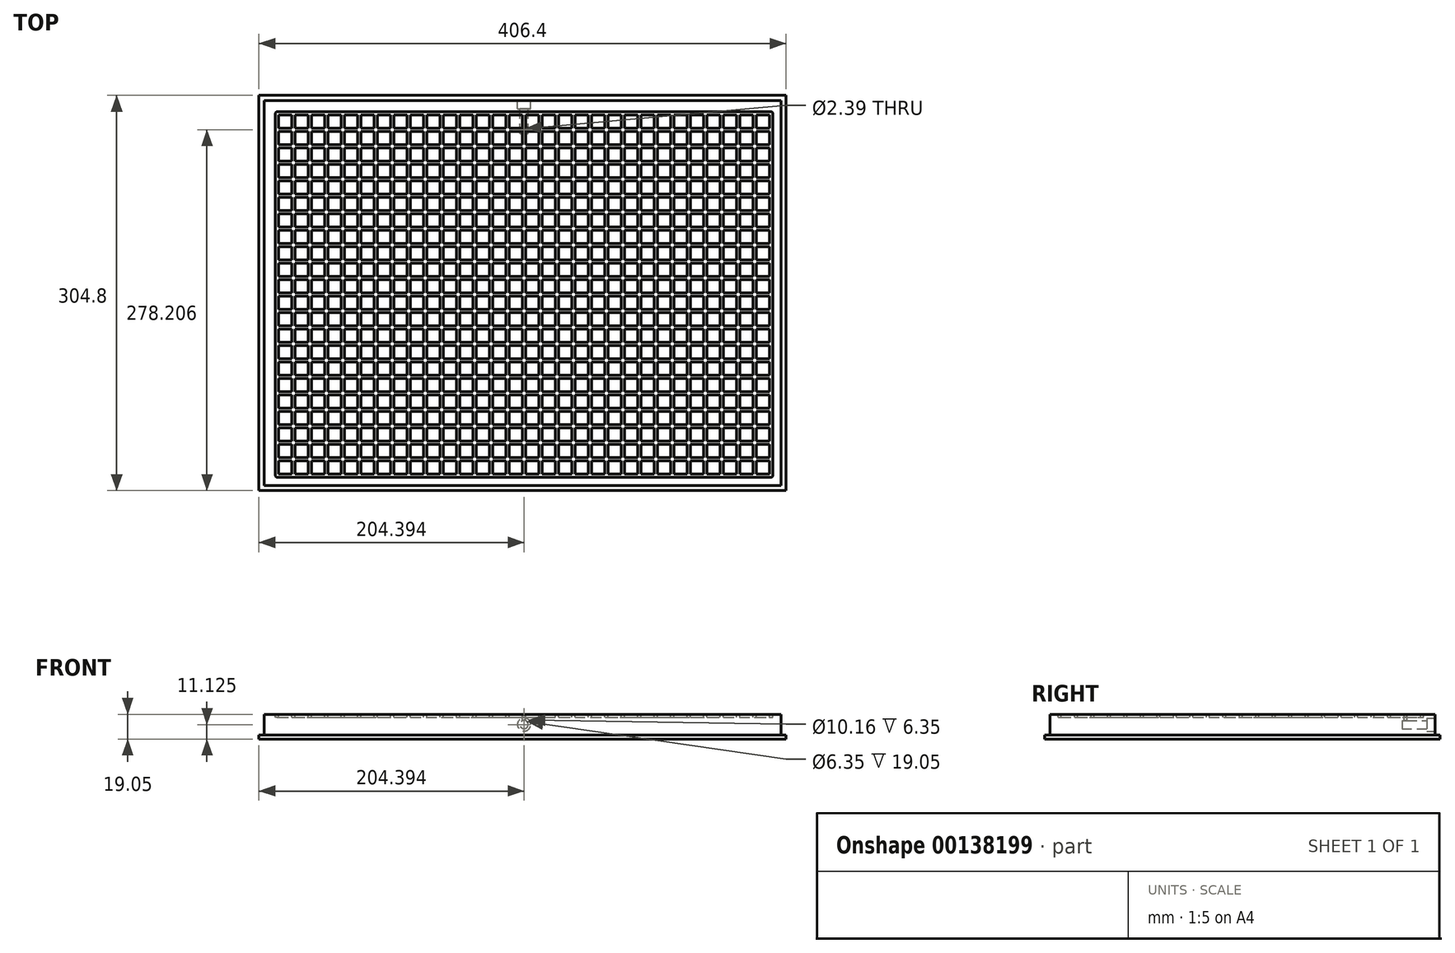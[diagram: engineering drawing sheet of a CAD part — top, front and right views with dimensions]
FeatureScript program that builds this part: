
annotation { "Feature Type Name" : "Feature", "Feature Type Description" : "" }
export const myFeature = defineFeature(function(context is Context, id is Id, definition is map)
    precondition{}
    {
        {
            var Q0;
            Q0=qCreatedBy(makeId("Top.planeOp"),FACE);
            var sketch = newSketch(context, id + "F0", { "sketchPlane" : qUnion([Q0])});
            skLineSegment(sketch, "E0.bottom", {"start": v(0, 0) * mm, "end": v(406.4, 0) * mm});
            skLineSegment(sketch, "E0.top", {"start": v(0, 304.8) * mm, "end": v(406.4, 304.8) * mm});
            skLineSegment(sketch, "E0.left", {"start": v(0, 0) * mm, "end": v(0, 304.8) * mm});
            skLineSegment(sketch, "E0.right", {"start": v(406.4, 0) * mm, "end": v(406.4, 304.8) * mm});
            skSolve(sketch);
        }
        {
            var Q0;
            Q0 = qSketchRegion(id + "F0", true);
            extrude(context, id + "F1", {"entities" : qUnion([Q0]), "depth" : 19.05 * mm});
        }
        {
            var Q0;
            Q0=makeQuery(id+"F1.opExtrude","CAP_FACE",FACE,{"disambiguationData":[OSD([sQuery(id+"F0.wireOp",EDGE,"E0.bottom"),sQuery(id+"F0.wireOp",EDGE,"E0.top"),sQuery(id+"F0.wireOp",EDGE,"E0.left"),sQuery(id+"F0.wireOp",EDGE,"E0.right")])],"isStart":false});
            var sketch = newSketch(context, id + "F2", { "sketchPlane" : qUnion([Q0])});
            skLineSegment(sketch, "E1.bottom", {"start": v(13.9, 10.31) * mm, "end": v(394.9, 10.31) * mm});
            skLineSegment(sketch, "E1.top", {"start": v(13.9, 292.1) * mm, "end": v(394.9, 292.1) * mm});
            skLineSegment(sketch, "E1.left", {"start": v(12.7, 11.5) * mm, "end": v(12.7, 290.9) * mm});
            skLineSegment(sketch, "E1.right", {"start": v(396.09, 11.5) * mm, "end": v(396.09, 290.9) * mm});
            skLineSegment(sketch, "E2.bottom", {"start": v(15.09, 12.7) * mm, "end": v(25.4, 12.7) * mm});
            skLineSegment(sketch, "E2.top", {"start": v(15.09, 23.01) * mm, "end": v(25.4, 23.01) * mm});
            skLineSegment(sketch, "E2.left", {"start": v(15.09, 12.7) * mm, "end": v(15.09, 23.01) * mm});
            skLineSegment(sketch, "E2.right", {"start": v(25.4, 12.7) * mm, "end": v(25.4, 23.01) * mm});
            skLineSegment(sketch, "E3.0.1.0", {"start": v(15.09, 25.4) * mm, "end": v(15.09, 35.71) * mm});
            skLineSegment(sketch, "E3.0.1.1", {"start": v(15.09, 35.71) * mm, "end": v(25.4, 35.71) * mm});
            skLineSegment(sketch, "E3.0.1.2", {"start": v(15.09, 25.4) * mm, "end": v(25.4, 25.4) * mm});
            skLineSegment(sketch, "E3.0.1.3", {"start": v(25.4, 25.4) * mm, "end": v(25.4, 35.71) * mm});
            skLineSegment(sketch, "E3.0.2.0", {"start": v(15.09, 38.1) * mm, "end": v(15.09, 48.41) * mm});
            skLineSegment(sketch, "E3.0.2.1", {"start": v(15.09, 48.41) * mm, "end": v(25.4, 48.41) * mm});
            skLineSegment(sketch, "E3.0.2.2", {"start": v(15.09, 38.1) * mm, "end": v(25.4, 38.1) * mm});
            skLineSegment(sketch, "E3.0.2.3", {"start": v(25.4, 38.1) * mm, "end": v(25.4, 48.41) * mm});
            skLineSegment(sketch, "E3.0.3.0", {"start": v(15.09, 50.8) * mm, "end": v(15.09, 61.11) * mm});
            skLineSegment(sketch, "E3.0.3.1", {"start": v(15.09, 61.11) * mm, "end": v(25.4, 61.11) * mm});
            skLineSegment(sketch, "E3.0.3.2", {"start": v(15.09, 50.8) * mm, "end": v(25.4, 50.8) * mm});
            skLineSegment(sketch, "E3.0.3.3", {"start": v(25.4, 50.8) * mm, "end": v(25.4, 61.11) * mm});
            skLineSegment(sketch, "E3.0.4.0", {"start": v(15.09, 63.5) * mm, "end": v(15.09, 73.81) * mm});
            skLineSegment(sketch, "E3.0.4.1", {"start": v(15.09, 73.81) * mm, "end": v(25.4, 73.81) * mm});
            skLineSegment(sketch, "E3.0.4.2", {"start": v(15.09, 63.5) * mm, "end": v(25.4, 63.5) * mm});
            skLineSegment(sketch, "E3.0.4.3", {"start": v(25.4, 63.5) * mm, "end": v(25.4, 73.81) * mm});
            skLineSegment(sketch, "E3.0.5.0", {"start": v(15.09, 76.2) * mm, "end": v(15.09, 86.51) * mm});
            skLineSegment(sketch, "E3.0.5.1", {"start": v(15.09, 86.51) * mm, "end": v(25.4, 86.51) * mm});
            skLineSegment(sketch, "E3.0.5.2", {"start": v(15.09, 76.2) * mm, "end": v(25.4, 76.2) * mm});
            skLineSegment(sketch, "E3.0.5.3", {"start": v(25.4, 76.2) * mm, "end": v(25.4, 86.51) * mm});
            skLineSegment(sketch, "E3.0.6.0", {"start": v(15.09, 88.9) * mm, "end": v(15.09, 99.21) * mm});
            skLineSegment(sketch, "E3.0.6.1", {"start": v(15.09, 99.21) * mm, "end": v(25.4, 99.21) * mm});
            skLineSegment(sketch, "E3.0.6.2", {"start": v(15.09, 88.9) * mm, "end": v(25.4, 88.9) * mm});
            skLineSegment(sketch, "E3.0.6.3", {"start": v(25.4, 88.9) * mm, "end": v(25.4, 99.21) * mm});
            skLineSegment(sketch, "E3.0.7.0", {"start": v(15.09, 101.6) * mm, "end": v(15.09, 111.91) * mm});
            skLineSegment(sketch, "E3.0.7.1", {"start": v(15.09, 111.91) * mm, "end": v(25.4, 111.91) * mm});
            skLineSegment(sketch, "E3.0.7.2", {"start": v(15.09, 101.6) * mm, "end": v(25.4, 101.6) * mm});
            skLineSegment(sketch, "E3.0.7.3", {"start": v(25.4, 101.6) * mm, "end": v(25.4, 111.91) * mm});
            skLineSegment(sketch, "E3.0.8.0", {"start": v(15.09, 114.3) * mm, "end": v(15.09, 124.61) * mm});
            skLineSegment(sketch, "E3.0.8.1", {"start": v(15.09, 124.61) * mm, "end": v(25.4, 124.61) * mm});
            skLineSegment(sketch, "E3.0.8.2", {"start": v(15.09, 114.3) * mm, "end": v(25.4, 114.3) * mm});
            skLineSegment(sketch, "E3.0.8.3", {"start": v(25.4, 114.3) * mm, "end": v(25.4, 124.61) * mm});
            skLineSegment(sketch, "E3.0.9.0", {"start": v(15.09, 127) * mm, "end": v(15.09, 137.31) * mm});
            skLineSegment(sketch, "E3.0.9.1", {"start": v(15.09, 137.31) * mm, "end": v(25.4, 137.31) * mm});
            skLineSegment(sketch, "E3.0.9.2", {"start": v(15.09, 127) * mm, "end": v(25.4, 127) * mm});
            skLineSegment(sketch, "E3.0.9.3", {"start": v(25.4, 127) * mm, "end": v(25.4, 137.31) * mm});
            skLineSegment(sketch, "E3.0.10.0", {"start": v(15.09, 139.7) * mm, "end": v(15.09, 150.01) * mm});
            skLineSegment(sketch, "E3.0.10.1", {"start": v(15.09, 150.01) * mm, "end": v(25.4, 150.01) * mm});
            skLineSegment(sketch, "E3.0.10.2", {"start": v(15.09, 139.7) * mm, "end": v(25.4, 139.7) * mm});
            skLineSegment(sketch, "E3.0.10.3", {"start": v(25.4, 139.7) * mm, "end": v(25.4, 150.01) * mm});
            skLineSegment(sketch, "E3.0.11.0", {"start": v(15.09, 152.4) * mm, "end": v(15.09, 162.71) * mm});
            skLineSegment(sketch, "E3.0.11.1", {"start": v(15.09, 162.71) * mm, "end": v(25.4, 162.71) * mm});
            skLineSegment(sketch, "E3.0.11.2", {"start": v(15.09, 152.4) * mm, "end": v(25.4, 152.4) * mm});
            skLineSegment(sketch, "E3.0.11.3", {"start": v(25.4, 152.4) * mm, "end": v(25.4, 162.71) * mm});
            skLineSegment(sketch, "E3.0.12.0", {"start": v(15.09, 165.1) * mm, "end": v(15.09, 175.41) * mm});
            skLineSegment(sketch, "E3.0.12.1", {"start": v(15.09, 175.41) * mm, "end": v(25.4, 175.41) * mm});
            skLineSegment(sketch, "E3.0.12.2", {"start": v(15.09, 165.1) * mm, "end": v(25.4, 165.1) * mm});
            skLineSegment(sketch, "E3.0.12.3", {"start": v(25.4, 165.1) * mm, "end": v(25.4, 175.41) * mm});
            skLineSegment(sketch, "E3.0.13.0", {"start": v(15.09, 177.8) * mm, "end": v(15.09, 188.11) * mm});
            skLineSegment(sketch, "E3.0.13.1", {"start": v(15.09, 188.11) * mm, "end": v(25.4, 188.11) * mm});
            skLineSegment(sketch, "E3.0.13.2", {"start": v(15.09, 177.8) * mm, "end": v(25.4, 177.8) * mm});
            skLineSegment(sketch, "E3.0.13.3", {"start": v(25.4, 177.8) * mm, "end": v(25.4, 188.11) * mm});
            skLineSegment(sketch, "E3.0.14.0", {"start": v(15.09, 190.5) * mm, "end": v(15.09, 200.81) * mm});
            skLineSegment(sketch, "E3.0.14.1", {"start": v(15.09, 200.81) * mm, "end": v(25.4, 200.81) * mm});
            skLineSegment(sketch, "E3.0.14.2", {"start": v(15.09, 190.5) * mm, "end": v(25.4, 190.5) * mm});
            skLineSegment(sketch, "E3.0.14.3", {"start": v(25.4, 190.5) * mm, "end": v(25.4, 200.81) * mm});
            skLineSegment(sketch, "E3.0.15.0", {"start": v(15.09, 203.2) * mm, "end": v(15.09, 213.51) * mm});
            skLineSegment(sketch, "E3.0.15.1", {"start": v(15.09, 213.51) * mm, "end": v(25.4, 213.51) * mm});
            skLineSegment(sketch, "E3.0.15.2", {"start": v(15.09, 203.2) * mm, "end": v(25.4, 203.2) * mm});
            skLineSegment(sketch, "E3.0.15.3", {"start": v(25.4, 203.2) * mm, "end": v(25.4, 213.51) * mm});
            skLineSegment(sketch, "E3.0.16.0", {"start": v(15.09, 215.9) * mm, "end": v(15.09, 226.21) * mm});
            skLineSegment(sketch, "E3.0.16.1", {"start": v(15.09, 226.21) * mm, "end": v(25.4, 226.21) * mm});
            skLineSegment(sketch, "E3.0.16.2", {"start": v(15.09, 215.9) * mm, "end": v(25.4, 215.9) * mm});
            skLineSegment(sketch, "E3.0.16.3", {"start": v(25.4, 215.9) * mm, "end": v(25.4, 226.21) * mm});
            skLineSegment(sketch, "E3.0.17.0", {"start": v(15.09, 228.6) * mm, "end": v(15.09, 238.91) * mm});
            skLineSegment(sketch, "E3.0.17.1", {"start": v(15.09, 238.91) * mm, "end": v(25.4, 238.91) * mm});
            skLineSegment(sketch, "E3.0.17.2", {"start": v(15.09, 228.6) * mm, "end": v(25.4, 228.6) * mm});
            skLineSegment(sketch, "E3.0.17.3", {"start": v(25.4, 228.6) * mm, "end": v(25.4, 238.91) * mm});
            skLineSegment(sketch, "E3.0.18.0", {"start": v(15.09, 241.3) * mm, "end": v(15.09, 251.61) * mm});
            skLineSegment(sketch, "E3.0.18.1", {"start": v(15.09, 251.61) * mm, "end": v(25.4, 251.61) * mm});
            skLineSegment(sketch, "E3.0.18.2", {"start": v(15.09, 241.3) * mm, "end": v(25.4, 241.3) * mm});
            skLineSegment(sketch, "E3.0.18.3", {"start": v(25.4, 241.3) * mm, "end": v(25.4, 251.61) * mm});
            skLineSegment(sketch, "E3.0.19.0", {"start": v(15.09, 254) * mm, "end": v(15.09, 264.31) * mm});
            skLineSegment(sketch, "E3.0.19.1", {"start": v(15.09, 264.31) * mm, "end": v(25.4, 264.31) * mm});
            skLineSegment(sketch, "E3.0.19.2", {"start": v(15.09, 254) * mm, "end": v(25.4, 254) * mm});
            skLineSegment(sketch, "E3.0.19.3", {"start": v(25.4, 254) * mm, "end": v(25.4, 264.31) * mm});
            skLineSegment(sketch, "E3.0.20.0", {"start": v(15.09, 266.7) * mm, "end": v(15.09, 277.01) * mm});
            skLineSegment(sketch, "E3.0.20.1", {"start": v(15.09, 277.01) * mm, "end": v(25.4, 277.01) * mm});
            skLineSegment(sketch, "E3.0.20.2", {"start": v(15.09, 266.7) * mm, "end": v(25.4, 266.7) * mm});
            skLineSegment(sketch, "E3.0.20.3", {"start": v(25.4, 266.7) * mm, "end": v(25.4, 277.01) * mm});
            skLineSegment(sketch, "E3.0.21.0", {"start": v(15.09, 279.4) * mm, "end": v(15.09, 289.71) * mm});
            skLineSegment(sketch, "E3.0.21.1", {"start": v(15.09, 289.71) * mm, "end": v(25.4, 289.71) * mm});
            skLineSegment(sketch, "E3.0.21.2", {"start": v(15.09, 279.4) * mm, "end": v(25.4, 279.4) * mm});
            skLineSegment(sketch, "E3.0.21.3", {"start": v(25.4, 279.4) * mm, "end": v(25.4, 289.71) * mm});
            skLineSegment(sketch, "E3.1.0.0", {"start": v(27.79, 12.7) * mm, "end": v(27.79, 23.01) * mm});
            skLineSegment(sketch, "E3.1.0.1", {"start": v(27.79, 23.01) * mm, "end": v(38.1, 23.01) * mm});
            skLineSegment(sketch, "E3.1.0.2", {"start": v(27.79, 12.7) * mm, "end": v(38.1, 12.7) * mm});
            skLineSegment(sketch, "E3.1.0.3", {"start": v(38.1, 12.7) * mm, "end": v(38.1, 23.01) * mm});
            skLineSegment(sketch, "E3.1.1.0", {"start": v(27.79, 25.4) * mm, "end": v(27.79, 35.71) * mm});
            skLineSegment(sketch, "E3.1.1.1", {"start": v(27.79, 35.71) * mm, "end": v(38.1, 35.71) * mm});
            skLineSegment(sketch, "E3.1.1.2", {"start": v(27.79, 25.4) * mm, "end": v(38.1, 25.4) * mm});
            skLineSegment(sketch, "E3.1.1.3", {"start": v(38.1, 25.4) * mm, "end": v(38.1, 35.71) * mm});
            skLineSegment(sketch, "E3.1.2.0", {"start": v(27.79, 38.1) * mm, "end": v(27.79, 48.41) * mm});
            skLineSegment(sketch, "E3.1.2.1", {"start": v(27.79, 48.41) * mm, "end": v(38.1, 48.41) * mm});
            skLineSegment(sketch, "E3.1.2.2", {"start": v(27.79, 38.1) * mm, "end": v(38.1, 38.1) * mm});
            skLineSegment(sketch, "E3.1.2.3", {"start": v(38.1, 38.1) * mm, "end": v(38.1, 48.41) * mm});
            skLineSegment(sketch, "E3.1.3.0", {"start": v(27.79, 50.8) * mm, "end": v(27.79, 61.11) * mm});
            skLineSegment(sketch, "E3.1.3.1", {"start": v(27.79, 61.11) * mm, "end": v(38.1, 61.11) * mm});
            skLineSegment(sketch, "E3.1.3.2", {"start": v(27.79, 50.8) * mm, "end": v(38.1, 50.8) * mm});
            skLineSegment(sketch, "E3.1.3.3", {"start": v(38.1, 50.8) * mm, "end": v(38.1, 61.11) * mm});
            skLineSegment(sketch, "E3.1.4.0", {"start": v(27.79, 63.5) * mm, "end": v(27.79, 73.81) * mm});
            skLineSegment(sketch, "E3.1.4.1", {"start": v(27.79, 73.81) * mm, "end": v(38.1, 73.81) * mm});
            skLineSegment(sketch, "E3.1.4.2", {"start": v(27.79, 63.5) * mm, "end": v(38.1, 63.5) * mm});
            skLineSegment(sketch, "E3.1.4.3", {"start": v(38.1, 63.5) * mm, "end": v(38.1, 73.81) * mm});
            skLineSegment(sketch, "E3.1.5.0", {"start": v(27.79, 76.2) * mm, "end": v(27.79, 86.51) * mm});
            skLineSegment(sketch, "E3.1.5.1", {"start": v(27.79, 86.51) * mm, "end": v(38.1, 86.51) * mm});
            skLineSegment(sketch, "E3.1.5.2", {"start": v(27.79, 76.2) * mm, "end": v(38.1, 76.2) * mm});
            skLineSegment(sketch, "E3.1.5.3", {"start": v(38.1, 76.2) * mm, "end": v(38.1, 86.51) * mm});
            skLineSegment(sketch, "E3.1.6.0", {"start": v(27.79, 88.9) * mm, "end": v(27.79, 99.21) * mm});
            skLineSegment(sketch, "E3.1.6.1", {"start": v(27.79, 99.21) * mm, "end": v(38.1, 99.21) * mm});
            skLineSegment(sketch, "E3.1.6.2", {"start": v(27.79, 88.9) * mm, "end": v(38.1, 88.9) * mm});
            skLineSegment(sketch, "E3.1.6.3", {"start": v(38.1, 88.9) * mm, "end": v(38.1, 99.21) * mm});
            skLineSegment(sketch, "E3.1.7.0", {"start": v(27.79, 101.6) * mm, "end": v(27.79, 111.91) * mm});
            skLineSegment(sketch, "E3.1.7.1", {"start": v(27.79, 111.91) * mm, "end": v(38.1, 111.91) * mm});
            skLineSegment(sketch, "E3.1.7.2", {"start": v(27.79, 101.6) * mm, "end": v(38.1, 101.6) * mm});
            skLineSegment(sketch, "E3.1.7.3", {"start": v(38.1, 101.6) * mm, "end": v(38.1, 111.91) * mm});
            skLineSegment(sketch, "E3.1.8.0", {"start": v(27.79, 114.3) * mm, "end": v(27.79, 124.61) * mm});
            skLineSegment(sketch, "E3.1.8.1", {"start": v(27.79, 124.61) * mm, "end": v(38.1, 124.61) * mm});
            skLineSegment(sketch, "E3.1.8.2", {"start": v(27.79, 114.3) * mm, "end": v(38.1, 114.3) * mm});
            skLineSegment(sketch, "E3.1.8.3", {"start": v(38.1, 114.3) * mm, "end": v(38.1, 124.61) * mm});
            skLineSegment(sketch, "E3.1.9.0", {"start": v(27.79, 127) * mm, "end": v(27.79, 137.31) * mm});
            skLineSegment(sketch, "E3.1.9.1", {"start": v(27.79, 137.31) * mm, "end": v(38.1, 137.31) * mm});
            skLineSegment(sketch, "E3.1.9.2", {"start": v(27.79, 127) * mm, "end": v(38.1, 127) * mm});
            skLineSegment(sketch, "E3.1.9.3", {"start": v(38.1, 127) * mm, "end": v(38.1, 137.31) * mm});
            skLineSegment(sketch, "E3.1.10.0", {"start": v(27.79, 139.7) * mm, "end": v(27.79, 150.01) * mm});
            skLineSegment(sketch, "E3.1.10.1", {"start": v(27.79, 150.01) * mm, "end": v(38.1, 150.01) * mm});
            skLineSegment(sketch, "E3.1.10.2", {"start": v(27.79, 139.7) * mm, "end": v(38.1, 139.7) * mm});
            skLineSegment(sketch, "E3.1.10.3", {"start": v(38.1, 139.7) * mm, "end": v(38.1, 150.01) * mm});
            skLineSegment(sketch, "E3.1.11.0", {"start": v(27.79, 152.4) * mm, "end": v(27.79, 162.71) * mm});
            skLineSegment(sketch, "E3.1.11.1", {"start": v(27.79, 162.71) * mm, "end": v(38.1, 162.71) * mm});
            skLineSegment(sketch, "E3.1.11.2", {"start": v(27.79, 152.4) * mm, "end": v(38.1, 152.4) * mm});
            skLineSegment(sketch, "E3.1.11.3", {"start": v(38.1, 152.4) * mm, "end": v(38.1, 162.71) * mm});
            skLineSegment(sketch, "E3.1.12.0", {"start": v(27.79, 165.1) * mm, "end": v(27.79, 175.41) * mm});
            skLineSegment(sketch, "E3.1.12.1", {"start": v(27.79, 175.41) * mm, "end": v(38.1, 175.41) * mm});
            skLineSegment(sketch, "E3.1.12.2", {"start": v(27.79, 165.1) * mm, "end": v(38.1, 165.1) * mm});
            skLineSegment(sketch, "E3.1.12.3", {"start": v(38.1, 165.1) * mm, "end": v(38.1, 175.41) * mm});
            skLineSegment(sketch, "E3.1.13.0", {"start": v(27.79, 177.8) * mm, "end": v(27.79, 188.11) * mm});
            skLineSegment(sketch, "E3.1.13.1", {"start": v(27.79, 188.11) * mm, "end": v(38.1, 188.11) * mm});
            skLineSegment(sketch, "E3.1.13.2", {"start": v(27.79, 177.8) * mm, "end": v(38.1, 177.8) * mm});
            skLineSegment(sketch, "E3.1.13.3", {"start": v(38.1, 177.8) * mm, "end": v(38.1, 188.11) * mm});
            skLineSegment(sketch, "E3.1.14.0", {"start": v(27.79, 190.5) * mm, "end": v(27.79, 200.81) * mm});
            skLineSegment(sketch, "E3.1.14.1", {"start": v(27.79, 200.81) * mm, "end": v(38.1, 200.81) * mm});
            skLineSegment(sketch, "E3.1.14.2", {"start": v(27.79, 190.5) * mm, "end": v(38.1, 190.5) * mm});
            skLineSegment(sketch, "E3.1.14.3", {"start": v(38.1, 190.5) * mm, "end": v(38.1, 200.81) * mm});
            skLineSegment(sketch, "E3.1.15.0", {"start": v(27.79, 203.2) * mm, "end": v(27.79, 213.51) * mm});
            skLineSegment(sketch, "E3.1.15.1", {"start": v(27.79, 213.51) * mm, "end": v(38.1, 213.51) * mm});
            skLineSegment(sketch, "E3.1.15.2", {"start": v(27.79, 203.2) * mm, "end": v(38.1, 203.2) * mm});
            skLineSegment(sketch, "E3.1.15.3", {"start": v(38.1, 203.2) * mm, "end": v(38.1, 213.51) * mm});
            skLineSegment(sketch, "E3.1.16.0", {"start": v(27.79, 215.9) * mm, "end": v(27.79, 226.21) * mm});
            skLineSegment(sketch, "E3.1.16.1", {"start": v(27.79, 226.21) * mm, "end": v(38.1, 226.21) * mm});
            skLineSegment(sketch, "E3.1.16.2", {"start": v(27.79, 215.9) * mm, "end": v(38.1, 215.9) * mm});
            skLineSegment(sketch, "E3.1.16.3", {"start": v(38.1, 215.9) * mm, "end": v(38.1, 226.21) * mm});
            skLineSegment(sketch, "E3.1.17.0", {"start": v(27.79, 228.6) * mm, "end": v(27.79, 238.91) * mm});
            skLineSegment(sketch, "E3.1.17.1", {"start": v(27.79, 238.91) * mm, "end": v(38.1, 238.91) * mm});
            skLineSegment(sketch, "E3.1.17.2", {"start": v(27.79, 228.6) * mm, "end": v(38.1, 228.6) * mm});
            skLineSegment(sketch, "E3.1.17.3", {"start": v(38.1, 228.6) * mm, "end": v(38.1, 238.91) * mm});
            skLineSegment(sketch, "E3.1.18.0", {"start": v(27.79, 241.3) * mm, "end": v(27.79, 251.61) * mm});
            skLineSegment(sketch, "E3.1.18.1", {"start": v(27.79, 251.61) * mm, "end": v(38.1, 251.61) * mm});
            skLineSegment(sketch, "E3.1.18.2", {"start": v(27.79, 241.3) * mm, "end": v(38.1, 241.3) * mm});
            skLineSegment(sketch, "E3.1.18.3", {"start": v(38.1, 241.3) * mm, "end": v(38.1, 251.61) * mm});
            skLineSegment(sketch, "E3.1.19.0", {"start": v(27.79, 254) * mm, "end": v(27.79, 264.31) * mm});
            skLineSegment(sketch, "E3.1.19.1", {"start": v(27.79, 264.31) * mm, "end": v(38.1, 264.31) * mm});
            skLineSegment(sketch, "E3.1.19.2", {"start": v(27.79, 254) * mm, "end": v(38.1, 254) * mm});
            skLineSegment(sketch, "E3.1.19.3", {"start": v(38.1, 254) * mm, "end": v(38.1, 264.31) * mm});
            skLineSegment(sketch, "E3.1.20.0", {"start": v(27.79, 266.7) * mm, "end": v(27.79, 277.01) * mm});
            skLineSegment(sketch, "E3.1.20.1", {"start": v(27.79, 277.01) * mm, "end": v(38.1, 277.01) * mm});
            skLineSegment(sketch, "E3.1.20.2", {"start": v(27.79, 266.7) * mm, "end": v(38.1, 266.7) * mm});
            skLineSegment(sketch, "E3.1.20.3", {"start": v(38.1, 266.7) * mm, "end": v(38.1, 277.01) * mm});
            skLineSegment(sketch, "E3.1.21.0", {"start": v(27.79, 279.4) * mm, "end": v(27.79, 289.71) * mm});
            skLineSegment(sketch, "E3.1.21.1", {"start": v(27.79, 289.71) * mm, "end": v(38.1, 289.71) * mm});
            skLineSegment(sketch, "E3.1.21.2", {"start": v(27.79, 279.4) * mm, "end": v(38.1, 279.4) * mm});
            skLineSegment(sketch, "E3.1.21.3", {"start": v(38.1, 279.4) * mm, "end": v(38.1, 289.71) * mm});
            skLineSegment(sketch, "E3.2.0.0", {"start": v(40.49, 12.7) * mm, "end": v(40.49, 23.01) * mm});
            skLineSegment(sketch, "E3.2.0.1", {"start": v(40.49, 23.01) * mm, "end": v(50.8, 23.01) * mm});
            skLineSegment(sketch, "E3.2.0.2", {"start": v(40.49, 12.7) * mm, "end": v(50.8, 12.7) * mm});
            skLineSegment(sketch, "E3.2.0.3", {"start": v(50.8, 12.7) * mm, "end": v(50.8, 23.01) * mm});
            skLineSegment(sketch, "E3.2.1.0", {"start": v(40.49, 25.4) * mm, "end": v(40.49, 35.71) * mm});
            skLineSegment(sketch, "E3.2.1.1", {"start": v(40.49, 35.71) * mm, "end": v(50.8, 35.71) * mm});
            skLineSegment(sketch, "E3.2.1.2", {"start": v(40.49, 25.4) * mm, "end": v(50.8, 25.4) * mm});
            skLineSegment(sketch, "E3.2.1.3", {"start": v(50.8, 25.4) * mm, "end": v(50.8, 35.71) * mm});
            skLineSegment(sketch, "E3.2.2.0", {"start": v(40.49, 38.1) * mm, "end": v(40.49, 48.41) * mm});
            skLineSegment(sketch, "E3.2.2.1", {"start": v(40.49, 48.41) * mm, "end": v(50.8, 48.41) * mm});
            skLineSegment(sketch, "E3.2.2.2", {"start": v(40.49, 38.1) * mm, "end": v(50.8, 38.1) * mm});
            skLineSegment(sketch, "E3.2.2.3", {"start": v(50.8, 38.1) * mm, "end": v(50.8, 48.41) * mm});
            skLineSegment(sketch, "E3.2.3.0", {"start": v(40.49, 50.8) * mm, "end": v(40.49, 61.11) * mm});
            skLineSegment(sketch, "E3.2.3.1", {"start": v(40.49, 61.11) * mm, "end": v(50.8, 61.11) * mm});
            skLineSegment(sketch, "E3.2.3.2", {"start": v(40.49, 50.8) * mm, "end": v(50.8, 50.8) * mm});
            skLineSegment(sketch, "E3.2.3.3", {"start": v(50.8, 50.8) * mm, "end": v(50.8, 61.11) * mm});
            skLineSegment(sketch, "E3.2.4.0", {"start": v(40.49, 63.5) * mm, "end": v(40.49, 73.81) * mm});
            skLineSegment(sketch, "E3.2.4.1", {"start": v(40.49, 73.81) * mm, "end": v(50.8, 73.81) * mm});
            skLineSegment(sketch, "E3.2.4.2", {"start": v(40.49, 63.5) * mm, "end": v(50.8, 63.5) * mm});
            skLineSegment(sketch, "E3.2.4.3", {"start": v(50.8, 63.5) * mm, "end": v(50.8, 73.81) * mm});
            skLineSegment(sketch, "E3.2.5.0", {"start": v(40.49, 76.2) * mm, "end": v(40.49, 86.51) * mm});
            skLineSegment(sketch, "E3.2.5.1", {"start": v(40.49, 86.51) * mm, "end": v(50.8, 86.51) * mm});
            skLineSegment(sketch, "E3.2.5.2", {"start": v(40.49, 76.2) * mm, "end": v(50.8, 76.2) * mm});
            skLineSegment(sketch, "E3.2.5.3", {"start": v(50.8, 76.2) * mm, "end": v(50.8, 86.51) * mm});
            skLineSegment(sketch, "E3.2.6.0", {"start": v(40.49, 88.9) * mm, "end": v(40.49, 99.21) * mm});
            skLineSegment(sketch, "E3.2.6.1", {"start": v(40.49, 99.21) * mm, "end": v(50.8, 99.21) * mm});
            skLineSegment(sketch, "E3.2.6.2", {"start": v(40.49, 88.9) * mm, "end": v(50.8, 88.9) * mm});
            skLineSegment(sketch, "E3.2.6.3", {"start": v(50.8, 88.9) * mm, "end": v(50.8, 99.21) * mm});
            skLineSegment(sketch, "E3.2.7.0", {"start": v(40.49, 101.6) * mm, "end": v(40.49, 111.91) * mm});
            skLineSegment(sketch, "E3.2.7.1", {"start": v(40.49, 111.91) * mm, "end": v(50.8, 111.91) * mm});
            skLineSegment(sketch, "E3.2.7.2", {"start": v(40.49, 101.6) * mm, "end": v(50.8, 101.6) * mm});
            skLineSegment(sketch, "E3.2.7.3", {"start": v(50.8, 101.6) * mm, "end": v(50.8, 111.91) * mm});
            skLineSegment(sketch, "E3.2.8.0", {"start": v(40.49, 114.3) * mm, "end": v(40.49, 124.61) * mm});
            skLineSegment(sketch, "E3.2.8.1", {"start": v(40.49, 124.61) * mm, "end": v(50.8, 124.61) * mm});
            skLineSegment(sketch, "E3.2.8.2", {"start": v(40.49, 114.3) * mm, "end": v(50.8, 114.3) * mm});
            skLineSegment(sketch, "E3.2.8.3", {"start": v(50.8, 114.3) * mm, "end": v(50.8, 124.61) * mm});
            skLineSegment(sketch, "E3.2.9.0", {"start": v(40.49, 127) * mm, "end": v(40.49, 137.31) * mm});
            skLineSegment(sketch, "E3.2.9.1", {"start": v(40.49, 137.31) * mm, "end": v(50.8, 137.31) * mm});
            skLineSegment(sketch, "E3.2.9.2", {"start": v(40.49, 127) * mm, "end": v(50.8, 127) * mm});
            skLineSegment(sketch, "E3.2.9.3", {"start": v(50.8, 127) * mm, "end": v(50.8, 137.31) * mm});
            skLineSegment(sketch, "E3.2.10.0", {"start": v(40.49, 139.7) * mm, "end": v(40.49, 150.01) * mm});
            skLineSegment(sketch, "E3.2.10.1", {"start": v(40.49, 150.01) * mm, "end": v(50.8, 150.01) * mm});
            skLineSegment(sketch, "E3.2.10.2", {"start": v(40.49, 139.7) * mm, "end": v(50.8, 139.7) * mm});
            skLineSegment(sketch, "E3.2.10.3", {"start": v(50.8, 139.7) * mm, "end": v(50.8, 150.01) * mm});
            skLineSegment(sketch, "E3.2.11.0", {"start": v(40.49, 152.4) * mm, "end": v(40.49, 162.71) * mm});
            skLineSegment(sketch, "E3.2.11.1", {"start": v(40.49, 162.71) * mm, "end": v(50.8, 162.71) * mm});
            skLineSegment(sketch, "E3.2.11.2", {"start": v(40.49, 152.4) * mm, "end": v(50.8, 152.4) * mm});
            skLineSegment(sketch, "E3.2.11.3", {"start": v(50.8, 152.4) * mm, "end": v(50.8, 162.71) * mm});
            skLineSegment(sketch, "E3.2.12.0", {"start": v(40.49, 165.1) * mm, "end": v(40.49, 175.41) * mm});
            skLineSegment(sketch, "E3.2.12.1", {"start": v(40.49, 175.41) * mm, "end": v(50.8, 175.41) * mm});
            skLineSegment(sketch, "E3.2.12.2", {"start": v(40.49, 165.1) * mm, "end": v(50.8, 165.1) * mm});
            skLineSegment(sketch, "E3.2.12.3", {"start": v(50.8, 165.1) * mm, "end": v(50.8, 175.41) * mm});
            skLineSegment(sketch, "E3.2.13.0", {"start": v(40.49, 177.8) * mm, "end": v(40.49, 188.11) * mm});
            skLineSegment(sketch, "E3.2.13.1", {"start": v(40.49, 188.11) * mm, "end": v(50.8, 188.11) * mm});
            skLineSegment(sketch, "E3.2.13.2", {"start": v(40.49, 177.8) * mm, "end": v(50.8, 177.8) * mm});
            skLineSegment(sketch, "E3.2.13.3", {"start": v(50.8, 177.8) * mm, "end": v(50.8, 188.11) * mm});
            skLineSegment(sketch, "E3.2.14.0", {"start": v(40.49, 190.5) * mm, "end": v(40.49, 200.81) * mm});
            skLineSegment(sketch, "E3.2.14.1", {"start": v(40.49, 200.81) * mm, "end": v(50.8, 200.81) * mm});
            skLineSegment(sketch, "E3.2.14.2", {"start": v(40.49, 190.5) * mm, "end": v(50.8, 190.5) * mm});
            skLineSegment(sketch, "E3.2.14.3", {"start": v(50.8, 190.5) * mm, "end": v(50.8, 200.81) * mm});
            skLineSegment(sketch, "E3.2.15.0", {"start": v(40.49, 203.2) * mm, "end": v(40.49, 213.51) * mm});
            skLineSegment(sketch, "E3.2.15.1", {"start": v(40.49, 213.51) * mm, "end": v(50.8, 213.51) * mm});
            skLineSegment(sketch, "E3.2.15.2", {"start": v(40.49, 203.2) * mm, "end": v(50.8, 203.2) * mm});
            skLineSegment(sketch, "E3.2.15.3", {"start": v(50.8, 203.2) * mm, "end": v(50.8, 213.51) * mm});
            skLineSegment(sketch, "E3.2.16.0", {"start": v(40.49, 215.9) * mm, "end": v(40.49, 226.21) * mm});
            skLineSegment(sketch, "E3.2.16.1", {"start": v(40.49, 226.21) * mm, "end": v(50.8, 226.21) * mm});
            skLineSegment(sketch, "E3.2.16.2", {"start": v(40.49, 215.9) * mm, "end": v(50.8, 215.9) * mm});
            skLineSegment(sketch, "E3.2.16.3", {"start": v(50.8, 215.9) * mm, "end": v(50.8, 226.21) * mm});
            skLineSegment(sketch, "E3.2.17.0", {"start": v(40.49, 228.6) * mm, "end": v(40.49, 238.91) * mm});
            skLineSegment(sketch, "E3.2.17.1", {"start": v(40.49, 238.91) * mm, "end": v(50.8, 238.91) * mm});
            skLineSegment(sketch, "E3.2.17.2", {"start": v(40.49, 228.6) * mm, "end": v(50.8, 228.6) * mm});
            skLineSegment(sketch, "E3.2.17.3", {"start": v(50.8, 228.6) * mm, "end": v(50.8, 238.91) * mm});
            skLineSegment(sketch, "E3.2.18.0", {"start": v(40.49, 241.3) * mm, "end": v(40.49, 251.61) * mm});
            skLineSegment(sketch, "E3.2.18.1", {"start": v(40.49, 251.61) * mm, "end": v(50.8, 251.61) * mm});
            skLineSegment(sketch, "E3.2.18.2", {"start": v(40.49, 241.3) * mm, "end": v(50.8, 241.3) * mm});
            skLineSegment(sketch, "E3.2.18.3", {"start": v(50.8, 241.3) * mm, "end": v(50.8, 251.61) * mm});
            skLineSegment(sketch, "E3.2.19.0", {"start": v(40.49, 254) * mm, "end": v(40.49, 264.31) * mm});
            skLineSegment(sketch, "E3.2.19.1", {"start": v(40.49, 264.31) * mm, "end": v(50.8, 264.31) * mm});
            skLineSegment(sketch, "E3.2.19.2", {"start": v(40.49, 254) * mm, "end": v(50.8, 254) * mm});
            skLineSegment(sketch, "E3.2.19.3", {"start": v(50.8, 254) * mm, "end": v(50.8, 264.31) * mm});
            skLineSegment(sketch, "E3.2.20.0", {"start": v(40.49, 266.7) * mm, "end": v(40.49, 277.01) * mm});
            skLineSegment(sketch, "E3.2.20.1", {"start": v(40.49, 277.01) * mm, "end": v(50.8, 277.01) * mm});
            skLineSegment(sketch, "E3.2.20.2", {"start": v(40.49, 266.7) * mm, "end": v(50.8, 266.7) * mm});
            skLineSegment(sketch, "E3.2.20.3", {"start": v(50.8, 266.7) * mm, "end": v(50.8, 277.01) * mm});
            skLineSegment(sketch, "E3.2.21.0", {"start": v(40.49, 279.4) * mm, "end": v(40.49, 289.71) * mm});
            skLineSegment(sketch, "E3.2.21.1", {"start": v(40.49, 289.71) * mm, "end": v(50.8, 289.71) * mm});
            skLineSegment(sketch, "E3.2.21.2", {"start": v(40.49, 279.4) * mm, "end": v(50.8, 279.4) * mm});
            skLineSegment(sketch, "E3.2.21.3", {"start": v(50.8, 279.4) * mm, "end": v(50.8, 289.71) * mm});
            skLineSegment(sketch, "E3.3.0.0", {"start": v(53.19, 12.7) * mm, "end": v(53.19, 23.01) * mm});
            skLineSegment(sketch, "E3.3.0.1", {"start": v(53.19, 23.01) * mm, "end": v(63.5, 23.01) * mm});
            skLineSegment(sketch, "E3.3.0.2", {"start": v(53.19, 12.7) * mm, "end": v(63.5, 12.7) * mm});
            skLineSegment(sketch, "E3.3.0.3", {"start": v(63.5, 12.7) * mm, "end": v(63.5, 23.01) * mm});
            skLineSegment(sketch, "E3.3.1.0", {"start": v(53.19, 25.4) * mm, "end": v(53.19, 35.71) * mm});
            skLineSegment(sketch, "E3.3.1.1", {"start": v(53.19, 35.71) * mm, "end": v(63.5, 35.71) * mm});
            skLineSegment(sketch, "E3.3.1.2", {"start": v(53.19, 25.4) * mm, "end": v(63.5, 25.4) * mm});
            skLineSegment(sketch, "E3.3.1.3", {"start": v(63.5, 25.4) * mm, "end": v(63.5, 35.71) * mm});
            skLineSegment(sketch, "E3.3.2.0", {"start": v(53.19, 38.1) * mm, "end": v(53.19, 48.41) * mm});
            skLineSegment(sketch, "E3.3.2.1", {"start": v(53.19, 48.41) * mm, "end": v(63.5, 48.41) * mm});
            skLineSegment(sketch, "E3.3.2.2", {"start": v(53.19, 38.1) * mm, "end": v(63.5, 38.1) * mm});
            skLineSegment(sketch, "E3.3.2.3", {"start": v(63.5, 38.1) * mm, "end": v(63.5, 48.41) * mm});
            skLineSegment(sketch, "E3.3.3.0", {"start": v(53.19, 50.8) * mm, "end": v(53.19, 61.11) * mm});
            skLineSegment(sketch, "E3.3.3.1", {"start": v(53.19, 61.11) * mm, "end": v(63.5, 61.11) * mm});
            skLineSegment(sketch, "E3.3.3.2", {"start": v(53.19, 50.8) * mm, "end": v(63.5, 50.8) * mm});
            skLineSegment(sketch, "E3.3.3.3", {"start": v(63.5, 50.8) * mm, "end": v(63.5, 61.11) * mm});
            skLineSegment(sketch, "E3.3.4.0", {"start": v(53.19, 63.5) * mm, "end": v(53.19, 73.81) * mm});
            skLineSegment(sketch, "E3.3.4.1", {"start": v(53.19, 73.81) * mm, "end": v(63.5, 73.81) * mm});
            skLineSegment(sketch, "E3.3.4.2", {"start": v(53.19, 63.5) * mm, "end": v(63.5, 63.5) * mm});
            skLineSegment(sketch, "E3.3.4.3", {"start": v(63.5, 63.5) * mm, "end": v(63.5, 73.81) * mm});
            skLineSegment(sketch, "E3.3.5.0", {"start": v(53.19, 76.2) * mm, "end": v(53.19, 86.51) * mm});
            skLineSegment(sketch, "E3.3.5.1", {"start": v(53.19, 86.51) * mm, "end": v(63.5, 86.51) * mm});
            skLineSegment(sketch, "E3.3.5.2", {"start": v(53.19, 76.2) * mm, "end": v(63.5, 76.2) * mm});
            skLineSegment(sketch, "E3.3.5.3", {"start": v(63.5, 76.2) * mm, "end": v(63.5, 86.51) * mm});
            skLineSegment(sketch, "E3.3.6.0", {"start": v(53.19, 88.9) * mm, "end": v(53.19, 99.21) * mm});
            skLineSegment(sketch, "E3.3.6.1", {"start": v(53.19, 99.21) * mm, "end": v(63.5, 99.21) * mm});
            skLineSegment(sketch, "E3.3.6.2", {"start": v(53.19, 88.9) * mm, "end": v(63.5, 88.9) * mm});
            skLineSegment(sketch, "E3.3.6.3", {"start": v(63.5, 88.9) * mm, "end": v(63.5, 99.21) * mm});
            skLineSegment(sketch, "E3.3.7.0", {"start": v(53.19, 101.6) * mm, "end": v(53.19, 111.91) * mm});
            skLineSegment(sketch, "E3.3.7.1", {"start": v(53.19, 111.91) * mm, "end": v(63.5, 111.91) * mm});
            skLineSegment(sketch, "E3.3.7.2", {"start": v(53.19, 101.6) * mm, "end": v(63.5, 101.6) * mm});
            skLineSegment(sketch, "E3.3.7.3", {"start": v(63.5, 101.6) * mm, "end": v(63.5, 111.91) * mm});
            skLineSegment(sketch, "E3.3.8.0", {"start": v(53.19, 114.3) * mm, "end": v(53.19, 124.61) * mm});
            skLineSegment(sketch, "E3.3.8.1", {"start": v(53.19, 124.61) * mm, "end": v(63.5, 124.61) * mm});
            skLineSegment(sketch, "E3.3.8.2", {"start": v(53.19, 114.3) * mm, "end": v(63.5, 114.3) * mm});
            skLineSegment(sketch, "E3.3.8.3", {"start": v(63.5, 114.3) * mm, "end": v(63.5, 124.61) * mm});
            skLineSegment(sketch, "E3.3.9.0", {"start": v(53.19, 127) * mm, "end": v(53.19, 137.31) * mm});
            skLineSegment(sketch, "E3.3.9.1", {"start": v(53.19, 137.31) * mm, "end": v(63.5, 137.31) * mm});
            skLineSegment(sketch, "E3.3.9.2", {"start": v(53.19, 127) * mm, "end": v(63.5, 127) * mm});
            skLineSegment(sketch, "E3.3.9.3", {"start": v(63.5, 127) * mm, "end": v(63.5, 137.31) * mm});
            skLineSegment(sketch, "E3.3.10.0", {"start": v(53.19, 139.7) * mm, "end": v(53.19, 150.01) * mm});
            skLineSegment(sketch, "E3.3.10.1", {"start": v(53.19, 150.01) * mm, "end": v(63.5, 150.01) * mm});
            skLineSegment(sketch, "E3.3.10.2", {"start": v(53.19, 139.7) * mm, "end": v(63.5, 139.7) * mm});
            skLineSegment(sketch, "E3.3.10.3", {"start": v(63.5, 139.7) * mm, "end": v(63.5, 150.01) * mm});
            skLineSegment(sketch, "E3.3.11.0", {"start": v(53.19, 152.4) * mm, "end": v(53.19, 162.71) * mm});
            skLineSegment(sketch, "E3.3.11.1", {"start": v(53.19, 162.71) * mm, "end": v(63.5, 162.71) * mm});
            skLineSegment(sketch, "E3.3.11.2", {"start": v(53.19, 152.4) * mm, "end": v(63.5, 152.4) * mm});
            skLineSegment(sketch, "E3.3.11.3", {"start": v(63.5, 152.4) * mm, "end": v(63.5, 162.71) * mm});
            skLineSegment(sketch, "E3.3.12.0", {"start": v(53.19, 165.1) * mm, "end": v(53.19, 175.41) * mm});
            skLineSegment(sketch, "E3.3.12.1", {"start": v(53.19, 175.41) * mm, "end": v(63.5, 175.41) * mm});
            skLineSegment(sketch, "E3.3.12.2", {"start": v(53.19, 165.1) * mm, "end": v(63.5, 165.1) * mm});
            skLineSegment(sketch, "E3.3.12.3", {"start": v(63.5, 165.1) * mm, "end": v(63.5, 175.41) * mm});
            skLineSegment(sketch, "E3.3.13.0", {"start": v(53.19, 177.8) * mm, "end": v(53.19, 188.11) * mm});
            skLineSegment(sketch, "E3.3.13.1", {"start": v(53.19, 188.11) * mm, "end": v(63.5, 188.11) * mm});
            skLineSegment(sketch, "E3.3.13.2", {"start": v(53.19, 177.8) * mm, "end": v(63.5, 177.8) * mm});
            skLineSegment(sketch, "E3.3.13.3", {"start": v(63.5, 177.8) * mm, "end": v(63.5, 188.11) * mm});
            skLineSegment(sketch, "E3.3.14.0", {"start": v(53.19, 190.5) * mm, "end": v(53.19, 200.81) * mm});
            skLineSegment(sketch, "E3.3.14.1", {"start": v(53.19, 200.81) * mm, "end": v(63.5, 200.81) * mm});
            skLineSegment(sketch, "E3.3.14.2", {"start": v(53.19, 190.5) * mm, "end": v(63.5, 190.5) * mm});
            skLineSegment(sketch, "E3.3.14.3", {"start": v(63.5, 190.5) * mm, "end": v(63.5, 200.81) * mm});
            skLineSegment(sketch, "E3.3.15.0", {"start": v(53.19, 203.2) * mm, "end": v(53.19, 213.51) * mm});
            skLineSegment(sketch, "E3.3.15.1", {"start": v(53.19, 213.51) * mm, "end": v(63.5, 213.51) * mm});
            skLineSegment(sketch, "E3.3.15.2", {"start": v(53.19, 203.2) * mm, "end": v(63.5, 203.2) * mm});
            skLineSegment(sketch, "E3.3.15.3", {"start": v(63.5, 203.2) * mm, "end": v(63.5, 213.51) * mm});
            skLineSegment(sketch, "E3.3.16.0", {"start": v(53.19, 215.9) * mm, "end": v(53.19, 226.21) * mm});
            skLineSegment(sketch, "E3.3.16.1", {"start": v(53.19, 226.21) * mm, "end": v(63.5, 226.21) * mm});
            skLineSegment(sketch, "E3.3.16.2", {"start": v(53.19, 215.9) * mm, "end": v(63.5, 215.9) * mm});
            skLineSegment(sketch, "E3.3.16.3", {"start": v(63.5, 215.9) * mm, "end": v(63.5, 226.21) * mm});
            skLineSegment(sketch, "E3.3.17.0", {"start": v(53.19, 228.6) * mm, "end": v(53.19, 238.91) * mm});
            skLineSegment(sketch, "E3.3.17.1", {"start": v(53.19, 238.91) * mm, "end": v(63.5, 238.91) * mm});
            skLineSegment(sketch, "E3.3.17.2", {"start": v(53.19, 228.6) * mm, "end": v(63.5, 228.6) * mm});
            skLineSegment(sketch, "E3.3.17.3", {"start": v(63.5, 228.6) * mm, "end": v(63.5, 238.91) * mm});
            skLineSegment(sketch, "E3.3.18.0", {"start": v(53.19, 241.3) * mm, "end": v(53.19, 251.61) * mm});
            skLineSegment(sketch, "E3.3.18.1", {"start": v(53.19, 251.61) * mm, "end": v(63.5, 251.61) * mm});
            skLineSegment(sketch, "E3.3.18.2", {"start": v(53.19, 241.3) * mm, "end": v(63.5, 241.3) * mm});
            skLineSegment(sketch, "E3.3.18.3", {"start": v(63.5, 241.3) * mm, "end": v(63.5, 251.61) * mm});
            skLineSegment(sketch, "E3.3.19.0", {"start": v(53.19, 254) * mm, "end": v(53.19, 264.31) * mm});
            skLineSegment(sketch, "E3.3.19.1", {"start": v(53.19, 264.31) * mm, "end": v(63.5, 264.31) * mm});
            skLineSegment(sketch, "E3.3.19.2", {"start": v(53.19, 254) * mm, "end": v(63.5, 254) * mm});
            skLineSegment(sketch, "E3.3.19.3", {"start": v(63.5, 254) * mm, "end": v(63.5, 264.31) * mm});
            skLineSegment(sketch, "E3.3.20.0", {"start": v(53.19, 266.7) * mm, "end": v(53.19, 277.01) * mm});
            skLineSegment(sketch, "E3.3.20.1", {"start": v(53.19, 277.01) * mm, "end": v(63.5, 277.01) * mm});
            skLineSegment(sketch, "E3.3.20.2", {"start": v(53.19, 266.7) * mm, "end": v(63.5, 266.7) * mm});
            skLineSegment(sketch, "E3.3.20.3", {"start": v(63.5, 266.7) * mm, "end": v(63.5, 277.01) * mm});
            skLineSegment(sketch, "E3.3.21.0", {"start": v(53.19, 279.4) * mm, "end": v(53.19, 289.71) * mm});
            skLineSegment(sketch, "E3.3.21.1", {"start": v(53.19, 289.71) * mm, "end": v(63.5, 289.71) * mm});
            skLineSegment(sketch, "E3.3.21.2", {"start": v(53.19, 279.4) * mm, "end": v(63.5, 279.4) * mm});
            skLineSegment(sketch, "E3.3.21.3", {"start": v(63.5, 279.4) * mm, "end": v(63.5, 289.71) * mm});
            skLineSegment(sketch, "E3.4.0.0", {"start": v(65.89, 12.7) * mm, "end": v(65.89, 23.01) * mm});
            skLineSegment(sketch, "E3.4.0.1", {"start": v(65.89, 23.01) * mm, "end": v(76.2, 23.01) * mm});
            skLineSegment(sketch, "E3.4.0.2", {"start": v(65.89, 12.7) * mm, "end": v(76.2, 12.7) * mm});
            skLineSegment(sketch, "E3.4.0.3", {"start": v(76.2, 12.7) * mm, "end": v(76.2, 23.01) * mm});
            skLineSegment(sketch, "E3.4.1.0", {"start": v(65.89, 25.4) * mm, "end": v(65.89, 35.71) * mm});
            skLineSegment(sketch, "E3.4.1.1", {"start": v(65.89, 35.71) * mm, "end": v(76.2, 35.71) * mm});
            skLineSegment(sketch, "E3.4.1.2", {"start": v(65.89, 25.4) * mm, "end": v(76.2, 25.4) * mm});
            skLineSegment(sketch, "E3.4.1.3", {"start": v(76.2, 25.4) * mm, "end": v(76.2, 35.71) * mm});
            skLineSegment(sketch, "E3.4.2.0", {"start": v(65.89, 38.1) * mm, "end": v(65.89, 48.41) * mm});
            skLineSegment(sketch, "E3.4.2.1", {"start": v(65.89, 48.41) * mm, "end": v(76.2, 48.41) * mm});
            skLineSegment(sketch, "E3.4.2.2", {"start": v(65.89, 38.1) * mm, "end": v(76.2, 38.1) * mm});
            skLineSegment(sketch, "E3.4.2.3", {"start": v(76.2, 38.1) * mm, "end": v(76.2, 48.41) * mm});
            skLineSegment(sketch, "E3.4.3.0", {"start": v(65.89, 50.8) * mm, "end": v(65.89, 61.11) * mm});
            skLineSegment(sketch, "E3.4.3.1", {"start": v(65.89, 61.11) * mm, "end": v(76.2, 61.11) * mm});
            skLineSegment(sketch, "E3.4.3.2", {"start": v(65.89, 50.8) * mm, "end": v(76.2, 50.8) * mm});
            skLineSegment(sketch, "E3.4.3.3", {"start": v(76.2, 50.8) * mm, "end": v(76.2, 61.11) * mm});
            skLineSegment(sketch, "E3.4.4.0", {"start": v(65.89, 63.5) * mm, "end": v(65.89, 73.81) * mm});
            skLineSegment(sketch, "E3.4.4.1", {"start": v(65.89, 73.81) * mm, "end": v(76.2, 73.81) * mm});
            skLineSegment(sketch, "E3.4.4.2", {"start": v(65.89, 63.5) * mm, "end": v(76.2, 63.5) * mm});
            skLineSegment(sketch, "E3.4.4.3", {"start": v(76.2, 63.5) * mm, "end": v(76.2, 73.81) * mm});
            skLineSegment(sketch, "E3.4.5.0", {"start": v(65.89, 76.2) * mm, "end": v(65.89, 86.51) * mm});
            skLineSegment(sketch, "E3.4.5.1", {"start": v(65.89, 86.51) * mm, "end": v(76.2, 86.51) * mm});
            skLineSegment(sketch, "E3.4.5.2", {"start": v(65.89, 76.2) * mm, "end": v(76.2, 76.2) * mm});
            skLineSegment(sketch, "E3.4.5.3", {"start": v(76.2, 76.2) * mm, "end": v(76.2, 86.51) * mm});
            skLineSegment(sketch, "E3.4.6.0", {"start": v(65.89, 88.9) * mm, "end": v(65.89, 99.21) * mm});
            skLineSegment(sketch, "E3.4.6.1", {"start": v(65.89, 99.21) * mm, "end": v(76.2, 99.21) * mm});
            skLineSegment(sketch, "E3.4.6.2", {"start": v(65.89, 88.9) * mm, "end": v(76.2, 88.9) * mm});
            skLineSegment(sketch, "E3.4.6.3", {"start": v(76.2, 88.9) * mm, "end": v(76.2, 99.21) * mm});
            skLineSegment(sketch, "E3.4.7.0", {"start": v(65.89, 101.6) * mm, "end": v(65.89, 111.91) * mm});
            skLineSegment(sketch, "E3.4.7.1", {"start": v(65.89, 111.91) * mm, "end": v(76.2, 111.91) * mm});
            skLineSegment(sketch, "E3.4.7.2", {"start": v(65.89, 101.6) * mm, "end": v(76.2, 101.6) * mm});
            skLineSegment(sketch, "E3.4.7.3", {"start": v(76.2, 101.6) * mm, "end": v(76.2, 111.91) * mm});
            skLineSegment(sketch, "E3.4.8.0", {"start": v(65.89, 114.3) * mm, "end": v(65.89, 124.61) * mm});
            skLineSegment(sketch, "E3.4.8.1", {"start": v(65.89, 124.61) * mm, "end": v(76.2, 124.61) * mm});
            skLineSegment(sketch, "E3.4.8.2", {"start": v(65.89, 114.3) * mm, "end": v(76.2, 114.3) * mm});
            skLineSegment(sketch, "E3.4.8.3", {"start": v(76.2, 114.3) * mm, "end": v(76.2, 124.61) * mm});
            skLineSegment(sketch, "E3.4.9.0", {"start": v(65.89, 127) * mm, "end": v(65.89, 137.31) * mm});
            skLineSegment(sketch, "E3.4.9.1", {"start": v(65.89, 137.31) * mm, "end": v(76.2, 137.31) * mm});
            skLineSegment(sketch, "E3.4.9.2", {"start": v(65.89, 127) * mm, "end": v(76.2, 127) * mm});
            skLineSegment(sketch, "E3.4.9.3", {"start": v(76.2, 127) * mm, "end": v(76.2, 137.31) * mm});
            skLineSegment(sketch, "E3.4.10.0", {"start": v(65.89, 139.7) * mm, "end": v(65.89, 150.01) * mm});
            skLineSegment(sketch, "E3.4.10.1", {"start": v(65.89, 150.01) * mm, "end": v(76.2, 150.01) * mm});
            skLineSegment(sketch, "E3.4.10.2", {"start": v(65.89, 139.7) * mm, "end": v(76.2, 139.7) * mm});
            skLineSegment(sketch, "E3.4.10.3", {"start": v(76.2, 139.7) * mm, "end": v(76.2, 150.01) * mm});
            skLineSegment(sketch, "E3.4.11.0", {"start": v(65.89, 152.4) * mm, "end": v(65.89, 162.71) * mm});
            skLineSegment(sketch, "E3.4.11.1", {"start": v(65.89, 162.71) * mm, "end": v(76.2, 162.71) * mm});
            skLineSegment(sketch, "E3.4.11.2", {"start": v(65.89, 152.4) * mm, "end": v(76.2, 152.4) * mm});
            skLineSegment(sketch, "E3.4.11.3", {"start": v(76.2, 152.4) * mm, "end": v(76.2, 162.71) * mm});
            skLineSegment(sketch, "E3.4.12.0", {"start": v(65.89, 165.1) * mm, "end": v(65.89, 175.41) * mm});
            skLineSegment(sketch, "E3.4.12.1", {"start": v(65.89, 175.41) * mm, "end": v(76.2, 175.41) * mm});
            skLineSegment(sketch, "E3.4.12.2", {"start": v(65.89, 165.1) * mm, "end": v(76.2, 165.1) * mm});
            skLineSegment(sketch, "E3.4.12.3", {"start": v(76.2, 165.1) * mm, "end": v(76.2, 175.41) * mm});
            skLineSegment(sketch, "E3.4.13.0", {"start": v(65.89, 177.8) * mm, "end": v(65.89, 188.11) * mm});
            skLineSegment(sketch, "E3.4.13.1", {"start": v(65.89, 188.11) * mm, "end": v(76.2, 188.11) * mm});
            skLineSegment(sketch, "E3.4.13.2", {"start": v(65.89, 177.8) * mm, "end": v(76.2, 177.8) * mm});
            skLineSegment(sketch, "E3.4.13.3", {"start": v(76.2, 177.8) * mm, "end": v(76.2, 188.11) * mm});
            skLineSegment(sketch, "E3.4.14.0", {"start": v(65.89, 190.5) * mm, "end": v(65.89, 200.81) * mm});
            skLineSegment(sketch, "E3.4.14.1", {"start": v(65.89, 200.81) * mm, "end": v(76.2, 200.81) * mm});
            skLineSegment(sketch, "E3.4.14.2", {"start": v(65.89, 190.5) * mm, "end": v(76.2, 190.5) * mm});
            skLineSegment(sketch, "E3.4.14.3", {"start": v(76.2, 190.5) * mm, "end": v(76.2, 200.81) * mm});
            skLineSegment(sketch, "E3.4.15.0", {"start": v(65.89, 203.2) * mm, "end": v(65.89, 213.51) * mm});
            skLineSegment(sketch, "E3.4.15.1", {"start": v(65.89, 213.51) * mm, "end": v(76.2, 213.51) * mm});
            skLineSegment(sketch, "E3.4.15.2", {"start": v(65.89, 203.2) * mm, "end": v(76.2, 203.2) * mm});
            skLineSegment(sketch, "E3.4.15.3", {"start": v(76.2, 203.2) * mm, "end": v(76.2, 213.51) * mm});
            skLineSegment(sketch, "E3.4.16.0", {"start": v(65.89, 215.9) * mm, "end": v(65.89, 226.21) * mm});
            skLineSegment(sketch, "E3.4.16.1", {"start": v(65.89, 226.21) * mm, "end": v(76.2, 226.21) * mm});
            skLineSegment(sketch, "E3.4.16.2", {"start": v(65.89, 215.9) * mm, "end": v(76.2, 215.9) * mm});
            skLineSegment(sketch, "E3.4.16.3", {"start": v(76.2, 215.9) * mm, "end": v(76.2, 226.21) * mm});
            skLineSegment(sketch, "E3.4.17.0", {"start": v(65.89, 228.6) * mm, "end": v(65.89, 238.91) * mm});
            skLineSegment(sketch, "E3.4.17.1", {"start": v(65.89, 238.91) * mm, "end": v(76.2, 238.91) * mm});
            skLineSegment(sketch, "E3.4.17.2", {"start": v(65.89, 228.6) * mm, "end": v(76.2, 228.6) * mm});
            skLineSegment(sketch, "E3.4.17.3", {"start": v(76.2, 228.6) * mm, "end": v(76.2, 238.91) * mm});
            skLineSegment(sketch, "E3.4.18.0", {"start": v(65.89, 241.3) * mm, "end": v(65.89, 251.61) * mm});
            skLineSegment(sketch, "E3.4.18.1", {"start": v(65.89, 251.61) * mm, "end": v(76.2, 251.61) * mm});
            skLineSegment(sketch, "E3.4.18.2", {"start": v(65.89, 241.3) * mm, "end": v(76.2, 241.3) * mm});
            skLineSegment(sketch, "E3.4.18.3", {"start": v(76.2, 241.3) * mm, "end": v(76.2, 251.61) * mm});
            skLineSegment(sketch, "E3.4.19.0", {"start": v(65.89, 254) * mm, "end": v(65.89, 264.31) * mm});
            skLineSegment(sketch, "E3.4.19.1", {"start": v(65.89, 264.31) * mm, "end": v(76.2, 264.31) * mm});
            skLineSegment(sketch, "E3.4.19.2", {"start": v(65.89, 254) * mm, "end": v(76.2, 254) * mm});
            skLineSegment(sketch, "E3.4.19.3", {"start": v(76.2, 254) * mm, "end": v(76.2, 264.31) * mm});
            skLineSegment(sketch, "E3.4.20.0", {"start": v(65.89, 266.7) * mm, "end": v(65.89, 277.01) * mm});
            skLineSegment(sketch, "E3.4.20.1", {"start": v(65.89, 277.01) * mm, "end": v(76.2, 277.01) * mm});
            skLineSegment(sketch, "E3.4.20.2", {"start": v(65.89, 266.7) * mm, "end": v(76.2, 266.7) * mm});
            skLineSegment(sketch, "E3.4.20.3", {"start": v(76.2, 266.7) * mm, "end": v(76.2, 277.01) * mm});
            skLineSegment(sketch, "E3.4.21.0", {"start": v(65.89, 279.4) * mm, "end": v(65.89, 289.71) * mm});
            skLineSegment(sketch, "E3.4.21.1", {"start": v(65.89, 289.71) * mm, "end": v(76.2, 289.71) * mm});
            skLineSegment(sketch, "E3.4.21.2", {"start": v(65.89, 279.4) * mm, "end": v(76.2, 279.4) * mm});
            skLineSegment(sketch, "E3.4.21.3", {"start": v(76.2, 279.4) * mm, "end": v(76.2, 289.71) * mm});
            skLineSegment(sketch, "E3.5.0.0", {"start": v(78.59, 12.7) * mm, "end": v(78.59, 23.01) * mm});
            skLineSegment(sketch, "E3.5.0.1", {"start": v(78.59, 23.01) * mm, "end": v(88.9, 23.01) * mm});
            skLineSegment(sketch, "E3.5.0.2", {"start": v(78.59, 12.7) * mm, "end": v(88.9, 12.7) * mm});
            skLineSegment(sketch, "E3.5.0.3", {"start": v(88.9, 12.7) * mm, "end": v(88.9, 23.01) * mm});
            skLineSegment(sketch, "E3.5.1.0", {"start": v(78.59, 25.4) * mm, "end": v(78.59, 35.71) * mm});
            skLineSegment(sketch, "E3.5.1.1", {"start": v(78.59, 35.71) * mm, "end": v(88.9, 35.71) * mm});
            skLineSegment(sketch, "E3.5.1.2", {"start": v(78.59, 25.4) * mm, "end": v(88.9, 25.4) * mm});
            skLineSegment(sketch, "E3.5.1.3", {"start": v(88.9, 25.4) * mm, "end": v(88.9, 35.71) * mm});
            skLineSegment(sketch, "E3.5.2.0", {"start": v(78.59, 38.1) * mm, "end": v(78.59, 48.41) * mm});
            skLineSegment(sketch, "E3.5.2.1", {"start": v(78.59, 48.41) * mm, "end": v(88.9, 48.41) * mm});
            skLineSegment(sketch, "E3.5.2.2", {"start": v(78.59, 38.1) * mm, "end": v(88.9, 38.1) * mm});
            skLineSegment(sketch, "E3.5.2.3", {"start": v(88.9, 38.1) * mm, "end": v(88.9, 48.41) * mm});
            skLineSegment(sketch, "E3.5.3.0", {"start": v(78.59, 50.8) * mm, "end": v(78.59, 61.11) * mm});
            skLineSegment(sketch, "E3.5.3.1", {"start": v(78.59, 61.11) * mm, "end": v(88.9, 61.11) * mm});
            skLineSegment(sketch, "E3.5.3.2", {"start": v(78.59, 50.8) * mm, "end": v(88.9, 50.8) * mm});
            skLineSegment(sketch, "E3.5.3.3", {"start": v(88.9, 50.8) * mm, "end": v(88.9, 61.11) * mm});
            skLineSegment(sketch, "E3.5.4.0", {"start": v(78.59, 63.5) * mm, "end": v(78.59, 73.81) * mm});
            skLineSegment(sketch, "E3.5.4.1", {"start": v(78.59, 73.81) * mm, "end": v(88.9, 73.81) * mm});
            skLineSegment(sketch, "E3.5.4.2", {"start": v(78.59, 63.5) * mm, "end": v(88.9, 63.5) * mm});
            skLineSegment(sketch, "E3.5.4.3", {"start": v(88.9, 63.5) * mm, "end": v(88.9, 73.81) * mm});
            skLineSegment(sketch, "E3.5.5.0", {"start": v(78.59, 76.2) * mm, "end": v(78.59, 86.51) * mm});
            skLineSegment(sketch, "E3.5.5.1", {"start": v(78.59, 86.51) * mm, "end": v(88.9, 86.51) * mm});
            skLineSegment(sketch, "E3.5.5.2", {"start": v(78.59, 76.2) * mm, "end": v(88.9, 76.2) * mm});
            skLineSegment(sketch, "E3.5.5.3", {"start": v(88.9, 76.2) * mm, "end": v(88.9, 86.51) * mm});
            skLineSegment(sketch, "E3.5.6.0", {"start": v(78.59, 88.9) * mm, "end": v(78.59, 99.21) * mm});
            skLineSegment(sketch, "E3.5.6.1", {"start": v(78.59, 99.21) * mm, "end": v(88.9, 99.21) * mm});
            skLineSegment(sketch, "E3.5.6.2", {"start": v(78.59, 88.9) * mm, "end": v(88.9, 88.9) * mm});
            skLineSegment(sketch, "E3.5.6.3", {"start": v(88.9, 88.9) * mm, "end": v(88.9, 99.21) * mm});
            skLineSegment(sketch, "E3.5.7.0", {"start": v(78.59, 101.6) * mm, "end": v(78.59, 111.91) * mm});
            skLineSegment(sketch, "E3.5.7.1", {"start": v(78.59, 111.91) * mm, "end": v(88.9, 111.91) * mm});
            skLineSegment(sketch, "E3.5.7.2", {"start": v(78.59, 101.6) * mm, "end": v(88.9, 101.6) * mm});
            skLineSegment(sketch, "E3.5.7.3", {"start": v(88.9, 101.6) * mm, "end": v(88.9, 111.91) * mm});
            skLineSegment(sketch, "E3.5.8.0", {"start": v(78.59, 114.3) * mm, "end": v(78.59, 124.61) * mm});
            skLineSegment(sketch, "E3.5.8.1", {"start": v(78.59, 124.61) * mm, "end": v(88.9, 124.61) * mm});
            skLineSegment(sketch, "E3.5.8.2", {"start": v(78.59, 114.3) * mm, "end": v(88.9, 114.3) * mm});
            skLineSegment(sketch, "E3.5.8.3", {"start": v(88.9, 114.3) * mm, "end": v(88.9, 124.61) * mm});
            skLineSegment(sketch, "E3.5.9.0", {"start": v(78.59, 127) * mm, "end": v(78.59, 137.31) * mm});
            skLineSegment(sketch, "E3.5.9.1", {"start": v(78.59, 137.31) * mm, "end": v(88.9, 137.31) * mm});
            skLineSegment(sketch, "E3.5.9.2", {"start": v(78.59, 127) * mm, "end": v(88.9, 127) * mm});
            skLineSegment(sketch, "E3.5.9.3", {"start": v(88.9, 127) * mm, "end": v(88.9, 137.31) * mm});
            skLineSegment(sketch, "E3.5.10.0", {"start": v(78.59, 139.7) * mm, "end": v(78.59, 150.01) * mm});
            skLineSegment(sketch, "E3.5.10.1", {"start": v(78.59, 150.01) * mm, "end": v(88.9, 150.01) * mm});
            skLineSegment(sketch, "E3.5.10.2", {"start": v(78.59, 139.7) * mm, "end": v(88.9, 139.7) * mm});
            skLineSegment(sketch, "E3.5.10.3", {"start": v(88.9, 139.7) * mm, "end": v(88.9, 150.01) * mm});
            skLineSegment(sketch, "E3.5.11.0", {"start": v(78.59, 152.4) * mm, "end": v(78.59, 162.71) * mm});
            skLineSegment(sketch, "E3.5.11.1", {"start": v(78.59, 162.71) * mm, "end": v(88.9, 162.71) * mm});
            skLineSegment(sketch, "E3.5.11.2", {"start": v(78.59, 152.4) * mm, "end": v(88.9, 152.4) * mm});
            skLineSegment(sketch, "E3.5.11.3", {"start": v(88.9, 152.4) * mm, "end": v(88.9, 162.71) * mm});
            skLineSegment(sketch, "E3.5.12.0", {"start": v(78.59, 165.1) * mm, "end": v(78.59, 175.41) * mm});
            skLineSegment(sketch, "E3.5.12.1", {"start": v(78.59, 175.41) * mm, "end": v(88.9, 175.41) * mm});
            skLineSegment(sketch, "E3.5.12.2", {"start": v(78.59, 165.1) * mm, "end": v(88.9, 165.1) * mm});
            skLineSegment(sketch, "E3.5.12.3", {"start": v(88.9, 165.1) * mm, "end": v(88.9, 175.41) * mm});
            skLineSegment(sketch, "E3.5.13.0", {"start": v(78.59, 177.8) * mm, "end": v(78.59, 188.11) * mm});
            skLineSegment(sketch, "E3.5.13.1", {"start": v(78.59, 188.11) * mm, "end": v(88.9, 188.11) * mm});
            skLineSegment(sketch, "E3.5.13.2", {"start": v(78.59, 177.8) * mm, "end": v(88.9, 177.8) * mm});
            skLineSegment(sketch, "E3.5.13.3", {"start": v(88.9, 177.8) * mm, "end": v(88.9, 188.11) * mm});
            skLineSegment(sketch, "E3.5.14.0", {"start": v(78.59, 190.5) * mm, "end": v(78.59, 200.81) * mm});
            skLineSegment(sketch, "E3.5.14.1", {"start": v(78.59, 200.81) * mm, "end": v(88.9, 200.81) * mm});
            skLineSegment(sketch, "E3.5.14.2", {"start": v(78.59, 190.5) * mm, "end": v(88.9, 190.5) * mm});
            skLineSegment(sketch, "E3.5.14.3", {"start": v(88.9, 190.5) * mm, "end": v(88.9, 200.81) * mm});
            skLineSegment(sketch, "E3.5.15.0", {"start": v(78.59, 203.2) * mm, "end": v(78.59, 213.51) * mm});
            skLineSegment(sketch, "E3.5.15.1", {"start": v(78.59, 213.51) * mm, "end": v(88.9, 213.51) * mm});
            skLineSegment(sketch, "E3.5.15.2", {"start": v(78.59, 203.2) * mm, "end": v(88.9, 203.2) * mm});
            skLineSegment(sketch, "E3.5.15.3", {"start": v(88.9, 203.2) * mm, "end": v(88.9, 213.51) * mm});
            skLineSegment(sketch, "E3.5.16.0", {"start": v(78.59, 215.9) * mm, "end": v(78.59, 226.21) * mm});
            skLineSegment(sketch, "E3.5.16.1", {"start": v(78.59, 226.21) * mm, "end": v(88.9, 226.21) * mm});
            skLineSegment(sketch, "E3.5.16.2", {"start": v(78.59, 215.9) * mm, "end": v(88.9, 215.9) * mm});
            skLineSegment(sketch, "E3.5.16.3", {"start": v(88.9, 215.9) * mm, "end": v(88.9, 226.21) * mm});
            skLineSegment(sketch, "E3.5.17.0", {"start": v(78.59, 228.6) * mm, "end": v(78.59, 238.91) * mm});
            skLineSegment(sketch, "E3.5.17.1", {"start": v(78.59, 238.91) * mm, "end": v(88.9, 238.91) * mm});
            skLineSegment(sketch, "E3.5.17.2", {"start": v(78.59, 228.6) * mm, "end": v(88.9, 228.6) * mm});
            skLineSegment(sketch, "E3.5.17.3", {"start": v(88.9, 228.6) * mm, "end": v(88.9, 238.91) * mm});
            skLineSegment(sketch, "E3.5.18.0", {"start": v(78.59, 241.3) * mm, "end": v(78.59, 251.61) * mm});
            skLineSegment(sketch, "E3.5.18.1", {"start": v(78.59, 251.61) * mm, "end": v(88.9, 251.61) * mm});
            skLineSegment(sketch, "E3.5.18.2", {"start": v(78.59, 241.3) * mm, "end": v(88.9, 241.3) * mm});
            skLineSegment(sketch, "E3.5.18.3", {"start": v(88.9, 241.3) * mm, "end": v(88.9, 251.61) * mm});
            skLineSegment(sketch, "E3.5.19.0", {"start": v(78.59, 254) * mm, "end": v(78.59, 264.31) * mm});
            skLineSegment(sketch, "E3.5.19.1", {"start": v(78.59, 264.31) * mm, "end": v(88.9, 264.31) * mm});
            skLineSegment(sketch, "E3.5.19.2", {"start": v(78.59, 254) * mm, "end": v(88.9, 254) * mm});
            skLineSegment(sketch, "E3.5.19.3", {"start": v(88.9, 254) * mm, "end": v(88.9, 264.31) * mm});
            skLineSegment(sketch, "E3.5.20.0", {"start": v(78.59, 266.7) * mm, "end": v(78.59, 277.01) * mm});
            skLineSegment(sketch, "E3.5.20.1", {"start": v(78.59, 277.01) * mm, "end": v(88.9, 277.01) * mm});
            skLineSegment(sketch, "E3.5.20.2", {"start": v(78.59, 266.7) * mm, "end": v(88.9, 266.7) * mm});
            skLineSegment(sketch, "E3.5.20.3", {"start": v(88.9, 266.7) * mm, "end": v(88.9, 277.01) * mm});
            skLineSegment(sketch, "E3.5.21.0", {"start": v(78.59, 279.4) * mm, "end": v(78.59, 289.71) * mm});
            skLineSegment(sketch, "E3.5.21.1", {"start": v(78.59, 289.71) * mm, "end": v(88.9, 289.71) * mm});
            skLineSegment(sketch, "E3.5.21.2", {"start": v(78.59, 279.4) * mm, "end": v(88.9, 279.4) * mm});
            skLineSegment(sketch, "E3.5.21.3", {"start": v(88.9, 279.4) * mm, "end": v(88.9, 289.71) * mm});
            skLineSegment(sketch, "E3.6.0.0", {"start": v(91.29, 12.7) * mm, "end": v(91.29, 23.01) * mm});
            skLineSegment(sketch, "E3.6.0.1", {"start": v(91.29, 23.01) * mm, "end": v(101.6, 23.01) * mm});
            skLineSegment(sketch, "E3.6.0.2", {"start": v(91.29, 12.7) * mm, "end": v(101.6, 12.7) * mm});
            skLineSegment(sketch, "E3.6.0.3", {"start": v(101.6, 12.7) * mm, "end": v(101.6, 23.01) * mm});
            skLineSegment(sketch, "E3.6.1.0", {"start": v(91.29, 25.4) * mm, "end": v(91.29, 35.71) * mm});
            skLineSegment(sketch, "E3.6.1.1", {"start": v(91.29, 35.71) * mm, "end": v(101.6, 35.71) * mm});
            skLineSegment(sketch, "E3.6.1.2", {"start": v(91.29, 25.4) * mm, "end": v(101.6, 25.4) * mm});
            skLineSegment(sketch, "E3.6.1.3", {"start": v(101.6, 25.4) * mm, "end": v(101.6, 35.71) * mm});
            skLineSegment(sketch, "E3.6.2.0", {"start": v(91.29, 38.1) * mm, "end": v(91.29, 48.41) * mm});
            skLineSegment(sketch, "E3.6.2.1", {"start": v(91.29, 48.41) * mm, "end": v(101.6, 48.41) * mm});
            skLineSegment(sketch, "E3.6.2.2", {"start": v(91.29, 38.1) * mm, "end": v(101.6, 38.1) * mm});
            skLineSegment(sketch, "E3.6.2.3", {"start": v(101.6, 38.1) * mm, "end": v(101.6, 48.41) * mm});
            skLineSegment(sketch, "E3.6.3.0", {"start": v(91.29, 50.8) * mm, "end": v(91.29, 61.11) * mm});
            skLineSegment(sketch, "E3.6.3.1", {"start": v(91.29, 61.11) * mm, "end": v(101.6, 61.11) * mm});
            skLineSegment(sketch, "E3.6.3.2", {"start": v(91.29, 50.8) * mm, "end": v(101.6, 50.8) * mm});
            skLineSegment(sketch, "E3.6.3.3", {"start": v(101.6, 50.8) * mm, "end": v(101.6, 61.11) * mm});
            skLineSegment(sketch, "E3.6.4.0", {"start": v(91.29, 63.5) * mm, "end": v(91.29, 73.81) * mm});
            skLineSegment(sketch, "E3.6.4.1", {"start": v(91.29, 73.81) * mm, "end": v(101.6, 73.81) * mm});
            skLineSegment(sketch, "E3.6.4.2", {"start": v(91.29, 63.5) * mm, "end": v(101.6, 63.5) * mm});
            skLineSegment(sketch, "E3.6.4.3", {"start": v(101.6, 63.5) * mm, "end": v(101.6, 73.81) * mm});
            skLineSegment(sketch, "E3.6.5.0", {"start": v(91.29, 76.2) * mm, "end": v(91.29, 86.51) * mm});
            skLineSegment(sketch, "E3.6.5.1", {"start": v(91.29, 86.51) * mm, "end": v(101.6, 86.51) * mm});
            skLineSegment(sketch, "E3.6.5.2", {"start": v(91.29, 76.2) * mm, "end": v(101.6, 76.2) * mm});
            skLineSegment(sketch, "E3.6.5.3", {"start": v(101.6, 76.2) * mm, "end": v(101.6, 86.51) * mm});
            skLineSegment(sketch, "E3.6.6.0", {"start": v(91.29, 88.9) * mm, "end": v(91.29, 99.21) * mm});
            skLineSegment(sketch, "E3.6.6.1", {"start": v(91.29, 99.21) * mm, "end": v(101.6, 99.21) * mm});
            skLineSegment(sketch, "E3.6.6.2", {"start": v(91.29, 88.9) * mm, "end": v(101.6, 88.9) * mm});
            skLineSegment(sketch, "E3.6.6.3", {"start": v(101.6, 88.9) * mm, "end": v(101.6, 99.21) * mm});
            skLineSegment(sketch, "E3.6.7.0", {"start": v(91.29, 101.6) * mm, "end": v(91.29, 111.91) * mm});
            skLineSegment(sketch, "E3.6.7.1", {"start": v(91.29, 111.91) * mm, "end": v(101.6, 111.91) * mm});
            skLineSegment(sketch, "E3.6.7.2", {"start": v(91.29, 101.6) * mm, "end": v(101.6, 101.6) * mm});
            skLineSegment(sketch, "E3.6.7.3", {"start": v(101.6, 101.6) * mm, "end": v(101.6, 111.91) * mm});
            skLineSegment(sketch, "E3.6.8.0", {"start": v(91.29, 114.3) * mm, "end": v(91.29, 124.61) * mm});
            skLineSegment(sketch, "E3.6.8.1", {"start": v(91.29, 124.61) * mm, "end": v(101.6, 124.61) * mm});
            skLineSegment(sketch, "E3.6.8.2", {"start": v(91.29, 114.3) * mm, "end": v(101.6, 114.3) * mm});
            skLineSegment(sketch, "E3.6.8.3", {"start": v(101.6, 114.3) * mm, "end": v(101.6, 124.61) * mm});
            skLineSegment(sketch, "E3.6.9.0", {"start": v(91.29, 127) * mm, "end": v(91.29, 137.31) * mm});
            skLineSegment(sketch, "E3.6.9.1", {"start": v(91.29, 137.31) * mm, "end": v(101.6, 137.31) * mm});
            skLineSegment(sketch, "E3.6.9.2", {"start": v(91.29, 127) * mm, "end": v(101.6, 127) * mm});
            skLineSegment(sketch, "E3.6.9.3", {"start": v(101.6, 127) * mm, "end": v(101.6, 137.31) * mm});
            skLineSegment(sketch, "E3.6.10.0", {"start": v(91.29, 139.7) * mm, "end": v(91.29, 150.01) * mm});
            skLineSegment(sketch, "E3.6.10.1", {"start": v(91.29, 150.01) * mm, "end": v(101.6, 150.01) * mm});
            skLineSegment(sketch, "E3.6.10.2", {"start": v(91.29, 139.7) * mm, "end": v(101.6, 139.7) * mm});
            skLineSegment(sketch, "E3.6.10.3", {"start": v(101.6, 139.7) * mm, "end": v(101.6, 150.01) * mm});
            skLineSegment(sketch, "E3.6.11.0", {"start": v(91.29, 152.4) * mm, "end": v(91.29, 162.71) * mm});
            skLineSegment(sketch, "E3.6.11.1", {"start": v(91.29, 162.71) * mm, "end": v(101.6, 162.71) * mm});
            skLineSegment(sketch, "E3.6.11.2", {"start": v(91.29, 152.4) * mm, "end": v(101.6, 152.4) * mm});
            skLineSegment(sketch, "E3.6.11.3", {"start": v(101.6, 152.4) * mm, "end": v(101.6, 162.71) * mm});
            skLineSegment(sketch, "E3.6.12.0", {"start": v(91.29, 165.1) * mm, "end": v(91.29, 175.41) * mm});
            skLineSegment(sketch, "E3.6.12.1", {"start": v(91.29, 175.41) * mm, "end": v(101.6, 175.41) * mm});
            skLineSegment(sketch, "E3.6.12.2", {"start": v(91.29, 165.1) * mm, "end": v(101.6, 165.1) * mm});
            skLineSegment(sketch, "E3.6.12.3", {"start": v(101.6, 165.1) * mm, "end": v(101.6, 175.41) * mm});
            skLineSegment(sketch, "E3.6.13.0", {"start": v(91.29, 177.8) * mm, "end": v(91.29, 188.11) * mm});
            skLineSegment(sketch, "E3.6.13.1", {"start": v(91.29, 188.11) * mm, "end": v(101.6, 188.11) * mm});
            skLineSegment(sketch, "E3.6.13.2", {"start": v(91.29, 177.8) * mm, "end": v(101.6, 177.8) * mm});
            skLineSegment(sketch, "E3.6.13.3", {"start": v(101.6, 177.8) * mm, "end": v(101.6, 188.11) * mm});
            skLineSegment(sketch, "E3.6.14.0", {"start": v(91.29, 190.5) * mm, "end": v(91.29, 200.81) * mm});
            skLineSegment(sketch, "E3.6.14.1", {"start": v(91.29, 200.81) * mm, "end": v(101.6, 200.81) * mm});
            skLineSegment(sketch, "E3.6.14.2", {"start": v(91.29, 190.5) * mm, "end": v(101.6, 190.5) * mm});
            skLineSegment(sketch, "E3.6.14.3", {"start": v(101.6, 190.5) * mm, "end": v(101.6, 200.81) * mm});
            skLineSegment(sketch, "E3.6.15.0", {"start": v(91.29, 203.2) * mm, "end": v(91.29, 213.51) * mm});
            skLineSegment(sketch, "E3.6.15.1", {"start": v(91.29, 213.51) * mm, "end": v(101.6, 213.51) * mm});
            skLineSegment(sketch, "E3.6.15.2", {"start": v(91.29, 203.2) * mm, "end": v(101.6, 203.2) * mm});
            skLineSegment(sketch, "E3.6.15.3", {"start": v(101.6, 203.2) * mm, "end": v(101.6, 213.51) * mm});
            skLineSegment(sketch, "E3.6.16.0", {"start": v(91.29, 215.9) * mm, "end": v(91.29, 226.21) * mm});
            skLineSegment(sketch, "E3.6.16.1", {"start": v(91.29, 226.21) * mm, "end": v(101.6, 226.21) * mm});
            skLineSegment(sketch, "E3.6.16.2", {"start": v(91.29, 215.9) * mm, "end": v(101.6, 215.9) * mm});
            skLineSegment(sketch, "E3.6.16.3", {"start": v(101.6, 215.9) * mm, "end": v(101.6, 226.21) * mm});
            skLineSegment(sketch, "E3.6.17.0", {"start": v(91.29, 228.6) * mm, "end": v(91.29, 238.91) * mm});
            skLineSegment(sketch, "E3.6.17.1", {"start": v(91.29, 238.91) * mm, "end": v(101.6, 238.91) * mm});
            skLineSegment(sketch, "E3.6.17.2", {"start": v(91.29, 228.6) * mm, "end": v(101.6, 228.6) * mm});
            skLineSegment(sketch, "E3.6.17.3", {"start": v(101.6, 228.6) * mm, "end": v(101.6, 238.91) * mm});
            skLineSegment(sketch, "E3.6.18.0", {"start": v(91.29, 241.3) * mm, "end": v(91.29, 251.61) * mm});
            skLineSegment(sketch, "E3.6.18.1", {"start": v(91.29, 251.61) * mm, "end": v(101.6, 251.61) * mm});
            skLineSegment(sketch, "E3.6.18.2", {"start": v(91.29, 241.3) * mm, "end": v(101.6, 241.3) * mm});
            skLineSegment(sketch, "E3.6.18.3", {"start": v(101.6, 241.3) * mm, "end": v(101.6, 251.61) * mm});
            skLineSegment(sketch, "E3.6.19.0", {"start": v(91.29, 254) * mm, "end": v(91.29, 264.31) * mm});
            skLineSegment(sketch, "E3.6.19.1", {"start": v(91.29, 264.31) * mm, "end": v(101.6, 264.31) * mm});
            skLineSegment(sketch, "E3.6.19.2", {"start": v(91.29, 254) * mm, "end": v(101.6, 254) * mm});
            skLineSegment(sketch, "E3.6.19.3", {"start": v(101.6, 254) * mm, "end": v(101.6, 264.31) * mm});
            skLineSegment(sketch, "E3.6.20.0", {"start": v(91.29, 266.7) * mm, "end": v(91.29, 277.01) * mm});
            skLineSegment(sketch, "E3.6.20.1", {"start": v(91.29, 277.01) * mm, "end": v(101.6, 277.01) * mm});
            skLineSegment(sketch, "E3.6.20.2", {"start": v(91.29, 266.7) * mm, "end": v(101.6, 266.7) * mm});
            skLineSegment(sketch, "E3.6.20.3", {"start": v(101.6, 266.7) * mm, "end": v(101.6, 277.01) * mm});
            skLineSegment(sketch, "E3.6.21.0", {"start": v(91.29, 279.4) * mm, "end": v(91.29, 289.71) * mm});
            skLineSegment(sketch, "E3.6.21.1", {"start": v(91.29, 289.71) * mm, "end": v(101.6, 289.71) * mm});
            skLineSegment(sketch, "E3.6.21.2", {"start": v(91.29, 279.4) * mm, "end": v(101.6, 279.4) * mm});
            skLineSegment(sketch, "E3.6.21.3", {"start": v(101.6, 279.4) * mm, "end": v(101.6, 289.71) * mm});
            skLineSegment(sketch, "E3.7.0.0", {"start": v(103.99, 12.7) * mm, "end": v(103.99, 23.01) * mm});
            skLineSegment(sketch, "E3.7.0.1", {"start": v(103.99, 23.01) * mm, "end": v(114.3, 23.01) * mm});
            skLineSegment(sketch, "E3.7.0.2", {"start": v(103.99, 12.7) * mm, "end": v(114.3, 12.7) * mm});
            skLineSegment(sketch, "E3.7.0.3", {"start": v(114.3, 12.7) * mm, "end": v(114.3, 23.01) * mm});
            skLineSegment(sketch, "E3.7.1.0", {"start": v(103.99, 25.4) * mm, "end": v(103.99, 35.71) * mm});
            skLineSegment(sketch, "E3.7.1.1", {"start": v(103.99, 35.71) * mm, "end": v(114.3, 35.71) * mm});
            skLineSegment(sketch, "E3.7.1.2", {"start": v(103.99, 25.4) * mm, "end": v(114.3, 25.4) * mm});
            skLineSegment(sketch, "E3.7.1.3", {"start": v(114.3, 25.4) * mm, "end": v(114.3, 35.71) * mm});
            skLineSegment(sketch, "E3.7.2.0", {"start": v(103.99, 38.1) * mm, "end": v(103.99, 48.41) * mm});
            skLineSegment(sketch, "E3.7.2.1", {"start": v(103.99, 48.41) * mm, "end": v(114.3, 48.41) * mm});
            skLineSegment(sketch, "E3.7.2.2", {"start": v(103.99, 38.1) * mm, "end": v(114.3, 38.1) * mm});
            skLineSegment(sketch, "E3.7.2.3", {"start": v(114.3, 38.1) * mm, "end": v(114.3, 48.41) * mm});
            skLineSegment(sketch, "E3.7.3.0", {"start": v(103.99, 50.8) * mm, "end": v(103.99, 61.11) * mm});
            skLineSegment(sketch, "E3.7.3.1", {"start": v(103.99, 61.11) * mm, "end": v(114.3, 61.11) * mm});
            skLineSegment(sketch, "E3.7.3.2", {"start": v(103.99, 50.8) * mm, "end": v(114.3, 50.8) * mm});
            skLineSegment(sketch, "E3.7.3.3", {"start": v(114.3, 50.8) * mm, "end": v(114.3, 61.11) * mm});
            skLineSegment(sketch, "E3.7.4.0", {"start": v(103.99, 63.5) * mm, "end": v(103.99, 73.81) * mm});
            skLineSegment(sketch, "E3.7.4.1", {"start": v(103.99, 73.81) * mm, "end": v(114.3, 73.81) * mm});
            skLineSegment(sketch, "E3.7.4.2", {"start": v(103.99, 63.5) * mm, "end": v(114.3, 63.5) * mm});
            skLineSegment(sketch, "E3.7.4.3", {"start": v(114.3, 63.5) * mm, "end": v(114.3, 73.81) * mm});
            skLineSegment(sketch, "E3.7.5.0", {"start": v(103.99, 76.2) * mm, "end": v(103.99, 86.51) * mm});
            skLineSegment(sketch, "E3.7.5.1", {"start": v(103.99, 86.51) * mm, "end": v(114.3, 86.51) * mm});
            skLineSegment(sketch, "E3.7.5.2", {"start": v(103.99, 76.2) * mm, "end": v(114.3, 76.2) * mm});
            skLineSegment(sketch, "E3.7.5.3", {"start": v(114.3, 76.2) * mm, "end": v(114.3, 86.51) * mm});
            skLineSegment(sketch, "E3.7.6.0", {"start": v(103.99, 88.9) * mm, "end": v(103.99, 99.21) * mm});
            skLineSegment(sketch, "E3.7.6.1", {"start": v(103.99, 99.21) * mm, "end": v(114.3, 99.21) * mm});
            skLineSegment(sketch, "E3.7.6.2", {"start": v(103.99, 88.9) * mm, "end": v(114.3, 88.9) * mm});
            skLineSegment(sketch, "E3.7.6.3", {"start": v(114.3, 88.9) * mm, "end": v(114.3, 99.21) * mm});
            skLineSegment(sketch, "E3.7.7.0", {"start": v(103.99, 101.6) * mm, "end": v(103.99, 111.91) * mm});
            skLineSegment(sketch, "E3.7.7.1", {"start": v(103.99, 111.91) * mm, "end": v(114.3, 111.91) * mm});
            skLineSegment(sketch, "E3.7.7.2", {"start": v(103.99, 101.6) * mm, "end": v(114.3, 101.6) * mm});
            skLineSegment(sketch, "E3.7.7.3", {"start": v(114.3, 101.6) * mm, "end": v(114.3, 111.91) * mm});
            skLineSegment(sketch, "E3.7.8.0", {"start": v(103.99, 114.3) * mm, "end": v(103.99, 124.61) * mm});
            skLineSegment(sketch, "E3.7.8.1", {"start": v(103.99, 124.61) * mm, "end": v(114.3, 124.61) * mm});
            skLineSegment(sketch, "E3.7.8.2", {"start": v(103.99, 114.3) * mm, "end": v(114.3, 114.3) * mm});
            skLineSegment(sketch, "E3.7.8.3", {"start": v(114.3, 114.3) * mm, "end": v(114.3, 124.61) * mm});
            skLineSegment(sketch, "E3.7.9.0", {"start": v(103.99, 127) * mm, "end": v(103.99, 137.31) * mm});
            skLineSegment(sketch, "E3.7.9.1", {"start": v(103.99, 137.31) * mm, "end": v(114.3, 137.31) * mm});
            skLineSegment(sketch, "E3.7.9.2", {"start": v(103.99, 127) * mm, "end": v(114.3, 127) * mm});
            skLineSegment(sketch, "E3.7.9.3", {"start": v(114.3, 127) * mm, "end": v(114.3, 137.31) * mm});
            skLineSegment(sketch, "E3.7.10.0", {"start": v(103.99, 139.7) * mm, "end": v(103.99, 150.01) * mm});
            skLineSegment(sketch, "E3.7.10.1", {"start": v(103.99, 150.01) * mm, "end": v(114.3, 150.01) * mm});
            skLineSegment(sketch, "E3.7.10.2", {"start": v(103.99, 139.7) * mm, "end": v(114.3, 139.7) * mm});
            skLineSegment(sketch, "E3.7.10.3", {"start": v(114.3, 139.7) * mm, "end": v(114.3, 150.01) * mm});
            skLineSegment(sketch, "E3.7.11.0", {"start": v(103.99, 152.4) * mm, "end": v(103.99, 162.71) * mm});
            skLineSegment(sketch, "E3.7.11.1", {"start": v(103.99, 162.71) * mm, "end": v(114.3, 162.71) * mm});
            skLineSegment(sketch, "E3.7.11.2", {"start": v(103.99, 152.4) * mm, "end": v(114.3, 152.4) * mm});
            skLineSegment(sketch, "E3.7.11.3", {"start": v(114.3, 152.4) * mm, "end": v(114.3, 162.71) * mm});
            skLineSegment(sketch, "E3.7.12.0", {"start": v(103.99, 165.1) * mm, "end": v(103.99, 175.41) * mm});
            skLineSegment(sketch, "E3.7.12.1", {"start": v(103.99, 175.41) * mm, "end": v(114.3, 175.41) * mm});
            skLineSegment(sketch, "E3.7.12.2", {"start": v(103.99, 165.1) * mm, "end": v(114.3, 165.1) * mm});
            skLineSegment(sketch, "E3.7.12.3", {"start": v(114.3, 165.1) * mm, "end": v(114.3, 175.41) * mm});
            skLineSegment(sketch, "E3.7.13.0", {"start": v(103.99, 177.8) * mm, "end": v(103.99, 188.11) * mm});
            skLineSegment(sketch, "E3.7.13.1", {"start": v(103.99, 188.11) * mm, "end": v(114.3, 188.11) * mm});
            skLineSegment(sketch, "E3.7.13.2", {"start": v(103.99, 177.8) * mm, "end": v(114.3, 177.8) * mm});
            skLineSegment(sketch, "E3.7.13.3", {"start": v(114.3, 177.8) * mm, "end": v(114.3, 188.11) * mm});
            skLineSegment(sketch, "E3.7.14.0", {"start": v(103.99, 190.5) * mm, "end": v(103.99, 200.81) * mm});
            skLineSegment(sketch, "E3.7.14.1", {"start": v(103.99, 200.81) * mm, "end": v(114.3, 200.81) * mm});
            skLineSegment(sketch, "E3.7.14.2", {"start": v(103.99, 190.5) * mm, "end": v(114.3, 190.5) * mm});
            skLineSegment(sketch, "E3.7.14.3", {"start": v(114.3, 190.5) * mm, "end": v(114.3, 200.81) * mm});
            skLineSegment(sketch, "E3.7.15.0", {"start": v(103.99, 203.2) * mm, "end": v(103.99, 213.51) * mm});
            skLineSegment(sketch, "E3.7.15.1", {"start": v(103.99, 213.51) * mm, "end": v(114.3, 213.51) * mm});
            skLineSegment(sketch, "E3.7.15.2", {"start": v(103.99, 203.2) * mm, "end": v(114.3, 203.2) * mm});
            skLineSegment(sketch, "E3.7.15.3", {"start": v(114.3, 203.2) * mm, "end": v(114.3, 213.51) * mm});
            skLineSegment(sketch, "E3.7.16.0", {"start": v(103.99, 215.9) * mm, "end": v(103.99, 226.21) * mm});
            skLineSegment(sketch, "E3.7.16.1", {"start": v(103.99, 226.21) * mm, "end": v(114.3, 226.21) * mm});
            skLineSegment(sketch, "E3.7.16.2", {"start": v(103.99, 215.9) * mm, "end": v(114.3, 215.9) * mm});
            skLineSegment(sketch, "E3.7.16.3", {"start": v(114.3, 215.9) * mm, "end": v(114.3, 226.21) * mm});
            skLineSegment(sketch, "E3.7.17.0", {"start": v(103.99, 228.6) * mm, "end": v(103.99, 238.91) * mm});
            skLineSegment(sketch, "E3.7.17.1", {"start": v(103.99, 238.91) * mm, "end": v(114.3, 238.91) * mm});
            skLineSegment(sketch, "E3.7.17.2", {"start": v(103.99, 228.6) * mm, "end": v(114.3, 228.6) * mm});
            skLineSegment(sketch, "E3.7.17.3", {"start": v(114.3, 228.6) * mm, "end": v(114.3, 238.91) * mm});
            skLineSegment(sketch, "E3.7.18.0", {"start": v(103.99, 241.3) * mm, "end": v(103.99, 251.61) * mm});
            skLineSegment(sketch, "E3.7.18.1", {"start": v(103.99, 251.61) * mm, "end": v(114.3, 251.61) * mm});
            skLineSegment(sketch, "E3.7.18.2", {"start": v(103.99, 241.3) * mm, "end": v(114.3, 241.3) * mm});
            skLineSegment(sketch, "E3.7.18.3", {"start": v(114.3, 241.3) * mm, "end": v(114.3, 251.61) * mm});
            skLineSegment(sketch, "E3.7.19.0", {"start": v(103.99, 254) * mm, "end": v(103.99, 264.31) * mm});
            skLineSegment(sketch, "E3.7.19.1", {"start": v(103.99, 264.31) * mm, "end": v(114.3, 264.31) * mm});
            skLineSegment(sketch, "E3.7.19.2", {"start": v(103.99, 254) * mm, "end": v(114.3, 254) * mm});
            skLineSegment(sketch, "E3.7.19.3", {"start": v(114.3, 254) * mm, "end": v(114.3, 264.31) * mm});
            skLineSegment(sketch, "E3.7.20.0", {"start": v(103.99, 266.7) * mm, "end": v(103.99, 277.01) * mm});
            skLineSegment(sketch, "E3.7.20.1", {"start": v(103.99, 277.01) * mm, "end": v(114.3, 277.01) * mm});
            skLineSegment(sketch, "E3.7.20.2", {"start": v(103.99, 266.7) * mm, "end": v(114.3, 266.7) * mm});
            skLineSegment(sketch, "E3.7.20.3", {"start": v(114.3, 266.7) * mm, "end": v(114.3, 277.01) * mm});
            skLineSegment(sketch, "E3.7.21.0", {"start": v(103.99, 279.4) * mm, "end": v(103.99, 289.71) * mm});
            skLineSegment(sketch, "E3.7.21.1", {"start": v(103.99, 289.71) * mm, "end": v(114.3, 289.71) * mm});
            skLineSegment(sketch, "E3.7.21.2", {"start": v(103.99, 279.4) * mm, "end": v(114.3, 279.4) * mm});
            skLineSegment(sketch, "E3.7.21.3", {"start": v(114.3, 279.4) * mm, "end": v(114.3, 289.71) * mm});
            skLineSegment(sketch, "E3.8.0.0", {"start": v(116.69, 12.7) * mm, "end": v(116.69, 23.01) * mm});
            skLineSegment(sketch, "E3.8.0.1", {"start": v(116.69, 23.01) * mm, "end": v(127, 23.01) * mm});
            skLineSegment(sketch, "E3.8.0.2", {"start": v(116.69, 12.7) * mm, "end": v(127, 12.7) * mm});
            skLineSegment(sketch, "E3.8.0.3", {"start": v(127, 12.7) * mm, "end": v(127, 23.01) * mm});
            skLineSegment(sketch, "E3.8.1.0", {"start": v(116.69, 25.4) * mm, "end": v(116.69, 35.71) * mm});
            skLineSegment(sketch, "E3.8.1.1", {"start": v(116.69, 35.71) * mm, "end": v(127, 35.71) * mm});
            skLineSegment(sketch, "E3.8.1.2", {"start": v(116.69, 25.4) * mm, "end": v(127, 25.4) * mm});
            skLineSegment(sketch, "E3.8.1.3", {"start": v(127, 25.4) * mm, "end": v(127, 35.71) * mm});
            skLineSegment(sketch, "E3.8.2.0", {"start": v(116.69, 38.1) * mm, "end": v(116.69, 48.41) * mm});
            skLineSegment(sketch, "E3.8.2.1", {"start": v(116.69, 48.41) * mm, "end": v(127, 48.41) * mm});
            skLineSegment(sketch, "E3.8.2.2", {"start": v(116.69, 38.1) * mm, "end": v(127, 38.1) * mm});
            skLineSegment(sketch, "E3.8.2.3", {"start": v(127, 38.1) * mm, "end": v(127, 48.41) * mm});
            skLineSegment(sketch, "E3.8.3.0", {"start": v(116.69, 50.8) * mm, "end": v(116.69, 61.11) * mm});
            skLineSegment(sketch, "E3.8.3.1", {"start": v(116.69, 61.11) * mm, "end": v(127, 61.11) * mm});
            skLineSegment(sketch, "E3.8.3.2", {"start": v(116.69, 50.8) * mm, "end": v(127, 50.8) * mm});
            skLineSegment(sketch, "E3.8.3.3", {"start": v(127, 50.8) * mm, "end": v(127, 61.11) * mm});
            skLineSegment(sketch, "E3.8.4.0", {"start": v(116.69, 63.5) * mm, "end": v(116.69, 73.81) * mm});
            skLineSegment(sketch, "E3.8.4.1", {"start": v(116.69, 73.81) * mm, "end": v(127, 73.81) * mm});
            skLineSegment(sketch, "E3.8.4.2", {"start": v(116.69, 63.5) * mm, "end": v(127, 63.5) * mm});
            skLineSegment(sketch, "E3.8.4.3", {"start": v(127, 63.5) * mm, "end": v(127, 73.81) * mm});
            skLineSegment(sketch, "E3.8.5.0", {"start": v(116.69, 76.2) * mm, "end": v(116.69, 86.51) * mm});
            skLineSegment(sketch, "E3.8.5.1", {"start": v(116.69, 86.51) * mm, "end": v(127, 86.51) * mm});
            skLineSegment(sketch, "E3.8.5.2", {"start": v(116.69, 76.2) * mm, "end": v(127, 76.2) * mm});
            skLineSegment(sketch, "E3.8.5.3", {"start": v(127, 76.2) * mm, "end": v(127, 86.51) * mm});
            skLineSegment(sketch, "E3.8.6.0", {"start": v(116.69, 88.9) * mm, "end": v(116.69, 99.21) * mm});
            skLineSegment(sketch, "E3.8.6.1", {"start": v(116.69, 99.21) * mm, "end": v(127, 99.21) * mm});
            skLineSegment(sketch, "E3.8.6.2", {"start": v(116.69, 88.9) * mm, "end": v(127, 88.9) * mm});
            skLineSegment(sketch, "E3.8.6.3", {"start": v(127, 88.9) * mm, "end": v(127, 99.21) * mm});
            skLineSegment(sketch, "E3.8.7.0", {"start": v(116.69, 101.6) * mm, "end": v(116.69, 111.91) * mm});
            skLineSegment(sketch, "E3.8.7.1", {"start": v(116.69, 111.91) * mm, "end": v(127, 111.91) * mm});
            skLineSegment(sketch, "E3.8.7.2", {"start": v(116.69, 101.6) * mm, "end": v(127, 101.6) * mm});
            skLineSegment(sketch, "E3.8.7.3", {"start": v(127, 101.6) * mm, "end": v(127, 111.91) * mm});
            skLineSegment(sketch, "E3.8.8.0", {"start": v(116.69, 114.3) * mm, "end": v(116.69, 124.61) * mm});
            skLineSegment(sketch, "E3.8.8.1", {"start": v(116.69, 124.61) * mm, "end": v(127, 124.61) * mm});
            skLineSegment(sketch, "E3.8.8.2", {"start": v(116.69, 114.3) * mm, "end": v(127, 114.3) * mm});
            skLineSegment(sketch, "E3.8.8.3", {"start": v(127, 114.3) * mm, "end": v(127, 124.61) * mm});
            skLineSegment(sketch, "E3.8.9.0", {"start": v(116.69, 127) * mm, "end": v(116.69, 137.31) * mm});
            skLineSegment(sketch, "E3.8.9.1", {"start": v(116.69, 137.31) * mm, "end": v(127, 137.31) * mm});
            skLineSegment(sketch, "E3.8.9.2", {"start": v(116.69, 127) * mm, "end": v(127, 127) * mm});
            skLineSegment(sketch, "E3.8.9.3", {"start": v(127, 127) * mm, "end": v(127, 137.31) * mm});
            skLineSegment(sketch, "E3.8.10.0", {"start": v(116.69, 139.7) * mm, "end": v(116.69, 150.01) * mm});
            skLineSegment(sketch, "E3.8.10.1", {"start": v(116.69, 150.01) * mm, "end": v(127, 150.01) * mm});
            skLineSegment(sketch, "E3.8.10.2", {"start": v(116.69, 139.7) * mm, "end": v(127, 139.7) * mm});
            skLineSegment(sketch, "E3.8.10.3", {"start": v(127, 139.7) * mm, "end": v(127, 150.01) * mm});
            skLineSegment(sketch, "E3.8.11.0", {"start": v(116.69, 152.4) * mm, "end": v(116.69, 162.71) * mm});
            skLineSegment(sketch, "E3.8.11.1", {"start": v(116.69, 162.71) * mm, "end": v(127, 162.71) * mm});
            skLineSegment(sketch, "E3.8.11.2", {"start": v(116.69, 152.4) * mm, "end": v(127, 152.4) * mm});
            skLineSegment(sketch, "E3.8.11.3", {"start": v(127, 152.4) * mm, "end": v(127, 162.71) * mm});
            skLineSegment(sketch, "E3.8.12.0", {"start": v(116.69, 165.1) * mm, "end": v(116.69, 175.41) * mm});
            skLineSegment(sketch, "E3.8.12.1", {"start": v(116.69, 175.41) * mm, "end": v(127, 175.41) * mm});
            skLineSegment(sketch, "E3.8.12.2", {"start": v(116.69, 165.1) * mm, "end": v(127, 165.1) * mm});
            skLineSegment(sketch, "E3.8.12.3", {"start": v(127, 165.1) * mm, "end": v(127, 175.41) * mm});
            skLineSegment(sketch, "E3.8.13.0", {"start": v(116.69, 177.8) * mm, "end": v(116.69, 188.11) * mm});
            skLineSegment(sketch, "E3.8.13.1", {"start": v(116.69, 188.11) * mm, "end": v(127, 188.11) * mm});
            skLineSegment(sketch, "E3.8.13.2", {"start": v(116.69, 177.8) * mm, "end": v(127, 177.8) * mm});
            skLineSegment(sketch, "E3.8.13.3", {"start": v(127, 177.8) * mm, "end": v(127, 188.11) * mm});
            skLineSegment(sketch, "E3.8.14.0", {"start": v(116.69, 190.5) * mm, "end": v(116.69, 200.81) * mm});
            skLineSegment(sketch, "E3.8.14.1", {"start": v(116.69, 200.81) * mm, "end": v(127, 200.81) * mm});
            skLineSegment(sketch, "E3.8.14.2", {"start": v(116.69, 190.5) * mm, "end": v(127, 190.5) * mm});
            skLineSegment(sketch, "E3.8.14.3", {"start": v(127, 190.5) * mm, "end": v(127, 200.81) * mm});
            skLineSegment(sketch, "E3.8.15.0", {"start": v(116.69, 203.2) * mm, "end": v(116.69, 213.51) * mm});
            skLineSegment(sketch, "E3.8.15.1", {"start": v(116.69, 213.51) * mm, "end": v(127, 213.51) * mm});
            skLineSegment(sketch, "E3.8.15.2", {"start": v(116.69, 203.2) * mm, "end": v(127, 203.2) * mm});
            skLineSegment(sketch, "E3.8.15.3", {"start": v(127, 203.2) * mm, "end": v(127, 213.51) * mm});
            skLineSegment(sketch, "E3.8.16.0", {"start": v(116.69, 215.9) * mm, "end": v(116.69, 226.21) * mm});
            skLineSegment(sketch, "E3.8.16.1", {"start": v(116.69, 226.21) * mm, "end": v(127, 226.21) * mm});
            skLineSegment(sketch, "E3.8.16.2", {"start": v(116.69, 215.9) * mm, "end": v(127, 215.9) * mm});
            skLineSegment(sketch, "E3.8.16.3", {"start": v(127, 215.9) * mm, "end": v(127, 226.21) * mm});
            skLineSegment(sketch, "E3.8.17.0", {"start": v(116.69, 228.6) * mm, "end": v(116.69, 238.91) * mm});
            skLineSegment(sketch, "E3.8.17.1", {"start": v(116.69, 238.91) * mm, "end": v(127, 238.91) * mm});
            skLineSegment(sketch, "E3.8.17.2", {"start": v(116.69, 228.6) * mm, "end": v(127, 228.6) * mm});
            skLineSegment(sketch, "E3.8.17.3", {"start": v(127, 228.6) * mm, "end": v(127, 238.91) * mm});
            skLineSegment(sketch, "E3.8.18.0", {"start": v(116.69, 241.3) * mm, "end": v(116.69, 251.61) * mm});
            skLineSegment(sketch, "E3.8.18.1", {"start": v(116.69, 251.61) * mm, "end": v(127, 251.61) * mm});
            skLineSegment(sketch, "E3.8.18.2", {"start": v(116.69, 241.3) * mm, "end": v(127, 241.3) * mm});
            skLineSegment(sketch, "E3.8.18.3", {"start": v(127, 241.3) * mm, "end": v(127, 251.61) * mm});
            skLineSegment(sketch, "E3.8.19.0", {"start": v(116.69, 254) * mm, "end": v(116.69, 264.31) * mm});
            skLineSegment(sketch, "E3.8.19.1", {"start": v(116.69, 264.31) * mm, "end": v(127, 264.31) * mm});
            skLineSegment(sketch, "E3.8.19.2", {"start": v(116.69, 254) * mm, "end": v(127, 254) * mm});
            skLineSegment(sketch, "E3.8.19.3", {"start": v(127, 254) * mm, "end": v(127, 264.31) * mm});
            skLineSegment(sketch, "E3.8.20.0", {"start": v(116.69, 266.7) * mm, "end": v(116.69, 277.01) * mm});
            skLineSegment(sketch, "E3.8.20.1", {"start": v(116.69, 277.01) * mm, "end": v(127, 277.01) * mm});
            skLineSegment(sketch, "E3.8.20.2", {"start": v(116.69, 266.7) * mm, "end": v(127, 266.7) * mm});
            skLineSegment(sketch, "E3.8.20.3", {"start": v(127, 266.7) * mm, "end": v(127, 277.01) * mm});
            skLineSegment(sketch, "E3.8.21.0", {"start": v(116.69, 279.4) * mm, "end": v(116.69, 289.71) * mm});
            skLineSegment(sketch, "E3.8.21.1", {"start": v(116.69, 289.71) * mm, "end": v(127, 289.71) * mm});
            skLineSegment(sketch, "E3.8.21.2", {"start": v(116.69, 279.4) * mm, "end": v(127, 279.4) * mm});
            skLineSegment(sketch, "E3.8.21.3", {"start": v(127, 279.4) * mm, "end": v(127, 289.71) * mm});
            skLineSegment(sketch, "E3.9.0.0", {"start": v(129.39, 12.7) * mm, "end": v(129.39, 23.01) * mm});
            skLineSegment(sketch, "E3.9.0.1", {"start": v(129.39, 23.01) * mm, "end": v(139.7, 23.01) * mm});
            skLineSegment(sketch, "E3.9.0.2", {"start": v(129.39, 12.7) * mm, "end": v(139.7, 12.7) * mm});
            skLineSegment(sketch, "E3.9.0.3", {"start": v(139.7, 12.7) * mm, "end": v(139.7, 23.01) * mm});
            skLineSegment(sketch, "E3.9.1.0", {"start": v(129.39, 25.4) * mm, "end": v(129.39, 35.71) * mm});
            skLineSegment(sketch, "E3.9.1.1", {"start": v(129.39, 35.71) * mm, "end": v(139.7, 35.71) * mm});
            skLineSegment(sketch, "E3.9.1.2", {"start": v(129.39, 25.4) * mm, "end": v(139.7, 25.4) * mm});
            skLineSegment(sketch, "E3.9.1.3", {"start": v(139.7, 25.4) * mm, "end": v(139.7, 35.71) * mm});
            skLineSegment(sketch, "E3.9.2.0", {"start": v(129.39, 38.1) * mm, "end": v(129.39, 48.41) * mm});
            skLineSegment(sketch, "E3.9.2.1", {"start": v(129.39, 48.41) * mm, "end": v(139.7, 48.41) * mm});
            skLineSegment(sketch, "E3.9.2.2", {"start": v(129.39, 38.1) * mm, "end": v(139.7, 38.1) * mm});
            skLineSegment(sketch, "E3.9.2.3", {"start": v(139.7, 38.1) * mm, "end": v(139.7, 48.41) * mm});
            skLineSegment(sketch, "E3.9.3.0", {"start": v(129.39, 50.8) * mm, "end": v(129.39, 61.11) * mm});
            skLineSegment(sketch, "E3.9.3.1", {"start": v(129.39, 61.11) * mm, "end": v(139.7, 61.11) * mm});
            skLineSegment(sketch, "E3.9.3.2", {"start": v(129.39, 50.8) * mm, "end": v(139.7, 50.8) * mm});
            skLineSegment(sketch, "E3.9.3.3", {"start": v(139.7, 50.8) * mm, "end": v(139.7, 61.11) * mm});
            skLineSegment(sketch, "E3.9.4.0", {"start": v(129.39, 63.5) * mm, "end": v(129.39, 73.81) * mm});
            skLineSegment(sketch, "E3.9.4.1", {"start": v(129.39, 73.81) * mm, "end": v(139.7, 73.81) * mm});
            skLineSegment(sketch, "E3.9.4.2", {"start": v(129.39, 63.5) * mm, "end": v(139.7, 63.5) * mm});
            skLineSegment(sketch, "E3.9.4.3", {"start": v(139.7, 63.5) * mm, "end": v(139.7, 73.81) * mm});
            skLineSegment(sketch, "E3.9.5.0", {"start": v(129.39, 76.2) * mm, "end": v(129.39, 86.51) * mm});
            skLineSegment(sketch, "E3.9.5.1", {"start": v(129.39, 86.51) * mm, "end": v(139.7, 86.51) * mm});
            skLineSegment(sketch, "E3.9.5.2", {"start": v(129.39, 76.2) * mm, "end": v(139.7, 76.2) * mm});
            skLineSegment(sketch, "E3.9.5.3", {"start": v(139.7, 76.2) * mm, "end": v(139.7, 86.51) * mm});
            skLineSegment(sketch, "E3.9.6.0", {"start": v(129.39, 88.9) * mm, "end": v(129.39, 99.21) * mm});
            skLineSegment(sketch, "E3.9.6.1", {"start": v(129.39, 99.21) * mm, "end": v(139.7, 99.21) * mm});
            skLineSegment(sketch, "E3.9.6.2", {"start": v(129.39, 88.9) * mm, "end": v(139.7, 88.9) * mm});
            skLineSegment(sketch, "E3.9.6.3", {"start": v(139.7, 88.9) * mm, "end": v(139.7, 99.21) * mm});
            skLineSegment(sketch, "E3.9.7.0", {"start": v(129.39, 101.6) * mm, "end": v(129.39, 111.91) * mm});
            skLineSegment(sketch, "E3.9.7.1", {"start": v(129.39, 111.91) * mm, "end": v(139.7, 111.91) * mm});
            skLineSegment(sketch, "E3.9.7.2", {"start": v(129.39, 101.6) * mm, "end": v(139.7, 101.6) * mm});
            skLineSegment(sketch, "E3.9.7.3", {"start": v(139.7, 101.6) * mm, "end": v(139.7, 111.91) * mm});
            skLineSegment(sketch, "E3.9.8.0", {"start": v(129.39, 114.3) * mm, "end": v(129.39, 124.61) * mm});
            skLineSegment(sketch, "E3.9.8.1", {"start": v(129.39, 124.61) * mm, "end": v(139.7, 124.61) * mm});
            skLineSegment(sketch, "E3.9.8.2", {"start": v(129.39, 114.3) * mm, "end": v(139.7, 114.3) * mm});
            skLineSegment(sketch, "E3.9.8.3", {"start": v(139.7, 114.3) * mm, "end": v(139.7, 124.61) * mm});
            skLineSegment(sketch, "E3.9.9.0", {"start": v(129.39, 127) * mm, "end": v(129.39, 137.31) * mm});
            skLineSegment(sketch, "E3.9.9.1", {"start": v(129.39, 137.31) * mm, "end": v(139.7, 137.31) * mm});
            skLineSegment(sketch, "E3.9.9.2", {"start": v(129.39, 127) * mm, "end": v(139.7, 127) * mm});
            skLineSegment(sketch, "E3.9.9.3", {"start": v(139.7, 127) * mm, "end": v(139.7, 137.31) * mm});
            skLineSegment(sketch, "E3.9.10.0", {"start": v(129.39, 139.7) * mm, "end": v(129.39, 150.01) * mm});
            skLineSegment(sketch, "E3.9.10.1", {"start": v(129.39, 150.01) * mm, "end": v(139.7, 150.01) * mm});
            skLineSegment(sketch, "E3.9.10.2", {"start": v(129.39, 139.7) * mm, "end": v(139.7, 139.7) * mm});
            skLineSegment(sketch, "E3.9.10.3", {"start": v(139.7, 139.7) * mm, "end": v(139.7, 150.01) * mm});
            skLineSegment(sketch, "E3.9.11.0", {"start": v(129.39, 152.4) * mm, "end": v(129.39, 162.71) * mm});
            skLineSegment(sketch, "E3.9.11.1", {"start": v(129.39, 162.71) * mm, "end": v(139.7, 162.71) * mm});
            skLineSegment(sketch, "E3.9.11.2", {"start": v(129.39, 152.4) * mm, "end": v(139.7, 152.4) * mm});
            skLineSegment(sketch, "E3.9.11.3", {"start": v(139.7, 152.4) * mm, "end": v(139.7, 162.71) * mm});
            skLineSegment(sketch, "E3.9.12.0", {"start": v(129.39, 165.1) * mm, "end": v(129.39, 175.41) * mm});
            skLineSegment(sketch, "E3.9.12.1", {"start": v(129.39, 175.41) * mm, "end": v(139.7, 175.41) * mm});
            skLineSegment(sketch, "E3.9.12.2", {"start": v(129.39, 165.1) * mm, "end": v(139.7, 165.1) * mm});
            skLineSegment(sketch, "E3.9.12.3", {"start": v(139.7, 165.1) * mm, "end": v(139.7, 175.41) * mm});
            skLineSegment(sketch, "E3.9.13.0", {"start": v(129.39, 177.8) * mm, "end": v(129.39, 188.11) * mm});
            skLineSegment(sketch, "E3.9.13.1", {"start": v(129.39, 188.11) * mm, "end": v(139.7, 188.11) * mm});
            skLineSegment(sketch, "E3.9.13.2", {"start": v(129.39, 177.8) * mm, "end": v(139.7, 177.8) * mm});
            skLineSegment(sketch, "E3.9.13.3", {"start": v(139.7, 177.8) * mm, "end": v(139.7, 188.11) * mm});
            skLineSegment(sketch, "E3.9.14.0", {"start": v(129.39, 190.5) * mm, "end": v(129.39, 200.81) * mm});
            skLineSegment(sketch, "E3.9.14.1", {"start": v(129.39, 200.81) * mm, "end": v(139.7, 200.81) * mm});
            skLineSegment(sketch, "E3.9.14.2", {"start": v(129.39, 190.5) * mm, "end": v(139.7, 190.5) * mm});
            skLineSegment(sketch, "E3.9.14.3", {"start": v(139.7, 190.5) * mm, "end": v(139.7, 200.81) * mm});
            skLineSegment(sketch, "E3.9.15.0", {"start": v(129.39, 203.2) * mm, "end": v(129.39, 213.51) * mm});
            skLineSegment(sketch, "E3.9.15.1", {"start": v(129.39, 213.51) * mm, "end": v(139.7, 213.51) * mm});
            skLineSegment(sketch, "E3.9.15.2", {"start": v(129.39, 203.2) * mm, "end": v(139.7, 203.2) * mm});
            skLineSegment(sketch, "E3.9.15.3", {"start": v(139.7, 203.2) * mm, "end": v(139.7, 213.51) * mm});
            skLineSegment(sketch, "E3.9.16.0", {"start": v(129.39, 215.9) * mm, "end": v(129.39, 226.21) * mm});
            skLineSegment(sketch, "E3.9.16.1", {"start": v(129.39, 226.21) * mm, "end": v(139.7, 226.21) * mm});
            skLineSegment(sketch, "E3.9.16.2", {"start": v(129.39, 215.9) * mm, "end": v(139.7, 215.9) * mm});
            skLineSegment(sketch, "E3.9.16.3", {"start": v(139.7, 215.9) * mm, "end": v(139.7, 226.21) * mm});
            skLineSegment(sketch, "E3.9.17.0", {"start": v(129.39, 228.6) * mm, "end": v(129.39, 238.91) * mm});
            skLineSegment(sketch, "E3.9.17.1", {"start": v(129.39, 238.91) * mm, "end": v(139.7, 238.91) * mm});
            skLineSegment(sketch, "E3.9.17.2", {"start": v(129.39, 228.6) * mm, "end": v(139.7, 228.6) * mm});
            skLineSegment(sketch, "E3.9.17.3", {"start": v(139.7, 228.6) * mm, "end": v(139.7, 238.91) * mm});
            skLineSegment(sketch, "E3.9.18.0", {"start": v(129.39, 241.3) * mm, "end": v(129.39, 251.61) * mm});
            skLineSegment(sketch, "E3.9.18.1", {"start": v(129.39, 251.61) * mm, "end": v(139.7, 251.61) * mm});
            skLineSegment(sketch, "E3.9.18.2", {"start": v(129.39, 241.3) * mm, "end": v(139.7, 241.3) * mm});
            skLineSegment(sketch, "E3.9.18.3", {"start": v(139.7, 241.3) * mm, "end": v(139.7, 251.61) * mm});
            skLineSegment(sketch, "E3.9.19.0", {"start": v(129.39, 254) * mm, "end": v(129.39, 264.31) * mm});
            skLineSegment(sketch, "E3.9.19.1", {"start": v(129.39, 264.31) * mm, "end": v(139.7, 264.31) * mm});
            skLineSegment(sketch, "E3.9.19.2", {"start": v(129.39, 254) * mm, "end": v(139.7, 254) * mm});
            skLineSegment(sketch, "E3.9.19.3", {"start": v(139.7, 254) * mm, "end": v(139.7, 264.31) * mm});
            skLineSegment(sketch, "E3.9.20.0", {"start": v(129.39, 266.7) * mm, "end": v(129.39, 277.01) * mm});
            skLineSegment(sketch, "E3.9.20.1", {"start": v(129.39, 277.01) * mm, "end": v(139.7, 277.01) * mm});
            skLineSegment(sketch, "E3.9.20.2", {"start": v(129.39, 266.7) * mm, "end": v(139.7, 266.7) * mm});
            skLineSegment(sketch, "E3.9.20.3", {"start": v(139.7, 266.7) * mm, "end": v(139.7, 277.01) * mm});
            skLineSegment(sketch, "E3.9.21.0", {"start": v(129.39, 279.4) * mm, "end": v(129.39, 289.71) * mm});
            skLineSegment(sketch, "E3.9.21.1", {"start": v(129.39, 289.71) * mm, "end": v(139.7, 289.71) * mm});
            skLineSegment(sketch, "E3.9.21.2", {"start": v(129.39, 279.4) * mm, "end": v(139.7, 279.4) * mm});
            skLineSegment(sketch, "E3.9.21.3", {"start": v(139.7, 279.4) * mm, "end": v(139.7, 289.71) * mm});
            skLineSegment(sketch, "E3.10.0.0", {"start": v(142.09, 12.7) * mm, "end": v(142.09, 23.01) * mm});
            skLineSegment(sketch, "E3.10.0.1", {"start": v(142.09, 23.01) * mm, "end": v(152.4, 23.01) * mm});
            skLineSegment(sketch, "E3.10.0.2", {"start": v(142.09, 12.7) * mm, "end": v(152.4, 12.7) * mm});
            skLineSegment(sketch, "E3.10.0.3", {"start": v(152.4, 12.7) * mm, "end": v(152.4, 23.01) * mm});
            skLineSegment(sketch, "E3.10.1.0", {"start": v(142.09, 25.4) * mm, "end": v(142.09, 35.71) * mm});
            skLineSegment(sketch, "E3.10.1.1", {"start": v(142.09, 35.71) * mm, "end": v(152.4, 35.71) * mm});
            skLineSegment(sketch, "E3.10.1.2", {"start": v(142.09, 25.4) * mm, "end": v(152.4, 25.4) * mm});
            skLineSegment(sketch, "E3.10.1.3", {"start": v(152.4, 25.4) * mm, "end": v(152.4, 35.71) * mm});
            skLineSegment(sketch, "E3.10.2.0", {"start": v(142.09, 38.1) * mm, "end": v(142.09, 48.41) * mm});
            skLineSegment(sketch, "E3.10.2.1", {"start": v(142.09, 48.41) * mm, "end": v(152.4, 48.41) * mm});
            skLineSegment(sketch, "E3.10.2.2", {"start": v(142.09, 38.1) * mm, "end": v(152.4, 38.1) * mm});
            skLineSegment(sketch, "E3.10.2.3", {"start": v(152.4, 38.1) * mm, "end": v(152.4, 48.41) * mm});
            skLineSegment(sketch, "E3.10.3.0", {"start": v(142.09, 50.8) * mm, "end": v(142.09, 61.11) * mm});
            skLineSegment(sketch, "E3.10.3.1", {"start": v(142.09, 61.11) * mm, "end": v(152.4, 61.11) * mm});
            skLineSegment(sketch, "E3.10.3.2", {"start": v(142.09, 50.8) * mm, "end": v(152.4, 50.8) * mm});
            skLineSegment(sketch, "E3.10.3.3", {"start": v(152.4, 50.8) * mm, "end": v(152.4, 61.11) * mm});
            skLineSegment(sketch, "E3.10.4.0", {"start": v(142.09, 63.5) * mm, "end": v(142.09, 73.81) * mm});
            skLineSegment(sketch, "E3.10.4.1", {"start": v(142.09, 73.81) * mm, "end": v(152.4, 73.81) * mm});
            skLineSegment(sketch, "E3.10.4.2", {"start": v(142.09, 63.5) * mm, "end": v(152.4, 63.5) * mm});
            skLineSegment(sketch, "E3.10.4.3", {"start": v(152.4, 63.5) * mm, "end": v(152.4, 73.81) * mm});
            skLineSegment(sketch, "E3.10.5.0", {"start": v(142.09, 76.2) * mm, "end": v(142.09, 86.51) * mm});
            skLineSegment(sketch, "E3.10.5.1", {"start": v(142.09, 86.51) * mm, "end": v(152.4, 86.51) * mm});
            skLineSegment(sketch, "E3.10.5.2", {"start": v(142.09, 76.2) * mm, "end": v(152.4, 76.2) * mm});
            skLineSegment(sketch, "E3.10.5.3", {"start": v(152.4, 76.2) * mm, "end": v(152.4, 86.51) * mm});
            skLineSegment(sketch, "E3.10.6.0", {"start": v(142.09, 88.9) * mm, "end": v(142.09, 99.21) * mm});
            skLineSegment(sketch, "E3.10.6.1", {"start": v(142.09, 99.21) * mm, "end": v(152.4, 99.21) * mm});
            skLineSegment(sketch, "E3.10.6.2", {"start": v(142.09, 88.9) * mm, "end": v(152.4, 88.9) * mm});
            skLineSegment(sketch, "E3.10.6.3", {"start": v(152.4, 88.9) * mm, "end": v(152.4, 99.21) * mm});
            skLineSegment(sketch, "E3.10.7.0", {"start": v(142.09, 101.6) * mm, "end": v(142.09, 111.91) * mm});
            skLineSegment(sketch, "E3.10.7.1", {"start": v(142.09, 111.91) * mm, "end": v(152.4, 111.91) * mm});
            skLineSegment(sketch, "E3.10.7.2", {"start": v(142.09, 101.6) * mm, "end": v(152.4, 101.6) * mm});
            skLineSegment(sketch, "E3.10.7.3", {"start": v(152.4, 101.6) * mm, "end": v(152.4, 111.91) * mm});
            skLineSegment(sketch, "E3.10.8.0", {"start": v(142.09, 114.3) * mm, "end": v(142.09, 124.61) * mm});
            skLineSegment(sketch, "E3.10.8.1", {"start": v(142.09, 124.61) * mm, "end": v(152.4, 124.61) * mm});
            skLineSegment(sketch, "E3.10.8.2", {"start": v(142.09, 114.3) * mm, "end": v(152.4, 114.3) * mm});
            skLineSegment(sketch, "E3.10.8.3", {"start": v(152.4, 114.3) * mm, "end": v(152.4, 124.61) * mm});
            skLineSegment(sketch, "E3.10.9.0", {"start": v(142.09, 127) * mm, "end": v(142.09, 137.31) * mm});
            skLineSegment(sketch, "E3.10.9.1", {"start": v(142.09, 137.31) * mm, "end": v(152.4, 137.31) * mm});
            skLineSegment(sketch, "E3.10.9.2", {"start": v(142.09, 127) * mm, "end": v(152.4, 127) * mm});
            skLineSegment(sketch, "E3.10.9.3", {"start": v(152.4, 127) * mm, "end": v(152.4, 137.31) * mm});
            skLineSegment(sketch, "E3.10.10.0", {"start": v(142.09, 139.7) * mm, "end": v(142.09, 150.01) * mm});
            skLineSegment(sketch, "E3.10.10.1", {"start": v(142.09, 150.01) * mm, "end": v(152.4, 150.01) * mm});
            skLineSegment(sketch, "E3.10.10.2", {"start": v(142.09, 139.7) * mm, "end": v(152.4, 139.7) * mm});
            skLineSegment(sketch, "E3.10.10.3", {"start": v(152.4, 139.7) * mm, "end": v(152.4, 150.01) * mm});
            skLineSegment(sketch, "E3.10.11.0", {"start": v(142.09, 152.4) * mm, "end": v(142.09, 162.71) * mm});
            skLineSegment(sketch, "E3.10.11.1", {"start": v(142.09, 162.71) * mm, "end": v(152.4, 162.71) * mm});
            skLineSegment(sketch, "E3.10.11.2", {"start": v(142.09, 152.4) * mm, "end": v(152.4, 152.4) * mm});
            skLineSegment(sketch, "E3.10.11.3", {"start": v(152.4, 152.4) * mm, "end": v(152.4, 162.71) * mm});
            skLineSegment(sketch, "E3.10.12.0", {"start": v(142.09, 165.1) * mm, "end": v(142.09, 175.41) * mm});
            skLineSegment(sketch, "E3.10.12.1", {"start": v(142.09, 175.41) * mm, "end": v(152.4, 175.41) * mm});
            skLineSegment(sketch, "E3.10.12.2", {"start": v(142.09, 165.1) * mm, "end": v(152.4, 165.1) * mm});
            skLineSegment(sketch, "E3.10.12.3", {"start": v(152.4, 165.1) * mm, "end": v(152.4, 175.41) * mm});
            skLineSegment(sketch, "E3.10.13.0", {"start": v(142.09, 177.8) * mm, "end": v(142.09, 188.11) * mm});
            skLineSegment(sketch, "E3.10.13.1", {"start": v(142.09, 188.11) * mm, "end": v(152.4, 188.11) * mm});
            skLineSegment(sketch, "E3.10.13.2", {"start": v(142.09, 177.8) * mm, "end": v(152.4, 177.8) * mm});
            skLineSegment(sketch, "E3.10.13.3", {"start": v(152.4, 177.8) * mm, "end": v(152.4, 188.11) * mm});
            skLineSegment(sketch, "E3.10.14.0", {"start": v(142.09, 190.5) * mm, "end": v(142.09, 200.81) * mm});
            skLineSegment(sketch, "E3.10.14.1", {"start": v(142.09, 200.81) * mm, "end": v(152.4, 200.81) * mm});
            skLineSegment(sketch, "E3.10.14.2", {"start": v(142.09, 190.5) * mm, "end": v(152.4, 190.5) * mm});
            skLineSegment(sketch, "E3.10.14.3", {"start": v(152.4, 190.5) * mm, "end": v(152.4, 200.81) * mm});
            skLineSegment(sketch, "E3.10.15.0", {"start": v(142.09, 203.2) * mm, "end": v(142.09, 213.51) * mm});
            skLineSegment(sketch, "E3.10.15.1", {"start": v(142.09, 213.51) * mm, "end": v(152.4, 213.51) * mm});
            skLineSegment(sketch, "E3.10.15.2", {"start": v(142.09, 203.2) * mm, "end": v(152.4, 203.2) * mm});
            skLineSegment(sketch, "E3.10.15.3", {"start": v(152.4, 203.2) * mm, "end": v(152.4, 213.51) * mm});
            skLineSegment(sketch, "E3.10.16.0", {"start": v(142.09, 215.9) * mm, "end": v(142.09, 226.21) * mm});
            skLineSegment(sketch, "E3.10.16.1", {"start": v(142.09, 226.21) * mm, "end": v(152.4, 226.21) * mm});
            skLineSegment(sketch, "E3.10.16.2", {"start": v(142.09, 215.9) * mm, "end": v(152.4, 215.9) * mm});
            skLineSegment(sketch, "E3.10.16.3", {"start": v(152.4, 215.9) * mm, "end": v(152.4, 226.21) * mm});
            skLineSegment(sketch, "E3.10.17.0", {"start": v(142.09, 228.6) * mm, "end": v(142.09, 238.91) * mm});
            skLineSegment(sketch, "E3.10.17.1", {"start": v(142.09, 238.91) * mm, "end": v(152.4, 238.91) * mm});
            skLineSegment(sketch, "E3.10.17.2", {"start": v(142.09, 228.6) * mm, "end": v(152.4, 228.6) * mm});
            skLineSegment(sketch, "E3.10.17.3", {"start": v(152.4, 228.6) * mm, "end": v(152.4, 238.91) * mm});
            skLineSegment(sketch, "E3.10.18.0", {"start": v(142.09, 241.3) * mm, "end": v(142.09, 251.61) * mm});
            skLineSegment(sketch, "E3.10.18.1", {"start": v(142.09, 251.61) * mm, "end": v(152.4, 251.61) * mm});
            skLineSegment(sketch, "E3.10.18.2", {"start": v(142.09, 241.3) * mm, "end": v(152.4, 241.3) * mm});
            skLineSegment(sketch, "E3.10.18.3", {"start": v(152.4, 241.3) * mm, "end": v(152.4, 251.61) * mm});
            skLineSegment(sketch, "E3.10.19.0", {"start": v(142.09, 254) * mm, "end": v(142.09, 264.31) * mm});
            skLineSegment(sketch, "E3.10.19.1", {"start": v(142.09, 264.31) * mm, "end": v(152.4, 264.31) * mm});
            skLineSegment(sketch, "E3.10.19.2", {"start": v(142.09, 254) * mm, "end": v(152.4, 254) * mm});
            skLineSegment(sketch, "E3.10.19.3", {"start": v(152.4, 254) * mm, "end": v(152.4, 264.31) * mm});
            skLineSegment(sketch, "E3.10.20.0", {"start": v(142.09, 266.7) * mm, "end": v(142.09, 277.01) * mm});
            skLineSegment(sketch, "E3.10.20.1", {"start": v(142.09, 277.01) * mm, "end": v(152.4, 277.01) * mm});
            skLineSegment(sketch, "E3.10.20.2", {"start": v(142.09, 266.7) * mm, "end": v(152.4, 266.7) * mm});
            skLineSegment(sketch, "E3.10.20.3", {"start": v(152.4, 266.7) * mm, "end": v(152.4, 277.01) * mm});
            skLineSegment(sketch, "E3.10.21.0", {"start": v(142.09, 279.4) * mm, "end": v(142.09, 289.71) * mm});
            skLineSegment(sketch, "E3.10.21.1", {"start": v(142.09, 289.71) * mm, "end": v(152.4, 289.71) * mm});
            skLineSegment(sketch, "E3.10.21.2", {"start": v(142.09, 279.4) * mm, "end": v(152.4, 279.4) * mm});
            skLineSegment(sketch, "E3.10.21.3", {"start": v(152.4, 279.4) * mm, "end": v(152.4, 289.71) * mm});
            skLineSegment(sketch, "E3.11.0.0", {"start": v(154.79, 12.7) * mm, "end": v(154.79, 23.01) * mm});
            skLineSegment(sketch, "E3.11.0.1", {"start": v(154.79, 23.01) * mm, "end": v(165.1, 23.01) * mm});
            skLineSegment(sketch, "E3.11.0.2", {"start": v(154.79, 12.7) * mm, "end": v(165.1, 12.7) * mm});
            skLineSegment(sketch, "E3.11.0.3", {"start": v(165.1, 12.7) * mm, "end": v(165.1, 23.01) * mm});
            skLineSegment(sketch, "E3.11.1.0", {"start": v(154.79, 25.4) * mm, "end": v(154.79, 35.71) * mm});
            skLineSegment(sketch, "E3.11.1.1", {"start": v(154.79, 35.71) * mm, "end": v(165.1, 35.71) * mm});
            skLineSegment(sketch, "E3.11.1.2", {"start": v(154.79, 25.4) * mm, "end": v(165.1, 25.4) * mm});
            skLineSegment(sketch, "E3.11.1.3", {"start": v(165.1, 25.4) * mm, "end": v(165.1, 35.71) * mm});
            skLineSegment(sketch, "E3.11.2.0", {"start": v(154.79, 38.1) * mm, "end": v(154.79, 48.41) * mm});
            skLineSegment(sketch, "E3.11.2.1", {"start": v(154.79, 48.41) * mm, "end": v(165.1, 48.41) * mm});
            skLineSegment(sketch, "E3.11.2.2", {"start": v(154.79, 38.1) * mm, "end": v(165.1, 38.1) * mm});
            skLineSegment(sketch, "E3.11.2.3", {"start": v(165.1, 38.1) * mm, "end": v(165.1, 48.41) * mm});
            skLineSegment(sketch, "E3.11.3.0", {"start": v(154.79, 50.8) * mm, "end": v(154.79, 61.11) * mm});
            skLineSegment(sketch, "E3.11.3.1", {"start": v(154.79, 61.11) * mm, "end": v(165.1, 61.11) * mm});
            skLineSegment(sketch, "E3.11.3.2", {"start": v(154.79, 50.8) * mm, "end": v(165.1, 50.8) * mm});
            skLineSegment(sketch, "E3.11.3.3", {"start": v(165.1, 50.8) * mm, "end": v(165.1, 61.11) * mm});
            skLineSegment(sketch, "E3.11.4.0", {"start": v(154.79, 63.5) * mm, "end": v(154.79, 73.81) * mm});
            skLineSegment(sketch, "E3.11.4.1", {"start": v(154.79, 73.81) * mm, "end": v(165.1, 73.81) * mm});
            skLineSegment(sketch, "E3.11.4.2", {"start": v(154.79, 63.5) * mm, "end": v(165.1, 63.5) * mm});
            skLineSegment(sketch, "E3.11.4.3", {"start": v(165.1, 63.5) * mm, "end": v(165.1, 73.81) * mm});
            skLineSegment(sketch, "E3.11.5.0", {"start": v(154.79, 76.2) * mm, "end": v(154.79, 86.51) * mm});
            skLineSegment(sketch, "E3.11.5.1", {"start": v(154.79, 86.51) * mm, "end": v(165.1, 86.51) * mm});
            skLineSegment(sketch, "E3.11.5.2", {"start": v(154.79, 76.2) * mm, "end": v(165.1, 76.2) * mm});
            skLineSegment(sketch, "E3.11.5.3", {"start": v(165.1, 76.2) * mm, "end": v(165.1, 86.51) * mm});
            skLineSegment(sketch, "E3.11.6.0", {"start": v(154.79, 88.9) * mm, "end": v(154.79, 99.21) * mm});
            skLineSegment(sketch, "E3.11.6.1", {"start": v(154.79, 99.21) * mm, "end": v(165.1, 99.21) * mm});
            skLineSegment(sketch, "E3.11.6.2", {"start": v(154.79, 88.9) * mm, "end": v(165.1, 88.9) * mm});
            skLineSegment(sketch, "E3.11.6.3", {"start": v(165.1, 88.9) * mm, "end": v(165.1, 99.21) * mm});
            skLineSegment(sketch, "E3.11.7.0", {"start": v(154.79, 101.6) * mm, "end": v(154.79, 111.91) * mm});
            skLineSegment(sketch, "E3.11.7.1", {"start": v(154.79, 111.91) * mm, "end": v(165.1, 111.91) * mm});
            skLineSegment(sketch, "E3.11.7.2", {"start": v(154.79, 101.6) * mm, "end": v(165.1, 101.6) * mm});
            skLineSegment(sketch, "E3.11.7.3", {"start": v(165.1, 101.6) * mm, "end": v(165.1, 111.91) * mm});
            skLineSegment(sketch, "E3.11.8.0", {"start": v(154.79, 114.3) * mm, "end": v(154.79, 124.61) * mm});
            skLineSegment(sketch, "E3.11.8.1", {"start": v(154.79, 124.61) * mm, "end": v(165.1, 124.61) * mm});
            skLineSegment(sketch, "E3.11.8.2", {"start": v(154.79, 114.3) * mm, "end": v(165.1, 114.3) * mm});
            skLineSegment(sketch, "E3.11.8.3", {"start": v(165.1, 114.3) * mm, "end": v(165.1, 124.61) * mm});
            skLineSegment(sketch, "E3.11.9.0", {"start": v(154.79, 127) * mm, "end": v(154.79, 137.31) * mm});
            skLineSegment(sketch, "E3.11.9.1", {"start": v(154.79, 137.31) * mm, "end": v(165.1, 137.31) * mm});
            skLineSegment(sketch, "E3.11.9.2", {"start": v(154.79, 127) * mm, "end": v(165.1, 127) * mm});
            skLineSegment(sketch, "E3.11.9.3", {"start": v(165.1, 127) * mm, "end": v(165.1, 137.31) * mm});
            skLineSegment(sketch, "E3.11.10.0", {"start": v(154.79, 139.7) * mm, "end": v(154.79, 150.01) * mm});
            skLineSegment(sketch, "E3.11.10.1", {"start": v(154.79, 150.01) * mm, "end": v(165.1, 150.01) * mm});
            skLineSegment(sketch, "E3.11.10.2", {"start": v(154.79, 139.7) * mm, "end": v(165.1, 139.7) * mm});
            skLineSegment(sketch, "E3.11.10.3", {"start": v(165.1, 139.7) * mm, "end": v(165.1, 150.01) * mm});
            skLineSegment(sketch, "E3.11.11.0", {"start": v(154.79, 152.4) * mm, "end": v(154.79, 162.71) * mm});
            skLineSegment(sketch, "E3.11.11.1", {"start": v(154.79, 162.71) * mm, "end": v(165.1, 162.71) * mm});
            skLineSegment(sketch, "E3.11.11.2", {"start": v(154.79, 152.4) * mm, "end": v(165.1, 152.4) * mm});
            skLineSegment(sketch, "E3.11.11.3", {"start": v(165.1, 152.4) * mm, "end": v(165.1, 162.71) * mm});
            skLineSegment(sketch, "E3.11.12.0", {"start": v(154.79, 165.1) * mm, "end": v(154.79, 175.41) * mm});
            skLineSegment(sketch, "E3.11.12.1", {"start": v(154.79, 175.41) * mm, "end": v(165.1, 175.41) * mm});
            skLineSegment(sketch, "E3.11.12.2", {"start": v(154.79, 165.1) * mm, "end": v(165.1, 165.1) * mm});
            skLineSegment(sketch, "E3.11.12.3", {"start": v(165.1, 165.1) * mm, "end": v(165.1, 175.41) * mm});
            skLineSegment(sketch, "E3.11.13.0", {"start": v(154.79, 177.8) * mm, "end": v(154.79, 188.11) * mm});
            skLineSegment(sketch, "E3.11.13.1", {"start": v(154.79, 188.11) * mm, "end": v(165.1, 188.11) * mm});
            skLineSegment(sketch, "E3.11.13.2", {"start": v(154.79, 177.8) * mm, "end": v(165.1, 177.8) * mm});
            skLineSegment(sketch, "E3.11.13.3", {"start": v(165.1, 177.8) * mm, "end": v(165.1, 188.11) * mm});
            skLineSegment(sketch, "E3.11.14.0", {"start": v(154.79, 190.5) * mm, "end": v(154.79, 200.81) * mm});
            skLineSegment(sketch, "E3.11.14.1", {"start": v(154.79, 200.81) * mm, "end": v(165.1, 200.81) * mm});
            skLineSegment(sketch, "E3.11.14.2", {"start": v(154.79, 190.5) * mm, "end": v(165.1, 190.5) * mm});
            skLineSegment(sketch, "E3.11.14.3", {"start": v(165.1, 190.5) * mm, "end": v(165.1, 200.81) * mm});
            skLineSegment(sketch, "E3.11.15.0", {"start": v(154.79, 203.2) * mm, "end": v(154.79, 213.51) * mm});
            skLineSegment(sketch, "E3.11.15.1", {"start": v(154.79, 213.51) * mm, "end": v(165.1, 213.51) * mm});
            skLineSegment(sketch, "E3.11.15.2", {"start": v(154.79, 203.2) * mm, "end": v(165.1, 203.2) * mm});
            skLineSegment(sketch, "E3.11.15.3", {"start": v(165.1, 203.2) * mm, "end": v(165.1, 213.51) * mm});
            skLineSegment(sketch, "E3.11.16.0", {"start": v(154.79, 215.9) * mm, "end": v(154.79, 226.21) * mm});
            skLineSegment(sketch, "E3.11.16.1", {"start": v(154.79, 226.21) * mm, "end": v(165.1, 226.21) * mm});
            skLineSegment(sketch, "E3.11.16.2", {"start": v(154.79, 215.9) * mm, "end": v(165.1, 215.9) * mm});
            skLineSegment(sketch, "E3.11.16.3", {"start": v(165.1, 215.9) * mm, "end": v(165.1, 226.21) * mm});
            skLineSegment(sketch, "E3.11.17.0", {"start": v(154.79, 228.6) * mm, "end": v(154.79, 238.91) * mm});
            skLineSegment(sketch, "E3.11.17.1", {"start": v(154.79, 238.91) * mm, "end": v(165.1, 238.91) * mm});
            skLineSegment(sketch, "E3.11.17.2", {"start": v(154.79, 228.6) * mm, "end": v(165.1, 228.6) * mm});
            skLineSegment(sketch, "E3.11.17.3", {"start": v(165.1, 228.6) * mm, "end": v(165.1, 238.91) * mm});
            skLineSegment(sketch, "E3.11.18.0", {"start": v(154.79, 241.3) * mm, "end": v(154.79, 251.61) * mm});
            skLineSegment(sketch, "E3.11.18.1", {"start": v(154.79, 251.61) * mm, "end": v(165.1, 251.61) * mm});
            skLineSegment(sketch, "E3.11.18.2", {"start": v(154.79, 241.3) * mm, "end": v(165.1, 241.3) * mm});
            skLineSegment(sketch, "E3.11.18.3", {"start": v(165.1, 241.3) * mm, "end": v(165.1, 251.61) * mm});
            skLineSegment(sketch, "E3.11.19.0", {"start": v(154.79, 254) * mm, "end": v(154.79, 264.31) * mm});
            skLineSegment(sketch, "E3.11.19.1", {"start": v(154.79, 264.31) * mm, "end": v(165.1, 264.31) * mm});
            skLineSegment(sketch, "E3.11.19.2", {"start": v(154.79, 254) * mm, "end": v(165.1, 254) * mm});
            skLineSegment(sketch, "E3.11.19.3", {"start": v(165.1, 254) * mm, "end": v(165.1, 264.31) * mm});
            skLineSegment(sketch, "E3.11.20.0", {"start": v(154.79, 266.7) * mm, "end": v(154.79, 277.01) * mm});
            skLineSegment(sketch, "E3.11.20.1", {"start": v(154.79, 277.01) * mm, "end": v(165.1, 277.01) * mm});
            skLineSegment(sketch, "E3.11.20.2", {"start": v(154.79, 266.7) * mm, "end": v(165.1, 266.7) * mm});
            skLineSegment(sketch, "E3.11.20.3", {"start": v(165.1, 266.7) * mm, "end": v(165.1, 277.01) * mm});
            skLineSegment(sketch, "E3.11.21.0", {"start": v(154.79, 279.4) * mm, "end": v(154.79, 289.71) * mm});
            skLineSegment(sketch, "E3.11.21.1", {"start": v(154.79, 289.71) * mm, "end": v(165.1, 289.71) * mm});
            skLineSegment(sketch, "E3.11.21.2", {"start": v(154.79, 279.4) * mm, "end": v(165.1, 279.4) * mm});
            skLineSegment(sketch, "E3.11.21.3", {"start": v(165.1, 279.4) * mm, "end": v(165.1, 289.71) * mm});
            skLineSegment(sketch, "E3.12.0.0", {"start": v(167.49, 12.7) * mm, "end": v(167.49, 23.01) * mm});
            skLineSegment(sketch, "E3.12.0.1", {"start": v(167.49, 23.01) * mm, "end": v(177.8, 23.01) * mm});
            skLineSegment(sketch, "E3.12.0.2", {"start": v(167.49, 12.7) * mm, "end": v(177.8, 12.7) * mm});
            skLineSegment(sketch, "E3.12.0.3", {"start": v(177.8, 12.7) * mm, "end": v(177.8, 23.01) * mm});
            skLineSegment(sketch, "E3.12.1.0", {"start": v(167.49, 25.4) * mm, "end": v(167.49, 35.71) * mm});
            skLineSegment(sketch, "E3.12.1.1", {"start": v(167.49, 35.71) * mm, "end": v(177.8, 35.71) * mm});
            skLineSegment(sketch, "E3.12.1.2", {"start": v(167.49, 25.4) * mm, "end": v(177.8, 25.4) * mm});
            skLineSegment(sketch, "E3.12.1.3", {"start": v(177.8, 25.4) * mm, "end": v(177.8, 35.71) * mm});
            skLineSegment(sketch, "E3.12.2.0", {"start": v(167.49, 38.1) * mm, "end": v(167.49, 48.41) * mm});
            skLineSegment(sketch, "E3.12.2.1", {"start": v(167.49, 48.41) * mm, "end": v(177.8, 48.41) * mm});
            skLineSegment(sketch, "E3.12.2.2", {"start": v(167.49, 38.1) * mm, "end": v(177.8, 38.1) * mm});
            skLineSegment(sketch, "E3.12.2.3", {"start": v(177.8, 38.1) * mm, "end": v(177.8, 48.41) * mm});
            skLineSegment(sketch, "E3.12.3.0", {"start": v(167.49, 50.8) * mm, "end": v(167.49, 61.11) * mm});
            skLineSegment(sketch, "E3.12.3.1", {"start": v(167.49, 61.11) * mm, "end": v(177.8, 61.11) * mm});
            skLineSegment(sketch, "E3.12.3.2", {"start": v(167.49, 50.8) * mm, "end": v(177.8, 50.8) * mm});
            skLineSegment(sketch, "E3.12.3.3", {"start": v(177.8, 50.8) * mm, "end": v(177.8, 61.11) * mm});
            skLineSegment(sketch, "E3.12.4.0", {"start": v(167.49, 63.5) * mm, "end": v(167.49, 73.81) * mm});
            skLineSegment(sketch, "E3.12.4.1", {"start": v(167.49, 73.81) * mm, "end": v(177.8, 73.81) * mm});
            skLineSegment(sketch, "E3.12.4.2", {"start": v(167.49, 63.5) * mm, "end": v(177.8, 63.5) * mm});
            skLineSegment(sketch, "E3.12.4.3", {"start": v(177.8, 63.5) * mm, "end": v(177.8, 73.81) * mm});
            skLineSegment(sketch, "E3.12.5.0", {"start": v(167.49, 76.2) * mm, "end": v(167.49, 86.51) * mm});
            skLineSegment(sketch, "E3.12.5.1", {"start": v(167.49, 86.51) * mm, "end": v(177.8, 86.51) * mm});
            skLineSegment(sketch, "E3.12.5.2", {"start": v(167.49, 76.2) * mm, "end": v(177.8, 76.2) * mm});
            skLineSegment(sketch, "E3.12.5.3", {"start": v(177.8, 76.2) * mm, "end": v(177.8, 86.51) * mm});
            skLineSegment(sketch, "E3.12.6.0", {"start": v(167.49, 88.9) * mm, "end": v(167.49, 99.21) * mm});
            skLineSegment(sketch, "E3.12.6.1", {"start": v(167.49, 99.21) * mm, "end": v(177.8, 99.21) * mm});
            skLineSegment(sketch, "E3.12.6.2", {"start": v(167.49, 88.9) * mm, "end": v(177.8, 88.9) * mm});
            skLineSegment(sketch, "E3.12.6.3", {"start": v(177.8, 88.9) * mm, "end": v(177.8, 99.21) * mm});
            skLineSegment(sketch, "E3.12.7.0", {"start": v(167.49, 101.6) * mm, "end": v(167.49, 111.91) * mm});
            skLineSegment(sketch, "E3.12.7.1", {"start": v(167.49, 111.91) * mm, "end": v(177.8, 111.91) * mm});
            skLineSegment(sketch, "E3.12.7.2", {"start": v(167.49, 101.6) * mm, "end": v(177.8, 101.6) * mm});
            skLineSegment(sketch, "E3.12.7.3", {"start": v(177.8, 101.6) * mm, "end": v(177.8, 111.91) * mm});
            skLineSegment(sketch, "E3.12.8.0", {"start": v(167.49, 114.3) * mm, "end": v(167.49, 124.61) * mm});
            skLineSegment(sketch, "E3.12.8.1", {"start": v(167.49, 124.61) * mm, "end": v(177.8, 124.61) * mm});
            skLineSegment(sketch, "E3.12.8.2", {"start": v(167.49, 114.3) * mm, "end": v(177.8, 114.3) * mm});
            skLineSegment(sketch, "E3.12.8.3", {"start": v(177.8, 114.3) * mm, "end": v(177.8, 124.61) * mm});
            skLineSegment(sketch, "E3.12.9.0", {"start": v(167.49, 127) * mm, "end": v(167.49, 137.31) * mm});
            skLineSegment(sketch, "E3.12.9.1", {"start": v(167.49, 137.31) * mm, "end": v(177.8, 137.31) * mm});
            skLineSegment(sketch, "E3.12.9.2", {"start": v(167.49, 127) * mm, "end": v(177.8, 127) * mm});
            skLineSegment(sketch, "E3.12.9.3", {"start": v(177.8, 127) * mm, "end": v(177.8, 137.31) * mm});
            skLineSegment(sketch, "E3.12.10.0", {"start": v(167.49, 139.7) * mm, "end": v(167.49, 150.01) * mm});
            skLineSegment(sketch, "E3.12.10.1", {"start": v(167.49, 150.01) * mm, "end": v(177.8, 150.01) * mm});
            skLineSegment(sketch, "E3.12.10.2", {"start": v(167.49, 139.7) * mm, "end": v(177.8, 139.7) * mm});
            skLineSegment(sketch, "E3.12.10.3", {"start": v(177.8, 139.7) * mm, "end": v(177.8, 150.01) * mm});
            skLineSegment(sketch, "E3.12.11.0", {"start": v(167.49, 152.4) * mm, "end": v(167.49, 162.71) * mm});
            skLineSegment(sketch, "E3.12.11.1", {"start": v(167.49, 162.71) * mm, "end": v(177.8, 162.71) * mm});
            skLineSegment(sketch, "E3.12.11.2", {"start": v(167.49, 152.4) * mm, "end": v(177.8, 152.4) * mm});
            skLineSegment(sketch, "E3.12.11.3", {"start": v(177.8, 152.4) * mm, "end": v(177.8, 162.71) * mm});
            skLineSegment(sketch, "E3.12.12.0", {"start": v(167.49, 165.1) * mm, "end": v(167.49, 175.41) * mm});
            skLineSegment(sketch, "E3.12.12.1", {"start": v(167.49, 175.41) * mm, "end": v(177.8, 175.41) * mm});
            skLineSegment(sketch, "E3.12.12.2", {"start": v(167.49, 165.1) * mm, "end": v(177.8, 165.1) * mm});
            skLineSegment(sketch, "E3.12.12.3", {"start": v(177.8, 165.1) * mm, "end": v(177.8, 175.41) * mm});
            skLineSegment(sketch, "E3.12.13.0", {"start": v(167.49, 177.8) * mm, "end": v(167.49, 188.11) * mm});
            skLineSegment(sketch, "E3.12.13.1", {"start": v(167.49, 188.11) * mm, "end": v(177.8, 188.11) * mm});
            skLineSegment(sketch, "E3.12.13.2", {"start": v(167.49, 177.8) * mm, "end": v(177.8, 177.8) * mm});
            skLineSegment(sketch, "E3.12.13.3", {"start": v(177.8, 177.8) * mm, "end": v(177.8, 188.11) * mm});
            skLineSegment(sketch, "E3.12.14.0", {"start": v(167.49, 190.5) * mm, "end": v(167.49, 200.81) * mm});
            skLineSegment(sketch, "E3.12.14.1", {"start": v(167.49, 200.81) * mm, "end": v(177.8, 200.81) * mm});
            skLineSegment(sketch, "E3.12.14.2", {"start": v(167.49, 190.5) * mm, "end": v(177.8, 190.5) * mm});
            skLineSegment(sketch, "E3.12.14.3", {"start": v(177.8, 190.5) * mm, "end": v(177.8, 200.81) * mm});
            skLineSegment(sketch, "E3.12.15.0", {"start": v(167.49, 203.2) * mm, "end": v(167.49, 213.51) * mm});
            skLineSegment(sketch, "E3.12.15.1", {"start": v(167.49, 213.51) * mm, "end": v(177.8, 213.51) * mm});
            skLineSegment(sketch, "E3.12.15.2", {"start": v(167.49, 203.2) * mm, "end": v(177.8, 203.2) * mm});
            skLineSegment(sketch, "E3.12.15.3", {"start": v(177.8, 203.2) * mm, "end": v(177.8, 213.51) * mm});
            skLineSegment(sketch, "E3.12.16.0", {"start": v(167.49, 215.9) * mm, "end": v(167.49, 226.21) * mm});
            skLineSegment(sketch, "E3.12.16.1", {"start": v(167.49, 226.21) * mm, "end": v(177.8, 226.21) * mm});
            skLineSegment(sketch, "E3.12.16.2", {"start": v(167.49, 215.9) * mm, "end": v(177.8, 215.9) * mm});
            skLineSegment(sketch, "E3.12.16.3", {"start": v(177.8, 215.9) * mm, "end": v(177.8, 226.21) * mm});
            skLineSegment(sketch, "E3.12.17.0", {"start": v(167.49, 228.6) * mm, "end": v(167.49, 238.91) * mm});
            skLineSegment(sketch, "E3.12.17.1", {"start": v(167.49, 238.91) * mm, "end": v(177.8, 238.91) * mm});
            skLineSegment(sketch, "E3.12.17.2", {"start": v(167.49, 228.6) * mm, "end": v(177.8, 228.6) * mm});
            skLineSegment(sketch, "E3.12.17.3", {"start": v(177.8, 228.6) * mm, "end": v(177.8, 238.91) * mm});
            skLineSegment(sketch, "E3.12.18.0", {"start": v(167.49, 241.3) * mm, "end": v(167.49, 251.61) * mm});
            skLineSegment(sketch, "E3.12.18.1", {"start": v(167.49, 251.61) * mm, "end": v(177.8, 251.61) * mm});
            skLineSegment(sketch, "E3.12.18.2", {"start": v(167.49, 241.3) * mm, "end": v(177.8, 241.3) * mm});
            skLineSegment(sketch, "E3.12.18.3", {"start": v(177.8, 241.3) * mm, "end": v(177.8, 251.61) * mm});
            skLineSegment(sketch, "E3.12.19.0", {"start": v(167.49, 254) * mm, "end": v(167.49, 264.31) * mm});
            skLineSegment(sketch, "E3.12.19.1", {"start": v(167.49, 264.31) * mm, "end": v(177.8, 264.31) * mm});
            skLineSegment(sketch, "E3.12.19.2", {"start": v(167.49, 254) * mm, "end": v(177.8, 254) * mm});
            skLineSegment(sketch, "E3.12.19.3", {"start": v(177.8, 254) * mm, "end": v(177.8, 264.31) * mm});
            skLineSegment(sketch, "E3.12.20.0", {"start": v(167.49, 266.7) * mm, "end": v(167.49, 277.01) * mm});
            skLineSegment(sketch, "E3.12.20.1", {"start": v(167.49, 277.01) * mm, "end": v(177.8, 277.01) * mm});
            skLineSegment(sketch, "E3.12.20.2", {"start": v(167.49, 266.7) * mm, "end": v(177.8, 266.7) * mm});
            skLineSegment(sketch, "E3.12.20.3", {"start": v(177.8, 266.7) * mm, "end": v(177.8, 277.01) * mm});
            skLineSegment(sketch, "E3.12.21.0", {"start": v(167.49, 279.4) * mm, "end": v(167.49, 289.71) * mm});
            skLineSegment(sketch, "E3.12.21.1", {"start": v(167.49, 289.71) * mm, "end": v(177.8, 289.71) * mm});
            skLineSegment(sketch, "E3.12.21.2", {"start": v(167.49, 279.4) * mm, "end": v(177.8, 279.4) * mm});
            skLineSegment(sketch, "E3.12.21.3", {"start": v(177.8, 279.4) * mm, "end": v(177.8, 289.71) * mm});
            skLineSegment(sketch, "E3.13.0.0", {"start": v(180.19, 12.7) * mm, "end": v(180.19, 23.01) * mm});
            skLineSegment(sketch, "E3.13.0.1", {"start": v(180.19, 23.01) * mm, "end": v(190.5, 23.01) * mm});
            skLineSegment(sketch, "E3.13.0.2", {"start": v(180.19, 12.7) * mm, "end": v(190.5, 12.7) * mm});
            skLineSegment(sketch, "E3.13.0.3", {"start": v(190.5, 12.7) * mm, "end": v(190.5, 23.01) * mm});
            skLineSegment(sketch, "E3.13.1.0", {"start": v(180.19, 25.4) * mm, "end": v(180.19, 35.71) * mm});
            skLineSegment(sketch, "E3.13.1.1", {"start": v(180.19, 35.71) * mm, "end": v(190.5, 35.71) * mm});
            skLineSegment(sketch, "E3.13.1.2", {"start": v(180.19, 25.4) * mm, "end": v(190.5, 25.4) * mm});
            skLineSegment(sketch, "E3.13.1.3", {"start": v(190.5, 25.4) * mm, "end": v(190.5, 35.71) * mm});
            skLineSegment(sketch, "E3.13.2.0", {"start": v(180.19, 38.1) * mm, "end": v(180.19, 48.41) * mm});
            skLineSegment(sketch, "E3.13.2.1", {"start": v(180.19, 48.41) * mm, "end": v(190.5, 48.41) * mm});
            skLineSegment(sketch, "E3.13.2.2", {"start": v(180.19, 38.1) * mm, "end": v(190.5, 38.1) * mm});
            skLineSegment(sketch, "E3.13.2.3", {"start": v(190.5, 38.1) * mm, "end": v(190.5, 48.41) * mm});
            skLineSegment(sketch, "E3.13.3.0", {"start": v(180.19, 50.8) * mm, "end": v(180.19, 61.11) * mm});
            skLineSegment(sketch, "E3.13.3.1", {"start": v(180.19, 61.11) * mm, "end": v(190.5, 61.11) * mm});
            skLineSegment(sketch, "E3.13.3.2", {"start": v(180.19, 50.8) * mm, "end": v(190.5, 50.8) * mm});
            skLineSegment(sketch, "E3.13.3.3", {"start": v(190.5, 50.8) * mm, "end": v(190.5, 61.11) * mm});
            skLineSegment(sketch, "E3.13.4.0", {"start": v(180.19, 63.5) * mm, "end": v(180.19, 73.81) * mm});
            skLineSegment(sketch, "E3.13.4.1", {"start": v(180.19, 73.81) * mm, "end": v(190.5, 73.81) * mm});
            skLineSegment(sketch, "E3.13.4.2", {"start": v(180.19, 63.5) * mm, "end": v(190.5, 63.5) * mm});
            skLineSegment(sketch, "E3.13.4.3", {"start": v(190.5, 63.5) * mm, "end": v(190.5, 73.81) * mm});
            skLineSegment(sketch, "E3.13.5.0", {"start": v(180.19, 76.2) * mm, "end": v(180.19, 86.51) * mm});
            skLineSegment(sketch, "E3.13.5.1", {"start": v(180.19, 86.51) * mm, "end": v(190.5, 86.51) * mm});
            skLineSegment(sketch, "E3.13.5.2", {"start": v(180.19, 76.2) * mm, "end": v(190.5, 76.2) * mm});
            skLineSegment(sketch, "E3.13.5.3", {"start": v(190.5, 76.2) * mm, "end": v(190.5, 86.51) * mm});
            skLineSegment(sketch, "E3.13.6.0", {"start": v(180.19, 88.9) * mm, "end": v(180.19, 99.21) * mm});
            skLineSegment(sketch, "E3.13.6.1", {"start": v(180.19, 99.21) * mm, "end": v(190.5, 99.21) * mm});
            skLineSegment(sketch, "E3.13.6.2", {"start": v(180.19, 88.9) * mm, "end": v(190.5, 88.9) * mm});
            skLineSegment(sketch, "E3.13.6.3", {"start": v(190.5, 88.9) * mm, "end": v(190.5, 99.21) * mm});
            skLineSegment(sketch, "E3.13.7.0", {"start": v(180.19, 101.6) * mm, "end": v(180.19, 111.91) * mm});
            skLineSegment(sketch, "E3.13.7.1", {"start": v(180.19, 111.91) * mm, "end": v(190.5, 111.91) * mm});
            skLineSegment(sketch, "E3.13.7.2", {"start": v(180.19, 101.6) * mm, "end": v(190.5, 101.6) * mm});
            skLineSegment(sketch, "E3.13.7.3", {"start": v(190.5, 101.6) * mm, "end": v(190.5, 111.91) * mm});
            skLineSegment(sketch, "E3.13.8.0", {"start": v(180.19, 114.3) * mm, "end": v(180.19, 124.61) * mm});
            skLineSegment(sketch, "E3.13.8.1", {"start": v(180.19, 124.61) * mm, "end": v(190.5, 124.61) * mm});
            skLineSegment(sketch, "E3.13.8.2", {"start": v(180.19, 114.3) * mm, "end": v(190.5, 114.3) * mm});
            skLineSegment(sketch, "E3.13.8.3", {"start": v(190.5, 114.3) * mm, "end": v(190.5, 124.61) * mm});
            skLineSegment(sketch, "E3.13.9.0", {"start": v(180.19, 127) * mm, "end": v(180.19, 137.31) * mm});
            skLineSegment(sketch, "E3.13.9.1", {"start": v(180.19, 137.31) * mm, "end": v(190.5, 137.31) * mm});
            skLineSegment(sketch, "E3.13.9.2", {"start": v(180.19, 127) * mm, "end": v(190.5, 127) * mm});
            skLineSegment(sketch, "E3.13.9.3", {"start": v(190.5, 127) * mm, "end": v(190.5, 137.31) * mm});
            skLineSegment(sketch, "E3.13.10.0", {"start": v(180.19, 139.7) * mm, "end": v(180.19, 150.01) * mm});
            skLineSegment(sketch, "E3.13.10.1", {"start": v(180.19, 150.01) * mm, "end": v(190.5, 150.01) * mm});
            skLineSegment(sketch, "E3.13.10.2", {"start": v(180.19, 139.7) * mm, "end": v(190.5, 139.7) * mm});
            skLineSegment(sketch, "E3.13.10.3", {"start": v(190.5, 139.7) * mm, "end": v(190.5, 150.01) * mm});
            skLineSegment(sketch, "E3.13.11.0", {"start": v(180.19, 152.4) * mm, "end": v(180.19, 162.71) * mm});
            skLineSegment(sketch, "E3.13.11.1", {"start": v(180.19, 162.71) * mm, "end": v(190.5, 162.71) * mm});
            skLineSegment(sketch, "E3.13.11.2", {"start": v(180.19, 152.4) * mm, "end": v(190.5, 152.4) * mm});
            skLineSegment(sketch, "E3.13.11.3", {"start": v(190.5, 152.4) * mm, "end": v(190.5, 162.71) * mm});
            skLineSegment(sketch, "E3.13.12.0", {"start": v(180.19, 165.1) * mm, "end": v(180.19, 175.41) * mm});
            skLineSegment(sketch, "E3.13.12.1", {"start": v(180.19, 175.41) * mm, "end": v(190.5, 175.41) * mm});
            skLineSegment(sketch, "E3.13.12.2", {"start": v(180.19, 165.1) * mm, "end": v(190.5, 165.1) * mm});
            skLineSegment(sketch, "E3.13.12.3", {"start": v(190.5, 165.1) * mm, "end": v(190.5, 175.41) * mm});
            skLineSegment(sketch, "E3.13.13.0", {"start": v(180.19, 177.8) * mm, "end": v(180.19, 188.11) * mm});
            skLineSegment(sketch, "E3.13.13.1", {"start": v(180.19, 188.11) * mm, "end": v(190.5, 188.11) * mm});
            skLineSegment(sketch, "E3.13.13.2", {"start": v(180.19, 177.8) * mm, "end": v(190.5, 177.8) * mm});
            skLineSegment(sketch, "E3.13.13.3", {"start": v(190.5, 177.8) * mm, "end": v(190.5, 188.11) * mm});
            skLineSegment(sketch, "E3.13.14.0", {"start": v(180.19, 190.5) * mm, "end": v(180.19, 200.81) * mm});
            skLineSegment(sketch, "E3.13.14.1", {"start": v(180.19, 200.81) * mm, "end": v(190.5, 200.81) * mm});
            skLineSegment(sketch, "E3.13.14.2", {"start": v(180.19, 190.5) * mm, "end": v(190.5, 190.5) * mm});
            skLineSegment(sketch, "E3.13.14.3", {"start": v(190.5, 190.5) * mm, "end": v(190.5, 200.81) * mm});
            skLineSegment(sketch, "E3.13.15.0", {"start": v(180.19, 203.2) * mm, "end": v(180.19, 213.51) * mm});
            skLineSegment(sketch, "E3.13.15.1", {"start": v(180.19, 213.51) * mm, "end": v(190.5, 213.51) * mm});
            skLineSegment(sketch, "E3.13.15.2", {"start": v(180.19, 203.2) * mm, "end": v(190.5, 203.2) * mm});
            skLineSegment(sketch, "E3.13.15.3", {"start": v(190.5, 203.2) * mm, "end": v(190.5, 213.51) * mm});
            skLineSegment(sketch, "E3.13.16.0", {"start": v(180.19, 215.9) * mm, "end": v(180.19, 226.21) * mm});
            skLineSegment(sketch, "E3.13.16.1", {"start": v(180.19, 226.21) * mm, "end": v(190.5, 226.21) * mm});
            skLineSegment(sketch, "E3.13.16.2", {"start": v(180.19, 215.9) * mm, "end": v(190.5, 215.9) * mm});
            skLineSegment(sketch, "E3.13.16.3", {"start": v(190.5, 215.9) * mm, "end": v(190.5, 226.21) * mm});
            skLineSegment(sketch, "E3.13.17.0", {"start": v(180.19, 228.6) * mm, "end": v(180.19, 238.91) * mm});
            skLineSegment(sketch, "E3.13.17.1", {"start": v(180.19, 238.91) * mm, "end": v(190.5, 238.91) * mm});
            skLineSegment(sketch, "E3.13.17.2", {"start": v(180.19, 228.6) * mm, "end": v(190.5, 228.6) * mm});
            skLineSegment(sketch, "E3.13.17.3", {"start": v(190.5, 228.6) * mm, "end": v(190.5, 238.91) * mm});
            skLineSegment(sketch, "E3.13.18.0", {"start": v(180.19, 241.3) * mm, "end": v(180.19, 251.61) * mm});
            skLineSegment(sketch, "E3.13.18.1", {"start": v(180.19, 251.61) * mm, "end": v(190.5, 251.61) * mm});
            skLineSegment(sketch, "E3.13.18.2", {"start": v(180.19, 241.3) * mm, "end": v(190.5, 241.3) * mm});
            skLineSegment(sketch, "E3.13.18.3", {"start": v(190.5, 241.3) * mm, "end": v(190.5, 251.61) * mm});
            skLineSegment(sketch, "E3.13.19.0", {"start": v(180.19, 254) * mm, "end": v(180.19, 264.31) * mm});
            skLineSegment(sketch, "E3.13.19.1", {"start": v(180.19, 264.31) * mm, "end": v(190.5, 264.31) * mm});
            skLineSegment(sketch, "E3.13.19.2", {"start": v(180.19, 254) * mm, "end": v(190.5, 254) * mm});
            skLineSegment(sketch, "E3.13.19.3", {"start": v(190.5, 254) * mm, "end": v(190.5, 264.31) * mm});
            skLineSegment(sketch, "E3.13.20.0", {"start": v(180.19, 266.7) * mm, "end": v(180.19, 277.01) * mm});
            skLineSegment(sketch, "E3.13.20.1", {"start": v(180.19, 277.01) * mm, "end": v(190.5, 277.01) * mm});
            skLineSegment(sketch, "E3.13.20.2", {"start": v(180.19, 266.7) * mm, "end": v(190.5, 266.7) * mm});
            skLineSegment(sketch, "E3.13.20.3", {"start": v(190.5, 266.7) * mm, "end": v(190.5, 277.01) * mm});
            skLineSegment(sketch, "E3.13.21.0", {"start": v(180.19, 279.4) * mm, "end": v(180.19, 289.71) * mm});
            skLineSegment(sketch, "E3.13.21.1", {"start": v(180.19, 289.71) * mm, "end": v(190.5, 289.71) * mm});
            skLineSegment(sketch, "E3.13.21.2", {"start": v(180.19, 279.4) * mm, "end": v(190.5, 279.4) * mm});
            skLineSegment(sketch, "E3.13.21.3", {"start": v(190.5, 279.4) * mm, "end": v(190.5, 289.71) * mm});
            skLineSegment(sketch, "E3.14.0.0", {"start": v(192.89, 12.7) * mm, "end": v(192.89, 23.01) * mm});
            skLineSegment(sketch, "E3.14.0.1", {"start": v(192.89, 23.01) * mm, "end": v(203.2, 23.01) * mm});
            skLineSegment(sketch, "E3.14.0.2", {"start": v(192.89, 12.7) * mm, "end": v(203.2, 12.7) * mm});
            skLineSegment(sketch, "E3.14.0.3", {"start": v(203.2, 12.7) * mm, "end": v(203.2, 23.01) * mm});
            skLineSegment(sketch, "E3.14.1.0", {"start": v(192.89, 25.4) * mm, "end": v(192.89, 35.71) * mm});
            skLineSegment(sketch, "E3.14.1.1", {"start": v(192.89, 35.71) * mm, "end": v(203.2, 35.71) * mm});
            skLineSegment(sketch, "E3.14.1.2", {"start": v(192.89, 25.4) * mm, "end": v(203.2, 25.4) * mm});
            skLineSegment(sketch, "E3.14.1.3", {"start": v(203.2, 25.4) * mm, "end": v(203.2, 35.71) * mm});
            skLineSegment(sketch, "E3.14.2.0", {"start": v(192.89, 38.1) * mm, "end": v(192.89, 48.41) * mm});
            skLineSegment(sketch, "E3.14.2.1", {"start": v(192.89, 48.41) * mm, "end": v(203.2, 48.41) * mm});
            skLineSegment(sketch, "E3.14.2.2", {"start": v(192.89, 38.1) * mm, "end": v(203.2, 38.1) * mm});
            skLineSegment(sketch, "E3.14.2.3", {"start": v(203.2, 38.1) * mm, "end": v(203.2, 48.41) * mm});
            skLineSegment(sketch, "E3.14.3.0", {"start": v(192.89, 50.8) * mm, "end": v(192.89, 61.11) * mm});
            skLineSegment(sketch, "E3.14.3.1", {"start": v(192.89, 61.11) * mm, "end": v(203.2, 61.11) * mm});
            skLineSegment(sketch, "E3.14.3.2", {"start": v(192.89, 50.8) * mm, "end": v(203.2, 50.8) * mm});
            skLineSegment(sketch, "E3.14.3.3", {"start": v(203.2, 50.8) * mm, "end": v(203.2, 61.11) * mm});
            skLineSegment(sketch, "E3.14.4.0", {"start": v(192.89, 63.5) * mm, "end": v(192.89, 73.81) * mm});
            skLineSegment(sketch, "E3.14.4.1", {"start": v(192.89, 73.81) * mm, "end": v(203.2, 73.81) * mm});
            skLineSegment(sketch, "E3.14.4.2", {"start": v(192.89, 63.5) * mm, "end": v(203.2, 63.5) * mm});
            skLineSegment(sketch, "E3.14.4.3", {"start": v(203.2, 63.5) * mm, "end": v(203.2, 73.81) * mm});
            skLineSegment(sketch, "E3.14.5.0", {"start": v(192.89, 76.2) * mm, "end": v(192.89, 86.51) * mm});
            skLineSegment(sketch, "E3.14.5.1", {"start": v(192.89, 86.51) * mm, "end": v(203.2, 86.51) * mm});
            skLineSegment(sketch, "E3.14.5.2", {"start": v(192.89, 76.2) * mm, "end": v(203.2, 76.2) * mm});
            skLineSegment(sketch, "E3.14.5.3", {"start": v(203.2, 76.2) * mm, "end": v(203.2, 86.51) * mm});
            skLineSegment(sketch, "E3.14.6.0", {"start": v(192.89, 88.9) * mm, "end": v(192.89, 99.21) * mm});
            skLineSegment(sketch, "E3.14.6.1", {"start": v(192.89, 99.21) * mm, "end": v(203.2, 99.21) * mm});
            skLineSegment(sketch, "E3.14.6.2", {"start": v(192.89, 88.9) * mm, "end": v(203.2, 88.9) * mm});
            skLineSegment(sketch, "E3.14.6.3", {"start": v(203.2, 88.9) * mm, "end": v(203.2, 99.21) * mm});
            skLineSegment(sketch, "E3.14.7.0", {"start": v(192.89, 101.6) * mm, "end": v(192.89, 111.91) * mm});
            skLineSegment(sketch, "E3.14.7.1", {"start": v(192.89, 111.91) * mm, "end": v(203.2, 111.91) * mm});
            skLineSegment(sketch, "E3.14.7.2", {"start": v(192.89, 101.6) * mm, "end": v(203.2, 101.6) * mm});
            skLineSegment(sketch, "E3.14.7.3", {"start": v(203.2, 101.6) * mm, "end": v(203.2, 111.91) * mm});
            skLineSegment(sketch, "E3.14.8.0", {"start": v(192.89, 114.3) * mm, "end": v(192.89, 124.61) * mm});
            skLineSegment(sketch, "E3.14.8.1", {"start": v(192.89, 124.61) * mm, "end": v(203.2, 124.61) * mm});
            skLineSegment(sketch, "E3.14.8.2", {"start": v(192.89, 114.3) * mm, "end": v(203.2, 114.3) * mm});
            skLineSegment(sketch, "E3.14.8.3", {"start": v(203.2, 114.3) * mm, "end": v(203.2, 124.61) * mm});
            skLineSegment(sketch, "E3.14.9.0", {"start": v(192.89, 127) * mm, "end": v(192.89, 137.31) * mm});
            skLineSegment(sketch, "E3.14.9.1", {"start": v(192.89, 137.31) * mm, "end": v(203.2, 137.31) * mm});
            skLineSegment(sketch, "E3.14.9.2", {"start": v(192.89, 127) * mm, "end": v(203.2, 127) * mm});
            skLineSegment(sketch, "E3.14.9.3", {"start": v(203.2, 127) * mm, "end": v(203.2, 137.31) * mm});
            skLineSegment(sketch, "E3.14.10.0", {"start": v(192.89, 139.7) * mm, "end": v(192.89, 150.01) * mm});
            skLineSegment(sketch, "E3.14.10.1", {"start": v(192.89, 150.01) * mm, "end": v(203.2, 150.01) * mm});
            skLineSegment(sketch, "E3.14.10.2", {"start": v(192.89, 139.7) * mm, "end": v(203.2, 139.7) * mm});
            skLineSegment(sketch, "E3.14.10.3", {"start": v(203.2, 139.7) * mm, "end": v(203.2, 150.01) * mm});
            skLineSegment(sketch, "E3.14.11.0", {"start": v(192.89, 152.4) * mm, "end": v(192.89, 162.71) * mm});
            skLineSegment(sketch, "E3.14.11.1", {"start": v(192.89, 162.71) * mm, "end": v(203.2, 162.71) * mm});
            skLineSegment(sketch, "E3.14.11.2", {"start": v(192.89, 152.4) * mm, "end": v(203.2, 152.4) * mm});
            skLineSegment(sketch, "E3.14.11.3", {"start": v(203.2, 152.4) * mm, "end": v(203.2, 162.71) * mm});
            skLineSegment(sketch, "E3.14.12.0", {"start": v(192.89, 165.1) * mm, "end": v(192.89, 175.41) * mm});
            skLineSegment(sketch, "E3.14.12.1", {"start": v(192.89, 175.41) * mm, "end": v(203.2, 175.41) * mm});
            skLineSegment(sketch, "E3.14.12.2", {"start": v(192.89, 165.1) * mm, "end": v(203.2, 165.1) * mm});
            skLineSegment(sketch, "E3.14.12.3", {"start": v(203.2, 165.1) * mm, "end": v(203.2, 175.41) * mm});
            skLineSegment(sketch, "E3.14.13.0", {"start": v(192.89, 177.8) * mm, "end": v(192.89, 188.11) * mm});
            skLineSegment(sketch, "E3.14.13.1", {"start": v(192.89, 188.11) * mm, "end": v(203.2, 188.11) * mm});
            skLineSegment(sketch, "E3.14.13.2", {"start": v(192.89, 177.8) * mm, "end": v(203.2, 177.8) * mm});
            skLineSegment(sketch, "E3.14.13.3", {"start": v(203.2, 177.8) * mm, "end": v(203.2, 188.11) * mm});
            skLineSegment(sketch, "E3.14.14.0", {"start": v(192.89, 190.5) * mm, "end": v(192.89, 200.81) * mm});
            skLineSegment(sketch, "E3.14.14.1", {"start": v(192.89, 200.81) * mm, "end": v(203.2, 200.81) * mm});
            skLineSegment(sketch, "E3.14.14.2", {"start": v(192.89, 190.5) * mm, "end": v(203.2, 190.5) * mm});
            skLineSegment(sketch, "E3.14.14.3", {"start": v(203.2, 190.5) * mm, "end": v(203.2, 200.81) * mm});
            skLineSegment(sketch, "E3.14.15.0", {"start": v(192.89, 203.2) * mm, "end": v(192.89, 213.51) * mm});
            skLineSegment(sketch, "E3.14.15.1", {"start": v(192.89, 213.51) * mm, "end": v(203.2, 213.51) * mm});
            skLineSegment(sketch, "E3.14.15.2", {"start": v(192.89, 203.2) * mm, "end": v(203.2, 203.2) * mm});
            skLineSegment(sketch, "E3.14.15.3", {"start": v(203.2, 203.2) * mm, "end": v(203.2, 213.51) * mm});
            skLineSegment(sketch, "E3.14.16.0", {"start": v(192.89, 215.9) * mm, "end": v(192.89, 226.21) * mm});
            skLineSegment(sketch, "E3.14.16.1", {"start": v(192.89, 226.21) * mm, "end": v(203.2, 226.21) * mm});
            skLineSegment(sketch, "E3.14.16.2", {"start": v(192.89, 215.9) * mm, "end": v(203.2, 215.9) * mm});
            skLineSegment(sketch, "E3.14.16.3", {"start": v(203.2, 215.9) * mm, "end": v(203.2, 226.21) * mm});
            skLineSegment(sketch, "E3.14.17.0", {"start": v(192.89, 228.6) * mm, "end": v(192.89, 238.91) * mm});
            skLineSegment(sketch, "E3.14.17.1", {"start": v(192.89, 238.91) * mm, "end": v(203.2, 238.91) * mm});
            skLineSegment(sketch, "E3.14.17.2", {"start": v(192.89, 228.6) * mm, "end": v(203.2, 228.6) * mm});
            skLineSegment(sketch, "E3.14.17.3", {"start": v(203.2, 228.6) * mm, "end": v(203.2, 238.91) * mm});
            skLineSegment(sketch, "E3.14.18.0", {"start": v(192.89, 241.3) * mm, "end": v(192.89, 251.61) * mm});
            skLineSegment(sketch, "E3.14.18.1", {"start": v(192.89, 251.61) * mm, "end": v(203.2, 251.61) * mm});
            skLineSegment(sketch, "E3.14.18.2", {"start": v(192.89, 241.3) * mm, "end": v(203.2, 241.3) * mm});
            skLineSegment(sketch, "E3.14.18.3", {"start": v(203.2, 241.3) * mm, "end": v(203.2, 251.61) * mm});
            skLineSegment(sketch, "E3.14.19.0", {"start": v(192.89, 254) * mm, "end": v(192.89, 264.31) * mm});
            skLineSegment(sketch, "E3.14.19.1", {"start": v(192.89, 264.31) * mm, "end": v(203.2, 264.31) * mm});
            skLineSegment(sketch, "E3.14.19.2", {"start": v(192.89, 254) * mm, "end": v(203.2, 254) * mm});
            skLineSegment(sketch, "E3.14.19.3", {"start": v(203.2, 254) * mm, "end": v(203.2, 264.31) * mm});
            skLineSegment(sketch, "E3.14.20.0", {"start": v(192.89, 266.7) * mm, "end": v(192.89, 277.01) * mm});
            skLineSegment(sketch, "E3.14.20.1", {"start": v(192.89, 277.01) * mm, "end": v(203.2, 277.01) * mm});
            skLineSegment(sketch, "E3.14.20.2", {"start": v(192.89, 266.7) * mm, "end": v(203.2, 266.7) * mm});
            skLineSegment(sketch, "E3.14.20.3", {"start": v(203.2, 266.7) * mm, "end": v(203.2, 277.01) * mm});
            skLineSegment(sketch, "E3.14.21.0", {"start": v(192.89, 279.4) * mm, "end": v(192.89, 289.71) * mm});
            skLineSegment(sketch, "E3.14.21.1", {"start": v(192.89, 289.71) * mm, "end": v(203.2, 289.71) * mm});
            skLineSegment(sketch, "E3.14.21.2", {"start": v(192.89, 279.4) * mm, "end": v(203.2, 279.4) * mm});
            skLineSegment(sketch, "E3.14.21.3", {"start": v(203.2, 279.4) * mm, "end": v(203.2, 289.71) * mm});
            skLineSegment(sketch, "E3.15.0.0", {"start": v(205.59, 12.7) * mm, "end": v(205.59, 23.01) * mm});
            skLineSegment(sketch, "E3.15.0.1", {"start": v(205.59, 23.01) * mm, "end": v(215.9, 23.01) * mm});
            skLineSegment(sketch, "E3.15.0.2", {"start": v(205.59, 12.7) * mm, "end": v(215.9, 12.7) * mm});
            skLineSegment(sketch, "E3.15.0.3", {"start": v(215.9, 12.7) * mm, "end": v(215.9, 23.01) * mm});
            skLineSegment(sketch, "E3.15.1.0", {"start": v(205.59, 25.4) * mm, "end": v(205.59, 35.71) * mm});
            skLineSegment(sketch, "E3.15.1.1", {"start": v(205.59, 35.71) * mm, "end": v(215.9, 35.71) * mm});
            skLineSegment(sketch, "E3.15.1.2", {"start": v(205.59, 25.4) * mm, "end": v(215.9, 25.4) * mm});
            skLineSegment(sketch, "E3.15.1.3", {"start": v(215.9, 25.4) * mm, "end": v(215.9, 35.71) * mm});
            skLineSegment(sketch, "E3.15.2.0", {"start": v(205.59, 38.1) * mm, "end": v(205.59, 48.41) * mm});
            skLineSegment(sketch, "E3.15.2.1", {"start": v(205.59, 48.41) * mm, "end": v(215.9, 48.41) * mm});
            skLineSegment(sketch, "E3.15.2.2", {"start": v(205.59, 38.1) * mm, "end": v(215.9, 38.1) * mm});
            skLineSegment(sketch, "E3.15.2.3", {"start": v(215.9, 38.1) * mm, "end": v(215.9, 48.41) * mm});
            skLineSegment(sketch, "E3.15.3.0", {"start": v(205.59, 50.8) * mm, "end": v(205.59, 61.11) * mm});
            skLineSegment(sketch, "E3.15.3.1", {"start": v(205.59, 61.11) * mm, "end": v(215.9, 61.11) * mm});
            skLineSegment(sketch, "E3.15.3.2", {"start": v(205.59, 50.8) * mm, "end": v(215.9, 50.8) * mm});
            skLineSegment(sketch, "E3.15.3.3", {"start": v(215.9, 50.8) * mm, "end": v(215.9, 61.11) * mm});
            skLineSegment(sketch, "E3.15.4.0", {"start": v(205.59, 63.5) * mm, "end": v(205.59, 73.81) * mm});
            skLineSegment(sketch, "E3.15.4.1", {"start": v(205.59, 73.81) * mm, "end": v(215.9, 73.81) * mm});
            skLineSegment(sketch, "E3.15.4.2", {"start": v(205.59, 63.5) * mm, "end": v(215.9, 63.5) * mm});
            skLineSegment(sketch, "E3.15.4.3", {"start": v(215.9, 63.5) * mm, "end": v(215.9, 73.81) * mm});
            skLineSegment(sketch, "E3.15.5.0", {"start": v(205.59, 76.2) * mm, "end": v(205.59, 86.51) * mm});
            skLineSegment(sketch, "E3.15.5.1", {"start": v(205.59, 86.51) * mm, "end": v(215.9, 86.51) * mm});
            skLineSegment(sketch, "E3.15.5.2", {"start": v(205.59, 76.2) * mm, "end": v(215.9, 76.2) * mm});
            skLineSegment(sketch, "E3.15.5.3", {"start": v(215.9, 76.2) * mm, "end": v(215.9, 86.51) * mm});
            skLineSegment(sketch, "E3.15.6.0", {"start": v(205.59, 88.9) * mm, "end": v(205.59, 99.21) * mm});
            skLineSegment(sketch, "E3.15.6.1", {"start": v(205.59, 99.21) * mm, "end": v(215.9, 99.21) * mm});
            skLineSegment(sketch, "E3.15.6.2", {"start": v(205.59, 88.9) * mm, "end": v(215.9, 88.9) * mm});
            skLineSegment(sketch, "E3.15.6.3", {"start": v(215.9, 88.9) * mm, "end": v(215.9, 99.21) * mm});
            skLineSegment(sketch, "E3.15.7.0", {"start": v(205.59, 101.6) * mm, "end": v(205.59, 111.91) * mm});
            skLineSegment(sketch, "E3.15.7.1", {"start": v(205.59, 111.91) * mm, "end": v(215.9, 111.91) * mm});
            skLineSegment(sketch, "E3.15.7.2", {"start": v(205.59, 101.6) * mm, "end": v(215.9, 101.6) * mm});
            skLineSegment(sketch, "E3.15.7.3", {"start": v(215.9, 101.6) * mm, "end": v(215.9, 111.91) * mm});
            skLineSegment(sketch, "E3.15.8.0", {"start": v(205.59, 114.3) * mm, "end": v(205.59, 124.61) * mm});
            skLineSegment(sketch, "E3.15.8.1", {"start": v(205.59, 124.61) * mm, "end": v(215.9, 124.61) * mm});
            skLineSegment(sketch, "E3.15.8.2", {"start": v(205.59, 114.3) * mm, "end": v(215.9, 114.3) * mm});
            skLineSegment(sketch, "E3.15.8.3", {"start": v(215.9, 114.3) * mm, "end": v(215.9, 124.61) * mm});
            skLineSegment(sketch, "E3.15.9.0", {"start": v(205.59, 127) * mm, "end": v(205.59, 137.31) * mm});
            skLineSegment(sketch, "E3.15.9.1", {"start": v(205.59, 137.31) * mm, "end": v(215.9, 137.31) * mm});
            skLineSegment(sketch, "E3.15.9.2", {"start": v(205.59, 127) * mm, "end": v(215.9, 127) * mm});
            skLineSegment(sketch, "E3.15.9.3", {"start": v(215.9, 127) * mm, "end": v(215.9, 137.31) * mm});
            skLineSegment(sketch, "E3.15.10.0", {"start": v(205.59, 139.7) * mm, "end": v(205.59, 150.01) * mm});
            skLineSegment(sketch, "E3.15.10.1", {"start": v(205.59, 150.01) * mm, "end": v(215.9, 150.01) * mm});
            skLineSegment(sketch, "E3.15.10.2", {"start": v(205.59, 139.7) * mm, "end": v(215.9, 139.7) * mm});
            skLineSegment(sketch, "E3.15.10.3", {"start": v(215.9, 139.7) * mm, "end": v(215.9, 150.01) * mm});
            skLineSegment(sketch, "E3.15.11.0", {"start": v(205.59, 152.4) * mm, "end": v(205.59, 162.71) * mm});
            skLineSegment(sketch, "E3.15.11.1", {"start": v(205.59, 162.71) * mm, "end": v(215.9, 162.71) * mm});
            skLineSegment(sketch, "E3.15.11.2", {"start": v(205.59, 152.4) * mm, "end": v(215.9, 152.4) * mm});
            skLineSegment(sketch, "E3.15.11.3", {"start": v(215.9, 152.4) * mm, "end": v(215.9, 162.71) * mm});
            skLineSegment(sketch, "E3.15.12.0", {"start": v(205.59, 165.1) * mm, "end": v(205.59, 175.41) * mm});
            skLineSegment(sketch, "E3.15.12.1", {"start": v(205.59, 175.41) * mm, "end": v(215.9, 175.41) * mm});
            skLineSegment(sketch, "E3.15.12.2", {"start": v(205.59, 165.1) * mm, "end": v(215.9, 165.1) * mm});
            skLineSegment(sketch, "E3.15.12.3", {"start": v(215.9, 165.1) * mm, "end": v(215.9, 175.41) * mm});
            skLineSegment(sketch, "E3.15.13.0", {"start": v(205.59, 177.8) * mm, "end": v(205.59, 188.11) * mm});
            skLineSegment(sketch, "E3.15.13.1", {"start": v(205.59, 188.11) * mm, "end": v(215.9, 188.11) * mm});
            skLineSegment(sketch, "E3.15.13.2", {"start": v(205.59, 177.8) * mm, "end": v(215.9, 177.8) * mm});
            skLineSegment(sketch, "E3.15.13.3", {"start": v(215.9, 177.8) * mm, "end": v(215.9, 188.11) * mm});
            skLineSegment(sketch, "E3.15.14.0", {"start": v(205.59, 190.5) * mm, "end": v(205.59, 200.81) * mm});
            skLineSegment(sketch, "E3.15.14.1", {"start": v(205.59, 200.81) * mm, "end": v(215.9, 200.81) * mm});
            skLineSegment(sketch, "E3.15.14.2", {"start": v(205.59, 190.5) * mm, "end": v(215.9, 190.5) * mm});
            skLineSegment(sketch, "E3.15.14.3", {"start": v(215.9, 190.5) * mm, "end": v(215.9, 200.81) * mm});
            skLineSegment(sketch, "E3.15.15.0", {"start": v(205.59, 203.2) * mm, "end": v(205.59, 213.51) * mm});
            skLineSegment(sketch, "E3.15.15.1", {"start": v(205.59, 213.51) * mm, "end": v(215.9, 213.51) * mm});
            skLineSegment(sketch, "E3.15.15.2", {"start": v(205.59, 203.2) * mm, "end": v(215.9, 203.2) * mm});
            skLineSegment(sketch, "E3.15.15.3", {"start": v(215.9, 203.2) * mm, "end": v(215.9, 213.51) * mm});
            skLineSegment(sketch, "E3.15.16.0", {"start": v(205.59, 215.9) * mm, "end": v(205.59, 226.21) * mm});
            skLineSegment(sketch, "E3.15.16.1", {"start": v(205.59, 226.21) * mm, "end": v(215.9, 226.21) * mm});
            skLineSegment(sketch, "E3.15.16.2", {"start": v(205.59, 215.9) * mm, "end": v(215.9, 215.9) * mm});
            skLineSegment(sketch, "E3.15.16.3", {"start": v(215.9, 215.9) * mm, "end": v(215.9, 226.21) * mm});
            skLineSegment(sketch, "E3.15.17.0", {"start": v(205.59, 228.6) * mm, "end": v(205.59, 238.91) * mm});
            skLineSegment(sketch, "E3.15.17.1", {"start": v(205.59, 238.91) * mm, "end": v(215.9, 238.91) * mm});
            skLineSegment(sketch, "E3.15.17.2", {"start": v(205.59, 228.6) * mm, "end": v(215.9, 228.6) * mm});
            skLineSegment(sketch, "E3.15.17.3", {"start": v(215.9, 228.6) * mm, "end": v(215.9, 238.91) * mm});
            skLineSegment(sketch, "E3.15.18.0", {"start": v(205.59, 241.3) * mm, "end": v(205.59, 251.61) * mm});
            skLineSegment(sketch, "E3.15.18.1", {"start": v(205.59, 251.61) * mm, "end": v(215.9, 251.61) * mm});
            skLineSegment(sketch, "E3.15.18.2", {"start": v(205.59, 241.3) * mm, "end": v(215.9, 241.3) * mm});
            skLineSegment(sketch, "E3.15.18.3", {"start": v(215.9, 241.3) * mm, "end": v(215.9, 251.61) * mm});
            skLineSegment(sketch, "E3.15.19.0", {"start": v(205.59, 254) * mm, "end": v(205.59, 264.31) * mm});
            skLineSegment(sketch, "E3.15.19.1", {"start": v(205.59, 264.31) * mm, "end": v(215.9, 264.31) * mm});
            skLineSegment(sketch, "E3.15.19.2", {"start": v(205.59, 254) * mm, "end": v(215.9, 254) * mm});
            skLineSegment(sketch, "E3.15.19.3", {"start": v(215.9, 254) * mm, "end": v(215.9, 264.31) * mm});
            skLineSegment(sketch, "E3.15.20.0", {"start": v(205.59, 266.7) * mm, "end": v(205.59, 277.01) * mm});
            skLineSegment(sketch, "E3.15.20.1", {"start": v(205.59, 277.01) * mm, "end": v(215.9, 277.01) * mm});
            skLineSegment(sketch, "E3.15.20.2", {"start": v(205.59, 266.7) * mm, "end": v(215.9, 266.7) * mm});
            skLineSegment(sketch, "E3.15.20.3", {"start": v(215.9, 266.7) * mm, "end": v(215.9, 277.01) * mm});
            skLineSegment(sketch, "E3.15.21.0", {"start": v(205.59, 279.4) * mm, "end": v(205.59, 289.71) * mm});
            skLineSegment(sketch, "E3.15.21.1", {"start": v(205.59, 289.71) * mm, "end": v(215.9, 289.71) * mm});
            skLineSegment(sketch, "E3.15.21.2", {"start": v(205.59, 279.4) * mm, "end": v(215.9, 279.4) * mm});
            skLineSegment(sketch, "E3.15.21.3", {"start": v(215.9, 279.4) * mm, "end": v(215.9, 289.71) * mm});
            skLineSegment(sketch, "E3.16.0.0", {"start": v(218.29, 12.7) * mm, "end": v(218.29, 23.01) * mm});
            skLineSegment(sketch, "E3.16.0.1", {"start": v(218.29, 23.01) * mm, "end": v(228.6, 23.01) * mm});
            skLineSegment(sketch, "E3.16.0.2", {"start": v(218.29, 12.7) * mm, "end": v(228.6, 12.7) * mm});
            skLineSegment(sketch, "E3.16.0.3", {"start": v(228.6, 12.7) * mm, "end": v(228.6, 23.01) * mm});
            skLineSegment(sketch, "E3.16.1.0", {"start": v(218.29, 25.4) * mm, "end": v(218.29, 35.71) * mm});
            skLineSegment(sketch, "E3.16.1.1", {"start": v(218.29, 35.71) * mm, "end": v(228.6, 35.71) * mm});
            skLineSegment(sketch, "E3.16.1.2", {"start": v(218.29, 25.4) * mm, "end": v(228.6, 25.4) * mm});
            skLineSegment(sketch, "E3.16.1.3", {"start": v(228.6, 25.4) * mm, "end": v(228.6, 35.71) * mm});
            skLineSegment(sketch, "E3.16.2.0", {"start": v(218.29, 38.1) * mm, "end": v(218.29, 48.41) * mm});
            skLineSegment(sketch, "E3.16.2.1", {"start": v(218.29, 48.41) * mm, "end": v(228.6, 48.41) * mm});
            skLineSegment(sketch, "E3.16.2.2", {"start": v(218.29, 38.1) * mm, "end": v(228.6, 38.1) * mm});
            skLineSegment(sketch, "E3.16.2.3", {"start": v(228.6, 38.1) * mm, "end": v(228.6, 48.41) * mm});
            skLineSegment(sketch, "E3.16.3.0", {"start": v(218.29, 50.8) * mm, "end": v(218.29, 61.11) * mm});
            skLineSegment(sketch, "E3.16.3.1", {"start": v(218.29, 61.11) * mm, "end": v(228.6, 61.11) * mm});
            skLineSegment(sketch, "E3.16.3.2", {"start": v(218.29, 50.8) * mm, "end": v(228.6, 50.8) * mm});
            skLineSegment(sketch, "E3.16.3.3", {"start": v(228.6, 50.8) * mm, "end": v(228.6, 61.11) * mm});
            skLineSegment(sketch, "E3.16.4.0", {"start": v(218.29, 63.5) * mm, "end": v(218.29, 73.81) * mm});
            skLineSegment(sketch, "E3.16.4.1", {"start": v(218.29, 73.81) * mm, "end": v(228.6, 73.81) * mm});
            skLineSegment(sketch, "E3.16.4.2", {"start": v(218.29, 63.5) * mm, "end": v(228.6, 63.5) * mm});
            skLineSegment(sketch, "E3.16.4.3", {"start": v(228.6, 63.5) * mm, "end": v(228.6, 73.81) * mm});
            skLineSegment(sketch, "E3.16.5.0", {"start": v(218.29, 76.2) * mm, "end": v(218.29, 86.51) * mm});
            skLineSegment(sketch, "E3.16.5.1", {"start": v(218.29, 86.51) * mm, "end": v(228.6, 86.51) * mm});
            skLineSegment(sketch, "E3.16.5.2", {"start": v(218.29, 76.2) * mm, "end": v(228.6, 76.2) * mm});
            skLineSegment(sketch, "E3.16.5.3", {"start": v(228.6, 76.2) * mm, "end": v(228.6, 86.51) * mm});
            skLineSegment(sketch, "E3.16.6.0", {"start": v(218.29, 88.9) * mm, "end": v(218.29, 99.21) * mm});
            skLineSegment(sketch, "E3.16.6.1", {"start": v(218.29, 99.21) * mm, "end": v(228.6, 99.21) * mm});
            skLineSegment(sketch, "E3.16.6.2", {"start": v(218.29, 88.9) * mm, "end": v(228.6, 88.9) * mm});
            skLineSegment(sketch, "E3.16.6.3", {"start": v(228.6, 88.9) * mm, "end": v(228.6, 99.21) * mm});
            skLineSegment(sketch, "E3.16.7.0", {"start": v(218.29, 101.6) * mm, "end": v(218.29, 111.91) * mm});
            skLineSegment(sketch, "E3.16.7.1", {"start": v(218.29, 111.91) * mm, "end": v(228.6, 111.91) * mm});
            skLineSegment(sketch, "E3.16.7.2", {"start": v(218.29, 101.6) * mm, "end": v(228.6, 101.6) * mm});
            skLineSegment(sketch, "E3.16.7.3", {"start": v(228.6, 101.6) * mm, "end": v(228.6, 111.91) * mm});
            skLineSegment(sketch, "E3.16.8.0", {"start": v(218.29, 114.3) * mm, "end": v(218.29, 124.61) * mm});
            skLineSegment(sketch, "E3.16.8.1", {"start": v(218.29, 124.61) * mm, "end": v(228.6, 124.61) * mm});
            skLineSegment(sketch, "E3.16.8.2", {"start": v(218.29, 114.3) * mm, "end": v(228.6, 114.3) * mm});
            skLineSegment(sketch, "E3.16.8.3", {"start": v(228.6, 114.3) * mm, "end": v(228.6, 124.61) * mm});
            skLineSegment(sketch, "E3.16.9.0", {"start": v(218.29, 127) * mm, "end": v(218.29, 137.31) * mm});
            skLineSegment(sketch, "E3.16.9.1", {"start": v(218.29, 137.31) * mm, "end": v(228.6, 137.31) * mm});
            skLineSegment(sketch, "E3.16.9.2", {"start": v(218.29, 127) * mm, "end": v(228.6, 127) * mm});
            skLineSegment(sketch, "E3.16.9.3", {"start": v(228.6, 127) * mm, "end": v(228.6, 137.31) * mm});
            skLineSegment(sketch, "E3.16.10.0", {"start": v(218.29, 139.7) * mm, "end": v(218.29, 150.01) * mm});
            skLineSegment(sketch, "E3.16.10.1", {"start": v(218.29, 150.01) * mm, "end": v(228.6, 150.01) * mm});
            skLineSegment(sketch, "E3.16.10.2", {"start": v(218.29, 139.7) * mm, "end": v(228.6, 139.7) * mm});
            skLineSegment(sketch, "E3.16.10.3", {"start": v(228.6, 139.7) * mm, "end": v(228.6, 150.01) * mm});
            skLineSegment(sketch, "E3.16.11.0", {"start": v(218.29, 152.4) * mm, "end": v(218.29, 162.71) * mm});
            skLineSegment(sketch, "E3.16.11.1", {"start": v(218.29, 162.71) * mm, "end": v(228.6, 162.71) * mm});
            skLineSegment(sketch, "E3.16.11.2", {"start": v(218.29, 152.4) * mm, "end": v(228.6, 152.4) * mm});
            skLineSegment(sketch, "E3.16.11.3", {"start": v(228.6, 152.4) * mm, "end": v(228.6, 162.71) * mm});
            skLineSegment(sketch, "E3.16.12.0", {"start": v(218.29, 165.1) * mm, "end": v(218.29, 175.41) * mm});
            skLineSegment(sketch, "E3.16.12.1", {"start": v(218.29, 175.41) * mm, "end": v(228.6, 175.41) * mm});
            skLineSegment(sketch, "E3.16.12.2", {"start": v(218.29, 165.1) * mm, "end": v(228.6, 165.1) * mm});
            skLineSegment(sketch, "E3.16.12.3", {"start": v(228.6, 165.1) * mm, "end": v(228.6, 175.41) * mm});
            skLineSegment(sketch, "E3.16.13.0", {"start": v(218.29, 177.8) * mm, "end": v(218.29, 188.11) * mm});
            skLineSegment(sketch, "E3.16.13.1", {"start": v(218.29, 188.11) * mm, "end": v(228.6, 188.11) * mm});
            skLineSegment(sketch, "E3.16.13.2", {"start": v(218.29, 177.8) * mm, "end": v(228.6, 177.8) * mm});
            skLineSegment(sketch, "E3.16.13.3", {"start": v(228.6, 177.8) * mm, "end": v(228.6, 188.11) * mm});
            skLineSegment(sketch, "E3.16.14.0", {"start": v(218.29, 190.5) * mm, "end": v(218.29, 200.81) * mm});
            skLineSegment(sketch, "E3.16.14.1", {"start": v(218.29, 200.81) * mm, "end": v(228.6, 200.81) * mm});
            skLineSegment(sketch, "E3.16.14.2", {"start": v(218.29, 190.5) * mm, "end": v(228.6, 190.5) * mm});
            skLineSegment(sketch, "E3.16.14.3", {"start": v(228.6, 190.5) * mm, "end": v(228.6, 200.81) * mm});
            skLineSegment(sketch, "E3.16.15.0", {"start": v(218.29, 203.2) * mm, "end": v(218.29, 213.51) * mm});
            skLineSegment(sketch, "E3.16.15.1", {"start": v(218.29, 213.51) * mm, "end": v(228.6, 213.51) * mm});
            skLineSegment(sketch, "E3.16.15.2", {"start": v(218.29, 203.2) * mm, "end": v(228.6, 203.2) * mm});
            skLineSegment(sketch, "E3.16.15.3", {"start": v(228.6, 203.2) * mm, "end": v(228.6, 213.51) * mm});
            skLineSegment(sketch, "E3.16.16.0", {"start": v(218.29, 215.9) * mm, "end": v(218.29, 226.21) * mm});
            skLineSegment(sketch, "E3.16.16.1", {"start": v(218.29, 226.21) * mm, "end": v(228.6, 226.21) * mm});
            skLineSegment(sketch, "E3.16.16.2", {"start": v(218.29, 215.9) * mm, "end": v(228.6, 215.9) * mm});
            skLineSegment(sketch, "E3.16.16.3", {"start": v(228.6, 215.9) * mm, "end": v(228.6, 226.21) * mm});
            skLineSegment(sketch, "E3.16.17.0", {"start": v(218.29, 228.6) * mm, "end": v(218.29, 238.91) * mm});
            skLineSegment(sketch, "E3.16.17.1", {"start": v(218.29, 238.91) * mm, "end": v(228.6, 238.91) * mm});
            skLineSegment(sketch, "E3.16.17.2", {"start": v(218.29, 228.6) * mm, "end": v(228.6, 228.6) * mm});
            skLineSegment(sketch, "E3.16.17.3", {"start": v(228.6, 228.6) * mm, "end": v(228.6, 238.91) * mm});
            skLineSegment(sketch, "E3.16.18.0", {"start": v(218.29, 241.3) * mm, "end": v(218.29, 251.61) * mm});
            skLineSegment(sketch, "E3.16.18.1", {"start": v(218.29, 251.61) * mm, "end": v(228.6, 251.61) * mm});
            skLineSegment(sketch, "E3.16.18.2", {"start": v(218.29, 241.3) * mm, "end": v(228.6, 241.3) * mm});
            skLineSegment(sketch, "E3.16.18.3", {"start": v(228.6, 241.3) * mm, "end": v(228.6, 251.61) * mm});
            skLineSegment(sketch, "E3.16.19.0", {"start": v(218.29, 254) * mm, "end": v(218.29, 264.31) * mm});
            skLineSegment(sketch, "E3.16.19.1", {"start": v(218.29, 264.31) * mm, "end": v(228.6, 264.31) * mm});
            skLineSegment(sketch, "E3.16.19.2", {"start": v(218.29, 254) * mm, "end": v(228.6, 254) * mm});
            skLineSegment(sketch, "E3.16.19.3", {"start": v(228.6, 254) * mm, "end": v(228.6, 264.31) * mm});
            skLineSegment(sketch, "E3.16.20.0", {"start": v(218.29, 266.7) * mm, "end": v(218.29, 277.01) * mm});
            skLineSegment(sketch, "E3.16.20.1", {"start": v(218.29, 277.01) * mm, "end": v(228.6, 277.01) * mm});
            skLineSegment(sketch, "E3.16.20.2", {"start": v(218.29, 266.7) * mm, "end": v(228.6, 266.7) * mm});
            skLineSegment(sketch, "E3.16.20.3", {"start": v(228.6, 266.7) * mm, "end": v(228.6, 277.01) * mm});
            skLineSegment(sketch, "E3.16.21.0", {"start": v(218.29, 279.4) * mm, "end": v(218.29, 289.71) * mm});
            skLineSegment(sketch, "E3.16.21.1", {"start": v(218.29, 289.71) * mm, "end": v(228.6, 289.71) * mm});
            skLineSegment(sketch, "E3.16.21.2", {"start": v(218.29, 279.4) * mm, "end": v(228.6, 279.4) * mm});
            skLineSegment(sketch, "E3.16.21.3", {"start": v(228.6, 279.4) * mm, "end": v(228.6, 289.71) * mm});
            skLineSegment(sketch, "E3.17.0.0", {"start": v(230.99, 12.7) * mm, "end": v(230.99, 23.01) * mm});
            skLineSegment(sketch, "E3.17.0.1", {"start": v(230.99, 23.01) * mm, "end": v(241.3, 23.01) * mm});
            skLineSegment(sketch, "E3.17.0.2", {"start": v(230.99, 12.7) * mm, "end": v(241.3, 12.7) * mm});
            skLineSegment(sketch, "E3.17.0.3", {"start": v(241.3, 12.7) * mm, "end": v(241.3, 23.01) * mm});
            skLineSegment(sketch, "E3.17.1.0", {"start": v(230.99, 25.4) * mm, "end": v(230.99, 35.71) * mm});
            skLineSegment(sketch, "E3.17.1.1", {"start": v(230.99, 35.71) * mm, "end": v(241.3, 35.71) * mm});
            skLineSegment(sketch, "E3.17.1.2", {"start": v(230.99, 25.4) * mm, "end": v(241.3, 25.4) * mm});
            skLineSegment(sketch, "E3.17.1.3", {"start": v(241.3, 25.4) * mm, "end": v(241.3, 35.71) * mm});
            skLineSegment(sketch, "E3.17.2.0", {"start": v(230.99, 38.1) * mm, "end": v(230.99, 48.41) * mm});
            skLineSegment(sketch, "E3.17.2.1", {"start": v(230.99, 48.41) * mm, "end": v(241.3, 48.41) * mm});
            skLineSegment(sketch, "E3.17.2.2", {"start": v(230.99, 38.1) * mm, "end": v(241.3, 38.1) * mm});
            skLineSegment(sketch, "E3.17.2.3", {"start": v(241.3, 38.1) * mm, "end": v(241.3, 48.41) * mm});
            skLineSegment(sketch, "E3.17.3.0", {"start": v(230.99, 50.8) * mm, "end": v(230.99, 61.11) * mm});
            skLineSegment(sketch, "E3.17.3.1", {"start": v(230.99, 61.11) * mm, "end": v(241.3, 61.11) * mm});
            skLineSegment(sketch, "E3.17.3.2", {"start": v(230.99, 50.8) * mm, "end": v(241.3, 50.8) * mm});
            skLineSegment(sketch, "E3.17.3.3", {"start": v(241.3, 50.8) * mm, "end": v(241.3, 61.11) * mm});
            skLineSegment(sketch, "E3.17.4.0", {"start": v(230.99, 63.5) * mm, "end": v(230.99, 73.81) * mm});
            skLineSegment(sketch, "E3.17.4.1", {"start": v(230.99, 73.81) * mm, "end": v(241.3, 73.81) * mm});
            skLineSegment(sketch, "E3.17.4.2", {"start": v(230.99, 63.5) * mm, "end": v(241.3, 63.5) * mm});
            skLineSegment(sketch, "E3.17.4.3", {"start": v(241.3, 63.5) * mm, "end": v(241.3, 73.81) * mm});
            skLineSegment(sketch, "E3.17.5.0", {"start": v(230.99, 76.2) * mm, "end": v(230.99, 86.51) * mm});
            skLineSegment(sketch, "E3.17.5.1", {"start": v(230.99, 86.51) * mm, "end": v(241.3, 86.51) * mm});
            skLineSegment(sketch, "E3.17.5.2", {"start": v(230.99, 76.2) * mm, "end": v(241.3, 76.2) * mm});
            skLineSegment(sketch, "E3.17.5.3", {"start": v(241.3, 76.2) * mm, "end": v(241.3, 86.51) * mm});
            skLineSegment(sketch, "E3.17.6.0", {"start": v(230.99, 88.9) * mm, "end": v(230.99, 99.21) * mm});
            skLineSegment(sketch, "E3.17.6.1", {"start": v(230.99, 99.21) * mm, "end": v(241.3, 99.21) * mm});
            skLineSegment(sketch, "E3.17.6.2", {"start": v(230.99, 88.9) * mm, "end": v(241.3, 88.9) * mm});
            skLineSegment(sketch, "E3.17.6.3", {"start": v(241.3, 88.9) * mm, "end": v(241.3, 99.21) * mm});
            skLineSegment(sketch, "E3.17.7.0", {"start": v(230.99, 101.6) * mm, "end": v(230.99, 111.91) * mm});
            skLineSegment(sketch, "E3.17.7.1", {"start": v(230.99, 111.91) * mm, "end": v(241.3, 111.91) * mm});
            skLineSegment(sketch, "E3.17.7.2", {"start": v(230.99, 101.6) * mm, "end": v(241.3, 101.6) * mm});
            skLineSegment(sketch, "E3.17.7.3", {"start": v(241.3, 101.6) * mm, "end": v(241.3, 111.91) * mm});
            skLineSegment(sketch, "E3.17.8.0", {"start": v(230.99, 114.3) * mm, "end": v(230.99, 124.61) * mm});
            skLineSegment(sketch, "E3.17.8.1", {"start": v(230.99, 124.61) * mm, "end": v(241.3, 124.61) * mm});
            skLineSegment(sketch, "E3.17.8.2", {"start": v(230.99, 114.3) * mm, "end": v(241.3, 114.3) * mm});
            skLineSegment(sketch, "E3.17.8.3", {"start": v(241.3, 114.3) * mm, "end": v(241.3, 124.61) * mm});
            skLineSegment(sketch, "E3.17.9.0", {"start": v(230.99, 127) * mm, "end": v(230.99, 137.31) * mm});
            skLineSegment(sketch, "E3.17.9.1", {"start": v(230.99, 137.31) * mm, "end": v(241.3, 137.31) * mm});
            skLineSegment(sketch, "E3.17.9.2", {"start": v(230.99, 127) * mm, "end": v(241.3, 127) * mm});
            skLineSegment(sketch, "E3.17.9.3", {"start": v(241.3, 127) * mm, "end": v(241.3, 137.31) * mm});
            skLineSegment(sketch, "E3.17.10.0", {"start": v(230.99, 139.7) * mm, "end": v(230.99, 150.01) * mm});
            skLineSegment(sketch, "E3.17.10.1", {"start": v(230.99, 150.01) * mm, "end": v(241.3, 150.01) * mm});
            skLineSegment(sketch, "E3.17.10.2", {"start": v(230.99, 139.7) * mm, "end": v(241.3, 139.7) * mm});
            skLineSegment(sketch, "E3.17.10.3", {"start": v(241.3, 139.7) * mm, "end": v(241.3, 150.01) * mm});
            skLineSegment(sketch, "E3.17.11.0", {"start": v(230.99, 152.4) * mm, "end": v(230.99, 162.71) * mm});
            skLineSegment(sketch, "E3.17.11.1", {"start": v(230.99, 162.71) * mm, "end": v(241.3, 162.71) * mm});
            skLineSegment(sketch, "E3.17.11.2", {"start": v(230.99, 152.4) * mm, "end": v(241.3, 152.4) * mm});
            skLineSegment(sketch, "E3.17.11.3", {"start": v(241.3, 152.4) * mm, "end": v(241.3, 162.71) * mm});
            skLineSegment(sketch, "E3.17.12.0", {"start": v(230.99, 165.1) * mm, "end": v(230.99, 175.41) * mm});
            skLineSegment(sketch, "E3.17.12.1", {"start": v(230.99, 175.41) * mm, "end": v(241.3, 175.41) * mm});
            skLineSegment(sketch, "E3.17.12.2", {"start": v(230.99, 165.1) * mm, "end": v(241.3, 165.1) * mm});
            skLineSegment(sketch, "E3.17.12.3", {"start": v(241.3, 165.1) * mm, "end": v(241.3, 175.41) * mm});
            skLineSegment(sketch, "E3.17.13.0", {"start": v(230.99, 177.8) * mm, "end": v(230.99, 188.11) * mm});
            skLineSegment(sketch, "E3.17.13.1", {"start": v(230.99, 188.11) * mm, "end": v(241.3, 188.11) * mm});
            skLineSegment(sketch, "E3.17.13.2", {"start": v(230.99, 177.8) * mm, "end": v(241.3, 177.8) * mm});
            skLineSegment(sketch, "E3.17.13.3", {"start": v(241.3, 177.8) * mm, "end": v(241.3, 188.11) * mm});
            skLineSegment(sketch, "E3.17.14.0", {"start": v(230.99, 190.5) * mm, "end": v(230.99, 200.81) * mm});
            skLineSegment(sketch, "E3.17.14.1", {"start": v(230.99, 200.81) * mm, "end": v(241.3, 200.81) * mm});
            skLineSegment(sketch, "E3.17.14.2", {"start": v(230.99, 190.5) * mm, "end": v(241.3, 190.5) * mm});
            skLineSegment(sketch, "E3.17.14.3", {"start": v(241.3, 190.5) * mm, "end": v(241.3, 200.81) * mm});
            skLineSegment(sketch, "E3.17.15.0", {"start": v(230.99, 203.2) * mm, "end": v(230.99, 213.51) * mm});
            skLineSegment(sketch, "E3.17.15.1", {"start": v(230.99, 213.51) * mm, "end": v(241.3, 213.51) * mm});
            skLineSegment(sketch, "E3.17.15.2", {"start": v(230.99, 203.2) * mm, "end": v(241.3, 203.2) * mm});
            skLineSegment(sketch, "E3.17.15.3", {"start": v(241.3, 203.2) * mm, "end": v(241.3, 213.51) * mm});
            skLineSegment(sketch, "E3.17.16.0", {"start": v(230.99, 215.9) * mm, "end": v(230.99, 226.21) * mm});
            skLineSegment(sketch, "E3.17.16.1", {"start": v(230.99, 226.21) * mm, "end": v(241.3, 226.21) * mm});
            skLineSegment(sketch, "E3.17.16.2", {"start": v(230.99, 215.9) * mm, "end": v(241.3, 215.9) * mm});
            skLineSegment(sketch, "E3.17.16.3", {"start": v(241.3, 215.9) * mm, "end": v(241.3, 226.21) * mm});
            skLineSegment(sketch, "E3.17.17.0", {"start": v(230.99, 228.6) * mm, "end": v(230.99, 238.91) * mm});
            skLineSegment(sketch, "E3.17.17.1", {"start": v(230.99, 238.91) * mm, "end": v(241.3, 238.91) * mm});
            skLineSegment(sketch, "E3.17.17.2", {"start": v(230.99, 228.6) * mm, "end": v(241.3, 228.6) * mm});
            skLineSegment(sketch, "E3.17.17.3", {"start": v(241.3, 228.6) * mm, "end": v(241.3, 238.91) * mm});
            skLineSegment(sketch, "E3.17.18.0", {"start": v(230.99, 241.3) * mm, "end": v(230.99, 251.61) * mm});
            skLineSegment(sketch, "E3.17.18.1", {"start": v(230.99, 251.61) * mm, "end": v(241.3, 251.61) * mm});
            skLineSegment(sketch, "E3.17.18.2", {"start": v(230.99, 241.3) * mm, "end": v(241.3, 241.3) * mm});
            skLineSegment(sketch, "E3.17.18.3", {"start": v(241.3, 241.3) * mm, "end": v(241.3, 251.61) * mm});
            skLineSegment(sketch, "E3.17.19.0", {"start": v(230.99, 254) * mm, "end": v(230.99, 264.31) * mm});
            skLineSegment(sketch, "E3.17.19.1", {"start": v(230.99, 264.31) * mm, "end": v(241.3, 264.31) * mm});
            skLineSegment(sketch, "E3.17.19.2", {"start": v(230.99, 254) * mm, "end": v(241.3, 254) * mm});
            skLineSegment(sketch, "E3.17.19.3", {"start": v(241.3, 254) * mm, "end": v(241.3, 264.31) * mm});
            skLineSegment(sketch, "E3.17.20.0", {"start": v(230.99, 266.7) * mm, "end": v(230.99, 277.01) * mm});
            skLineSegment(sketch, "E3.17.20.1", {"start": v(230.99, 277.01) * mm, "end": v(241.3, 277.01) * mm});
            skLineSegment(sketch, "E3.17.20.2", {"start": v(230.99, 266.7) * mm, "end": v(241.3, 266.7) * mm});
            skLineSegment(sketch, "E3.17.20.3", {"start": v(241.3, 266.7) * mm, "end": v(241.3, 277.01) * mm});
            skLineSegment(sketch, "E3.17.21.0", {"start": v(230.99, 279.4) * mm, "end": v(230.99, 289.71) * mm});
            skLineSegment(sketch, "E3.17.21.1", {"start": v(230.99, 289.71) * mm, "end": v(241.3, 289.71) * mm});
            skLineSegment(sketch, "E3.17.21.2", {"start": v(230.99, 279.4) * mm, "end": v(241.3, 279.4) * mm});
            skLineSegment(sketch, "E3.17.21.3", {"start": v(241.3, 279.4) * mm, "end": v(241.3, 289.71) * mm});
            skLineSegment(sketch, "E3.18.0.0", {"start": v(243.69, 12.7) * mm, "end": v(243.69, 23.01) * mm});
            skLineSegment(sketch, "E3.18.0.1", {"start": v(243.69, 23.01) * mm, "end": v(254, 23.01) * mm});
            skLineSegment(sketch, "E3.18.0.2", {"start": v(243.69, 12.7) * mm, "end": v(254, 12.7) * mm});
            skLineSegment(sketch, "E3.18.0.3", {"start": v(254, 12.7) * mm, "end": v(254, 23.01) * mm});
            skLineSegment(sketch, "E3.18.1.0", {"start": v(243.69, 25.4) * mm, "end": v(243.69, 35.71) * mm});
            skLineSegment(sketch, "E3.18.1.1", {"start": v(243.69, 35.71) * mm, "end": v(254, 35.71) * mm});
            skLineSegment(sketch, "E3.18.1.2", {"start": v(243.69, 25.4) * mm, "end": v(254, 25.4) * mm});
            skLineSegment(sketch, "E3.18.1.3", {"start": v(254, 25.4) * mm, "end": v(254, 35.71) * mm});
            skLineSegment(sketch, "E3.18.2.0", {"start": v(243.69, 38.1) * mm, "end": v(243.69, 48.41) * mm});
            skLineSegment(sketch, "E3.18.2.1", {"start": v(243.69, 48.41) * mm, "end": v(254, 48.41) * mm});
            skLineSegment(sketch, "E3.18.2.2", {"start": v(243.69, 38.1) * mm, "end": v(254, 38.1) * mm});
            skLineSegment(sketch, "E3.18.2.3", {"start": v(254, 38.1) * mm, "end": v(254, 48.41) * mm});
            skLineSegment(sketch, "E3.18.3.0", {"start": v(243.69, 50.8) * mm, "end": v(243.69, 61.11) * mm});
            skLineSegment(sketch, "E3.18.3.1", {"start": v(243.69, 61.11) * mm, "end": v(254, 61.11) * mm});
            skLineSegment(sketch, "E3.18.3.2", {"start": v(243.69, 50.8) * mm, "end": v(254, 50.8) * mm});
            skLineSegment(sketch, "E3.18.3.3", {"start": v(254, 50.8) * mm, "end": v(254, 61.11) * mm});
            skLineSegment(sketch, "E3.18.4.0", {"start": v(243.69, 63.5) * mm, "end": v(243.69, 73.81) * mm});
            skLineSegment(sketch, "E3.18.4.1", {"start": v(243.69, 73.81) * mm, "end": v(254, 73.81) * mm});
            skLineSegment(sketch, "E3.18.4.2", {"start": v(243.69, 63.5) * mm, "end": v(254, 63.5) * mm});
            skLineSegment(sketch, "E3.18.4.3", {"start": v(254, 63.5) * mm, "end": v(254, 73.81) * mm});
            skLineSegment(sketch, "E3.18.5.0", {"start": v(243.69, 76.2) * mm, "end": v(243.69, 86.51) * mm});
            skLineSegment(sketch, "E3.18.5.1", {"start": v(243.69, 86.51) * mm, "end": v(254, 86.51) * mm});
            skLineSegment(sketch, "E3.18.5.2", {"start": v(243.69, 76.2) * mm, "end": v(254, 76.2) * mm});
            skLineSegment(sketch, "E3.18.5.3", {"start": v(254, 76.2) * mm, "end": v(254, 86.51) * mm});
            skLineSegment(sketch, "E3.18.6.0", {"start": v(243.69, 88.9) * mm, "end": v(243.69, 99.21) * mm});
            skLineSegment(sketch, "E3.18.6.1", {"start": v(243.69, 99.21) * mm, "end": v(254, 99.21) * mm});
            skLineSegment(sketch, "E3.18.6.2", {"start": v(243.69, 88.9) * mm, "end": v(254, 88.9) * mm});
            skLineSegment(sketch, "E3.18.6.3", {"start": v(254, 88.9) * mm, "end": v(254, 99.21) * mm});
            skLineSegment(sketch, "E3.18.7.0", {"start": v(243.69, 101.6) * mm, "end": v(243.69, 111.91) * mm});
            skLineSegment(sketch, "E3.18.7.1", {"start": v(243.69, 111.91) * mm, "end": v(254, 111.91) * mm});
            skLineSegment(sketch, "E3.18.7.2", {"start": v(243.69, 101.6) * mm, "end": v(254, 101.6) * mm});
            skLineSegment(sketch, "E3.18.7.3", {"start": v(254, 101.6) * mm, "end": v(254, 111.91) * mm});
            skLineSegment(sketch, "E3.18.8.0", {"start": v(243.69, 114.3) * mm, "end": v(243.69, 124.61) * mm});
            skLineSegment(sketch, "E3.18.8.1", {"start": v(243.69, 124.61) * mm, "end": v(254, 124.61) * mm});
            skLineSegment(sketch, "E3.18.8.2", {"start": v(243.69, 114.3) * mm, "end": v(254, 114.3) * mm});
            skLineSegment(sketch, "E3.18.8.3", {"start": v(254, 114.3) * mm, "end": v(254, 124.61) * mm});
            skLineSegment(sketch, "E3.18.9.0", {"start": v(243.69, 127) * mm, "end": v(243.69, 137.31) * mm});
            skLineSegment(sketch, "E3.18.9.1", {"start": v(243.69, 137.31) * mm, "end": v(254, 137.31) * mm});
            skLineSegment(sketch, "E3.18.9.2", {"start": v(243.69, 127) * mm, "end": v(254, 127) * mm});
            skLineSegment(sketch, "E3.18.9.3", {"start": v(254, 127) * mm, "end": v(254, 137.31) * mm});
            skLineSegment(sketch, "E3.18.10.0", {"start": v(243.69, 139.7) * mm, "end": v(243.69, 150.01) * mm});
            skLineSegment(sketch, "E3.18.10.1", {"start": v(243.69, 150.01) * mm, "end": v(254, 150.01) * mm});
            skLineSegment(sketch, "E3.18.10.2", {"start": v(243.69, 139.7) * mm, "end": v(254, 139.7) * mm});
            skLineSegment(sketch, "E3.18.10.3", {"start": v(254, 139.7) * mm, "end": v(254, 150.01) * mm});
            skLineSegment(sketch, "E3.18.11.0", {"start": v(243.69, 152.4) * mm, "end": v(243.69, 162.71) * mm});
            skLineSegment(sketch, "E3.18.11.1", {"start": v(243.69, 162.71) * mm, "end": v(254, 162.71) * mm});
            skLineSegment(sketch, "E3.18.11.2", {"start": v(243.69, 152.4) * mm, "end": v(254, 152.4) * mm});
            skLineSegment(sketch, "E3.18.11.3", {"start": v(254, 152.4) * mm, "end": v(254, 162.71) * mm});
            skLineSegment(sketch, "E3.18.12.0", {"start": v(243.69, 165.1) * mm, "end": v(243.69, 175.41) * mm});
            skLineSegment(sketch, "E3.18.12.1", {"start": v(243.69, 175.41) * mm, "end": v(254, 175.41) * mm});
            skLineSegment(sketch, "E3.18.12.2", {"start": v(243.69, 165.1) * mm, "end": v(254, 165.1) * mm});
            skLineSegment(sketch, "E3.18.12.3", {"start": v(254, 165.1) * mm, "end": v(254, 175.41) * mm});
            skLineSegment(sketch, "E3.18.13.0", {"start": v(243.69, 177.8) * mm, "end": v(243.69, 188.11) * mm});
            skLineSegment(sketch, "E3.18.13.1", {"start": v(243.69, 188.11) * mm, "end": v(254, 188.11) * mm});
            skLineSegment(sketch, "E3.18.13.2", {"start": v(243.69, 177.8) * mm, "end": v(254, 177.8) * mm});
            skLineSegment(sketch, "E3.18.13.3", {"start": v(254, 177.8) * mm, "end": v(254, 188.11) * mm});
            skLineSegment(sketch, "E3.18.14.0", {"start": v(243.69, 190.5) * mm, "end": v(243.69, 200.81) * mm});
            skLineSegment(sketch, "E3.18.14.1", {"start": v(243.69, 200.81) * mm, "end": v(254, 200.81) * mm});
            skLineSegment(sketch, "E3.18.14.2", {"start": v(243.69, 190.5) * mm, "end": v(254, 190.5) * mm});
            skLineSegment(sketch, "E3.18.14.3", {"start": v(254, 190.5) * mm, "end": v(254, 200.81) * mm});
            skLineSegment(sketch, "E3.18.15.0", {"start": v(243.69, 203.2) * mm, "end": v(243.69, 213.51) * mm});
            skLineSegment(sketch, "E3.18.15.1", {"start": v(243.69, 213.51) * mm, "end": v(254, 213.51) * mm});
            skLineSegment(sketch, "E3.18.15.2", {"start": v(243.69, 203.2) * mm, "end": v(254, 203.2) * mm});
            skLineSegment(sketch, "E3.18.15.3", {"start": v(254, 203.2) * mm, "end": v(254, 213.51) * mm});
            skLineSegment(sketch, "E3.18.16.0", {"start": v(243.69, 215.9) * mm, "end": v(243.69, 226.21) * mm});
            skLineSegment(sketch, "E3.18.16.1", {"start": v(243.69, 226.21) * mm, "end": v(254, 226.21) * mm});
            skLineSegment(sketch, "E3.18.16.2", {"start": v(243.69, 215.9) * mm, "end": v(254, 215.9) * mm});
            skLineSegment(sketch, "E3.18.16.3", {"start": v(254, 215.9) * mm, "end": v(254, 226.21) * mm});
            skLineSegment(sketch, "E3.18.17.0", {"start": v(243.69, 228.6) * mm, "end": v(243.69, 238.91) * mm});
            skLineSegment(sketch, "E3.18.17.1", {"start": v(243.69, 238.91) * mm, "end": v(254, 238.91) * mm});
            skLineSegment(sketch, "E3.18.17.2", {"start": v(243.69, 228.6) * mm, "end": v(254, 228.6) * mm});
            skLineSegment(sketch, "E3.18.17.3", {"start": v(254, 228.6) * mm, "end": v(254, 238.91) * mm});
            skLineSegment(sketch, "E3.18.18.0", {"start": v(243.69, 241.3) * mm, "end": v(243.69, 251.61) * mm});
            skLineSegment(sketch, "E3.18.18.1", {"start": v(243.69, 251.61) * mm, "end": v(254, 251.61) * mm});
            skLineSegment(sketch, "E3.18.18.2", {"start": v(243.69, 241.3) * mm, "end": v(254, 241.3) * mm});
            skLineSegment(sketch, "E3.18.18.3", {"start": v(254, 241.3) * mm, "end": v(254, 251.61) * mm});
            skLineSegment(sketch, "E3.18.19.0", {"start": v(243.69, 254) * mm, "end": v(243.69, 264.31) * mm});
            skLineSegment(sketch, "E3.18.19.1", {"start": v(243.69, 264.31) * mm, "end": v(254, 264.31) * mm});
            skLineSegment(sketch, "E3.18.19.2", {"start": v(243.69, 254) * mm, "end": v(254, 254) * mm});
            skLineSegment(sketch, "E3.18.19.3", {"start": v(254, 254) * mm, "end": v(254, 264.31) * mm});
            skLineSegment(sketch, "E3.18.20.0", {"start": v(243.69, 266.7) * mm, "end": v(243.69, 277.01) * mm});
            skLineSegment(sketch, "E3.18.20.1", {"start": v(243.69, 277.01) * mm, "end": v(254, 277.01) * mm});
            skLineSegment(sketch, "E3.18.20.2", {"start": v(243.69, 266.7) * mm, "end": v(254, 266.7) * mm});
            skLineSegment(sketch, "E3.18.20.3", {"start": v(254, 266.7) * mm, "end": v(254, 277.01) * mm});
            skLineSegment(sketch, "E3.18.21.0", {"start": v(243.69, 279.4) * mm, "end": v(243.69, 289.71) * mm});
            skLineSegment(sketch, "E3.18.21.1", {"start": v(243.69, 289.71) * mm, "end": v(254, 289.71) * mm});
            skLineSegment(sketch, "E3.18.21.2", {"start": v(243.69, 279.4) * mm, "end": v(254, 279.4) * mm});
            skLineSegment(sketch, "E3.18.21.3", {"start": v(254, 279.4) * mm, "end": v(254, 289.71) * mm});
            skLineSegment(sketch, "E3.19.0.0", {"start": v(256.39, 12.7) * mm, "end": v(256.39, 23.01) * mm});
            skLineSegment(sketch, "E3.19.0.1", {"start": v(256.39, 23.01) * mm, "end": v(266.7, 23.01) * mm});
            skLineSegment(sketch, "E3.19.0.2", {"start": v(256.39, 12.7) * mm, "end": v(266.7, 12.7) * mm});
            skLineSegment(sketch, "E3.19.0.3", {"start": v(266.7, 12.7) * mm, "end": v(266.7, 23.01) * mm});
            skLineSegment(sketch, "E3.19.1.0", {"start": v(256.39, 25.4) * mm, "end": v(256.39, 35.71) * mm});
            skLineSegment(sketch, "E3.19.1.1", {"start": v(256.39, 35.71) * mm, "end": v(266.7, 35.71) * mm});
            skLineSegment(sketch, "E3.19.1.2", {"start": v(256.39, 25.4) * mm, "end": v(266.7, 25.4) * mm});
            skLineSegment(sketch, "E3.19.1.3", {"start": v(266.7, 25.4) * mm, "end": v(266.7, 35.71) * mm});
            skLineSegment(sketch, "E3.19.2.0", {"start": v(256.39, 38.1) * mm, "end": v(256.39, 48.41) * mm});
            skLineSegment(sketch, "E3.19.2.1", {"start": v(256.39, 48.41) * mm, "end": v(266.7, 48.41) * mm});
            skLineSegment(sketch, "E3.19.2.2", {"start": v(256.39, 38.1) * mm, "end": v(266.7, 38.1) * mm});
            skLineSegment(sketch, "E3.19.2.3", {"start": v(266.7, 38.1) * mm, "end": v(266.7, 48.41) * mm});
            skLineSegment(sketch, "E3.19.3.0", {"start": v(256.39, 50.8) * mm, "end": v(256.39, 61.11) * mm});
            skLineSegment(sketch, "E3.19.3.1", {"start": v(256.39, 61.11) * mm, "end": v(266.7, 61.11) * mm});
            skLineSegment(sketch, "E3.19.3.2", {"start": v(256.39, 50.8) * mm, "end": v(266.7, 50.8) * mm});
            skLineSegment(sketch, "E3.19.3.3", {"start": v(266.7, 50.8) * mm, "end": v(266.7, 61.11) * mm});
            skLineSegment(sketch, "E3.19.4.0", {"start": v(256.39, 63.5) * mm, "end": v(256.39, 73.81) * mm});
            skLineSegment(sketch, "E3.19.4.1", {"start": v(256.39, 73.81) * mm, "end": v(266.7, 73.81) * mm});
            skLineSegment(sketch, "E3.19.4.2", {"start": v(256.39, 63.5) * mm, "end": v(266.7, 63.5) * mm});
            skLineSegment(sketch, "E3.19.4.3", {"start": v(266.7, 63.5) * mm, "end": v(266.7, 73.81) * mm});
            skLineSegment(sketch, "E3.19.5.0", {"start": v(256.39, 76.2) * mm, "end": v(256.39, 86.51) * mm});
            skLineSegment(sketch, "E3.19.5.1", {"start": v(256.39, 86.51) * mm, "end": v(266.7, 86.51) * mm});
            skLineSegment(sketch, "E3.19.5.2", {"start": v(256.39, 76.2) * mm, "end": v(266.7, 76.2) * mm});
            skLineSegment(sketch, "E3.19.5.3", {"start": v(266.7, 76.2) * mm, "end": v(266.7, 86.51) * mm});
            skLineSegment(sketch, "E3.19.6.0", {"start": v(256.39, 88.9) * mm, "end": v(256.39, 99.21) * mm});
            skLineSegment(sketch, "E3.19.6.1", {"start": v(256.39, 99.21) * mm, "end": v(266.7, 99.21) * mm});
            skLineSegment(sketch, "E3.19.6.2", {"start": v(256.39, 88.9) * mm, "end": v(266.7, 88.9) * mm});
            skLineSegment(sketch, "E3.19.6.3", {"start": v(266.7, 88.9) * mm, "end": v(266.7, 99.21) * mm});
            skLineSegment(sketch, "E3.19.7.0", {"start": v(256.39, 101.6) * mm, "end": v(256.39, 111.91) * mm});
            skLineSegment(sketch, "E3.19.7.1", {"start": v(256.39, 111.91) * mm, "end": v(266.7, 111.91) * mm});
            skLineSegment(sketch, "E3.19.7.2", {"start": v(256.39, 101.6) * mm, "end": v(266.7, 101.6) * mm});
            skLineSegment(sketch, "E3.19.7.3", {"start": v(266.7, 101.6) * mm, "end": v(266.7, 111.91) * mm});
            skLineSegment(sketch, "E3.19.8.0", {"start": v(256.39, 114.3) * mm, "end": v(256.39, 124.61) * mm});
            skLineSegment(sketch, "E3.19.8.1", {"start": v(256.39, 124.61) * mm, "end": v(266.7, 124.61) * mm});
            skLineSegment(sketch, "E3.19.8.2", {"start": v(256.39, 114.3) * mm, "end": v(266.7, 114.3) * mm});
            skLineSegment(sketch, "E3.19.8.3", {"start": v(266.7, 114.3) * mm, "end": v(266.7, 124.61) * mm});
            skLineSegment(sketch, "E3.19.9.0", {"start": v(256.39, 127) * mm, "end": v(256.39, 137.31) * mm});
            skLineSegment(sketch, "E3.19.9.1", {"start": v(256.39, 137.31) * mm, "end": v(266.7, 137.31) * mm});
            skLineSegment(sketch, "E3.19.9.2", {"start": v(256.39, 127) * mm, "end": v(266.7, 127) * mm});
            skLineSegment(sketch, "E3.19.9.3", {"start": v(266.7, 127) * mm, "end": v(266.7, 137.31) * mm});
            skLineSegment(sketch, "E3.19.10.0", {"start": v(256.39, 139.7) * mm, "end": v(256.39, 150.01) * mm});
            skLineSegment(sketch, "E3.19.10.1", {"start": v(256.39, 150.01) * mm, "end": v(266.7, 150.01) * mm});
            skLineSegment(sketch, "E3.19.10.2", {"start": v(256.39, 139.7) * mm, "end": v(266.7, 139.7) * mm});
            skLineSegment(sketch, "E3.19.10.3", {"start": v(266.7, 139.7) * mm, "end": v(266.7, 150.01) * mm});
            skLineSegment(sketch, "E3.19.11.0", {"start": v(256.39, 152.4) * mm, "end": v(256.39, 162.71) * mm});
            skLineSegment(sketch, "E3.19.11.1", {"start": v(256.39, 162.71) * mm, "end": v(266.7, 162.71) * mm});
            skLineSegment(sketch, "E3.19.11.2", {"start": v(256.39, 152.4) * mm, "end": v(266.7, 152.4) * mm});
            skLineSegment(sketch, "E3.19.11.3", {"start": v(266.7, 152.4) * mm, "end": v(266.7, 162.71) * mm});
            skLineSegment(sketch, "E3.19.12.0", {"start": v(256.39, 165.1) * mm, "end": v(256.39, 175.41) * mm});
            skLineSegment(sketch, "E3.19.12.1", {"start": v(256.39, 175.41) * mm, "end": v(266.7, 175.41) * mm});
            skLineSegment(sketch, "E3.19.12.2", {"start": v(256.39, 165.1) * mm, "end": v(266.7, 165.1) * mm});
            skLineSegment(sketch, "E3.19.12.3", {"start": v(266.7, 165.1) * mm, "end": v(266.7, 175.41) * mm});
            skLineSegment(sketch, "E3.19.13.0", {"start": v(256.39, 177.8) * mm, "end": v(256.39, 188.11) * mm});
            skLineSegment(sketch, "E3.19.13.1", {"start": v(256.39, 188.11) * mm, "end": v(266.7, 188.11) * mm});
            skLineSegment(sketch, "E3.19.13.2", {"start": v(256.39, 177.8) * mm, "end": v(266.7, 177.8) * mm});
            skLineSegment(sketch, "E3.19.13.3", {"start": v(266.7, 177.8) * mm, "end": v(266.7, 188.11) * mm});
            skLineSegment(sketch, "E3.19.14.0", {"start": v(256.39, 190.5) * mm, "end": v(256.39, 200.81) * mm});
            skLineSegment(sketch, "E3.19.14.1", {"start": v(256.39, 200.81) * mm, "end": v(266.7, 200.81) * mm});
            skLineSegment(sketch, "E3.19.14.2", {"start": v(256.39, 190.5) * mm, "end": v(266.7, 190.5) * mm});
            skLineSegment(sketch, "E3.19.14.3", {"start": v(266.7, 190.5) * mm, "end": v(266.7, 200.81) * mm});
            skLineSegment(sketch, "E3.19.15.0", {"start": v(256.39, 203.2) * mm, "end": v(256.39, 213.51) * mm});
            skLineSegment(sketch, "E3.19.15.1", {"start": v(256.39, 213.51) * mm, "end": v(266.7, 213.51) * mm});
            skLineSegment(sketch, "E3.19.15.2", {"start": v(256.39, 203.2) * mm, "end": v(266.7, 203.2) * mm});
            skLineSegment(sketch, "E3.19.15.3", {"start": v(266.7, 203.2) * mm, "end": v(266.7, 213.51) * mm});
            skLineSegment(sketch, "E3.19.16.0", {"start": v(256.39, 215.9) * mm, "end": v(256.39, 226.21) * mm});
            skLineSegment(sketch, "E3.19.16.1", {"start": v(256.39, 226.21) * mm, "end": v(266.7, 226.21) * mm});
            skLineSegment(sketch, "E3.19.16.2", {"start": v(256.39, 215.9) * mm, "end": v(266.7, 215.9) * mm});
            skLineSegment(sketch, "E3.19.16.3", {"start": v(266.7, 215.9) * mm, "end": v(266.7, 226.21) * mm});
            skLineSegment(sketch, "E3.19.17.0", {"start": v(256.39, 228.6) * mm, "end": v(256.39, 238.91) * mm});
            skLineSegment(sketch, "E3.19.17.1", {"start": v(256.39, 238.91) * mm, "end": v(266.7, 238.91) * mm});
            skLineSegment(sketch, "E3.19.17.2", {"start": v(256.39, 228.6) * mm, "end": v(266.7, 228.6) * mm});
            skLineSegment(sketch, "E3.19.17.3", {"start": v(266.7, 228.6) * mm, "end": v(266.7, 238.91) * mm});
            skLineSegment(sketch, "E3.19.18.0", {"start": v(256.39, 241.3) * mm, "end": v(256.39, 251.61) * mm});
            skLineSegment(sketch, "E3.19.18.1", {"start": v(256.39, 251.61) * mm, "end": v(266.7, 251.61) * mm});
            skLineSegment(sketch, "E3.19.18.2", {"start": v(256.39, 241.3) * mm, "end": v(266.7, 241.3) * mm});
            skLineSegment(sketch, "E3.19.18.3", {"start": v(266.7, 241.3) * mm, "end": v(266.7, 251.61) * mm});
            skLineSegment(sketch, "E3.19.19.0", {"start": v(256.39, 254) * mm, "end": v(256.39, 264.31) * mm});
            skLineSegment(sketch, "E3.19.19.1", {"start": v(256.39, 264.31) * mm, "end": v(266.7, 264.31) * mm});
            skLineSegment(sketch, "E3.19.19.2", {"start": v(256.39, 254) * mm, "end": v(266.7, 254) * mm});
            skLineSegment(sketch, "E3.19.19.3", {"start": v(266.7, 254) * mm, "end": v(266.7, 264.31) * mm});
            skLineSegment(sketch, "E3.19.20.0", {"start": v(256.39, 266.7) * mm, "end": v(256.39, 277.01) * mm});
            skLineSegment(sketch, "E3.19.20.1", {"start": v(256.39, 277.01) * mm, "end": v(266.7, 277.01) * mm});
            skLineSegment(sketch, "E3.19.20.2", {"start": v(256.39, 266.7) * mm, "end": v(266.7, 266.7) * mm});
            skLineSegment(sketch, "E3.19.20.3", {"start": v(266.7, 266.7) * mm, "end": v(266.7, 277.01) * mm});
            skLineSegment(sketch, "E3.19.21.0", {"start": v(256.39, 279.4) * mm, "end": v(256.39, 289.71) * mm});
            skLineSegment(sketch, "E3.19.21.1", {"start": v(256.39, 289.71) * mm, "end": v(266.7, 289.71) * mm});
            skLineSegment(sketch, "E3.19.21.2", {"start": v(256.39, 279.4) * mm, "end": v(266.7, 279.4) * mm});
            skLineSegment(sketch, "E3.19.21.3", {"start": v(266.7, 279.4) * mm, "end": v(266.7, 289.71) * mm});
            skLineSegment(sketch, "E3.20.0.0", {"start": v(269.09, 12.7) * mm, "end": v(269.09, 23.01) * mm});
            skLineSegment(sketch, "E3.20.0.1", {"start": v(269.09, 23.01) * mm, "end": v(279.4, 23.01) * mm});
            skLineSegment(sketch, "E3.20.0.2", {"start": v(269.09, 12.7) * mm, "end": v(279.4, 12.7) * mm});
            skLineSegment(sketch, "E3.20.0.3", {"start": v(279.4, 12.7) * mm, "end": v(279.4, 23.01) * mm});
            skLineSegment(sketch, "E3.20.1.0", {"start": v(269.09, 25.4) * mm, "end": v(269.09, 35.71) * mm});
            skLineSegment(sketch, "E3.20.1.1", {"start": v(269.09, 35.71) * mm, "end": v(279.4, 35.71) * mm});
            skLineSegment(sketch, "E3.20.1.2", {"start": v(269.09, 25.4) * mm, "end": v(279.4, 25.4) * mm});
            skLineSegment(sketch, "E3.20.1.3", {"start": v(279.4, 25.4) * mm, "end": v(279.4, 35.71) * mm});
            skLineSegment(sketch, "E3.20.2.0", {"start": v(269.09, 38.1) * mm, "end": v(269.09, 48.41) * mm});
            skLineSegment(sketch, "E3.20.2.1", {"start": v(269.09, 48.41) * mm, "end": v(279.4, 48.41) * mm});
            skLineSegment(sketch, "E3.20.2.2", {"start": v(269.09, 38.1) * mm, "end": v(279.4, 38.1) * mm});
            skLineSegment(sketch, "E3.20.2.3", {"start": v(279.4, 38.1) * mm, "end": v(279.4, 48.41) * mm});
            skLineSegment(sketch, "E3.20.3.0", {"start": v(269.09, 50.8) * mm, "end": v(269.09, 61.11) * mm});
            skLineSegment(sketch, "E3.20.3.1", {"start": v(269.09, 61.11) * mm, "end": v(279.4, 61.11) * mm});
            skLineSegment(sketch, "E3.20.3.2", {"start": v(269.09, 50.8) * mm, "end": v(279.4, 50.8) * mm});
            skLineSegment(sketch, "E3.20.3.3", {"start": v(279.4, 50.8) * mm, "end": v(279.4, 61.11) * mm});
            skLineSegment(sketch, "E3.20.4.0", {"start": v(269.09, 63.5) * mm, "end": v(269.09, 73.81) * mm});
            skLineSegment(sketch, "E3.20.4.1", {"start": v(269.09, 73.81) * mm, "end": v(279.4, 73.81) * mm});
            skLineSegment(sketch, "E3.20.4.2", {"start": v(269.09, 63.5) * mm, "end": v(279.4, 63.5) * mm});
            skLineSegment(sketch, "E3.20.4.3", {"start": v(279.4, 63.5) * mm, "end": v(279.4, 73.81) * mm});
            skLineSegment(sketch, "E3.20.5.0", {"start": v(269.09, 76.2) * mm, "end": v(269.09, 86.51) * mm});
            skLineSegment(sketch, "E3.20.5.1", {"start": v(269.09, 86.51) * mm, "end": v(279.4, 86.51) * mm});
            skLineSegment(sketch, "E3.20.5.2", {"start": v(269.09, 76.2) * mm, "end": v(279.4, 76.2) * mm});
            skLineSegment(sketch, "E3.20.5.3", {"start": v(279.4, 76.2) * mm, "end": v(279.4, 86.51) * mm});
            skLineSegment(sketch, "E3.20.6.0", {"start": v(269.09, 88.9) * mm, "end": v(269.09, 99.21) * mm});
            skLineSegment(sketch, "E3.20.6.1", {"start": v(269.09, 99.21) * mm, "end": v(279.4, 99.21) * mm});
            skLineSegment(sketch, "E3.20.6.2", {"start": v(269.09, 88.9) * mm, "end": v(279.4, 88.9) * mm});
            skLineSegment(sketch, "E3.20.6.3", {"start": v(279.4, 88.9) * mm, "end": v(279.4, 99.21) * mm});
            skLineSegment(sketch, "E3.20.7.0", {"start": v(269.09, 101.6) * mm, "end": v(269.09, 111.91) * mm});
            skLineSegment(sketch, "E3.20.7.1", {"start": v(269.09, 111.91) * mm, "end": v(279.4, 111.91) * mm});
            skLineSegment(sketch, "E3.20.7.2", {"start": v(269.09, 101.6) * mm, "end": v(279.4, 101.6) * mm});
            skLineSegment(sketch, "E3.20.7.3", {"start": v(279.4, 101.6) * mm, "end": v(279.4, 111.91) * mm});
            skLineSegment(sketch, "E3.20.8.0", {"start": v(269.09, 114.3) * mm, "end": v(269.09, 124.61) * mm});
            skLineSegment(sketch, "E3.20.8.1", {"start": v(269.09, 124.61) * mm, "end": v(279.4, 124.61) * mm});
            skLineSegment(sketch, "E3.20.8.2", {"start": v(269.09, 114.3) * mm, "end": v(279.4, 114.3) * mm});
            skLineSegment(sketch, "E3.20.8.3", {"start": v(279.4, 114.3) * mm, "end": v(279.4, 124.61) * mm});
            skLineSegment(sketch, "E3.20.9.0", {"start": v(269.09, 127) * mm, "end": v(269.09, 137.31) * mm});
            skLineSegment(sketch, "E3.20.9.1", {"start": v(269.09, 137.31) * mm, "end": v(279.4, 137.31) * mm});
            skLineSegment(sketch, "E3.20.9.2", {"start": v(269.09, 127) * mm, "end": v(279.4, 127) * mm});
            skLineSegment(sketch, "E3.20.9.3", {"start": v(279.4, 127) * mm, "end": v(279.4, 137.31) * mm});
            skLineSegment(sketch, "E3.20.10.0", {"start": v(269.09, 139.7) * mm, "end": v(269.09, 150.01) * mm});
            skLineSegment(sketch, "E3.20.10.1", {"start": v(269.09, 150.01) * mm, "end": v(279.4, 150.01) * mm});
            skLineSegment(sketch, "E3.20.10.2", {"start": v(269.09, 139.7) * mm, "end": v(279.4, 139.7) * mm});
            skLineSegment(sketch, "E3.20.10.3", {"start": v(279.4, 139.7) * mm, "end": v(279.4, 150.01) * mm});
            skLineSegment(sketch, "E3.20.11.0", {"start": v(269.09, 152.4) * mm, "end": v(269.09, 162.71) * mm});
            skLineSegment(sketch, "E3.20.11.1", {"start": v(269.09, 162.71) * mm, "end": v(279.4, 162.71) * mm});
            skLineSegment(sketch, "E3.20.11.2", {"start": v(269.09, 152.4) * mm, "end": v(279.4, 152.4) * mm});
            skLineSegment(sketch, "E3.20.11.3", {"start": v(279.4, 152.4) * mm, "end": v(279.4, 162.71) * mm});
            skLineSegment(sketch, "E3.20.12.0", {"start": v(269.09, 165.1) * mm, "end": v(269.09, 175.41) * mm});
            skLineSegment(sketch, "E3.20.12.1", {"start": v(269.09, 175.41) * mm, "end": v(279.4, 175.41) * mm});
            skLineSegment(sketch, "E3.20.12.2", {"start": v(269.09, 165.1) * mm, "end": v(279.4, 165.1) * mm});
            skLineSegment(sketch, "E3.20.12.3", {"start": v(279.4, 165.1) * mm, "end": v(279.4, 175.41) * mm});
            skLineSegment(sketch, "E3.20.13.0", {"start": v(269.09, 177.8) * mm, "end": v(269.09, 188.11) * mm});
            skLineSegment(sketch, "E3.20.13.1", {"start": v(269.09, 188.11) * mm, "end": v(279.4, 188.11) * mm});
            skLineSegment(sketch, "E3.20.13.2", {"start": v(269.09, 177.8) * mm, "end": v(279.4, 177.8) * mm});
            skLineSegment(sketch, "E3.20.13.3", {"start": v(279.4, 177.8) * mm, "end": v(279.4, 188.11) * mm});
            skLineSegment(sketch, "E3.20.14.0", {"start": v(269.09, 190.5) * mm, "end": v(269.09, 200.81) * mm});
            skLineSegment(sketch, "E3.20.14.1", {"start": v(269.09, 200.81) * mm, "end": v(279.4, 200.81) * mm});
            skLineSegment(sketch, "E3.20.14.2", {"start": v(269.09, 190.5) * mm, "end": v(279.4, 190.5) * mm});
            skLineSegment(sketch, "E3.20.14.3", {"start": v(279.4, 190.5) * mm, "end": v(279.4, 200.81) * mm});
            skLineSegment(sketch, "E3.20.15.0", {"start": v(269.09, 203.2) * mm, "end": v(269.09, 213.51) * mm});
            skLineSegment(sketch, "E3.20.15.1", {"start": v(269.09, 213.51) * mm, "end": v(279.4, 213.51) * mm});
            skLineSegment(sketch, "E3.20.15.2", {"start": v(269.09, 203.2) * mm, "end": v(279.4, 203.2) * mm});
            skLineSegment(sketch, "E3.20.15.3", {"start": v(279.4, 203.2) * mm, "end": v(279.4, 213.51) * mm});
            skLineSegment(sketch, "E3.20.16.0", {"start": v(269.09, 215.9) * mm, "end": v(269.09, 226.21) * mm});
            skLineSegment(sketch, "E3.20.16.1", {"start": v(269.09, 226.21) * mm, "end": v(279.4, 226.21) * mm});
            skLineSegment(sketch, "E3.20.16.2", {"start": v(269.09, 215.9) * mm, "end": v(279.4, 215.9) * mm});
            skLineSegment(sketch, "E3.20.16.3", {"start": v(279.4, 215.9) * mm, "end": v(279.4, 226.21) * mm});
            skLineSegment(sketch, "E3.20.17.0", {"start": v(269.09, 228.6) * mm, "end": v(269.09, 238.91) * mm});
            skLineSegment(sketch, "E3.20.17.1", {"start": v(269.09, 238.91) * mm, "end": v(279.4, 238.91) * mm});
            skLineSegment(sketch, "E3.20.17.2", {"start": v(269.09, 228.6) * mm, "end": v(279.4, 228.6) * mm});
            skLineSegment(sketch, "E3.20.17.3", {"start": v(279.4, 228.6) * mm, "end": v(279.4, 238.91) * mm});
            skLineSegment(sketch, "E3.20.18.0", {"start": v(269.09, 241.3) * mm, "end": v(269.09, 251.61) * mm});
            skLineSegment(sketch, "E3.20.18.1", {"start": v(269.09, 251.61) * mm, "end": v(279.4, 251.61) * mm});
            skLineSegment(sketch, "E3.20.18.2", {"start": v(269.09, 241.3) * mm, "end": v(279.4, 241.3) * mm});
            skLineSegment(sketch, "E3.20.18.3", {"start": v(279.4, 241.3) * mm, "end": v(279.4, 251.61) * mm});
            skLineSegment(sketch, "E3.20.19.0", {"start": v(269.09, 254) * mm, "end": v(269.09, 264.31) * mm});
            skLineSegment(sketch, "E3.20.19.1", {"start": v(269.09, 264.31) * mm, "end": v(279.4, 264.31) * mm});
            skLineSegment(sketch, "E3.20.19.2", {"start": v(269.09, 254) * mm, "end": v(279.4, 254) * mm});
            skLineSegment(sketch, "E3.20.19.3", {"start": v(279.4, 254) * mm, "end": v(279.4, 264.31) * mm});
            skLineSegment(sketch, "E3.20.20.0", {"start": v(269.09, 266.7) * mm, "end": v(269.09, 277.01) * mm});
            skLineSegment(sketch, "E3.20.20.1", {"start": v(269.09, 277.01) * mm, "end": v(279.4, 277.01) * mm});
            skLineSegment(sketch, "E3.20.20.2", {"start": v(269.09, 266.7) * mm, "end": v(279.4, 266.7) * mm});
            skLineSegment(sketch, "E3.20.20.3", {"start": v(279.4, 266.7) * mm, "end": v(279.4, 277.01) * mm});
            skLineSegment(sketch, "E3.20.21.0", {"start": v(269.09, 279.4) * mm, "end": v(269.09, 289.71) * mm});
            skLineSegment(sketch, "E3.20.21.1", {"start": v(269.09, 289.71) * mm, "end": v(279.4, 289.71) * mm});
            skLineSegment(sketch, "E3.20.21.2", {"start": v(269.09, 279.4) * mm, "end": v(279.4, 279.4) * mm});
            skLineSegment(sketch, "E3.20.21.3", {"start": v(279.4, 279.4) * mm, "end": v(279.4, 289.71) * mm});
            skLineSegment(sketch, "E3.21.0.0", {"start": v(281.79, 12.7) * mm, "end": v(281.79, 23.01) * mm});
            skLineSegment(sketch, "E3.21.0.1", {"start": v(281.79, 23.01) * mm, "end": v(292.1, 23.01) * mm});
            skLineSegment(sketch, "E3.21.0.2", {"start": v(281.79, 12.7) * mm, "end": v(292.1, 12.7) * mm});
            skLineSegment(sketch, "E3.21.0.3", {"start": v(292.1, 12.7) * mm, "end": v(292.1, 23.01) * mm});
            skLineSegment(sketch, "E3.21.1.0", {"start": v(281.79, 25.4) * mm, "end": v(281.79, 35.71) * mm});
            skLineSegment(sketch, "E3.21.1.1", {"start": v(281.79, 35.71) * mm, "end": v(292.1, 35.71) * mm});
            skLineSegment(sketch, "E3.21.1.2", {"start": v(281.79, 25.4) * mm, "end": v(292.1, 25.4) * mm});
            skLineSegment(sketch, "E3.21.1.3", {"start": v(292.1, 25.4) * mm, "end": v(292.1, 35.71) * mm});
            skLineSegment(sketch, "E3.21.2.0", {"start": v(281.79, 38.1) * mm, "end": v(281.79, 48.41) * mm});
            skLineSegment(sketch, "E3.21.2.1", {"start": v(281.79, 48.41) * mm, "end": v(292.1, 48.41) * mm});
            skLineSegment(sketch, "E3.21.2.2", {"start": v(281.79, 38.1) * mm, "end": v(292.1, 38.1) * mm});
            skLineSegment(sketch, "E3.21.2.3", {"start": v(292.1, 38.1) * mm, "end": v(292.1, 48.41) * mm});
            skLineSegment(sketch, "E3.21.3.0", {"start": v(281.79, 50.8) * mm, "end": v(281.79, 61.11) * mm});
            skLineSegment(sketch, "E3.21.3.1", {"start": v(281.79, 61.11) * mm, "end": v(292.1, 61.11) * mm});
            skLineSegment(sketch, "E3.21.3.2", {"start": v(281.79, 50.8) * mm, "end": v(292.1, 50.8) * mm});
            skLineSegment(sketch, "E3.21.3.3", {"start": v(292.1, 50.8) * mm, "end": v(292.1, 61.11) * mm});
            skLineSegment(sketch, "E3.21.4.0", {"start": v(281.79, 63.5) * mm, "end": v(281.79, 73.81) * mm});
            skLineSegment(sketch, "E3.21.4.1", {"start": v(281.79, 73.81) * mm, "end": v(292.1, 73.81) * mm});
            skLineSegment(sketch, "E3.21.4.2", {"start": v(281.79, 63.5) * mm, "end": v(292.1, 63.5) * mm});
            skLineSegment(sketch, "E3.21.4.3", {"start": v(292.1, 63.5) * mm, "end": v(292.1, 73.81) * mm});
            skLineSegment(sketch, "E3.21.5.0", {"start": v(281.79, 76.2) * mm, "end": v(281.79, 86.51) * mm});
            skLineSegment(sketch, "E3.21.5.1", {"start": v(281.79, 86.51) * mm, "end": v(292.1, 86.51) * mm});
            skLineSegment(sketch, "E3.21.5.2", {"start": v(281.79, 76.2) * mm, "end": v(292.1, 76.2) * mm});
            skLineSegment(sketch, "E3.21.5.3", {"start": v(292.1, 76.2) * mm, "end": v(292.1, 86.51) * mm});
            skLineSegment(sketch, "E3.21.6.0", {"start": v(281.79, 88.9) * mm, "end": v(281.79, 99.21) * mm});
            skLineSegment(sketch, "E3.21.6.1", {"start": v(281.79, 99.21) * mm, "end": v(292.1, 99.21) * mm});
            skLineSegment(sketch, "E3.21.6.2", {"start": v(281.79, 88.9) * mm, "end": v(292.1, 88.9) * mm});
            skLineSegment(sketch, "E3.21.6.3", {"start": v(292.1, 88.9) * mm, "end": v(292.1, 99.21) * mm});
            skLineSegment(sketch, "E3.21.7.0", {"start": v(281.79, 101.6) * mm, "end": v(281.79, 111.91) * mm});
            skLineSegment(sketch, "E3.21.7.1", {"start": v(281.79, 111.91) * mm, "end": v(292.1, 111.91) * mm});
            skLineSegment(sketch, "E3.21.7.2", {"start": v(281.79, 101.6) * mm, "end": v(292.1, 101.6) * mm});
            skLineSegment(sketch, "E3.21.7.3", {"start": v(292.1, 101.6) * mm, "end": v(292.1, 111.91) * mm});
            skLineSegment(sketch, "E3.21.8.0", {"start": v(281.79, 114.3) * mm, "end": v(281.79, 124.61) * mm});
            skLineSegment(sketch, "E3.21.8.1", {"start": v(281.79, 124.61) * mm, "end": v(292.1, 124.61) * mm});
            skLineSegment(sketch, "E3.21.8.2", {"start": v(281.79, 114.3) * mm, "end": v(292.1, 114.3) * mm});
            skLineSegment(sketch, "E3.21.8.3", {"start": v(292.1, 114.3) * mm, "end": v(292.1, 124.61) * mm});
            skLineSegment(sketch, "E3.21.9.0", {"start": v(281.79, 127) * mm, "end": v(281.79, 137.31) * mm});
            skLineSegment(sketch, "E3.21.9.1", {"start": v(281.79, 137.31) * mm, "end": v(292.1, 137.31) * mm});
            skLineSegment(sketch, "E3.21.9.2", {"start": v(281.79, 127) * mm, "end": v(292.1, 127) * mm});
            skLineSegment(sketch, "E3.21.9.3", {"start": v(292.1, 127) * mm, "end": v(292.1, 137.31) * mm});
            skLineSegment(sketch, "E3.21.10.0", {"start": v(281.79, 139.7) * mm, "end": v(281.79, 150.01) * mm});
            skLineSegment(sketch, "E3.21.10.1", {"start": v(281.79, 150.01) * mm, "end": v(292.1, 150.01) * mm});
            skLineSegment(sketch, "E3.21.10.2", {"start": v(281.79, 139.7) * mm, "end": v(292.1, 139.7) * mm});
            skLineSegment(sketch, "E3.21.10.3", {"start": v(292.1, 139.7) * mm, "end": v(292.1, 150.01) * mm});
            skLineSegment(sketch, "E3.21.11.0", {"start": v(281.79, 152.4) * mm, "end": v(281.79, 162.71) * mm});
            skLineSegment(sketch, "E3.21.11.1", {"start": v(281.79, 162.71) * mm, "end": v(292.1, 162.71) * mm});
            skLineSegment(sketch, "E3.21.11.2", {"start": v(281.79, 152.4) * mm, "end": v(292.1, 152.4) * mm});
            skLineSegment(sketch, "E3.21.11.3", {"start": v(292.1, 152.4) * mm, "end": v(292.1, 162.71) * mm});
            skLineSegment(sketch, "E3.21.12.0", {"start": v(281.79, 165.1) * mm, "end": v(281.79, 175.41) * mm});
            skLineSegment(sketch, "E3.21.12.1", {"start": v(281.79, 175.41) * mm, "end": v(292.1, 175.41) * mm});
            skLineSegment(sketch, "E3.21.12.2", {"start": v(281.79, 165.1) * mm, "end": v(292.1, 165.1) * mm});
            skLineSegment(sketch, "E3.21.12.3", {"start": v(292.1, 165.1) * mm, "end": v(292.1, 175.41) * mm});
            skLineSegment(sketch, "E3.21.13.0", {"start": v(281.79, 177.8) * mm, "end": v(281.79, 188.11) * mm});
            skLineSegment(sketch, "E3.21.13.1", {"start": v(281.79, 188.11) * mm, "end": v(292.1, 188.11) * mm});
            skLineSegment(sketch, "E3.21.13.2", {"start": v(281.79, 177.8) * mm, "end": v(292.1, 177.8) * mm});
            skLineSegment(sketch, "E3.21.13.3", {"start": v(292.1, 177.8) * mm, "end": v(292.1, 188.11) * mm});
            skLineSegment(sketch, "E3.21.14.0", {"start": v(281.79, 190.5) * mm, "end": v(281.79, 200.81) * mm});
            skLineSegment(sketch, "E3.21.14.1", {"start": v(281.79, 200.81) * mm, "end": v(292.1, 200.81) * mm});
            skLineSegment(sketch, "E3.21.14.2", {"start": v(281.79, 190.5) * mm, "end": v(292.1, 190.5) * mm});
            skLineSegment(sketch, "E3.21.14.3", {"start": v(292.1, 190.5) * mm, "end": v(292.1, 200.81) * mm});
            skLineSegment(sketch, "E3.21.15.0", {"start": v(281.79, 203.2) * mm, "end": v(281.79, 213.51) * mm});
            skLineSegment(sketch, "E3.21.15.1", {"start": v(281.79, 213.51) * mm, "end": v(292.1, 213.51) * mm});
            skLineSegment(sketch, "E3.21.15.2", {"start": v(281.79, 203.2) * mm, "end": v(292.1, 203.2) * mm});
            skLineSegment(sketch, "E3.21.15.3", {"start": v(292.1, 203.2) * mm, "end": v(292.1, 213.51) * mm});
            skLineSegment(sketch, "E3.21.16.0", {"start": v(281.79, 215.9) * mm, "end": v(281.79, 226.21) * mm});
            skLineSegment(sketch, "E3.21.16.1", {"start": v(281.79, 226.21) * mm, "end": v(292.1, 226.21) * mm});
            skLineSegment(sketch, "E3.21.16.2", {"start": v(281.79, 215.9) * mm, "end": v(292.1, 215.9) * mm});
            skLineSegment(sketch, "E3.21.16.3", {"start": v(292.1, 215.9) * mm, "end": v(292.1, 226.21) * mm});
            skLineSegment(sketch, "E3.21.17.0", {"start": v(281.79, 228.6) * mm, "end": v(281.79, 238.91) * mm});
            skLineSegment(sketch, "E3.21.17.1", {"start": v(281.79, 238.91) * mm, "end": v(292.1, 238.91) * mm});
            skLineSegment(sketch, "E3.21.17.2", {"start": v(281.79, 228.6) * mm, "end": v(292.1, 228.6) * mm});
            skLineSegment(sketch, "E3.21.17.3", {"start": v(292.1, 228.6) * mm, "end": v(292.1, 238.91) * mm});
            skLineSegment(sketch, "E3.21.18.0", {"start": v(281.79, 241.3) * mm, "end": v(281.79, 251.61) * mm});
            skLineSegment(sketch, "E3.21.18.1", {"start": v(281.79, 251.61) * mm, "end": v(292.1, 251.61) * mm});
            skLineSegment(sketch, "E3.21.18.2", {"start": v(281.79, 241.3) * mm, "end": v(292.1, 241.3) * mm});
            skLineSegment(sketch, "E3.21.18.3", {"start": v(292.1, 241.3) * mm, "end": v(292.1, 251.61) * mm});
            skLineSegment(sketch, "E3.21.19.0", {"start": v(281.79, 254) * mm, "end": v(281.79, 264.31) * mm});
            skLineSegment(sketch, "E3.21.19.1", {"start": v(281.79, 264.31) * mm, "end": v(292.1, 264.31) * mm});
            skLineSegment(sketch, "E3.21.19.2", {"start": v(281.79, 254) * mm, "end": v(292.1, 254) * mm});
            skLineSegment(sketch, "E3.21.19.3", {"start": v(292.1, 254) * mm, "end": v(292.1, 264.31) * mm});
            skLineSegment(sketch, "E3.21.20.0", {"start": v(281.79, 266.7) * mm, "end": v(281.79, 277.01) * mm});
            skLineSegment(sketch, "E3.21.20.1", {"start": v(281.79, 277.01) * mm, "end": v(292.1, 277.01) * mm});
            skLineSegment(sketch, "E3.21.20.2", {"start": v(281.79, 266.7) * mm, "end": v(292.1, 266.7) * mm});
            skLineSegment(sketch, "E3.21.20.3", {"start": v(292.1, 266.7) * mm, "end": v(292.1, 277.01) * mm});
            skLineSegment(sketch, "E3.21.21.0", {"start": v(281.79, 279.4) * mm, "end": v(281.79, 289.71) * mm});
            skLineSegment(sketch, "E3.21.21.1", {"start": v(281.79, 289.71) * mm, "end": v(292.1, 289.71) * mm});
            skLineSegment(sketch, "E3.21.21.2", {"start": v(281.79, 279.4) * mm, "end": v(292.1, 279.4) * mm});
            skLineSegment(sketch, "E3.21.21.3", {"start": v(292.1, 279.4) * mm, "end": v(292.1, 289.71) * mm});
            skLineSegment(sketch, "E3.22.0.0", {"start": v(294.49, 12.7) * mm, "end": v(294.49, 23.01) * mm});
            skLineSegment(sketch, "E3.22.0.1", {"start": v(294.49, 23.01) * mm, "end": v(304.8, 23.01) * mm});
            skLineSegment(sketch, "E3.22.0.2", {"start": v(294.49, 12.7) * mm, "end": v(304.8, 12.7) * mm});
            skLineSegment(sketch, "E3.22.0.3", {"start": v(304.8, 12.7) * mm, "end": v(304.8, 23.01) * mm});
            skLineSegment(sketch, "E3.22.1.0", {"start": v(294.49, 25.4) * mm, "end": v(294.49, 35.71) * mm});
            skLineSegment(sketch, "E3.22.1.1", {"start": v(294.49, 35.71) * mm, "end": v(304.8, 35.71) * mm});
            skLineSegment(sketch, "E3.22.1.2", {"start": v(294.49, 25.4) * mm, "end": v(304.8, 25.4) * mm});
            skLineSegment(sketch, "E3.22.1.3", {"start": v(304.8, 25.4) * mm, "end": v(304.8, 35.71) * mm});
            skLineSegment(sketch, "E3.22.2.0", {"start": v(294.49, 38.1) * mm, "end": v(294.49, 48.41) * mm});
            skLineSegment(sketch, "E3.22.2.1", {"start": v(294.49, 48.41) * mm, "end": v(304.8, 48.41) * mm});
            skLineSegment(sketch, "E3.22.2.2", {"start": v(294.49, 38.1) * mm, "end": v(304.8, 38.1) * mm});
            skLineSegment(sketch, "E3.22.2.3", {"start": v(304.8, 38.1) * mm, "end": v(304.8, 48.41) * mm});
            skLineSegment(sketch, "E3.22.3.0", {"start": v(294.49, 50.8) * mm, "end": v(294.49, 61.11) * mm});
            skLineSegment(sketch, "E3.22.3.1", {"start": v(294.49, 61.11) * mm, "end": v(304.8, 61.11) * mm});
            skLineSegment(sketch, "E3.22.3.2", {"start": v(294.49, 50.8) * mm, "end": v(304.8, 50.8) * mm});
            skLineSegment(sketch, "E3.22.3.3", {"start": v(304.8, 50.8) * mm, "end": v(304.8, 61.11) * mm});
            skLineSegment(sketch, "E3.22.4.0", {"start": v(294.49, 63.5) * mm, "end": v(294.49, 73.81) * mm});
            skLineSegment(sketch, "E3.22.4.1", {"start": v(294.49, 73.81) * mm, "end": v(304.8, 73.81) * mm});
            skLineSegment(sketch, "E3.22.4.2", {"start": v(294.49, 63.5) * mm, "end": v(304.8, 63.5) * mm});
            skLineSegment(sketch, "E3.22.4.3", {"start": v(304.8, 63.5) * mm, "end": v(304.8, 73.81) * mm});
            skLineSegment(sketch, "E3.22.5.0", {"start": v(294.49, 76.2) * mm, "end": v(294.49, 86.51) * mm});
            skLineSegment(sketch, "E3.22.5.1", {"start": v(294.49, 86.51) * mm, "end": v(304.8, 86.51) * mm});
            skLineSegment(sketch, "E3.22.5.2", {"start": v(294.49, 76.2) * mm, "end": v(304.8, 76.2) * mm});
            skLineSegment(sketch, "E3.22.5.3", {"start": v(304.8, 76.2) * mm, "end": v(304.8, 86.51) * mm});
            skLineSegment(sketch, "E3.22.6.0", {"start": v(294.49, 88.9) * mm, "end": v(294.49, 99.21) * mm});
            skLineSegment(sketch, "E3.22.6.1", {"start": v(294.49, 99.21) * mm, "end": v(304.8, 99.21) * mm});
            skLineSegment(sketch, "E3.22.6.2", {"start": v(294.49, 88.9) * mm, "end": v(304.8, 88.9) * mm});
            skLineSegment(sketch, "E3.22.6.3", {"start": v(304.8, 88.9) * mm, "end": v(304.8, 99.21) * mm});
            skLineSegment(sketch, "E3.22.7.0", {"start": v(294.49, 101.6) * mm, "end": v(294.49, 111.91) * mm});
            skLineSegment(sketch, "E3.22.7.1", {"start": v(294.49, 111.91) * mm, "end": v(304.8, 111.91) * mm});
            skLineSegment(sketch, "E3.22.7.2", {"start": v(294.49, 101.6) * mm, "end": v(304.8, 101.6) * mm});
            skLineSegment(sketch, "E3.22.7.3", {"start": v(304.8, 101.6) * mm, "end": v(304.8, 111.91) * mm});
            skLineSegment(sketch, "E3.22.8.0", {"start": v(294.49, 114.3) * mm, "end": v(294.49, 124.61) * mm});
            skLineSegment(sketch, "E3.22.8.1", {"start": v(294.49, 124.61) * mm, "end": v(304.8, 124.61) * mm});
            skLineSegment(sketch, "E3.22.8.2", {"start": v(294.49, 114.3) * mm, "end": v(304.8, 114.3) * mm});
            skLineSegment(sketch, "E3.22.8.3", {"start": v(304.8, 114.3) * mm, "end": v(304.8, 124.61) * mm});
            skLineSegment(sketch, "E3.22.9.0", {"start": v(294.49, 127) * mm, "end": v(294.49, 137.31) * mm});
            skLineSegment(sketch, "E3.22.9.1", {"start": v(294.49, 137.31) * mm, "end": v(304.8, 137.31) * mm});
            skLineSegment(sketch, "E3.22.9.2", {"start": v(294.49, 127) * mm, "end": v(304.8, 127) * mm});
            skLineSegment(sketch, "E3.22.9.3", {"start": v(304.8, 127) * mm, "end": v(304.8, 137.31) * mm});
            skLineSegment(sketch, "E3.22.10.0", {"start": v(294.49, 139.7) * mm, "end": v(294.49, 150.01) * mm});
            skLineSegment(sketch, "E3.22.10.1", {"start": v(294.49, 150.01) * mm, "end": v(304.8, 150.01) * mm});
            skLineSegment(sketch, "E3.22.10.2", {"start": v(294.49, 139.7) * mm, "end": v(304.8, 139.7) * mm});
            skLineSegment(sketch, "E3.22.10.3", {"start": v(304.8, 139.7) * mm, "end": v(304.8, 150.01) * mm});
            skLineSegment(sketch, "E3.22.11.0", {"start": v(294.49, 152.4) * mm, "end": v(294.49, 162.71) * mm});
            skLineSegment(sketch, "E3.22.11.1", {"start": v(294.49, 162.71) * mm, "end": v(304.8, 162.71) * mm});
            skLineSegment(sketch, "E3.22.11.2", {"start": v(294.49, 152.4) * mm, "end": v(304.8, 152.4) * mm});
            skLineSegment(sketch, "E3.22.11.3", {"start": v(304.8, 152.4) * mm, "end": v(304.8, 162.71) * mm});
            skLineSegment(sketch, "E3.22.12.0", {"start": v(294.49, 165.1) * mm, "end": v(294.49, 175.41) * mm});
            skLineSegment(sketch, "E3.22.12.1", {"start": v(294.49, 175.41) * mm, "end": v(304.8, 175.41) * mm});
            skLineSegment(sketch, "E3.22.12.2", {"start": v(294.49, 165.1) * mm, "end": v(304.8, 165.1) * mm});
            skLineSegment(sketch, "E3.22.12.3", {"start": v(304.8, 165.1) * mm, "end": v(304.8, 175.41) * mm});
            skLineSegment(sketch, "E3.22.13.0", {"start": v(294.49, 177.8) * mm, "end": v(294.49, 188.11) * mm});
            skLineSegment(sketch, "E3.22.13.1", {"start": v(294.49, 188.11) * mm, "end": v(304.8, 188.11) * mm});
            skLineSegment(sketch, "E3.22.13.2", {"start": v(294.49, 177.8) * mm, "end": v(304.8, 177.8) * mm});
            skLineSegment(sketch, "E3.22.13.3", {"start": v(304.8, 177.8) * mm, "end": v(304.8, 188.11) * mm});
            skLineSegment(sketch, "E3.22.14.0", {"start": v(294.49, 190.5) * mm, "end": v(294.49, 200.81) * mm});
            skLineSegment(sketch, "E3.22.14.1", {"start": v(294.49, 200.81) * mm, "end": v(304.8, 200.81) * mm});
            skLineSegment(sketch, "E3.22.14.2", {"start": v(294.49, 190.5) * mm, "end": v(304.8, 190.5) * mm});
            skLineSegment(sketch, "E3.22.14.3", {"start": v(304.8, 190.5) * mm, "end": v(304.8, 200.81) * mm});
            skLineSegment(sketch, "E3.22.15.0", {"start": v(294.49, 203.2) * mm, "end": v(294.49, 213.51) * mm});
            skLineSegment(sketch, "E3.22.15.1", {"start": v(294.49, 213.51) * mm, "end": v(304.8, 213.51) * mm});
            skLineSegment(sketch, "E3.22.15.2", {"start": v(294.49, 203.2) * mm, "end": v(304.8, 203.2) * mm});
            skLineSegment(sketch, "E3.22.15.3", {"start": v(304.8, 203.2) * mm, "end": v(304.8, 213.51) * mm});
            skLineSegment(sketch, "E3.22.16.0", {"start": v(294.49, 215.9) * mm, "end": v(294.49, 226.21) * mm});
            skLineSegment(sketch, "E3.22.16.1", {"start": v(294.49, 226.21) * mm, "end": v(304.8, 226.21) * mm});
            skLineSegment(sketch, "E3.22.16.2", {"start": v(294.49, 215.9) * mm, "end": v(304.8, 215.9) * mm});
            skLineSegment(sketch, "E3.22.16.3", {"start": v(304.8, 215.9) * mm, "end": v(304.8, 226.21) * mm});
            skLineSegment(sketch, "E3.22.17.0", {"start": v(294.49, 228.6) * mm, "end": v(294.49, 238.91) * mm});
            skLineSegment(sketch, "E3.22.17.1", {"start": v(294.49, 238.91) * mm, "end": v(304.8, 238.91) * mm});
            skLineSegment(sketch, "E3.22.17.2", {"start": v(294.49, 228.6) * mm, "end": v(304.8, 228.6) * mm});
            skLineSegment(sketch, "E3.22.17.3", {"start": v(304.8, 228.6) * mm, "end": v(304.8, 238.91) * mm});
            skLineSegment(sketch, "E3.22.18.0", {"start": v(294.49, 241.3) * mm, "end": v(294.49, 251.61) * mm});
            skLineSegment(sketch, "E3.22.18.1", {"start": v(294.49, 251.61) * mm, "end": v(304.8, 251.61) * mm});
            skLineSegment(sketch, "E3.22.18.2", {"start": v(294.49, 241.3) * mm, "end": v(304.8, 241.3) * mm});
            skLineSegment(sketch, "E3.22.18.3", {"start": v(304.8, 241.3) * mm, "end": v(304.8, 251.61) * mm});
            skLineSegment(sketch, "E3.22.19.0", {"start": v(294.49, 254) * mm, "end": v(294.49, 264.31) * mm});
            skLineSegment(sketch, "E3.22.19.1", {"start": v(294.49, 264.31) * mm, "end": v(304.8, 264.31) * mm});
            skLineSegment(sketch, "E3.22.19.2", {"start": v(294.49, 254) * mm, "end": v(304.8, 254) * mm});
            skLineSegment(sketch, "E3.22.19.3", {"start": v(304.8, 254) * mm, "end": v(304.8, 264.31) * mm});
            skLineSegment(sketch, "E3.22.20.0", {"start": v(294.49, 266.7) * mm, "end": v(294.49, 277.01) * mm});
            skLineSegment(sketch, "E3.22.20.1", {"start": v(294.49, 277.01) * mm, "end": v(304.8, 277.01) * mm});
            skLineSegment(sketch, "E3.22.20.2", {"start": v(294.49, 266.7) * mm, "end": v(304.8, 266.7) * mm});
            skLineSegment(sketch, "E3.22.20.3", {"start": v(304.8, 266.7) * mm, "end": v(304.8, 277.01) * mm});
            skLineSegment(sketch, "E3.22.21.0", {"start": v(294.49, 279.4) * mm, "end": v(294.49, 289.71) * mm});
            skLineSegment(sketch, "E3.22.21.1", {"start": v(294.49, 289.71) * mm, "end": v(304.8, 289.71) * mm});
            skLineSegment(sketch, "E3.22.21.2", {"start": v(294.49, 279.4) * mm, "end": v(304.8, 279.4) * mm});
            skLineSegment(sketch, "E3.22.21.3", {"start": v(304.8, 279.4) * mm, "end": v(304.8, 289.71) * mm});
            skLineSegment(sketch, "E3.23.0.0", {"start": v(307.19, 12.7) * mm, "end": v(307.19, 23.01) * mm});
            skLineSegment(sketch, "E3.23.0.1", {"start": v(307.19, 23.01) * mm, "end": v(317.5, 23.01) * mm});
            skLineSegment(sketch, "E3.23.0.2", {"start": v(307.19, 12.7) * mm, "end": v(317.5, 12.7) * mm});
            skLineSegment(sketch, "E3.23.0.3", {"start": v(317.5, 12.7) * mm, "end": v(317.5, 23.01) * mm});
            skLineSegment(sketch, "E3.23.1.0", {"start": v(307.19, 25.4) * mm, "end": v(307.19, 35.71) * mm});
            skLineSegment(sketch, "E3.23.1.1", {"start": v(307.19, 35.71) * mm, "end": v(317.5, 35.71) * mm});
            skLineSegment(sketch, "E3.23.1.2", {"start": v(307.19, 25.4) * mm, "end": v(317.5, 25.4) * mm});
            skLineSegment(sketch, "E3.23.1.3", {"start": v(317.5, 25.4) * mm, "end": v(317.5, 35.71) * mm});
            skLineSegment(sketch, "E3.23.2.0", {"start": v(307.19, 38.1) * mm, "end": v(307.19, 48.41) * mm});
            skLineSegment(sketch, "E3.23.2.1", {"start": v(307.19, 48.41) * mm, "end": v(317.5, 48.41) * mm});
            skLineSegment(sketch, "E3.23.2.2", {"start": v(307.19, 38.1) * mm, "end": v(317.5, 38.1) * mm});
            skLineSegment(sketch, "E3.23.2.3", {"start": v(317.5, 38.1) * mm, "end": v(317.5, 48.41) * mm});
            skLineSegment(sketch, "E3.23.3.0", {"start": v(307.19, 50.8) * mm, "end": v(307.19, 61.11) * mm});
            skLineSegment(sketch, "E3.23.3.1", {"start": v(307.19, 61.11) * mm, "end": v(317.5, 61.11) * mm});
            skLineSegment(sketch, "E3.23.3.2", {"start": v(307.19, 50.8) * mm, "end": v(317.5, 50.8) * mm});
            skLineSegment(sketch, "E3.23.3.3", {"start": v(317.5, 50.8) * mm, "end": v(317.5, 61.11) * mm});
            skLineSegment(sketch, "E3.23.4.0", {"start": v(307.19, 63.5) * mm, "end": v(307.19, 73.81) * mm});
            skLineSegment(sketch, "E3.23.4.1", {"start": v(307.19, 73.81) * mm, "end": v(317.5, 73.81) * mm});
            skLineSegment(sketch, "E3.23.4.2", {"start": v(307.19, 63.5) * mm, "end": v(317.5, 63.5) * mm});
            skLineSegment(sketch, "E3.23.4.3", {"start": v(317.5, 63.5) * mm, "end": v(317.5, 73.81) * mm});
            skLineSegment(sketch, "E3.23.5.0", {"start": v(307.19, 76.2) * mm, "end": v(307.19, 86.51) * mm});
            skLineSegment(sketch, "E3.23.5.1", {"start": v(307.19, 86.51) * mm, "end": v(317.5, 86.51) * mm});
            skLineSegment(sketch, "E3.23.5.2", {"start": v(307.19, 76.2) * mm, "end": v(317.5, 76.2) * mm});
            skLineSegment(sketch, "E3.23.5.3", {"start": v(317.5, 76.2) * mm, "end": v(317.5, 86.51) * mm});
            skLineSegment(sketch, "E3.23.6.0", {"start": v(307.19, 88.9) * mm, "end": v(307.19, 99.21) * mm});
            skLineSegment(sketch, "E3.23.6.1", {"start": v(307.19, 99.21) * mm, "end": v(317.5, 99.21) * mm});
            skLineSegment(sketch, "E3.23.6.2", {"start": v(307.19, 88.9) * mm, "end": v(317.5, 88.9) * mm});
            skLineSegment(sketch, "E3.23.6.3", {"start": v(317.5, 88.9) * mm, "end": v(317.5, 99.21) * mm});
            skLineSegment(sketch, "E3.23.7.0", {"start": v(307.19, 101.6) * mm, "end": v(307.19, 111.91) * mm});
            skLineSegment(sketch, "E3.23.7.1", {"start": v(307.19, 111.91) * mm, "end": v(317.5, 111.91) * mm});
            skLineSegment(sketch, "E3.23.7.2", {"start": v(307.19, 101.6) * mm, "end": v(317.5, 101.6) * mm});
            skLineSegment(sketch, "E3.23.7.3", {"start": v(317.5, 101.6) * mm, "end": v(317.5, 111.91) * mm});
            skLineSegment(sketch, "E3.23.8.0", {"start": v(307.19, 114.3) * mm, "end": v(307.19, 124.61) * mm});
            skLineSegment(sketch, "E3.23.8.1", {"start": v(307.19, 124.61) * mm, "end": v(317.5, 124.61) * mm});
            skLineSegment(sketch, "E3.23.8.2", {"start": v(307.19, 114.3) * mm, "end": v(317.5, 114.3) * mm});
            skLineSegment(sketch, "E3.23.8.3", {"start": v(317.5, 114.3) * mm, "end": v(317.5, 124.61) * mm});
            skLineSegment(sketch, "E3.23.9.0", {"start": v(307.19, 127) * mm, "end": v(307.19, 137.31) * mm});
            skLineSegment(sketch, "E3.23.9.1", {"start": v(307.19, 137.31) * mm, "end": v(317.5, 137.31) * mm});
            skLineSegment(sketch, "E3.23.9.2", {"start": v(307.19, 127) * mm, "end": v(317.5, 127) * mm});
            skLineSegment(sketch, "E3.23.9.3", {"start": v(317.5, 127) * mm, "end": v(317.5, 137.31) * mm});
            skLineSegment(sketch, "E3.23.10.0", {"start": v(307.19, 139.7) * mm, "end": v(307.19, 150.01) * mm});
            skLineSegment(sketch, "E3.23.10.1", {"start": v(307.19, 150.01) * mm, "end": v(317.5, 150.01) * mm});
            skLineSegment(sketch, "E3.23.10.2", {"start": v(307.19, 139.7) * mm, "end": v(317.5, 139.7) * mm});
            skLineSegment(sketch, "E3.23.10.3", {"start": v(317.5, 139.7) * mm, "end": v(317.5, 150.01) * mm});
            skLineSegment(sketch, "E3.23.11.0", {"start": v(307.19, 152.4) * mm, "end": v(307.19, 162.71) * mm});
            skLineSegment(sketch, "E3.23.11.1", {"start": v(307.19, 162.71) * mm, "end": v(317.5, 162.71) * mm});
            skLineSegment(sketch, "E3.23.11.2", {"start": v(307.19, 152.4) * mm, "end": v(317.5, 152.4) * mm});
            skLineSegment(sketch, "E3.23.11.3", {"start": v(317.5, 152.4) * mm, "end": v(317.5, 162.71) * mm});
            skLineSegment(sketch, "E3.23.12.0", {"start": v(307.19, 165.1) * mm, "end": v(307.19, 175.41) * mm});
            skLineSegment(sketch, "E3.23.12.1", {"start": v(307.19, 175.41) * mm, "end": v(317.5, 175.41) * mm});
            skLineSegment(sketch, "E3.23.12.2", {"start": v(307.19, 165.1) * mm, "end": v(317.5, 165.1) * mm});
            skLineSegment(sketch, "E3.23.12.3", {"start": v(317.5, 165.1) * mm, "end": v(317.5, 175.41) * mm});
            skLineSegment(sketch, "E3.23.13.0", {"start": v(307.19, 177.8) * mm, "end": v(307.19, 188.11) * mm});
            skLineSegment(sketch, "E3.23.13.1", {"start": v(307.19, 188.11) * mm, "end": v(317.5, 188.11) * mm});
            skLineSegment(sketch, "E3.23.13.2", {"start": v(307.19, 177.8) * mm, "end": v(317.5, 177.8) * mm});
            skLineSegment(sketch, "E3.23.13.3", {"start": v(317.5, 177.8) * mm, "end": v(317.5, 188.11) * mm});
            skLineSegment(sketch, "E3.23.14.0", {"start": v(307.19, 190.5) * mm, "end": v(307.19, 200.81) * mm});
            skLineSegment(sketch, "E3.23.14.1", {"start": v(307.19, 200.81) * mm, "end": v(317.5, 200.81) * mm});
            skLineSegment(sketch, "E3.23.14.2", {"start": v(307.19, 190.5) * mm, "end": v(317.5, 190.5) * mm});
            skLineSegment(sketch, "E3.23.14.3", {"start": v(317.5, 190.5) * mm, "end": v(317.5, 200.81) * mm});
            skLineSegment(sketch, "E3.23.15.0", {"start": v(307.19, 203.2) * mm, "end": v(307.19, 213.51) * mm});
            skLineSegment(sketch, "E3.23.15.1", {"start": v(307.19, 213.51) * mm, "end": v(317.5, 213.51) * mm});
            skLineSegment(sketch, "E3.23.15.2", {"start": v(307.19, 203.2) * mm, "end": v(317.5, 203.2) * mm});
            skLineSegment(sketch, "E3.23.15.3", {"start": v(317.5, 203.2) * mm, "end": v(317.5, 213.51) * mm});
            skLineSegment(sketch, "E3.23.16.0", {"start": v(307.19, 215.9) * mm, "end": v(307.19, 226.21) * mm});
            skLineSegment(sketch, "E3.23.16.1", {"start": v(307.19, 226.21) * mm, "end": v(317.5, 226.21) * mm});
            skLineSegment(sketch, "E3.23.16.2", {"start": v(307.19, 215.9) * mm, "end": v(317.5, 215.9) * mm});
            skLineSegment(sketch, "E3.23.16.3", {"start": v(317.5, 215.9) * mm, "end": v(317.5, 226.21) * mm});
            skLineSegment(sketch, "E3.23.17.0", {"start": v(307.19, 228.6) * mm, "end": v(307.19, 238.91) * mm});
            skLineSegment(sketch, "E3.23.17.1", {"start": v(307.19, 238.91) * mm, "end": v(317.5, 238.91) * mm});
            skLineSegment(sketch, "E3.23.17.2", {"start": v(307.19, 228.6) * mm, "end": v(317.5, 228.6) * mm});
            skLineSegment(sketch, "E3.23.17.3", {"start": v(317.5, 228.6) * mm, "end": v(317.5, 238.91) * mm});
            skLineSegment(sketch, "E3.23.18.0", {"start": v(307.19, 241.3) * mm, "end": v(307.19, 251.61) * mm});
            skLineSegment(sketch, "E3.23.18.1", {"start": v(307.19, 251.61) * mm, "end": v(317.5, 251.61) * mm});
            skLineSegment(sketch, "E3.23.18.2", {"start": v(307.19, 241.3) * mm, "end": v(317.5, 241.3) * mm});
            skLineSegment(sketch, "E3.23.18.3", {"start": v(317.5, 241.3) * mm, "end": v(317.5, 251.61) * mm});
            skLineSegment(sketch, "E3.23.19.0", {"start": v(307.19, 254) * mm, "end": v(307.19, 264.31) * mm});
            skLineSegment(sketch, "E3.23.19.1", {"start": v(307.19, 264.31) * mm, "end": v(317.5, 264.31) * mm});
            skLineSegment(sketch, "E3.23.19.2", {"start": v(307.19, 254) * mm, "end": v(317.5, 254) * mm});
            skLineSegment(sketch, "E3.23.19.3", {"start": v(317.5, 254) * mm, "end": v(317.5, 264.31) * mm});
            skLineSegment(sketch, "E3.23.20.0", {"start": v(307.19, 266.7) * mm, "end": v(307.19, 277.01) * mm});
            skLineSegment(sketch, "E3.23.20.1", {"start": v(307.19, 277.01) * mm, "end": v(317.5, 277.01) * mm});
            skLineSegment(sketch, "E3.23.20.2", {"start": v(307.19, 266.7) * mm, "end": v(317.5, 266.7) * mm});
            skLineSegment(sketch, "E3.23.20.3", {"start": v(317.5, 266.7) * mm, "end": v(317.5, 277.01) * mm});
            skLineSegment(sketch, "E3.23.21.0", {"start": v(307.19, 279.4) * mm, "end": v(307.19, 289.71) * mm});
            skLineSegment(sketch, "E3.23.21.1", {"start": v(307.19, 289.71) * mm, "end": v(317.5, 289.71) * mm});
            skLineSegment(sketch, "E3.23.21.2", {"start": v(307.19, 279.4) * mm, "end": v(317.5, 279.4) * mm});
            skLineSegment(sketch, "E3.23.21.3", {"start": v(317.5, 279.4) * mm, "end": v(317.5, 289.71) * mm});
            skLineSegment(sketch, "E3.24.0.0", {"start": v(319.89, 12.7) * mm, "end": v(319.89, 23.01) * mm});
            skLineSegment(sketch, "E3.24.0.1", {"start": v(319.89, 23.01) * mm, "end": v(330.2, 23.01) * mm});
            skLineSegment(sketch, "E3.24.0.2", {"start": v(319.89, 12.7) * mm, "end": v(330.2, 12.7) * mm});
            skLineSegment(sketch, "E3.24.0.3", {"start": v(330.2, 12.7) * mm, "end": v(330.2, 23.01) * mm});
            skLineSegment(sketch, "E3.24.1.0", {"start": v(319.89, 25.4) * mm, "end": v(319.89, 35.71) * mm});
            skLineSegment(sketch, "E3.24.1.1", {"start": v(319.89, 35.71) * mm, "end": v(330.2, 35.71) * mm});
            skLineSegment(sketch, "E3.24.1.2", {"start": v(319.89, 25.4) * mm, "end": v(330.2, 25.4) * mm});
            skLineSegment(sketch, "E3.24.1.3", {"start": v(330.2, 25.4) * mm, "end": v(330.2, 35.71) * mm});
            skLineSegment(sketch, "E3.24.2.0", {"start": v(319.89, 38.1) * mm, "end": v(319.89, 48.41) * mm});
            skLineSegment(sketch, "E3.24.2.1", {"start": v(319.89, 48.41) * mm, "end": v(330.2, 48.41) * mm});
            skLineSegment(sketch, "E3.24.2.2", {"start": v(319.89, 38.1) * mm, "end": v(330.2, 38.1) * mm});
            skLineSegment(sketch, "E3.24.2.3", {"start": v(330.2, 38.1) * mm, "end": v(330.2, 48.41) * mm});
            skLineSegment(sketch, "E3.24.3.0", {"start": v(319.89, 50.8) * mm, "end": v(319.89, 61.11) * mm});
            skLineSegment(sketch, "E3.24.3.1", {"start": v(319.89, 61.11) * mm, "end": v(330.2, 61.11) * mm});
            skLineSegment(sketch, "E3.24.3.2", {"start": v(319.89, 50.8) * mm, "end": v(330.2, 50.8) * mm});
            skLineSegment(sketch, "E3.24.3.3", {"start": v(330.2, 50.8) * mm, "end": v(330.2, 61.11) * mm});
            skLineSegment(sketch, "E3.24.4.0", {"start": v(319.89, 63.5) * mm, "end": v(319.89, 73.81) * mm});
            skLineSegment(sketch, "E3.24.4.1", {"start": v(319.89, 73.81) * mm, "end": v(330.2, 73.81) * mm});
            skLineSegment(sketch, "E3.24.4.2", {"start": v(319.89, 63.5) * mm, "end": v(330.2, 63.5) * mm});
            skLineSegment(sketch, "E3.24.4.3", {"start": v(330.2, 63.5) * mm, "end": v(330.2, 73.81) * mm});
            skLineSegment(sketch, "E3.24.5.0", {"start": v(319.89, 76.2) * mm, "end": v(319.89, 86.51) * mm});
            skLineSegment(sketch, "E3.24.5.1", {"start": v(319.89, 86.51) * mm, "end": v(330.2, 86.51) * mm});
            skLineSegment(sketch, "E3.24.5.2", {"start": v(319.89, 76.2) * mm, "end": v(330.2, 76.2) * mm});
            skLineSegment(sketch, "E3.24.5.3", {"start": v(330.2, 76.2) * mm, "end": v(330.2, 86.51) * mm});
            skLineSegment(sketch, "E3.24.6.0", {"start": v(319.89, 88.9) * mm, "end": v(319.89, 99.21) * mm});
            skLineSegment(sketch, "E3.24.6.1", {"start": v(319.89, 99.21) * mm, "end": v(330.2, 99.21) * mm});
            skLineSegment(sketch, "E3.24.6.2", {"start": v(319.89, 88.9) * mm, "end": v(330.2, 88.9) * mm});
            skLineSegment(sketch, "E3.24.6.3", {"start": v(330.2, 88.9) * mm, "end": v(330.2, 99.21) * mm});
            skLineSegment(sketch, "E3.24.7.0", {"start": v(319.89, 101.6) * mm, "end": v(319.89, 111.91) * mm});
            skLineSegment(sketch, "E3.24.7.1", {"start": v(319.89, 111.91) * mm, "end": v(330.2, 111.91) * mm});
            skLineSegment(sketch, "E3.24.7.2", {"start": v(319.89, 101.6) * mm, "end": v(330.2, 101.6) * mm});
            skLineSegment(sketch, "E3.24.7.3", {"start": v(330.2, 101.6) * mm, "end": v(330.2, 111.91) * mm});
            skLineSegment(sketch, "E3.24.8.0", {"start": v(319.89, 114.3) * mm, "end": v(319.89, 124.61) * mm});
            skLineSegment(sketch, "E3.24.8.1", {"start": v(319.89, 124.61) * mm, "end": v(330.2, 124.61) * mm});
            skLineSegment(sketch, "E3.24.8.2", {"start": v(319.89, 114.3) * mm, "end": v(330.2, 114.3) * mm});
            skLineSegment(sketch, "E3.24.8.3", {"start": v(330.2, 114.3) * mm, "end": v(330.2, 124.61) * mm});
            skLineSegment(sketch, "E3.24.9.0", {"start": v(319.89, 127) * mm, "end": v(319.89, 137.31) * mm});
            skLineSegment(sketch, "E3.24.9.1", {"start": v(319.89, 137.31) * mm, "end": v(330.2, 137.31) * mm});
            skLineSegment(sketch, "E3.24.9.2", {"start": v(319.89, 127) * mm, "end": v(330.2, 127) * mm});
            skLineSegment(sketch, "E3.24.9.3", {"start": v(330.2, 127) * mm, "end": v(330.2, 137.31) * mm});
            skLineSegment(sketch, "E3.24.10.0", {"start": v(319.89, 139.7) * mm, "end": v(319.89, 150.01) * mm});
            skLineSegment(sketch, "E3.24.10.1", {"start": v(319.89, 150.01) * mm, "end": v(330.2, 150.01) * mm});
            skLineSegment(sketch, "E3.24.10.2", {"start": v(319.89, 139.7) * mm, "end": v(330.2, 139.7) * mm});
            skLineSegment(sketch, "E3.24.10.3", {"start": v(330.2, 139.7) * mm, "end": v(330.2, 150.01) * mm});
            skLineSegment(sketch, "E3.24.11.0", {"start": v(319.89, 152.4) * mm, "end": v(319.89, 162.71) * mm});
            skLineSegment(sketch, "E3.24.11.1", {"start": v(319.89, 162.71) * mm, "end": v(330.2, 162.71) * mm});
            skLineSegment(sketch, "E3.24.11.2", {"start": v(319.89, 152.4) * mm, "end": v(330.2, 152.4) * mm});
            skLineSegment(sketch, "E3.24.11.3", {"start": v(330.2, 152.4) * mm, "end": v(330.2, 162.71) * mm});
            skLineSegment(sketch, "E3.24.12.0", {"start": v(319.89, 165.1) * mm, "end": v(319.89, 175.41) * mm});
            skLineSegment(sketch, "E3.24.12.1", {"start": v(319.89, 175.41) * mm, "end": v(330.2, 175.41) * mm});
            skLineSegment(sketch, "E3.24.12.2", {"start": v(319.89, 165.1) * mm, "end": v(330.2, 165.1) * mm});
            skLineSegment(sketch, "E3.24.12.3", {"start": v(330.2, 165.1) * mm, "end": v(330.2, 175.41) * mm});
            skLineSegment(sketch, "E3.24.13.0", {"start": v(319.89, 177.8) * mm, "end": v(319.89, 188.11) * mm});
            skLineSegment(sketch, "E3.24.13.1", {"start": v(319.89, 188.11) * mm, "end": v(330.2, 188.11) * mm});
            skLineSegment(sketch, "E3.24.13.2", {"start": v(319.89, 177.8) * mm, "end": v(330.2, 177.8) * mm});
            skLineSegment(sketch, "E3.24.13.3", {"start": v(330.2, 177.8) * mm, "end": v(330.2, 188.11) * mm});
            skLineSegment(sketch, "E3.24.14.0", {"start": v(319.89, 190.5) * mm, "end": v(319.89, 200.81) * mm});
            skLineSegment(sketch, "E3.24.14.1", {"start": v(319.89, 200.81) * mm, "end": v(330.2, 200.81) * mm});
            skLineSegment(sketch, "E3.24.14.2", {"start": v(319.89, 190.5) * mm, "end": v(330.2, 190.5) * mm});
            skLineSegment(sketch, "E3.24.14.3", {"start": v(330.2, 190.5) * mm, "end": v(330.2, 200.81) * mm});
            skLineSegment(sketch, "E3.24.15.0", {"start": v(319.89, 203.2) * mm, "end": v(319.89, 213.51) * mm});
            skLineSegment(sketch, "E3.24.15.1", {"start": v(319.89, 213.51) * mm, "end": v(330.2, 213.51) * mm});
            skLineSegment(sketch, "E3.24.15.2", {"start": v(319.89, 203.2) * mm, "end": v(330.2, 203.2) * mm});
            skLineSegment(sketch, "E3.24.15.3", {"start": v(330.2, 203.2) * mm, "end": v(330.2, 213.51) * mm});
            skLineSegment(sketch, "E3.24.16.0", {"start": v(319.89, 215.9) * mm, "end": v(319.89, 226.21) * mm});
            skLineSegment(sketch, "E3.24.16.1", {"start": v(319.89, 226.21) * mm, "end": v(330.2, 226.21) * mm});
            skLineSegment(sketch, "E3.24.16.2", {"start": v(319.89, 215.9) * mm, "end": v(330.2, 215.9) * mm});
            skLineSegment(sketch, "E3.24.16.3", {"start": v(330.2, 215.9) * mm, "end": v(330.2, 226.21) * mm});
            skLineSegment(sketch, "E3.24.17.0", {"start": v(319.89, 228.6) * mm, "end": v(319.89, 238.91) * mm});
            skLineSegment(sketch, "E3.24.17.1", {"start": v(319.89, 238.91) * mm, "end": v(330.2, 238.91) * mm});
            skLineSegment(sketch, "E3.24.17.2", {"start": v(319.89, 228.6) * mm, "end": v(330.2, 228.6) * mm});
            skLineSegment(sketch, "E3.24.17.3", {"start": v(330.2, 228.6) * mm, "end": v(330.2, 238.91) * mm});
            skLineSegment(sketch, "E3.24.18.0", {"start": v(319.89, 241.3) * mm, "end": v(319.89, 251.61) * mm});
            skLineSegment(sketch, "E3.24.18.1", {"start": v(319.89, 251.61) * mm, "end": v(330.2, 251.61) * mm});
            skLineSegment(sketch, "E3.24.18.2", {"start": v(319.89, 241.3) * mm, "end": v(330.2, 241.3) * mm});
            skLineSegment(sketch, "E3.24.18.3", {"start": v(330.2, 241.3) * mm, "end": v(330.2, 251.61) * mm});
            skLineSegment(sketch, "E3.24.19.0", {"start": v(319.89, 254) * mm, "end": v(319.89, 264.31) * mm});
            skLineSegment(sketch, "E3.24.19.1", {"start": v(319.89, 264.31) * mm, "end": v(330.2, 264.31) * mm});
            skLineSegment(sketch, "E3.24.19.2", {"start": v(319.89, 254) * mm, "end": v(330.2, 254) * mm});
            skLineSegment(sketch, "E3.24.19.3", {"start": v(330.2, 254) * mm, "end": v(330.2, 264.31) * mm});
            skLineSegment(sketch, "E3.24.20.0", {"start": v(319.89, 266.7) * mm, "end": v(319.89, 277.01) * mm});
            skLineSegment(sketch, "E3.24.20.1", {"start": v(319.89, 277.01) * mm, "end": v(330.2, 277.01) * mm});
            skLineSegment(sketch, "E3.24.20.2", {"start": v(319.89, 266.7) * mm, "end": v(330.2, 266.7) * mm});
            skLineSegment(sketch, "E3.24.20.3", {"start": v(330.2, 266.7) * mm, "end": v(330.2, 277.01) * mm});
            skLineSegment(sketch, "E3.24.21.0", {"start": v(319.89, 279.4) * mm, "end": v(319.89, 289.71) * mm});
            skLineSegment(sketch, "E3.24.21.1", {"start": v(319.89, 289.71) * mm, "end": v(330.2, 289.71) * mm});
            skLineSegment(sketch, "E3.24.21.2", {"start": v(319.89, 279.4) * mm, "end": v(330.2, 279.4) * mm});
            skLineSegment(sketch, "E3.24.21.3", {"start": v(330.2, 279.4) * mm, "end": v(330.2, 289.71) * mm});
            skLineSegment(sketch, "E3.25.0.0", {"start": v(332.59, 12.7) * mm, "end": v(332.59, 23.01) * mm});
            skLineSegment(sketch, "E3.25.0.1", {"start": v(332.59, 23.01) * mm, "end": v(342.9, 23.01) * mm});
            skLineSegment(sketch, "E3.25.0.2", {"start": v(332.59, 12.7) * mm, "end": v(342.9, 12.7) * mm});
            skLineSegment(sketch, "E3.25.0.3", {"start": v(342.9, 12.7) * mm, "end": v(342.9, 23.01) * mm});
            skLineSegment(sketch, "E3.25.1.0", {"start": v(332.59, 25.4) * mm, "end": v(332.59, 35.71) * mm});
            skLineSegment(sketch, "E3.25.1.1", {"start": v(332.59, 35.71) * mm, "end": v(342.9, 35.71) * mm});
            skLineSegment(sketch, "E3.25.1.2", {"start": v(332.59, 25.4) * mm, "end": v(342.9, 25.4) * mm});
            skLineSegment(sketch, "E3.25.1.3", {"start": v(342.9, 25.4) * mm, "end": v(342.9, 35.71) * mm});
            skLineSegment(sketch, "E3.25.2.0", {"start": v(332.59, 38.1) * mm, "end": v(332.59, 48.41) * mm});
            skLineSegment(sketch, "E3.25.2.1", {"start": v(332.59, 48.41) * mm, "end": v(342.9, 48.41) * mm});
            skLineSegment(sketch, "E3.25.2.2", {"start": v(332.59, 38.1) * mm, "end": v(342.9, 38.1) * mm});
            skLineSegment(sketch, "E3.25.2.3", {"start": v(342.9, 38.1) * mm, "end": v(342.9, 48.41) * mm});
            skLineSegment(sketch, "E3.25.3.0", {"start": v(332.59, 50.8) * mm, "end": v(332.59, 61.11) * mm});
            skLineSegment(sketch, "E3.25.3.1", {"start": v(332.59, 61.11) * mm, "end": v(342.9, 61.11) * mm});
            skLineSegment(sketch, "E3.25.3.2", {"start": v(332.59, 50.8) * mm, "end": v(342.9, 50.8) * mm});
            skLineSegment(sketch, "E3.25.3.3", {"start": v(342.9, 50.8) * mm, "end": v(342.9, 61.11) * mm});
            skLineSegment(sketch, "E3.25.4.0", {"start": v(332.59, 63.5) * mm, "end": v(332.59, 73.81) * mm});
            skLineSegment(sketch, "E3.25.4.1", {"start": v(332.59, 73.81) * mm, "end": v(342.9, 73.81) * mm});
            skLineSegment(sketch, "E3.25.4.2", {"start": v(332.59, 63.5) * mm, "end": v(342.9, 63.5) * mm});
            skLineSegment(sketch, "E3.25.4.3", {"start": v(342.9, 63.5) * mm, "end": v(342.9, 73.81) * mm});
            skLineSegment(sketch, "E3.25.5.0", {"start": v(332.59, 76.2) * mm, "end": v(332.59, 86.51) * mm});
            skLineSegment(sketch, "E3.25.5.1", {"start": v(332.59, 86.51) * mm, "end": v(342.9, 86.51) * mm});
            skLineSegment(sketch, "E3.25.5.2", {"start": v(332.59, 76.2) * mm, "end": v(342.9, 76.2) * mm});
            skLineSegment(sketch, "E3.25.5.3", {"start": v(342.9, 76.2) * mm, "end": v(342.9, 86.51) * mm});
            skLineSegment(sketch, "E3.25.6.0", {"start": v(332.59, 88.9) * mm, "end": v(332.59, 99.21) * mm});
            skLineSegment(sketch, "E3.25.6.1", {"start": v(332.59, 99.21) * mm, "end": v(342.9, 99.21) * mm});
            skLineSegment(sketch, "E3.25.6.2", {"start": v(332.59, 88.9) * mm, "end": v(342.9, 88.9) * mm});
            skLineSegment(sketch, "E3.25.6.3", {"start": v(342.9, 88.9) * mm, "end": v(342.9, 99.21) * mm});
            skLineSegment(sketch, "E3.25.7.0", {"start": v(332.59, 101.6) * mm, "end": v(332.59, 111.91) * mm});
            skLineSegment(sketch, "E3.25.7.1", {"start": v(332.59, 111.91) * mm, "end": v(342.9, 111.91) * mm});
            skLineSegment(sketch, "E3.25.7.2", {"start": v(332.59, 101.6) * mm, "end": v(342.9, 101.6) * mm});
            skLineSegment(sketch, "E3.25.7.3", {"start": v(342.9, 101.6) * mm, "end": v(342.9, 111.91) * mm});
            skLineSegment(sketch, "E3.25.8.0", {"start": v(332.59, 114.3) * mm, "end": v(332.59, 124.61) * mm});
            skLineSegment(sketch, "E3.25.8.1", {"start": v(332.59, 124.61) * mm, "end": v(342.9, 124.61) * mm});
            skLineSegment(sketch, "E3.25.8.2", {"start": v(332.59, 114.3) * mm, "end": v(342.9, 114.3) * mm});
            skLineSegment(sketch, "E3.25.8.3", {"start": v(342.9, 114.3) * mm, "end": v(342.9, 124.61) * mm});
            skLineSegment(sketch, "E3.25.9.0", {"start": v(332.59, 127) * mm, "end": v(332.59, 137.31) * mm});
            skLineSegment(sketch, "E3.25.9.1", {"start": v(332.59, 137.31) * mm, "end": v(342.9, 137.31) * mm});
            skLineSegment(sketch, "E3.25.9.2", {"start": v(332.59, 127) * mm, "end": v(342.9, 127) * mm});
            skLineSegment(sketch, "E3.25.9.3", {"start": v(342.9, 127) * mm, "end": v(342.9, 137.31) * mm});
            skLineSegment(sketch, "E3.25.10.0", {"start": v(332.59, 139.7) * mm, "end": v(332.59, 150.01) * mm});
            skLineSegment(sketch, "E3.25.10.1", {"start": v(332.59, 150.01) * mm, "end": v(342.9, 150.01) * mm});
            skLineSegment(sketch, "E3.25.10.2", {"start": v(332.59, 139.7) * mm, "end": v(342.9, 139.7) * mm});
            skLineSegment(sketch, "E3.25.10.3", {"start": v(342.9, 139.7) * mm, "end": v(342.9, 150.01) * mm});
            skLineSegment(sketch, "E3.25.11.0", {"start": v(332.59, 152.4) * mm, "end": v(332.59, 162.71) * mm});
            skLineSegment(sketch, "E3.25.11.1", {"start": v(332.59, 162.71) * mm, "end": v(342.9, 162.71) * mm});
            skLineSegment(sketch, "E3.25.11.2", {"start": v(332.59, 152.4) * mm, "end": v(342.9, 152.4) * mm});
            skLineSegment(sketch, "E3.25.11.3", {"start": v(342.9, 152.4) * mm, "end": v(342.9, 162.71) * mm});
            skLineSegment(sketch, "E3.25.12.0", {"start": v(332.59, 165.1) * mm, "end": v(332.59, 175.41) * mm});
            skLineSegment(sketch, "E3.25.12.1", {"start": v(332.59, 175.41) * mm, "end": v(342.9, 175.41) * mm});
            skLineSegment(sketch, "E3.25.12.2", {"start": v(332.59, 165.1) * mm, "end": v(342.9, 165.1) * mm});
            skLineSegment(sketch, "E3.25.12.3", {"start": v(342.9, 165.1) * mm, "end": v(342.9, 175.41) * mm});
            skLineSegment(sketch, "E3.25.13.0", {"start": v(332.59, 177.8) * mm, "end": v(332.59, 188.11) * mm});
            skLineSegment(sketch, "E3.25.13.1", {"start": v(332.59, 188.11) * mm, "end": v(342.9, 188.11) * mm});
            skLineSegment(sketch, "E3.25.13.2", {"start": v(332.59, 177.8) * mm, "end": v(342.9, 177.8) * mm});
            skLineSegment(sketch, "E3.25.13.3", {"start": v(342.9, 177.8) * mm, "end": v(342.9, 188.11) * mm});
            skLineSegment(sketch, "E3.25.14.0", {"start": v(332.59, 190.5) * mm, "end": v(332.59, 200.81) * mm});
            skLineSegment(sketch, "E3.25.14.1", {"start": v(332.59, 200.81) * mm, "end": v(342.9, 200.81) * mm});
            skLineSegment(sketch, "E3.25.14.2", {"start": v(332.59, 190.5) * mm, "end": v(342.9, 190.5) * mm});
            skLineSegment(sketch, "E3.25.14.3", {"start": v(342.9, 190.5) * mm, "end": v(342.9, 200.81) * mm});
            skLineSegment(sketch, "E3.25.15.0", {"start": v(332.59, 203.2) * mm, "end": v(332.59, 213.51) * mm});
            skLineSegment(sketch, "E3.25.15.1", {"start": v(332.59, 213.51) * mm, "end": v(342.9, 213.51) * mm});
            skLineSegment(sketch, "E3.25.15.2", {"start": v(332.59, 203.2) * mm, "end": v(342.9, 203.2) * mm});
            skLineSegment(sketch, "E3.25.15.3", {"start": v(342.9, 203.2) * mm, "end": v(342.9, 213.51) * mm});
            skLineSegment(sketch, "E3.25.16.0", {"start": v(332.59, 215.9) * mm, "end": v(332.59, 226.21) * mm});
            skLineSegment(sketch, "E3.25.16.1", {"start": v(332.59, 226.21) * mm, "end": v(342.9, 226.21) * mm});
            skLineSegment(sketch, "E3.25.16.2", {"start": v(332.59, 215.9) * mm, "end": v(342.9, 215.9) * mm});
            skLineSegment(sketch, "E3.25.16.3", {"start": v(342.9, 215.9) * mm, "end": v(342.9, 226.21) * mm});
            skLineSegment(sketch, "E3.25.17.0", {"start": v(332.59, 228.6) * mm, "end": v(332.59, 238.91) * mm});
            skLineSegment(sketch, "E3.25.17.1", {"start": v(332.59, 238.91) * mm, "end": v(342.9, 238.91) * mm});
            skLineSegment(sketch, "E3.25.17.2", {"start": v(332.59, 228.6) * mm, "end": v(342.9, 228.6) * mm});
            skLineSegment(sketch, "E3.25.17.3", {"start": v(342.9, 228.6) * mm, "end": v(342.9, 238.91) * mm});
            skLineSegment(sketch, "E3.25.18.0", {"start": v(332.59, 241.3) * mm, "end": v(332.59, 251.61) * mm});
            skLineSegment(sketch, "E3.25.18.1", {"start": v(332.59, 251.61) * mm, "end": v(342.9, 251.61) * mm});
            skLineSegment(sketch, "E3.25.18.2", {"start": v(332.59, 241.3) * mm, "end": v(342.9, 241.3) * mm});
            skLineSegment(sketch, "E3.25.18.3", {"start": v(342.9, 241.3) * mm, "end": v(342.9, 251.61) * mm});
            skLineSegment(sketch, "E3.25.19.0", {"start": v(332.59, 254) * mm, "end": v(332.59, 264.31) * mm});
            skLineSegment(sketch, "E3.25.19.1", {"start": v(332.59, 264.31) * mm, "end": v(342.9, 264.31) * mm});
            skLineSegment(sketch, "E3.25.19.2", {"start": v(332.59, 254) * mm, "end": v(342.9, 254) * mm});
            skLineSegment(sketch, "E3.25.19.3", {"start": v(342.9, 254) * mm, "end": v(342.9, 264.31) * mm});
            skLineSegment(sketch, "E3.25.20.0", {"start": v(332.59, 266.7) * mm, "end": v(332.59, 277.01) * mm});
            skLineSegment(sketch, "E3.25.20.1", {"start": v(332.59, 277.01) * mm, "end": v(342.9, 277.01) * mm});
            skLineSegment(sketch, "E3.25.20.2", {"start": v(332.59, 266.7) * mm, "end": v(342.9, 266.7) * mm});
            skLineSegment(sketch, "E3.25.20.3", {"start": v(342.9, 266.7) * mm, "end": v(342.9, 277.01) * mm});
            skLineSegment(sketch, "E3.25.21.0", {"start": v(332.59, 279.4) * mm, "end": v(332.59, 289.71) * mm});
            skLineSegment(sketch, "E3.25.21.1", {"start": v(332.59, 289.71) * mm, "end": v(342.9, 289.71) * mm});
            skLineSegment(sketch, "E3.25.21.2", {"start": v(332.59, 279.4) * mm, "end": v(342.9, 279.4) * mm});
            skLineSegment(sketch, "E3.25.21.3", {"start": v(342.9, 279.4) * mm, "end": v(342.9, 289.71) * mm});
            skLineSegment(sketch, "E3.26.0.0", {"start": v(345.29, 12.7) * mm, "end": v(345.29, 23.01) * mm});
            skLineSegment(sketch, "E3.26.0.1", {"start": v(345.29, 23.01) * mm, "end": v(355.6, 23.01) * mm});
            skLineSegment(sketch, "E3.26.0.2", {"start": v(345.29, 12.7) * mm, "end": v(355.6, 12.7) * mm});
            skLineSegment(sketch, "E3.26.0.3", {"start": v(355.6, 12.7) * mm, "end": v(355.6, 23.01) * mm});
            skLineSegment(sketch, "E3.26.1.0", {"start": v(345.29, 25.4) * mm, "end": v(345.29, 35.71) * mm});
            skLineSegment(sketch, "E3.26.1.1", {"start": v(345.29, 35.71) * mm, "end": v(355.6, 35.71) * mm});
            skLineSegment(sketch, "E3.26.1.2", {"start": v(345.29, 25.4) * mm, "end": v(355.6, 25.4) * mm});
            skLineSegment(sketch, "E3.26.1.3", {"start": v(355.6, 25.4) * mm, "end": v(355.6, 35.71) * mm});
            skLineSegment(sketch, "E3.26.2.0", {"start": v(345.29, 38.1) * mm, "end": v(345.29, 48.41) * mm});
            skLineSegment(sketch, "E3.26.2.1", {"start": v(345.29, 48.41) * mm, "end": v(355.6, 48.41) * mm});
            skLineSegment(sketch, "E3.26.2.2", {"start": v(345.29, 38.1) * mm, "end": v(355.6, 38.1) * mm});
            skLineSegment(sketch, "E3.26.2.3", {"start": v(355.6, 38.1) * mm, "end": v(355.6, 48.41) * mm});
            skLineSegment(sketch, "E3.26.3.0", {"start": v(345.29, 50.8) * mm, "end": v(345.29, 61.11) * mm});
            skLineSegment(sketch, "E3.26.3.1", {"start": v(345.29, 61.11) * mm, "end": v(355.6, 61.11) * mm});
            skLineSegment(sketch, "E3.26.3.2", {"start": v(345.29, 50.8) * mm, "end": v(355.6, 50.8) * mm});
            skLineSegment(sketch, "E3.26.3.3", {"start": v(355.6, 50.8) * mm, "end": v(355.6, 61.11) * mm});
            skLineSegment(sketch, "E3.26.4.0", {"start": v(345.29, 63.5) * mm, "end": v(345.29, 73.81) * mm});
            skLineSegment(sketch, "E3.26.4.1", {"start": v(345.29, 73.81) * mm, "end": v(355.6, 73.81) * mm});
            skLineSegment(sketch, "E3.26.4.2", {"start": v(345.29, 63.5) * mm, "end": v(355.6, 63.5) * mm});
            skLineSegment(sketch, "E3.26.4.3", {"start": v(355.6, 63.5) * mm, "end": v(355.6, 73.81) * mm});
            skLineSegment(sketch, "E3.26.5.0", {"start": v(345.29, 76.2) * mm, "end": v(345.29, 86.51) * mm});
            skLineSegment(sketch, "E3.26.5.1", {"start": v(345.29, 86.51) * mm, "end": v(355.6, 86.51) * mm});
            skLineSegment(sketch, "E3.26.5.2", {"start": v(345.29, 76.2) * mm, "end": v(355.6, 76.2) * mm});
            skLineSegment(sketch, "E3.26.5.3", {"start": v(355.6, 76.2) * mm, "end": v(355.6, 86.51) * mm});
            skLineSegment(sketch, "E3.26.6.0", {"start": v(345.29, 88.9) * mm, "end": v(345.29, 99.21) * mm});
            skLineSegment(sketch, "E3.26.6.1", {"start": v(345.29, 99.21) * mm, "end": v(355.6, 99.21) * mm});
            skLineSegment(sketch, "E3.26.6.2", {"start": v(345.29, 88.9) * mm, "end": v(355.6, 88.9) * mm});
            skLineSegment(sketch, "E3.26.6.3", {"start": v(355.6, 88.9) * mm, "end": v(355.6, 99.21) * mm});
            skLineSegment(sketch, "E3.26.7.0", {"start": v(345.29, 101.6) * mm, "end": v(345.29, 111.91) * mm});
            skLineSegment(sketch, "E3.26.7.1", {"start": v(345.29, 111.91) * mm, "end": v(355.6, 111.91) * mm});
            skLineSegment(sketch, "E3.26.7.2", {"start": v(345.29, 101.6) * mm, "end": v(355.6, 101.6) * mm});
            skLineSegment(sketch, "E3.26.7.3", {"start": v(355.6, 101.6) * mm, "end": v(355.6, 111.91) * mm});
            skLineSegment(sketch, "E3.26.8.0", {"start": v(345.29, 114.3) * mm, "end": v(345.29, 124.61) * mm});
            skLineSegment(sketch, "E3.26.8.1", {"start": v(345.29, 124.61) * mm, "end": v(355.6, 124.61) * mm});
            skLineSegment(sketch, "E3.26.8.2", {"start": v(345.29, 114.3) * mm, "end": v(355.6, 114.3) * mm});
            skLineSegment(sketch, "E3.26.8.3", {"start": v(355.6, 114.3) * mm, "end": v(355.6, 124.61) * mm});
            skLineSegment(sketch, "E3.26.9.0", {"start": v(345.29, 127) * mm, "end": v(345.29, 137.31) * mm});
            skLineSegment(sketch, "E3.26.9.1", {"start": v(345.29, 137.31) * mm, "end": v(355.6, 137.31) * mm});
            skLineSegment(sketch, "E3.26.9.2", {"start": v(345.29, 127) * mm, "end": v(355.6, 127) * mm});
            skLineSegment(sketch, "E3.26.9.3", {"start": v(355.6, 127) * mm, "end": v(355.6, 137.31) * mm});
            skLineSegment(sketch, "E3.26.10.0", {"start": v(345.29, 139.7) * mm, "end": v(345.29, 150.01) * mm});
            skLineSegment(sketch, "E3.26.10.1", {"start": v(345.29, 150.01) * mm, "end": v(355.6, 150.01) * mm});
            skLineSegment(sketch, "E3.26.10.2", {"start": v(345.29, 139.7) * mm, "end": v(355.6, 139.7) * mm});
            skLineSegment(sketch, "E3.26.10.3", {"start": v(355.6, 139.7) * mm, "end": v(355.6, 150.01) * mm});
            skLineSegment(sketch, "E3.26.11.0", {"start": v(345.29, 152.4) * mm, "end": v(345.29, 162.71) * mm});
            skLineSegment(sketch, "E3.26.11.1", {"start": v(345.29, 162.71) * mm, "end": v(355.6, 162.71) * mm});
            skLineSegment(sketch, "E3.26.11.2", {"start": v(345.29, 152.4) * mm, "end": v(355.6, 152.4) * mm});
            skLineSegment(sketch, "E3.26.11.3", {"start": v(355.6, 152.4) * mm, "end": v(355.6, 162.71) * mm});
            skLineSegment(sketch, "E3.26.12.0", {"start": v(345.29, 165.1) * mm, "end": v(345.29, 175.41) * mm});
            skLineSegment(sketch, "E3.26.12.1", {"start": v(345.29, 175.41) * mm, "end": v(355.6, 175.41) * mm});
            skLineSegment(sketch, "E3.26.12.2", {"start": v(345.29, 165.1) * mm, "end": v(355.6, 165.1) * mm});
            skLineSegment(sketch, "E3.26.12.3", {"start": v(355.6, 165.1) * mm, "end": v(355.6, 175.41) * mm});
            skLineSegment(sketch, "E3.26.13.0", {"start": v(345.29, 177.8) * mm, "end": v(345.29, 188.11) * mm});
            skLineSegment(sketch, "E3.26.13.1", {"start": v(345.29, 188.11) * mm, "end": v(355.6, 188.11) * mm});
            skLineSegment(sketch, "E3.26.13.2", {"start": v(345.29, 177.8) * mm, "end": v(355.6, 177.8) * mm});
            skLineSegment(sketch, "E3.26.13.3", {"start": v(355.6, 177.8) * mm, "end": v(355.6, 188.11) * mm});
            skLineSegment(sketch, "E3.26.14.0", {"start": v(345.29, 190.5) * mm, "end": v(345.29, 200.81) * mm});
            skLineSegment(sketch, "E3.26.14.1", {"start": v(345.29, 200.81) * mm, "end": v(355.6, 200.81) * mm});
            skLineSegment(sketch, "E3.26.14.2", {"start": v(345.29, 190.5) * mm, "end": v(355.6, 190.5) * mm});
            skLineSegment(sketch, "E3.26.14.3", {"start": v(355.6, 190.5) * mm, "end": v(355.6, 200.81) * mm});
            skLineSegment(sketch, "E3.26.15.0", {"start": v(345.29, 203.2) * mm, "end": v(345.29, 213.51) * mm});
            skLineSegment(sketch, "E3.26.15.1", {"start": v(345.29, 213.51) * mm, "end": v(355.6, 213.51) * mm});
            skLineSegment(sketch, "E3.26.15.2", {"start": v(345.29, 203.2) * mm, "end": v(355.6, 203.2) * mm});
            skLineSegment(sketch, "E3.26.15.3", {"start": v(355.6, 203.2) * mm, "end": v(355.6, 213.51) * mm});
            skLineSegment(sketch, "E3.26.16.0", {"start": v(345.29, 215.9) * mm, "end": v(345.29, 226.21) * mm});
            skLineSegment(sketch, "E3.26.16.1", {"start": v(345.29, 226.21) * mm, "end": v(355.6, 226.21) * mm});
            skLineSegment(sketch, "E3.26.16.2", {"start": v(345.29, 215.9) * mm, "end": v(355.6, 215.9) * mm});
            skLineSegment(sketch, "E3.26.16.3", {"start": v(355.6, 215.9) * mm, "end": v(355.6, 226.21) * mm});
            skLineSegment(sketch, "E3.26.17.0", {"start": v(345.29, 228.6) * mm, "end": v(345.29, 238.91) * mm});
            skLineSegment(sketch, "E3.26.17.1", {"start": v(345.29, 238.91) * mm, "end": v(355.6, 238.91) * mm});
            skLineSegment(sketch, "E3.26.17.2", {"start": v(345.29, 228.6) * mm, "end": v(355.6, 228.6) * mm});
            skLineSegment(sketch, "E3.26.17.3", {"start": v(355.6, 228.6) * mm, "end": v(355.6, 238.91) * mm});
            skLineSegment(sketch, "E3.26.18.0", {"start": v(345.29, 241.3) * mm, "end": v(345.29, 251.61) * mm});
            skLineSegment(sketch, "E3.26.18.1", {"start": v(345.29, 251.61) * mm, "end": v(355.6, 251.61) * mm});
            skLineSegment(sketch, "E3.26.18.2", {"start": v(345.29, 241.3) * mm, "end": v(355.6, 241.3) * mm});
            skLineSegment(sketch, "E3.26.18.3", {"start": v(355.6, 241.3) * mm, "end": v(355.6, 251.61) * mm});
            skLineSegment(sketch, "E3.26.19.0", {"start": v(345.29, 254) * mm, "end": v(345.29, 264.31) * mm});
            skLineSegment(sketch, "E3.26.19.1", {"start": v(345.29, 264.31) * mm, "end": v(355.6, 264.31) * mm});
            skLineSegment(sketch, "E3.26.19.2", {"start": v(345.29, 254) * mm, "end": v(355.6, 254) * mm});
            skLineSegment(sketch, "E3.26.19.3", {"start": v(355.6, 254) * mm, "end": v(355.6, 264.31) * mm});
            skLineSegment(sketch, "E3.26.20.0", {"start": v(345.29, 266.7) * mm, "end": v(345.29, 277.01) * mm});
            skLineSegment(sketch, "E3.26.20.1", {"start": v(345.29, 277.01) * mm, "end": v(355.6, 277.01) * mm});
            skLineSegment(sketch, "E3.26.20.2", {"start": v(345.29, 266.7) * mm, "end": v(355.6, 266.7) * mm});
            skLineSegment(sketch, "E3.26.20.3", {"start": v(355.6, 266.7) * mm, "end": v(355.6, 277.01) * mm});
            skLineSegment(sketch, "E3.26.21.0", {"start": v(345.29, 279.4) * mm, "end": v(345.29, 289.71) * mm});
            skLineSegment(sketch, "E3.26.21.1", {"start": v(345.29, 289.71) * mm, "end": v(355.6, 289.71) * mm});
            skLineSegment(sketch, "E3.26.21.2", {"start": v(345.29, 279.4) * mm, "end": v(355.6, 279.4) * mm});
            skLineSegment(sketch, "E3.26.21.3", {"start": v(355.6, 279.4) * mm, "end": v(355.6, 289.71) * mm});
            skLineSegment(sketch, "E3.27.0.0", {"start": v(357.99, 12.7) * mm, "end": v(357.99, 23.01) * mm});
            skLineSegment(sketch, "E3.27.0.1", {"start": v(357.99, 23.01) * mm, "end": v(368.3, 23.01) * mm});
            skLineSegment(sketch, "E3.27.0.2", {"start": v(357.99, 12.7) * mm, "end": v(368.3, 12.7) * mm});
            skLineSegment(sketch, "E3.27.0.3", {"start": v(368.3, 12.7) * mm, "end": v(368.3, 23.01) * mm});
            skLineSegment(sketch, "E3.27.1.0", {"start": v(357.99, 25.4) * mm, "end": v(357.99, 35.71) * mm});
            skLineSegment(sketch, "E3.27.1.1", {"start": v(357.99, 35.71) * mm, "end": v(368.3, 35.71) * mm});
            skLineSegment(sketch, "E3.27.1.2", {"start": v(357.99, 25.4) * mm, "end": v(368.3, 25.4) * mm});
            skLineSegment(sketch, "E3.27.1.3", {"start": v(368.3, 25.4) * mm, "end": v(368.3, 35.71) * mm});
            skLineSegment(sketch, "E3.27.2.0", {"start": v(357.99, 38.1) * mm, "end": v(357.99, 48.41) * mm});
            skLineSegment(sketch, "E3.27.2.1", {"start": v(357.99, 48.41) * mm, "end": v(368.3, 48.41) * mm});
            skLineSegment(sketch, "E3.27.2.2", {"start": v(357.99, 38.1) * mm, "end": v(368.3, 38.1) * mm});
            skLineSegment(sketch, "E3.27.2.3", {"start": v(368.3, 38.1) * mm, "end": v(368.3, 48.41) * mm});
            skLineSegment(sketch, "E3.27.3.0", {"start": v(357.99, 50.8) * mm, "end": v(357.99, 61.11) * mm});
            skLineSegment(sketch, "E3.27.3.1", {"start": v(357.99, 61.11) * mm, "end": v(368.3, 61.11) * mm});
            skLineSegment(sketch, "E3.27.3.2", {"start": v(357.99, 50.8) * mm, "end": v(368.3, 50.8) * mm});
            skLineSegment(sketch, "E3.27.3.3", {"start": v(368.3, 50.8) * mm, "end": v(368.3, 61.11) * mm});
            skLineSegment(sketch, "E3.27.4.0", {"start": v(357.99, 63.5) * mm, "end": v(357.99, 73.81) * mm});
            skLineSegment(sketch, "E3.27.4.1", {"start": v(357.99, 73.81) * mm, "end": v(368.3, 73.81) * mm});
            skLineSegment(sketch, "E3.27.4.2", {"start": v(357.99, 63.5) * mm, "end": v(368.3, 63.5) * mm});
            skLineSegment(sketch, "E3.27.4.3", {"start": v(368.3, 63.5) * mm, "end": v(368.3, 73.81) * mm});
            skLineSegment(sketch, "E3.27.5.0", {"start": v(357.99, 76.2) * mm, "end": v(357.99, 86.51) * mm});
            skLineSegment(sketch, "E3.27.5.1", {"start": v(357.99, 86.51) * mm, "end": v(368.3, 86.51) * mm});
            skLineSegment(sketch, "E3.27.5.2", {"start": v(357.99, 76.2) * mm, "end": v(368.3, 76.2) * mm});
            skLineSegment(sketch, "E3.27.5.3", {"start": v(368.3, 76.2) * mm, "end": v(368.3, 86.51) * mm});
            skLineSegment(sketch, "E3.27.6.0", {"start": v(357.99, 88.9) * mm, "end": v(357.99, 99.21) * mm});
            skLineSegment(sketch, "E3.27.6.1", {"start": v(357.99, 99.21) * mm, "end": v(368.3, 99.21) * mm});
            skLineSegment(sketch, "E3.27.6.2", {"start": v(357.99, 88.9) * mm, "end": v(368.3, 88.9) * mm});
            skLineSegment(sketch, "E3.27.6.3", {"start": v(368.3, 88.9) * mm, "end": v(368.3, 99.21) * mm});
            skLineSegment(sketch, "E3.27.7.0", {"start": v(357.99, 101.6) * mm, "end": v(357.99, 111.91) * mm});
            skLineSegment(sketch, "E3.27.7.1", {"start": v(357.99, 111.91) * mm, "end": v(368.3, 111.91) * mm});
            skLineSegment(sketch, "E3.27.7.2", {"start": v(357.99, 101.6) * mm, "end": v(368.3, 101.6) * mm});
            skLineSegment(sketch, "E3.27.7.3", {"start": v(368.3, 101.6) * mm, "end": v(368.3, 111.91) * mm});
            skLineSegment(sketch, "E3.27.8.0", {"start": v(357.99, 114.3) * mm, "end": v(357.99, 124.61) * mm});
            skLineSegment(sketch, "E3.27.8.1", {"start": v(357.99, 124.61) * mm, "end": v(368.3, 124.61) * mm});
            skLineSegment(sketch, "E3.27.8.2", {"start": v(357.99, 114.3) * mm, "end": v(368.3, 114.3) * mm});
            skLineSegment(sketch, "E3.27.8.3", {"start": v(368.3, 114.3) * mm, "end": v(368.3, 124.61) * mm});
            skLineSegment(sketch, "E3.27.9.0", {"start": v(357.99, 127) * mm, "end": v(357.99, 137.31) * mm});
            skLineSegment(sketch, "E3.27.9.1", {"start": v(357.99, 137.31) * mm, "end": v(368.3, 137.31) * mm});
            skLineSegment(sketch, "E3.27.9.2", {"start": v(357.99, 127) * mm, "end": v(368.3, 127) * mm});
            skLineSegment(sketch, "E3.27.9.3", {"start": v(368.3, 127) * mm, "end": v(368.3, 137.31) * mm});
            skLineSegment(sketch, "E3.27.10.0", {"start": v(357.99, 139.7) * mm, "end": v(357.99, 150.01) * mm});
            skLineSegment(sketch, "E3.27.10.1", {"start": v(357.99, 150.01) * mm, "end": v(368.3, 150.01) * mm});
            skLineSegment(sketch, "E3.27.10.2", {"start": v(357.99, 139.7) * mm, "end": v(368.3, 139.7) * mm});
            skLineSegment(sketch, "E3.27.10.3", {"start": v(368.3, 139.7) * mm, "end": v(368.3, 150.01) * mm});
            skLineSegment(sketch, "E3.27.11.0", {"start": v(357.99, 152.4) * mm, "end": v(357.99, 162.71) * mm});
            skLineSegment(sketch, "E3.27.11.1", {"start": v(357.99, 162.71) * mm, "end": v(368.3, 162.71) * mm});
            skLineSegment(sketch, "E3.27.11.2", {"start": v(357.99, 152.4) * mm, "end": v(368.3, 152.4) * mm});
            skLineSegment(sketch, "E3.27.11.3", {"start": v(368.3, 152.4) * mm, "end": v(368.3, 162.71) * mm});
            skLineSegment(sketch, "E3.27.12.0", {"start": v(357.99, 165.1) * mm, "end": v(357.99, 175.41) * mm});
            skLineSegment(sketch, "E3.27.12.1", {"start": v(357.99, 175.41) * mm, "end": v(368.3, 175.41) * mm});
            skLineSegment(sketch, "E3.27.12.2", {"start": v(357.99, 165.1) * mm, "end": v(368.3, 165.1) * mm});
            skLineSegment(sketch, "E3.27.12.3", {"start": v(368.3, 165.1) * mm, "end": v(368.3, 175.41) * mm});
            skLineSegment(sketch, "E3.27.13.0", {"start": v(357.99, 177.8) * mm, "end": v(357.99, 188.11) * mm});
            skLineSegment(sketch, "E3.27.13.1", {"start": v(357.99, 188.11) * mm, "end": v(368.3, 188.11) * mm});
            skLineSegment(sketch, "E3.27.13.2", {"start": v(357.99, 177.8) * mm, "end": v(368.3, 177.8) * mm});
            skLineSegment(sketch, "E3.27.13.3", {"start": v(368.3, 177.8) * mm, "end": v(368.3, 188.11) * mm});
            skLineSegment(sketch, "E3.27.14.0", {"start": v(357.99, 190.5) * mm, "end": v(357.99, 200.81) * mm});
            skLineSegment(sketch, "E3.27.14.1", {"start": v(357.99, 200.81) * mm, "end": v(368.3, 200.81) * mm});
            skLineSegment(sketch, "E3.27.14.2", {"start": v(357.99, 190.5) * mm, "end": v(368.3, 190.5) * mm});
            skLineSegment(sketch, "E3.27.14.3", {"start": v(368.3, 190.5) * mm, "end": v(368.3, 200.81) * mm});
            skLineSegment(sketch, "E3.27.15.0", {"start": v(357.99, 203.2) * mm, "end": v(357.99, 213.51) * mm});
            skLineSegment(sketch, "E3.27.15.1", {"start": v(357.99, 213.51) * mm, "end": v(368.3, 213.51) * mm});
            skLineSegment(sketch, "E3.27.15.2", {"start": v(357.99, 203.2) * mm, "end": v(368.3, 203.2) * mm});
            skLineSegment(sketch, "E3.27.15.3", {"start": v(368.3, 203.2) * mm, "end": v(368.3, 213.51) * mm});
            skLineSegment(sketch, "E3.27.16.0", {"start": v(357.99, 215.9) * mm, "end": v(357.99, 226.21) * mm});
            skLineSegment(sketch, "E3.27.16.1", {"start": v(357.99, 226.21) * mm, "end": v(368.3, 226.21) * mm});
            skLineSegment(sketch, "E3.27.16.2", {"start": v(357.99, 215.9) * mm, "end": v(368.3, 215.9) * mm});
            skLineSegment(sketch, "E3.27.16.3", {"start": v(368.3, 215.9) * mm, "end": v(368.3, 226.21) * mm});
            skLineSegment(sketch, "E3.27.17.0", {"start": v(357.99, 228.6) * mm, "end": v(357.99, 238.91) * mm});
            skLineSegment(sketch, "E3.27.17.1", {"start": v(357.99, 238.91) * mm, "end": v(368.3, 238.91) * mm});
            skLineSegment(sketch, "E3.27.17.2", {"start": v(357.99, 228.6) * mm, "end": v(368.3, 228.6) * mm});
            skLineSegment(sketch, "E3.27.17.3", {"start": v(368.3, 228.6) * mm, "end": v(368.3, 238.91) * mm});
            skLineSegment(sketch, "E3.27.18.0", {"start": v(357.99, 241.3) * mm, "end": v(357.99, 251.61) * mm});
            skLineSegment(sketch, "E3.27.18.1", {"start": v(357.99, 251.61) * mm, "end": v(368.3, 251.61) * mm});
            skLineSegment(sketch, "E3.27.18.2", {"start": v(357.99, 241.3) * mm, "end": v(368.3, 241.3) * mm});
            skLineSegment(sketch, "E3.27.18.3", {"start": v(368.3, 241.3) * mm, "end": v(368.3, 251.61) * mm});
            skLineSegment(sketch, "E3.27.19.0", {"start": v(357.99, 254) * mm, "end": v(357.99, 264.31) * mm});
            skLineSegment(sketch, "E3.27.19.1", {"start": v(357.99, 264.31) * mm, "end": v(368.3, 264.31) * mm});
            skLineSegment(sketch, "E3.27.19.2", {"start": v(357.99, 254) * mm, "end": v(368.3, 254) * mm});
            skLineSegment(sketch, "E3.27.19.3", {"start": v(368.3, 254) * mm, "end": v(368.3, 264.31) * mm});
            skLineSegment(sketch, "E3.27.20.0", {"start": v(357.99, 266.7) * mm, "end": v(357.99, 277.01) * mm});
            skLineSegment(sketch, "E3.27.20.1", {"start": v(357.99, 277.01) * mm, "end": v(368.3, 277.01) * mm});
            skLineSegment(sketch, "E3.27.20.2", {"start": v(357.99, 266.7) * mm, "end": v(368.3, 266.7) * mm});
            skLineSegment(sketch, "E3.27.20.3", {"start": v(368.3, 266.7) * mm, "end": v(368.3, 277.01) * mm});
            skLineSegment(sketch, "E3.27.21.0", {"start": v(357.99, 279.4) * mm, "end": v(357.99, 289.71) * mm});
            skLineSegment(sketch, "E3.27.21.1", {"start": v(357.99, 289.71) * mm, "end": v(368.3, 289.71) * mm});
            skLineSegment(sketch, "E3.27.21.2", {"start": v(357.99, 279.4) * mm, "end": v(368.3, 279.4) * mm});
            skLineSegment(sketch, "E3.27.21.3", {"start": v(368.3, 279.4) * mm, "end": v(368.3, 289.71) * mm});
            skLineSegment(sketch, "E3.28.0.0", {"start": v(370.69, 12.7) * mm, "end": v(370.69, 23.01) * mm});
            skLineSegment(sketch, "E3.28.0.1", {"start": v(370.69, 23.01) * mm, "end": v(381, 23.01) * mm});
            skLineSegment(sketch, "E3.28.0.2", {"start": v(370.69, 12.7) * mm, "end": v(381, 12.7) * mm});
            skLineSegment(sketch, "E3.28.0.3", {"start": v(381, 12.7) * mm, "end": v(381, 23.01) * mm});
            skLineSegment(sketch, "E3.28.1.0", {"start": v(370.69, 25.4) * mm, "end": v(370.69, 35.71) * mm});
            skLineSegment(sketch, "E3.28.1.1", {"start": v(370.69, 35.71) * mm, "end": v(381, 35.71) * mm});
            skLineSegment(sketch, "E3.28.1.2", {"start": v(370.69, 25.4) * mm, "end": v(381, 25.4) * mm});
            skLineSegment(sketch, "E3.28.1.3", {"start": v(381, 25.4) * mm, "end": v(381, 35.71) * mm});
            skLineSegment(sketch, "E3.28.2.0", {"start": v(370.69, 38.1) * mm, "end": v(370.69, 48.41) * mm});
            skLineSegment(sketch, "E3.28.2.1", {"start": v(370.69, 48.41) * mm, "end": v(381, 48.41) * mm});
            skLineSegment(sketch, "E3.28.2.2", {"start": v(370.69, 38.1) * mm, "end": v(381, 38.1) * mm});
            skLineSegment(sketch, "E3.28.2.3", {"start": v(381, 38.1) * mm, "end": v(381, 48.41) * mm});
            skLineSegment(sketch, "E3.28.3.0", {"start": v(370.69, 50.8) * mm, "end": v(370.69, 61.11) * mm});
            skLineSegment(sketch, "E3.28.3.1", {"start": v(370.69, 61.11) * mm, "end": v(381, 61.11) * mm});
            skLineSegment(sketch, "E3.28.3.2", {"start": v(370.69, 50.8) * mm, "end": v(381, 50.8) * mm});
            skLineSegment(sketch, "E3.28.3.3", {"start": v(381, 50.8) * mm, "end": v(381, 61.11) * mm});
            skLineSegment(sketch, "E3.28.4.0", {"start": v(370.69, 63.5) * mm, "end": v(370.69, 73.81) * mm});
            skLineSegment(sketch, "E3.28.4.1", {"start": v(370.69, 73.81) * mm, "end": v(381, 73.81) * mm});
            skLineSegment(sketch, "E3.28.4.2", {"start": v(370.69, 63.5) * mm, "end": v(381, 63.5) * mm});
            skLineSegment(sketch, "E3.28.4.3", {"start": v(381, 63.5) * mm, "end": v(381, 73.81) * mm});
            skLineSegment(sketch, "E3.28.5.0", {"start": v(370.69, 76.2) * mm, "end": v(370.69, 86.51) * mm});
            skLineSegment(sketch, "E3.28.5.1", {"start": v(370.69, 86.51) * mm, "end": v(381, 86.51) * mm});
            skLineSegment(sketch, "E3.28.5.2", {"start": v(370.69, 76.2) * mm, "end": v(381, 76.2) * mm});
            skLineSegment(sketch, "E3.28.5.3", {"start": v(381, 76.2) * mm, "end": v(381, 86.51) * mm});
            skLineSegment(sketch, "E3.28.6.0", {"start": v(370.69, 88.9) * mm, "end": v(370.69, 99.21) * mm});
            skLineSegment(sketch, "E3.28.6.1", {"start": v(370.69, 99.21) * mm, "end": v(381, 99.21) * mm});
            skLineSegment(sketch, "E3.28.6.2", {"start": v(370.69, 88.9) * mm, "end": v(381, 88.9) * mm});
            skLineSegment(sketch, "E3.28.6.3", {"start": v(381, 88.9) * mm, "end": v(381, 99.21) * mm});
            skLineSegment(sketch, "E3.28.7.0", {"start": v(370.69, 101.6) * mm, "end": v(370.69, 111.91) * mm});
            skLineSegment(sketch, "E3.28.7.1", {"start": v(370.69, 111.91) * mm, "end": v(381, 111.91) * mm});
            skLineSegment(sketch, "E3.28.7.2", {"start": v(370.69, 101.6) * mm, "end": v(381, 101.6) * mm});
            skLineSegment(sketch, "E3.28.7.3", {"start": v(381, 101.6) * mm, "end": v(381, 111.91) * mm});
            skLineSegment(sketch, "E3.28.8.0", {"start": v(370.69, 114.3) * mm, "end": v(370.69, 124.61) * mm});
            skLineSegment(sketch, "E3.28.8.1", {"start": v(370.69, 124.61) * mm, "end": v(381, 124.61) * mm});
            skLineSegment(sketch, "E3.28.8.2", {"start": v(370.69, 114.3) * mm, "end": v(381, 114.3) * mm});
            skLineSegment(sketch, "E3.28.8.3", {"start": v(381, 114.3) * mm, "end": v(381, 124.61) * mm});
            skLineSegment(sketch, "E3.28.9.0", {"start": v(370.69, 127) * mm, "end": v(370.69, 137.31) * mm});
            skLineSegment(sketch, "E3.28.9.1", {"start": v(370.69, 137.31) * mm, "end": v(381, 137.31) * mm});
            skLineSegment(sketch, "E3.28.9.2", {"start": v(370.69, 127) * mm, "end": v(381, 127) * mm});
            skLineSegment(sketch, "E3.28.9.3", {"start": v(381, 127) * mm, "end": v(381, 137.31) * mm});
            skLineSegment(sketch, "E3.28.10.0", {"start": v(370.69, 139.7) * mm, "end": v(370.69, 150.01) * mm});
            skLineSegment(sketch, "E3.28.10.1", {"start": v(370.69, 150.01) * mm, "end": v(381, 150.01) * mm});
            skLineSegment(sketch, "E3.28.10.2", {"start": v(370.69, 139.7) * mm, "end": v(381, 139.7) * mm});
            skLineSegment(sketch, "E3.28.10.3", {"start": v(381, 139.7) * mm, "end": v(381, 150.01) * mm});
            skLineSegment(sketch, "E3.28.11.0", {"start": v(370.69, 152.4) * mm, "end": v(370.69, 162.71) * mm});
            skLineSegment(sketch, "E3.28.11.1", {"start": v(370.69, 162.71) * mm, "end": v(381, 162.71) * mm});
            skLineSegment(sketch, "E3.28.11.2", {"start": v(370.69, 152.4) * mm, "end": v(381, 152.4) * mm});
            skLineSegment(sketch, "E3.28.11.3", {"start": v(381, 152.4) * mm, "end": v(381, 162.71) * mm});
            skLineSegment(sketch, "E3.28.12.0", {"start": v(370.69, 165.1) * mm, "end": v(370.69, 175.41) * mm});
            skLineSegment(sketch, "E3.28.12.1", {"start": v(370.69, 175.41) * mm, "end": v(381, 175.41) * mm});
            skLineSegment(sketch, "E3.28.12.2", {"start": v(370.69, 165.1) * mm, "end": v(381, 165.1) * mm});
            skLineSegment(sketch, "E3.28.12.3", {"start": v(381, 165.1) * mm, "end": v(381, 175.41) * mm});
            skLineSegment(sketch, "E3.28.13.0", {"start": v(370.69, 177.8) * mm, "end": v(370.69, 188.11) * mm});
            skLineSegment(sketch, "E3.28.13.1", {"start": v(370.69, 188.11) * mm, "end": v(381, 188.11) * mm});
            skLineSegment(sketch, "E3.28.13.2", {"start": v(370.69, 177.8) * mm, "end": v(381, 177.8) * mm});
            skLineSegment(sketch, "E3.28.13.3", {"start": v(381, 177.8) * mm, "end": v(381, 188.11) * mm});
            skLineSegment(sketch, "E3.28.14.0", {"start": v(370.69, 190.5) * mm, "end": v(370.69, 200.81) * mm});
            skLineSegment(sketch, "E3.28.14.1", {"start": v(370.69, 200.81) * mm, "end": v(381, 200.81) * mm});
            skLineSegment(sketch, "E3.28.14.2", {"start": v(370.69, 190.5) * mm, "end": v(381, 190.5) * mm});
            skLineSegment(sketch, "E3.28.14.3", {"start": v(381, 190.5) * mm, "end": v(381, 200.81) * mm});
            skLineSegment(sketch, "E3.28.15.0", {"start": v(370.69, 203.2) * mm, "end": v(370.69, 213.51) * mm});
            skLineSegment(sketch, "E3.28.15.1", {"start": v(370.69, 213.51) * mm, "end": v(381, 213.51) * mm});
            skLineSegment(sketch, "E3.28.15.2", {"start": v(370.69, 203.2) * mm, "end": v(381, 203.2) * mm});
            skLineSegment(sketch, "E3.28.15.3", {"start": v(381, 203.2) * mm, "end": v(381, 213.51) * mm});
            skLineSegment(sketch, "E3.28.16.0", {"start": v(370.69, 215.9) * mm, "end": v(370.69, 226.21) * mm});
            skLineSegment(sketch, "E3.28.16.1", {"start": v(370.69, 226.21) * mm, "end": v(381, 226.21) * mm});
            skLineSegment(sketch, "E3.28.16.2", {"start": v(370.69, 215.9) * mm, "end": v(381, 215.9) * mm});
            skLineSegment(sketch, "E3.28.16.3", {"start": v(381, 215.9) * mm, "end": v(381, 226.21) * mm});
            skLineSegment(sketch, "E3.28.17.0", {"start": v(370.69, 228.6) * mm, "end": v(370.69, 238.91) * mm});
            skLineSegment(sketch, "E3.28.17.1", {"start": v(370.69, 238.91) * mm, "end": v(381, 238.91) * mm});
            skLineSegment(sketch, "E3.28.17.2", {"start": v(370.69, 228.6) * mm, "end": v(381, 228.6) * mm});
            skLineSegment(sketch, "E3.28.17.3", {"start": v(381, 228.6) * mm, "end": v(381, 238.91) * mm});
            skLineSegment(sketch, "E3.28.18.0", {"start": v(370.69, 241.3) * mm, "end": v(370.69, 251.61) * mm});
            skLineSegment(sketch, "E3.28.18.1", {"start": v(370.69, 251.61) * mm, "end": v(381, 251.61) * mm});
            skLineSegment(sketch, "E3.28.18.2", {"start": v(370.69, 241.3) * mm, "end": v(381, 241.3) * mm});
            skLineSegment(sketch, "E3.28.18.3", {"start": v(381, 241.3) * mm, "end": v(381, 251.61) * mm});
            skLineSegment(sketch, "E3.28.19.0", {"start": v(370.69, 254) * mm, "end": v(370.69, 264.31) * mm});
            skLineSegment(sketch, "E3.28.19.1", {"start": v(370.69, 264.31) * mm, "end": v(381, 264.31) * mm});
            skLineSegment(sketch, "E3.28.19.2", {"start": v(370.69, 254) * mm, "end": v(381, 254) * mm});
            skLineSegment(sketch, "E3.28.19.3", {"start": v(381, 254) * mm, "end": v(381, 264.31) * mm});
            skLineSegment(sketch, "E3.28.20.0", {"start": v(370.69, 266.7) * mm, "end": v(370.69, 277.01) * mm});
            skLineSegment(sketch, "E3.28.20.1", {"start": v(370.69, 277.01) * mm, "end": v(381, 277.01) * mm});
            skLineSegment(sketch, "E3.28.20.2", {"start": v(370.69, 266.7) * mm, "end": v(381, 266.7) * mm});
            skLineSegment(sketch, "E3.28.20.3", {"start": v(381, 266.7) * mm, "end": v(381, 277.01) * mm});
            skLineSegment(sketch, "E3.28.21.0", {"start": v(370.69, 279.4) * mm, "end": v(370.69, 289.71) * mm});
            skLineSegment(sketch, "E3.28.21.1", {"start": v(370.69, 289.71) * mm, "end": v(381, 289.71) * mm});
            skLineSegment(sketch, "E3.28.21.2", {"start": v(370.69, 279.4) * mm, "end": v(381, 279.4) * mm});
            skLineSegment(sketch, "E3.28.21.3", {"start": v(381, 279.4) * mm, "end": v(381, 289.71) * mm});
            skLineSegment(sketch, "E3.29.0.0", {"start": v(383.39, 12.7) * mm, "end": v(383.39, 23.01) * mm});
            skLineSegment(sketch, "E3.29.0.1", {"start": v(383.39, 23.01) * mm, "end": v(393.7, 23.01) * mm});
            skLineSegment(sketch, "E3.29.0.2", {"start": v(383.39, 12.7) * mm, "end": v(393.7, 12.7) * mm});
            skLineSegment(sketch, "E3.29.0.3", {"start": v(393.7, 12.7) * mm, "end": v(393.7, 23.01) * mm});
            skLineSegment(sketch, "E3.29.1.0", {"start": v(383.39, 25.4) * mm, "end": v(383.39, 35.71) * mm});
            skLineSegment(sketch, "E3.29.1.1", {"start": v(383.39, 35.71) * mm, "end": v(393.7, 35.71) * mm});
            skLineSegment(sketch, "E3.29.1.2", {"start": v(383.39, 25.4) * mm, "end": v(393.7, 25.4) * mm});
            skLineSegment(sketch, "E3.29.1.3", {"start": v(393.7, 25.4) * mm, "end": v(393.7, 35.71) * mm});
            skLineSegment(sketch, "E3.29.2.0", {"start": v(383.39, 38.1) * mm, "end": v(383.39, 48.41) * mm});
            skLineSegment(sketch, "E3.29.2.1", {"start": v(383.39, 48.41) * mm, "end": v(393.7, 48.41) * mm});
            skLineSegment(sketch, "E3.29.2.2", {"start": v(383.39, 38.1) * mm, "end": v(393.7, 38.1) * mm});
            skLineSegment(sketch, "E3.29.2.3", {"start": v(393.7, 38.1) * mm, "end": v(393.7, 48.41) * mm});
            skLineSegment(sketch, "E3.29.3.0", {"start": v(383.39, 50.8) * mm, "end": v(383.39, 61.11) * mm});
            skLineSegment(sketch, "E3.29.3.1", {"start": v(383.39, 61.11) * mm, "end": v(393.7, 61.11) * mm});
            skLineSegment(sketch, "E3.29.3.2", {"start": v(383.39, 50.8) * mm, "end": v(393.7, 50.8) * mm});
            skLineSegment(sketch, "E3.29.3.3", {"start": v(393.7, 50.8) * mm, "end": v(393.7, 61.11) * mm});
            skLineSegment(sketch, "E3.29.4.0", {"start": v(383.39, 63.5) * mm, "end": v(383.39, 73.81) * mm});
            skLineSegment(sketch, "E3.29.4.1", {"start": v(383.39, 73.81) * mm, "end": v(393.7, 73.81) * mm});
            skLineSegment(sketch, "E3.29.4.2", {"start": v(383.39, 63.5) * mm, "end": v(393.7, 63.5) * mm});
            skLineSegment(sketch, "E3.29.4.3", {"start": v(393.7, 63.5) * mm, "end": v(393.7, 73.81) * mm});
            skLineSegment(sketch, "E3.29.5.0", {"start": v(383.39, 76.2) * mm, "end": v(383.39, 86.51) * mm});
            skLineSegment(sketch, "E3.29.5.1", {"start": v(383.39, 86.51) * mm, "end": v(393.7, 86.51) * mm});
            skLineSegment(sketch, "E3.29.5.2", {"start": v(383.39, 76.2) * mm, "end": v(393.7, 76.2) * mm});
            skLineSegment(sketch, "E3.29.5.3", {"start": v(393.7, 76.2) * mm, "end": v(393.7, 86.51) * mm});
            skLineSegment(sketch, "E3.29.6.0", {"start": v(383.39, 88.9) * mm, "end": v(383.39, 99.21) * mm});
            skLineSegment(sketch, "E3.29.6.1", {"start": v(383.39, 99.21) * mm, "end": v(393.7, 99.21) * mm});
            skLineSegment(sketch, "E3.29.6.2", {"start": v(383.39, 88.9) * mm, "end": v(393.7, 88.9) * mm});
            skLineSegment(sketch, "E3.29.6.3", {"start": v(393.7, 88.9) * mm, "end": v(393.7, 99.21) * mm});
            skLineSegment(sketch, "E3.29.7.0", {"start": v(383.39, 101.6) * mm, "end": v(383.39, 111.91) * mm});
            skLineSegment(sketch, "E3.29.7.1", {"start": v(383.39, 111.91) * mm, "end": v(393.7, 111.91) * mm});
            skLineSegment(sketch, "E3.29.7.2", {"start": v(383.39, 101.6) * mm, "end": v(393.7, 101.6) * mm});
            skLineSegment(sketch, "E3.29.7.3", {"start": v(393.7, 101.6) * mm, "end": v(393.7, 111.91) * mm});
            skLineSegment(sketch, "E3.29.8.0", {"start": v(383.39, 114.3) * mm, "end": v(383.39, 124.61) * mm});
            skLineSegment(sketch, "E3.29.8.1", {"start": v(383.39, 124.61) * mm, "end": v(393.7, 124.61) * mm});
            skLineSegment(sketch, "E3.29.8.2", {"start": v(383.39, 114.3) * mm, "end": v(393.7, 114.3) * mm});
            skLineSegment(sketch, "E3.29.8.3", {"start": v(393.7, 114.3) * mm, "end": v(393.7, 124.61) * mm});
            skLineSegment(sketch, "E3.29.9.0", {"start": v(383.39, 127) * mm, "end": v(383.39, 137.31) * mm});
            skLineSegment(sketch, "E3.29.9.1", {"start": v(383.39, 137.31) * mm, "end": v(393.7, 137.31) * mm});
            skLineSegment(sketch, "E3.29.9.2", {"start": v(383.39, 127) * mm, "end": v(393.7, 127) * mm});
            skLineSegment(sketch, "E3.29.9.3", {"start": v(393.7, 127) * mm, "end": v(393.7, 137.31) * mm});
            skLineSegment(sketch, "E3.29.10.0", {"start": v(383.39, 139.7) * mm, "end": v(383.39, 150.01) * mm});
            skLineSegment(sketch, "E3.29.10.1", {"start": v(383.39, 150.01) * mm, "end": v(393.7, 150.01) * mm});
            skLineSegment(sketch, "E3.29.10.2", {"start": v(383.39, 139.7) * mm, "end": v(393.7, 139.7) * mm});
            skLineSegment(sketch, "E3.29.10.3", {"start": v(393.7, 139.7) * mm, "end": v(393.7, 150.01) * mm});
            skLineSegment(sketch, "E3.29.11.0", {"start": v(383.39, 152.4) * mm, "end": v(383.39, 162.71) * mm});
            skLineSegment(sketch, "E3.29.11.1", {"start": v(383.39, 162.71) * mm, "end": v(393.7, 162.71) * mm});
            skLineSegment(sketch, "E3.29.11.2", {"start": v(383.39, 152.4) * mm, "end": v(393.7, 152.4) * mm});
            skLineSegment(sketch, "E3.29.11.3", {"start": v(393.7, 152.4) * mm, "end": v(393.7, 162.71) * mm});
            skLineSegment(sketch, "E3.29.12.0", {"start": v(383.39, 165.1) * mm, "end": v(383.39, 175.41) * mm});
            skLineSegment(sketch, "E3.29.12.1", {"start": v(383.39, 175.41) * mm, "end": v(393.7, 175.41) * mm});
            skLineSegment(sketch, "E3.29.12.2", {"start": v(383.39, 165.1) * mm, "end": v(393.7, 165.1) * mm});
            skLineSegment(sketch, "E3.29.12.3", {"start": v(393.7, 165.1) * mm, "end": v(393.7, 175.41) * mm});
            skLineSegment(sketch, "E3.29.13.0", {"start": v(383.39, 177.8) * mm, "end": v(383.39, 188.11) * mm});
            skLineSegment(sketch, "E3.29.13.1", {"start": v(383.39, 188.11) * mm, "end": v(393.7, 188.11) * mm});
            skLineSegment(sketch, "E3.29.13.2", {"start": v(383.39, 177.8) * mm, "end": v(393.7, 177.8) * mm});
            skLineSegment(sketch, "E3.29.13.3", {"start": v(393.7, 177.8) * mm, "end": v(393.7, 188.11) * mm});
            skLineSegment(sketch, "E3.29.14.0", {"start": v(383.39, 190.5) * mm, "end": v(383.39, 200.81) * mm});
            skLineSegment(sketch, "E3.29.14.1", {"start": v(383.39, 200.81) * mm, "end": v(393.7, 200.81) * mm});
            skLineSegment(sketch, "E3.29.14.2", {"start": v(383.39, 190.5) * mm, "end": v(393.7, 190.5) * mm});
            skLineSegment(sketch, "E3.29.14.3", {"start": v(393.7, 190.5) * mm, "end": v(393.7, 200.81) * mm});
            skLineSegment(sketch, "E3.29.15.0", {"start": v(383.39, 203.2) * mm, "end": v(383.39, 213.51) * mm});
            skLineSegment(sketch, "E3.29.15.1", {"start": v(383.39, 213.51) * mm, "end": v(393.7, 213.51) * mm});
            skLineSegment(sketch, "E3.29.15.2", {"start": v(383.39, 203.2) * mm, "end": v(393.7, 203.2) * mm});
            skLineSegment(sketch, "E3.29.15.3", {"start": v(393.7, 203.2) * mm, "end": v(393.7, 213.51) * mm});
            skLineSegment(sketch, "E3.29.16.0", {"start": v(383.39, 215.9) * mm, "end": v(383.39, 226.21) * mm});
            skLineSegment(sketch, "E3.29.16.1", {"start": v(383.39, 226.21) * mm, "end": v(393.7, 226.21) * mm});
            skLineSegment(sketch, "E3.29.16.2", {"start": v(383.39, 215.9) * mm, "end": v(393.7, 215.9) * mm});
            skLineSegment(sketch, "E3.29.16.3", {"start": v(393.7, 215.9) * mm, "end": v(393.7, 226.21) * mm});
            skLineSegment(sketch, "E3.29.17.0", {"start": v(383.39, 228.6) * mm, "end": v(383.39, 238.91) * mm});
            skLineSegment(sketch, "E3.29.17.1", {"start": v(383.39, 238.91) * mm, "end": v(393.7, 238.91) * mm});
            skLineSegment(sketch, "E3.29.17.2", {"start": v(383.39, 228.6) * mm, "end": v(393.7, 228.6) * mm});
            skLineSegment(sketch, "E3.29.17.3", {"start": v(393.7, 228.6) * mm, "end": v(393.7, 238.91) * mm});
            skLineSegment(sketch, "E3.29.18.0", {"start": v(383.39, 241.3) * mm, "end": v(383.39, 251.61) * mm});
            skLineSegment(sketch, "E3.29.18.1", {"start": v(383.39, 251.61) * mm, "end": v(393.7, 251.61) * mm});
            skLineSegment(sketch, "E3.29.18.2", {"start": v(383.39, 241.3) * mm, "end": v(393.7, 241.3) * mm});
            skLineSegment(sketch, "E3.29.18.3", {"start": v(393.7, 241.3) * mm, "end": v(393.7, 251.61) * mm});
            skLineSegment(sketch, "E3.29.19.0", {"start": v(383.39, 254) * mm, "end": v(383.39, 264.31) * mm});
            skLineSegment(sketch, "E3.29.19.1", {"start": v(383.39, 264.31) * mm, "end": v(393.7, 264.31) * mm});
            skLineSegment(sketch, "E3.29.19.2", {"start": v(383.39, 254) * mm, "end": v(393.7, 254) * mm});
            skLineSegment(sketch, "E3.29.19.3", {"start": v(393.7, 254) * mm, "end": v(393.7, 264.31) * mm});
            skLineSegment(sketch, "E3.29.20.0", {"start": v(383.39, 266.7) * mm, "end": v(383.39, 277.01) * mm});
            skLineSegment(sketch, "E3.29.20.1", {"start": v(383.39, 277.01) * mm, "end": v(393.7, 277.01) * mm});
            skLineSegment(sketch, "E3.29.20.2", {"start": v(383.39, 266.7) * mm, "end": v(393.7, 266.7) * mm});
            skLineSegment(sketch, "E3.29.20.3", {"start": v(393.7, 266.7) * mm, "end": v(393.7, 277.01) * mm});
            skLineSegment(sketch, "E3.29.21.0", {"start": v(383.39, 279.4) * mm, "end": v(383.39, 289.71) * mm});
            skLineSegment(sketch, "E3.29.21.1", {"start": v(383.39, 289.71) * mm, "end": v(393.7, 289.71) * mm});
            skLineSegment(sketch, "E3.29.21.2", {"start": v(383.39, 279.4) * mm, "end": v(393.7, 279.4) * mm});
            skLineSegment(sketch, "E3.29.21.3", {"start": v(393.7, 279.4) * mm, "end": v(393.7, 289.71) * mm});
            skLineSegment(sketch, "E3.direction1", {"start": v(15.09, 15.09) * mm, "end": v(27.79, 15.09) * mm, "construction": true});
            skLineSegment(sketch, "E3.direction2", {"start": v(15.09, 15.09) * mm, "end": v(15.09, 27.79) * mm, "construction": true});
            skPoint(sketch, "E4.visualSharp", {"position": v(12.7, 10.31) * mm});
            skArc(sketch, "E4.filletArc", {"start": v(12.7, 11.5) * mm, "mid": v(13.05, 10.66) * mm, "end": v(13.9, 10.31) * mm});
            skPoint(sketch, "E5.visualSharp", {"position": v(396.09, 10.31) * mm});
            skArc(sketch, "E5.filletArc", {"start": v(394.9, 10.31) * mm, "mid": v(395.74, 10.66) * mm, "end": v(396.09, 11.5) * mm});
            skPoint(sketch, "E6.visualSharp", {"position": v(396.09, 292.1) * mm});
            skArc(sketch, "E6.filletArc", {"start": v(396.09, 290.9) * mm, "mid": v(395.74, 291.75) * mm, "end": v(394.9, 292.1) * mm});
            skPoint(sketch, "E7.visualSharp", {"position": v(12.7, 292.1) * mm});
            skArc(sketch, "E7.filletArc", {"start": v(13.9, 292.1) * mm, "mid": v(13.05, 291.75) * mm, "end": v(12.7, 290.9) * mm});
            skSolve(sketch);
        }
        {
            var Q0;
            Q0 = qSketchRegion(id + "F2", true);
            extrude(context, id + "F3", {"entities" : qUnion([Q0]), "operationType" : NewBodyOperationType.REMOVE, "oppositeDirection" : true, "depth" : 2.4 * mm});
        }
        {
            var Q0;
            Q0=makeQuery(id+"F3.boolean.opBoolean","COPY",FACE,{"derivedFrom":makeQuery(id+"F3.opExtrude","CAP_FACE",FACE,{"disambiguationData":[OSD([sQuery(id+"F2.wireOp",EDGE,"E1.bottom"),sQuery(id+"F2.wireOp",EDGE,"E1.top"),sQuery(id+"F2.wireOp",EDGE,"E1.left"),sQuery(id+"F2.wireOp",EDGE,"E1.right"),sQuery(id+"F2.wireOp",EDGE,"E2.bottom"),sQuery(id+"F2.wireOp",EDGE,"E2.top"),sQuery(id+"F2.wireOp",EDGE,"E2.left"),sQuery(id+"F2.wireOp",EDGE,"E2.right"),sQuery(id+"F2.wireOp",EDGE,"E3.0.1.0"),sQuery(id+"F2.wireOp",EDGE,"E3.0.1.1"),sQuery(id+"F2.wireOp",EDGE,"E3.0.1.2"),sQuery(id+"F2.wireOp",EDGE,"E3.0.1.3"),sQuery(id+"F2.wireOp",EDGE,"E3.0.2.0"),sQuery(id+"F2.wireOp",EDGE,"E3.0.2.1"),sQuery(id+"F2.wireOp",EDGE,"E3.0.2.2"),sQuery(id+"F2.wireOp",EDGE,"E3.0.2.3"),sQuery(id+"F2.wireOp",EDGE,"E3.0.3.0"),sQuery(id+"F2.wireOp",EDGE,"E3.0.3.1"),sQuery(id+"F2.wireOp",EDGE,"E3.0.3.2"),sQuery(id+"F2.wireOp",EDGE,"E3.0.3.3"),sQuery(id+"F2.wireOp",EDGE,"E3.0.4.0"),sQuery(id+"F2.wireOp",EDGE,"E3.0.4.1"),sQuery(id+"F2.wireOp",EDGE,"E3.0.4.2"),sQuery(id+"F2.wireOp",EDGE,"E3.0.4.3"),sQuery(id+"F2.wireOp",EDGE,"E3.0.5.0"),sQuery(id+"F2.wireOp",EDGE,"E3.0.5.1"),sQuery(id+"F2.wireOp",EDGE,"E3.0.5.2"),sQuery(id+"F2.wireOp",EDGE,"E3.0.5.3"),sQuery(id+"F2.wireOp",EDGE,"E3.0.6.0"),sQuery(id+"F2.wireOp",EDGE,"E3.0.6.1"),sQuery(id+"F2.wireOp",EDGE,"E3.0.6.2"),sQuery(id+"F2.wireOp",EDGE,"E3.0.6.3"),sQuery(id+"F2.wireOp",EDGE,"E3.0.7.0"),sQuery(id+"F2.wireOp",EDGE,"E3.0.7.1"),sQuery(id+"F2.wireOp",EDGE,"E3.0.7.2"),sQuery(id+"F2.wireOp",EDGE,"E3.0.7.3"),sQuery(id+"F2.wireOp",EDGE,"E3.0.8.0"),sQuery(id+"F2.wireOp",EDGE,"E3.0.8.1"),sQuery(id+"F2.wireOp",EDGE,"E3.0.8.2"),sQuery(id+"F2.wireOp",EDGE,"E3.0.8.3"),sQuery(id+"F2.wireOp",EDGE,"E3.0.9.0"),sQuery(id+"F2.wireOp",EDGE,"E3.0.9.1"),sQuery(id+"F2.wireOp",EDGE,"E3.0.9.2"),sQuery(id+"F2.wireOp",EDGE,"E3.0.9.3"),sQuery(id+"F2.wireOp",EDGE,"E3.0.10.0"),sQuery(id+"F2.wireOp",EDGE,"E3.0.10.1"),sQuery(id+"F2.wireOp",EDGE,"E3.0.10.2"),sQuery(id+"F2.wireOp",EDGE,"E3.0.10.3"),sQuery(id+"F2.wireOp",EDGE,"E3.0.11.0"),sQuery(id+"F2.wireOp",EDGE,"E3.0.11.1"),sQuery(id+"F2.wireOp",EDGE,"E3.0.11.2"),sQuery(id+"F2.wireOp",EDGE,"E3.0.11.3"),sQuery(id+"F2.wireOp",EDGE,"E3.0.12.0"),sQuery(id+"F2.wireOp",EDGE,"E3.0.12.1"),sQuery(id+"F2.wireOp",EDGE,"E3.0.12.2"),sQuery(id+"F2.wireOp",EDGE,"E3.0.12.3"),sQuery(id+"F2.wireOp",EDGE,"E3.0.13.0"),sQuery(id+"F2.wireOp",EDGE,"E3.0.13.1"),sQuery(id+"F2.wireOp",EDGE,"E3.0.13.2"),sQuery(id+"F2.wireOp",EDGE,"E3.0.13.3"),sQuery(id+"F2.wireOp",EDGE,"E3.0.14.0"),sQuery(id+"F2.wireOp",EDGE,"E3.0.14.1"),sQuery(id+"F2.wireOp",EDGE,"E3.0.14.2"),sQuery(id+"F2.wireOp",EDGE,"E3.0.14.3"),sQuery(id+"F2.wireOp",EDGE,"E3.0.15.0"),sQuery(id+"F2.wireOp",EDGE,"E3.0.15.1"),sQuery(id+"F2.wireOp",EDGE,"E3.0.15.2"),sQuery(id+"F2.wireOp",EDGE,"E3.0.15.3"),sQuery(id+"F2.wireOp",EDGE,"E3.0.16.0"),sQuery(id+"F2.wireOp",EDGE,"E3.0.16.1"),sQuery(id+"F2.wireOp",EDGE,"E3.0.16.2"),sQuery(id+"F2.wireOp",EDGE,"E3.0.16.3"),sQuery(id+"F2.wireOp",EDGE,"E3.0.17.0"),sQuery(id+"F2.wireOp",EDGE,"E3.0.17.1"),sQuery(id+"F2.wireOp",EDGE,"E3.0.17.2"),sQuery(id+"F2.wireOp",EDGE,"E3.0.17.3"),sQuery(id+"F2.wireOp",EDGE,"E3.0.18.0"),sQuery(id+"F2.wireOp",EDGE,"E3.0.18.1"),sQuery(id+"F2.wireOp",EDGE,"E3.0.18.2"),sQuery(id+"F2.wireOp",EDGE,"E3.0.18.3"),sQuery(id+"F2.wireOp",EDGE,"E3.0.19.0"),sQuery(id+"F2.wireOp",EDGE,"E3.0.19.1"),sQuery(id+"F2.wireOp",EDGE,"E3.0.19.2"),sQuery(id+"F2.wireOp",EDGE,"E3.0.19.3"),sQuery(id+"F2.wireOp",EDGE,"E3.0.20.0"),sQuery(id+"F2.wireOp",EDGE,"E3.0.20.1"),sQuery(id+"F2.wireOp",EDGE,"E3.0.20.2"),sQuery(id+"F2.wireOp",EDGE,"E3.0.20.3"),sQuery(id+"F2.wireOp",EDGE,"E3.0.21.0"),sQuery(id+"F2.wireOp",EDGE,"E3.0.21.1"),sQuery(id+"F2.wireOp",EDGE,"E3.0.21.2"),sQuery(id+"F2.wireOp",EDGE,"E3.0.21.3"),sQuery(id+"F2.wireOp",EDGE,"E3.1.0.0"),sQuery(id+"F2.wireOp",EDGE,"E3.1.0.1"),sQuery(id+"F2.wireOp",EDGE,"E3.1.0.2"),sQuery(id+"F2.wireOp",EDGE,"E3.1.0.3"),sQuery(id+"F2.wireOp",EDGE,"E3.1.1.0"),sQuery(id+"F2.wireOp",EDGE,"E3.1.1.1"),sQuery(id+"F2.wireOp",EDGE,"E3.1.1.2"),sQuery(id+"F2.wireOp",EDGE,"E3.1.1.3"),sQuery(id+"F2.wireOp",EDGE,"E3.1.2.0"),sQuery(id+"F2.wireOp",EDGE,"E3.1.2.1"),sQuery(id+"F2.wireOp",EDGE,"E3.1.2.2"),sQuery(id+"F2.wireOp",EDGE,"E3.1.2.3"),sQuery(id+"F2.wireOp",EDGE,"E3.1.3.0"),sQuery(id+"F2.wireOp",EDGE,"E3.1.3.1"),sQuery(id+"F2.wireOp",EDGE,"E3.1.3.2"),sQuery(id+"F2.wireOp",EDGE,"E3.1.3.3"),sQuery(id+"F2.wireOp",EDGE,"E3.1.4.0"),sQuery(id+"F2.wireOp",EDGE,"E3.1.4.1"),sQuery(id+"F2.wireOp",EDGE,"E3.1.4.2"),sQuery(id+"F2.wireOp",EDGE,"E3.1.4.3"),sQuery(id+"F2.wireOp",EDGE,"E3.1.5.0"),sQuery(id+"F2.wireOp",EDGE,"E3.1.5.1"),sQuery(id+"F2.wireOp",EDGE,"E3.1.5.2"),sQuery(id+"F2.wireOp",EDGE,"E3.1.5.3"),sQuery(id+"F2.wireOp",EDGE,"E3.1.6.0"),sQuery(id+"F2.wireOp",EDGE,"E3.1.6.1"),sQuery(id+"F2.wireOp",EDGE,"E3.1.6.2"),sQuery(id+"F2.wireOp",EDGE,"E3.1.6.3"),sQuery(id+"F2.wireOp",EDGE,"E3.1.7.0"),sQuery(id+"F2.wireOp",EDGE,"E3.1.7.1"),sQuery(id+"F2.wireOp",EDGE,"E3.1.7.2"),sQuery(id+"F2.wireOp",EDGE,"E3.1.7.3"),sQuery(id+"F2.wireOp",EDGE,"E3.1.8.0"),sQuery(id+"F2.wireOp",EDGE,"E3.1.8.1"),sQuery(id+"F2.wireOp",EDGE,"E3.1.8.2"),sQuery(id+"F2.wireOp",EDGE,"E3.1.8.3"),sQuery(id+"F2.wireOp",EDGE,"E3.1.9.0"),sQuery(id+"F2.wireOp",EDGE,"E3.1.9.1"),sQuery(id+"F2.wireOp",EDGE,"E3.1.9.2"),sQuery(id+"F2.wireOp",EDGE,"E3.1.9.3"),sQuery(id+"F2.wireOp",EDGE,"E3.1.10.0"),sQuery(id+"F2.wireOp",EDGE,"E3.1.10.1"),sQuery(id+"F2.wireOp",EDGE,"E3.1.10.2"),sQuery(id+"F2.wireOp",EDGE,"E3.1.10.3"),sQuery(id+"F2.wireOp",EDGE,"E3.1.11.0"),sQuery(id+"F2.wireOp",EDGE,"E3.1.11.1"),sQuery(id+"F2.wireOp",EDGE,"E3.1.11.2"),sQuery(id+"F2.wireOp",EDGE,"E3.1.11.3"),sQuery(id+"F2.wireOp",EDGE,"E3.1.12.0"),sQuery(id+"F2.wireOp",EDGE,"E3.1.12.1"),sQuery(id+"F2.wireOp",EDGE,"E3.1.12.2"),sQuery(id+"F2.wireOp",EDGE,"E3.1.12.3"),sQuery(id+"F2.wireOp",EDGE,"E3.1.13.0"),sQuery(id+"F2.wireOp",EDGE,"E3.1.13.1"),sQuery(id+"F2.wireOp",EDGE,"E3.1.13.2"),sQuery(id+"F2.wireOp",EDGE,"E3.1.13.3"),sQuery(id+"F2.wireOp",EDGE,"E3.1.14.0"),sQuery(id+"F2.wireOp",EDGE,"E3.1.14.1"),sQuery(id+"F2.wireOp",EDGE,"E3.1.14.2"),sQuery(id+"F2.wireOp",EDGE,"E3.1.14.3"),sQuery(id+"F2.wireOp",EDGE,"E3.1.15.0"),sQuery(id+"F2.wireOp",EDGE,"E3.1.15.1"),sQuery(id+"F2.wireOp",EDGE,"E3.1.15.2"),sQuery(id+"F2.wireOp",EDGE,"E3.1.15.3"),sQuery(id+"F2.wireOp",EDGE,"E3.1.16.0"),sQuery(id+"F2.wireOp",EDGE,"E3.1.16.1"),sQuery(id+"F2.wireOp",EDGE,"E3.1.16.2"),sQuery(id+"F2.wireOp",EDGE,"E3.1.16.3"),sQuery(id+"F2.wireOp",EDGE,"E3.1.17.0"),sQuery(id+"F2.wireOp",EDGE,"E3.1.17.1"),sQuery(id+"F2.wireOp",EDGE,"E3.1.17.2"),sQuery(id+"F2.wireOp",EDGE,"E3.1.17.3"),sQuery(id+"F2.wireOp",EDGE,"E3.1.18.0"),sQuery(id+"F2.wireOp",EDGE,"E3.1.18.1"),sQuery(id+"F2.wireOp",EDGE,"E3.1.18.2"),sQuery(id+"F2.wireOp",EDGE,"E3.1.18.3"),sQuery(id+"F2.wireOp",EDGE,"E3.1.19.0"),sQuery(id+"F2.wireOp",EDGE,"E3.1.19.1"),sQuery(id+"F2.wireOp",EDGE,"E3.1.19.2"),sQuery(id+"F2.wireOp",EDGE,"E3.1.19.3"),sQuery(id+"F2.wireOp",EDGE,"E3.1.20.0"),sQuery(id+"F2.wireOp",EDGE,"E3.1.20.1"),sQuery(id+"F2.wireOp",EDGE,"E3.1.20.2"),sQuery(id+"F2.wireOp",EDGE,"E3.1.20.3"),sQuery(id+"F2.wireOp",EDGE,"E3.1.21.0"),sQuery(id+"F2.wireOp",EDGE,"E3.1.21.1"),sQuery(id+"F2.wireOp",EDGE,"E3.1.21.2"),sQuery(id+"F2.wireOp",EDGE,"E3.1.21.3"),sQuery(id+"F2.wireOp",EDGE,"E3.2.0.0"),sQuery(id+"F2.wireOp",EDGE,"E3.2.0.1"),sQuery(id+"F2.wireOp",EDGE,"E3.2.0.2"),sQuery(id+"F2.wireOp",EDGE,"E3.2.0.3"),sQuery(id+"F2.wireOp",EDGE,"E3.2.1.0"),sQuery(id+"F2.wireOp",EDGE,"E3.2.1.1"),sQuery(id+"F2.wireOp",EDGE,"E3.2.1.2"),sQuery(id+"F2.wireOp",EDGE,"E3.2.1.3"),sQuery(id+"F2.wireOp",EDGE,"E3.2.2.0"),sQuery(id+"F2.wireOp",EDGE,"E3.2.2.1"),sQuery(id+"F2.wireOp",EDGE,"E3.2.2.2"),sQuery(id+"F2.wireOp",EDGE,"E3.2.2.3"),sQuery(id+"F2.wireOp",EDGE,"E3.2.3.0"),sQuery(id+"F2.wireOp",EDGE,"E3.2.3.1"),sQuery(id+"F2.wireOp",EDGE,"E3.2.3.2"),sQuery(id+"F2.wireOp",EDGE,"E3.2.3.3"),sQuery(id+"F2.wireOp",EDGE,"E3.2.4.0"),sQuery(id+"F2.wireOp",EDGE,"E3.2.4.1"),sQuery(id+"F2.wireOp",EDGE,"E3.2.4.2"),sQuery(id+"F2.wireOp",EDGE,"E3.2.4.3"),sQuery(id+"F2.wireOp",EDGE,"E3.2.5.0"),sQuery(id+"F2.wireOp",EDGE,"E3.2.5.1"),sQuery(id+"F2.wireOp",EDGE,"E3.2.5.2"),sQuery(id+"F2.wireOp",EDGE,"E3.2.5.3"),sQuery(id+"F2.wireOp",EDGE,"E3.2.6.0"),sQuery(id+"F2.wireOp",EDGE,"E3.2.6.1"),sQuery(id+"F2.wireOp",EDGE,"E3.2.6.2"),sQuery(id+"F2.wireOp",EDGE,"E3.2.6.3"),sQuery(id+"F2.wireOp",EDGE,"E3.2.7.0"),sQuery(id+"F2.wireOp",EDGE,"E3.2.7.1"),sQuery(id+"F2.wireOp",EDGE,"E3.2.7.2"),sQuery(id+"F2.wireOp",EDGE,"E3.2.7.3"),sQuery(id+"F2.wireOp",EDGE,"E3.2.8.0"),sQuery(id+"F2.wireOp",EDGE,"E3.2.8.1"),sQuery(id+"F2.wireOp",EDGE,"E3.2.8.2"),sQuery(id+"F2.wireOp",EDGE,"E3.2.8.3"),sQuery(id+"F2.wireOp",EDGE,"E3.2.9.0"),sQuery(id+"F2.wireOp",EDGE,"E3.2.9.1"),sQuery(id+"F2.wireOp",EDGE,"E3.2.9.2"),sQuery(id+"F2.wireOp",EDGE,"E3.2.9.3"),sQuery(id+"F2.wireOp",EDGE,"E3.2.10.0"),sQuery(id+"F2.wireOp",EDGE,"E3.2.10.1"),sQuery(id+"F2.wireOp",EDGE,"E3.2.10.2"),sQuery(id+"F2.wireOp",EDGE,"E3.2.10.3"),sQuery(id+"F2.wireOp",EDGE,"E3.2.11.0"),sQuery(id+"F2.wireOp",EDGE,"E3.2.11.1"),sQuery(id+"F2.wireOp",EDGE,"E3.2.11.2"),sQuery(id+"F2.wireOp",EDGE,"E3.2.11.3"),sQuery(id+"F2.wireOp",EDGE,"E3.2.12.0"),sQuery(id+"F2.wireOp",EDGE,"E3.2.12.1"),sQuery(id+"F2.wireOp",EDGE,"E3.2.12.2"),sQuery(id+"F2.wireOp",EDGE,"E3.2.12.3"),sQuery(id+"F2.wireOp",EDGE,"E3.2.13.0"),sQuery(id+"F2.wireOp",EDGE,"E3.2.13.1"),sQuery(id+"F2.wireOp",EDGE,"E3.2.13.2"),sQuery(id+"F2.wireOp",EDGE,"E3.2.13.3"),sQuery(id+"F2.wireOp",EDGE,"E3.2.14.0"),sQuery(id+"F2.wireOp",EDGE,"E3.2.14.1"),sQuery(id+"F2.wireOp",EDGE,"E3.2.14.2"),sQuery(id+"F2.wireOp",EDGE,"E3.2.14.3"),sQuery(id+"F2.wireOp",EDGE,"E3.2.15.0"),sQuery(id+"F2.wireOp",EDGE,"E3.2.15.1"),sQuery(id+"F2.wireOp",EDGE,"E3.2.15.2"),sQuery(id+"F2.wireOp",EDGE,"E3.2.15.3"),sQuery(id+"F2.wireOp",EDGE,"E3.2.16.0"),sQuery(id+"F2.wireOp",EDGE,"E3.2.16.1"),sQuery(id+"F2.wireOp",EDGE,"E3.2.16.2"),sQuery(id+"F2.wireOp",EDGE,"E3.2.16.3"),sQuery(id+"F2.wireOp",EDGE,"E3.2.17.0"),sQuery(id+"F2.wireOp",EDGE,"E3.2.17.1"),sQuery(id+"F2.wireOp",EDGE,"E3.2.17.2"),sQuery(id+"F2.wireOp",EDGE,"E3.2.17.3"),sQuery(id+"F2.wireOp",EDGE,"E3.2.18.0"),sQuery(id+"F2.wireOp",EDGE,"E3.2.18.1"),sQuery(id+"F2.wireOp",EDGE,"E3.2.18.2"),sQuery(id+"F2.wireOp",EDGE,"E3.2.18.3"),sQuery(id+"F2.wireOp",EDGE,"E3.2.19.0"),sQuery(id+"F2.wireOp",EDGE,"E3.2.19.1"),sQuery(id+"F2.wireOp",EDGE,"E3.2.19.2"),sQuery(id+"F2.wireOp",EDGE,"E3.2.19.3"),sQuery(id+"F2.wireOp",EDGE,"E3.2.20.0"),sQuery(id+"F2.wireOp",EDGE,"E3.2.20.1"),sQuery(id+"F2.wireOp",EDGE,"E3.2.20.2"),sQuery(id+"F2.wireOp",EDGE,"E3.2.20.3"),sQuery(id+"F2.wireOp",EDGE,"E3.2.21.0"),sQuery(id+"F2.wireOp",EDGE,"E3.2.21.1"),sQuery(id+"F2.wireOp",EDGE,"E3.2.21.2"),sQuery(id+"F2.wireOp",EDGE,"E3.2.21.3"),sQuery(id+"F2.wireOp",EDGE,"E3.3.0.0"),sQuery(id+"F2.wireOp",EDGE,"E3.3.0.1"),sQuery(id+"F2.wireOp",EDGE,"E3.3.0.2"),sQuery(id+"F2.wireOp",EDGE,"E3.3.0.3"),sQuery(id+"F2.wireOp",EDGE,"E3.3.1.0"),sQuery(id+"F2.wireOp",EDGE,"E3.3.1.1"),sQuery(id+"F2.wireOp",EDGE,"E3.3.1.2"),sQuery(id+"F2.wireOp",EDGE,"E3.3.1.3"),sQuery(id+"F2.wireOp",EDGE,"E3.3.2.0"),sQuery(id+"F2.wireOp",EDGE,"E3.3.2.1"),sQuery(id+"F2.wireOp",EDGE,"E3.3.2.2"),sQuery(id+"F2.wireOp",EDGE,"E3.3.2.3"),sQuery(id+"F2.wireOp",EDGE,"E3.3.3.0"),sQuery(id+"F2.wireOp",EDGE,"E3.3.3.1"),sQuery(id+"F2.wireOp",EDGE,"E3.3.3.2"),sQuery(id+"F2.wireOp",EDGE,"E3.3.3.3"),sQuery(id+"F2.wireOp",EDGE,"E3.3.4.0"),sQuery(id+"F2.wireOp",EDGE,"E3.3.4.1"),sQuery(id+"F2.wireOp",EDGE,"E3.3.4.2"),sQuery(id+"F2.wireOp",EDGE,"E3.3.4.3"),sQuery(id+"F2.wireOp",EDGE,"E3.3.5.0"),sQuery(id+"F2.wireOp",EDGE,"E3.3.5.1"),sQuery(id+"F2.wireOp",EDGE,"E3.3.5.2"),sQuery(id+"F2.wireOp",EDGE,"E3.3.5.3"),sQuery(id+"F2.wireOp",EDGE,"E3.3.6.0"),sQuery(id+"F2.wireOp",EDGE,"E3.3.6.1"),sQuery(id+"F2.wireOp",EDGE,"E3.3.6.2"),sQuery(id+"F2.wireOp",EDGE,"E3.3.6.3"),sQuery(id+"F2.wireOp",EDGE,"E3.3.7.0"),sQuery(id+"F2.wireOp",EDGE,"E3.3.7.1"),sQuery(id+"F2.wireOp",EDGE,"E3.3.7.2"),sQuery(id+"F2.wireOp",EDGE,"E3.3.7.3"),sQuery(id+"F2.wireOp",EDGE,"E3.3.8.0"),sQuery(id+"F2.wireOp",EDGE,"E3.3.8.1"),sQuery(id+"F2.wireOp",EDGE,"E3.3.8.2"),sQuery(id+"F2.wireOp",EDGE,"E3.3.8.3"),sQuery(id+"F2.wireOp",EDGE,"E3.3.9.0"),sQuery(id+"F2.wireOp",EDGE,"E3.3.9.1"),sQuery(id+"F2.wireOp",EDGE,"E3.3.9.2"),sQuery(id+"F2.wireOp",EDGE,"E3.3.9.3"),sQuery(id+"F2.wireOp",EDGE,"E3.3.10.0"),sQuery(id+"F2.wireOp",EDGE,"E3.3.10.1"),sQuery(id+"F2.wireOp",EDGE,"E3.3.10.2"),sQuery(id+"F2.wireOp",EDGE,"E3.3.10.3"),sQuery(id+"F2.wireOp",EDGE,"E3.3.11.0"),sQuery(id+"F2.wireOp",EDGE,"E3.3.11.1"),sQuery(id+"F2.wireOp",EDGE,"E3.3.11.2"),sQuery(id+"F2.wireOp",EDGE,"E3.3.11.3"),sQuery(id+"F2.wireOp",EDGE,"E3.3.12.0"),sQuery(id+"F2.wireOp",EDGE,"E3.3.12.1"),sQuery(id+"F2.wireOp",EDGE,"E3.3.12.2"),sQuery(id+"F2.wireOp",EDGE,"E3.3.12.3"),sQuery(id+"F2.wireOp",EDGE,"E3.3.13.0"),sQuery(id+"F2.wireOp",EDGE,"E3.3.13.1"),sQuery(id+"F2.wireOp",EDGE,"E3.3.13.2"),sQuery(id+"F2.wireOp",EDGE,"E3.3.13.3"),sQuery(id+"F2.wireOp",EDGE,"E3.3.14.0"),sQuery(id+"F2.wireOp",EDGE,"E3.3.14.1"),sQuery(id+"F2.wireOp",EDGE,"E3.3.14.2"),sQuery(id+"F2.wireOp",EDGE,"E3.3.14.3"),sQuery(id+"F2.wireOp",EDGE,"E3.3.15.0"),sQuery(id+"F2.wireOp",EDGE,"E3.3.15.1"),sQuery(id+"F2.wireOp",EDGE,"E3.3.15.2"),sQuery(id+"F2.wireOp",EDGE,"E3.3.15.3"),sQuery(id+"F2.wireOp",EDGE,"E3.3.16.0"),sQuery(id+"F2.wireOp",EDGE,"E3.3.16.1"),sQuery(id+"F2.wireOp",EDGE,"E3.3.16.2"),sQuery(id+"F2.wireOp",EDGE,"E3.3.16.3"),sQuery(id+"F2.wireOp",EDGE,"E3.3.17.0"),sQuery(id+"F2.wireOp",EDGE,"E3.3.17.1"),sQuery(id+"F2.wireOp",EDGE,"E3.3.17.2"),sQuery(id+"F2.wireOp",EDGE,"E3.3.17.3"),sQuery(id+"F2.wireOp",EDGE,"E3.3.18.0"),sQuery(id+"F2.wireOp",EDGE,"E3.3.18.1"),sQuery(id+"F2.wireOp",EDGE,"E3.3.18.2"),sQuery(id+"F2.wireOp",EDGE,"E3.3.18.3"),sQuery(id+"F2.wireOp",EDGE,"E3.3.19.0"),sQuery(id+"F2.wireOp",EDGE,"E3.3.19.1"),sQuery(id+"F2.wireOp",EDGE,"E3.3.19.2"),sQuery(id+"F2.wireOp",EDGE,"E3.3.19.3"),sQuery(id+"F2.wireOp",EDGE,"E3.3.20.0"),sQuery(id+"F2.wireOp",EDGE,"E3.3.20.1"),sQuery(id+"F2.wireOp",EDGE,"E3.3.20.2"),sQuery(id+"F2.wireOp",EDGE,"E3.3.20.3"),sQuery(id+"F2.wireOp",EDGE,"E3.3.21.0"),sQuery(id+"F2.wireOp",EDGE,"E3.3.21.1"),sQuery(id+"F2.wireOp",EDGE,"E3.3.21.2"),sQuery(id+"F2.wireOp",EDGE,"E3.3.21.3"),sQuery(id+"F2.wireOp",EDGE,"E3.4.0.0"),sQuery(id+"F2.wireOp",EDGE,"E3.4.0.1"),sQuery(id+"F2.wireOp",EDGE,"E3.4.0.2"),sQuery(id+"F2.wireOp",EDGE,"E3.4.0.3"),sQuery(id+"F2.wireOp",EDGE,"E3.4.1.0"),sQuery(id+"F2.wireOp",EDGE,"E3.4.1.1"),sQuery(id+"F2.wireOp",EDGE,"E3.4.1.2"),sQuery(id+"F2.wireOp",EDGE,"E3.4.1.3"),sQuery(id+"F2.wireOp",EDGE,"E3.4.2.0"),sQuery(id+"F2.wireOp",EDGE,"E3.4.2.1"),sQuery(id+"F2.wireOp",EDGE,"E3.4.2.2"),sQuery(id+"F2.wireOp",EDGE,"E3.4.2.3"),sQuery(id+"F2.wireOp",EDGE,"E3.4.3.0"),sQuery(id+"F2.wireOp",EDGE,"E3.4.3.1"),sQuery(id+"F2.wireOp",EDGE,"E3.4.3.2"),sQuery(id+"F2.wireOp",EDGE,"E3.4.3.3"),sQuery(id+"F2.wireOp",EDGE,"E3.4.4.0"),sQuery(id+"F2.wireOp",EDGE,"E3.4.4.1"),sQuery(id+"F2.wireOp",EDGE,"E3.4.4.2"),sQuery(id+"F2.wireOp",EDGE,"E3.4.4.3"),sQuery(id+"F2.wireOp",EDGE,"E3.4.5.0"),sQuery(id+"F2.wireOp",EDGE,"E3.4.5.1"),sQuery(id+"F2.wireOp",EDGE,"E3.4.5.2"),sQuery(id+"F2.wireOp",EDGE,"E3.4.5.3"),sQuery(id+"F2.wireOp",EDGE,"E3.4.6.0"),sQuery(id+"F2.wireOp",EDGE,"E3.4.6.1"),sQuery(id+"F2.wireOp",EDGE,"E3.4.6.2"),sQuery(id+"F2.wireOp",EDGE,"E3.4.6.3"),sQuery(id+"F2.wireOp",EDGE,"E3.4.7.0"),sQuery(id+"F2.wireOp",EDGE,"E3.4.7.1"),sQuery(id+"F2.wireOp",EDGE,"E3.4.7.2"),sQuery(id+"F2.wireOp",EDGE,"E3.4.7.3"),sQuery(id+"F2.wireOp",EDGE,"E3.4.8.0"),sQuery(id+"F2.wireOp",EDGE,"E3.4.8.1"),sQuery(id+"F2.wireOp",EDGE,"E3.4.8.2"),sQuery(id+"F2.wireOp",EDGE,"E3.4.8.3"),sQuery(id+"F2.wireOp",EDGE,"E3.4.9.0"),sQuery(id+"F2.wireOp",EDGE,"E3.4.9.1"),sQuery(id+"F2.wireOp",EDGE,"E3.4.9.2"),sQuery(id+"F2.wireOp",EDGE,"E3.4.9.3"),sQuery(id+"F2.wireOp",EDGE,"E3.4.10.0"),sQuery(id+"F2.wireOp",EDGE,"E3.4.10.1"),sQuery(id+"F2.wireOp",EDGE,"E3.4.10.2"),sQuery(id+"F2.wireOp",EDGE,"E3.4.10.3"),sQuery(id+"F2.wireOp",EDGE,"E3.4.11.0"),sQuery(id+"F2.wireOp",EDGE,"E3.4.11.1"),sQuery(id+"F2.wireOp",EDGE,"E3.4.11.2"),sQuery(id+"F2.wireOp",EDGE,"E3.4.11.3"),sQuery(id+"F2.wireOp",EDGE,"E3.4.12.0"),sQuery(id+"F2.wireOp",EDGE,"E3.4.12.1"),sQuery(id+"F2.wireOp",EDGE,"E3.4.12.2"),sQuery(id+"F2.wireOp",EDGE,"E3.4.12.3"),sQuery(id+"F2.wireOp",EDGE,"E3.4.13.0"),sQuery(id+"F2.wireOp",EDGE,"E3.4.13.1"),sQuery(id+"F2.wireOp",EDGE,"E3.4.13.2"),sQuery(id+"F2.wireOp",EDGE,"E3.4.13.3"),sQuery(id+"F2.wireOp",EDGE,"E3.4.14.0"),sQuery(id+"F2.wireOp",EDGE,"E3.4.14.1"),sQuery(id+"F2.wireOp",EDGE,"E3.4.14.2"),sQuery(id+"F2.wireOp",EDGE,"E3.4.14.3"),sQuery(id+"F2.wireOp",EDGE,"E3.4.15.0"),sQuery(id+"F2.wireOp",EDGE,"E3.4.15.1"),sQuery(id+"F2.wireOp",EDGE,"E3.4.15.2"),sQuery(id+"F2.wireOp",EDGE,"E3.4.15.3"),sQuery(id+"F2.wireOp",EDGE,"E3.4.16.0"),sQuery(id+"F2.wireOp",EDGE,"E3.4.16.1"),sQuery(id+"F2.wireOp",EDGE,"E3.4.16.2"),sQuery(id+"F2.wireOp",EDGE,"E3.4.16.3"),sQuery(id+"F2.wireOp",EDGE,"E3.4.17.0"),sQuery(id+"F2.wireOp",EDGE,"E3.4.17.1"),sQuery(id+"F2.wireOp",EDGE,"E3.4.17.2"),sQuery(id+"F2.wireOp",EDGE,"E3.4.17.3"),sQuery(id+"F2.wireOp",EDGE,"E3.4.18.0"),sQuery(id+"F2.wireOp",EDGE,"E3.4.18.1"),sQuery(id+"F2.wireOp",EDGE,"E3.4.18.2"),sQuery(id+"F2.wireOp",EDGE,"E3.4.18.3"),sQuery(id+"F2.wireOp",EDGE,"E3.4.19.0"),sQuery(id+"F2.wireOp",EDGE,"E3.4.19.1"),sQuery(id+"F2.wireOp",EDGE,"E3.4.19.2"),sQuery(id+"F2.wireOp",EDGE,"E3.4.19.3"),sQuery(id+"F2.wireOp",EDGE,"E3.4.20.0"),sQuery(id+"F2.wireOp",EDGE,"E3.4.20.1"),sQuery(id+"F2.wireOp",EDGE,"E3.4.20.2"),sQuery(id+"F2.wireOp",EDGE,"E3.4.20.3"),sQuery(id+"F2.wireOp",EDGE,"E3.4.21.0"),sQuery(id+"F2.wireOp",EDGE,"E3.4.21.1"),sQuery(id+"F2.wireOp",EDGE,"E3.4.21.2"),sQuery(id+"F2.wireOp",EDGE,"E3.4.21.3"),sQuery(id+"F2.wireOp",EDGE,"E3.5.0.0"),sQuery(id+"F2.wireOp",EDGE,"E3.5.0.1"),sQuery(id+"F2.wireOp",EDGE,"E3.5.0.2"),sQuery(id+"F2.wireOp",EDGE,"E3.5.0.3"),sQuery(id+"F2.wireOp",EDGE,"E3.5.1.0"),sQuery(id+"F2.wireOp",EDGE,"E3.5.1.1"),sQuery(id+"F2.wireOp",EDGE,"E3.5.1.2"),sQuery(id+"F2.wireOp",EDGE,"E3.5.1.3"),sQuery(id+"F2.wireOp",EDGE,"E3.5.2.0"),sQuery(id+"F2.wireOp",EDGE,"E3.5.2.1"),sQuery(id+"F2.wireOp",EDGE,"E3.5.2.2"),sQuery(id+"F2.wireOp",EDGE,"E3.5.2.3"),sQuery(id+"F2.wireOp",EDGE,"E3.5.3.0"),sQuery(id+"F2.wireOp",EDGE,"E3.5.3.1"),sQuery(id+"F2.wireOp",EDGE,"E3.5.3.2"),sQuery(id+"F2.wireOp",EDGE,"E3.5.3.3"),sQuery(id+"F2.wireOp",EDGE,"E3.5.4.0"),sQuery(id+"F2.wireOp",EDGE,"E3.5.4.1"),sQuery(id+"F2.wireOp",EDGE,"E3.5.4.2"),sQuery(id+"F2.wireOp",EDGE,"E3.5.4.3"),sQuery(id+"F2.wireOp",EDGE,"E3.5.5.0"),sQuery(id+"F2.wireOp",EDGE,"E3.5.5.1"),sQuery(id+"F2.wireOp",EDGE,"E3.5.5.2"),sQuery(id+"F2.wireOp",EDGE,"E3.5.5.3"),sQuery(id+"F2.wireOp",EDGE,"E3.5.6.0"),sQuery(id+"F2.wireOp",EDGE,"E3.5.6.1"),sQuery(id+"F2.wireOp",EDGE,"E3.5.6.2"),sQuery(id+"F2.wireOp",EDGE,"E3.5.6.3"),sQuery(id+"F2.wireOp",EDGE,"E3.5.7.0"),sQuery(id+"F2.wireOp",EDGE,"E3.5.7.1"),sQuery(id+"F2.wireOp",EDGE,"E3.5.7.2"),sQuery(id+"F2.wireOp",EDGE,"E3.5.7.3"),sQuery(id+"F2.wireOp",EDGE,"E3.5.8.0"),sQuery(id+"F2.wireOp",EDGE,"E3.5.8.1"),sQuery(id+"F2.wireOp",EDGE,"E3.5.8.2"),sQuery(id+"F2.wireOp",EDGE,"E3.5.8.3"),sQuery(id+"F2.wireOp",EDGE,"E3.5.9.0"),sQuery(id+"F2.wireOp",EDGE,"E3.5.9.1"),sQuery(id+"F2.wireOp",EDGE,"E3.5.9.2"),sQuery(id+"F2.wireOp",EDGE,"E3.5.9.3"),sQuery(id+"F2.wireOp",EDGE,"E3.5.10.0"),sQuery(id+"F2.wireOp",EDGE,"E3.5.10.1"),sQuery(id+"F2.wireOp",EDGE,"E3.5.10.2"),sQuery(id+"F2.wireOp",EDGE,"E3.5.10.3"),sQuery(id+"F2.wireOp",EDGE,"E3.5.11.0"),sQuery(id+"F2.wireOp",EDGE,"E3.5.11.1"),sQuery(id+"F2.wireOp",EDGE,"E3.5.11.2"),sQuery(id+"F2.wireOp",EDGE,"E3.5.11.3"),sQuery(id+"F2.wireOp",EDGE,"E3.5.12.0"),sQuery(id+"F2.wireOp",EDGE,"E3.5.12.1"),sQuery(id+"F2.wireOp",EDGE,"E3.5.12.2"),sQuery(id+"F2.wireOp",EDGE,"E3.5.12.3"),sQuery(id+"F2.wireOp",EDGE,"E3.5.13.0"),sQuery(id+"F2.wireOp",EDGE,"E3.5.13.1"),sQuery(id+"F2.wireOp",EDGE,"E3.5.13.2"),sQuery(id+"F2.wireOp",EDGE,"E3.5.13.3"),sQuery(id+"F2.wireOp",EDGE,"E3.5.14.0"),sQuery(id+"F2.wireOp",EDGE,"E3.5.14.1"),sQuery(id+"F2.wireOp",EDGE,"E3.5.14.2"),sQuery(id+"F2.wireOp",EDGE,"E3.5.14.3"),sQuery(id+"F2.wireOp",EDGE,"E3.5.15.0"),sQuery(id+"F2.wireOp",EDGE,"E3.5.15.1"),sQuery(id+"F2.wireOp",EDGE,"E3.5.15.2"),sQuery(id+"F2.wireOp",EDGE,"E3.5.15.3"),sQuery(id+"F2.wireOp",EDGE,"E3.5.16.0"),sQuery(id+"F2.wireOp",EDGE,"E3.5.16.1"),sQuery(id+"F2.wireOp",EDGE,"E3.5.16.2"),sQuery(id+"F2.wireOp",EDGE,"E3.5.16.3"),sQuery(id+"F2.wireOp",EDGE,"E3.5.17.0"),sQuery(id+"F2.wireOp",EDGE,"E3.5.17.1"),sQuery(id+"F2.wireOp",EDGE,"E3.5.17.2"),sQuery(id+"F2.wireOp",EDGE,"E3.5.17.3"),sQuery(id+"F2.wireOp",EDGE,"E3.5.18.0"),sQuery(id+"F2.wireOp",EDGE,"E3.5.18.1"),sQuery(id+"F2.wireOp",EDGE,"E3.5.18.2"),sQuery(id+"F2.wireOp",EDGE,"E3.5.18.3"),sQuery(id+"F2.wireOp",EDGE,"E3.5.19.0"),sQuery(id+"F2.wireOp",EDGE,"E3.5.19.1"),sQuery(id+"F2.wireOp",EDGE,"E3.5.19.2"),sQuery(id+"F2.wireOp",EDGE,"E3.5.19.3"),sQuery(id+"F2.wireOp",EDGE,"E3.5.20.0"),sQuery(id+"F2.wireOp",EDGE,"E3.5.20.1"),sQuery(id+"F2.wireOp",EDGE,"E3.5.20.2"),sQuery(id+"F2.wireOp",EDGE,"E3.5.20.3"),sQuery(id+"F2.wireOp",EDGE,"E3.5.21.0"),sQuery(id+"F2.wireOp",EDGE,"E3.5.21.1"),sQuery(id+"F2.wireOp",EDGE,"E3.5.21.2"),sQuery(id+"F2.wireOp",EDGE,"E3.5.21.3"),sQuery(id+"F2.wireOp",EDGE,"E3.6.0.0"),sQuery(id+"F2.wireOp",EDGE,"E3.6.0.1"),sQuery(id+"F2.wireOp",EDGE,"E3.6.0.2"),sQuery(id+"F2.wireOp",EDGE,"E3.6.0.3"),sQuery(id+"F2.wireOp",EDGE,"E3.6.1.0"),sQuery(id+"F2.wireOp",EDGE,"E3.6.1.1"),sQuery(id+"F2.wireOp",EDGE,"E3.6.1.2"),sQuery(id+"F2.wireOp",EDGE,"E3.6.1.3"),sQuery(id+"F2.wireOp",EDGE,"E3.6.2.0"),sQuery(id+"F2.wireOp",EDGE,"E3.6.2.1"),sQuery(id+"F2.wireOp",EDGE,"E3.6.2.2"),sQuery(id+"F2.wireOp",EDGE,"E3.6.2.3"),sQuery(id+"F2.wireOp",EDGE,"E3.6.3.0"),sQuery(id+"F2.wireOp",EDGE,"E3.6.3.1"),sQuery(id+"F2.wireOp",EDGE,"E3.6.3.2"),sQuery(id+"F2.wireOp",EDGE,"E3.6.3.3"),sQuery(id+"F2.wireOp",EDGE,"E3.6.4.0"),sQuery(id+"F2.wireOp",EDGE,"E3.6.4.1"),sQuery(id+"F2.wireOp",EDGE,"E3.6.4.2"),sQuery(id+"F2.wireOp",EDGE,"E3.6.4.3"),sQuery(id+"F2.wireOp",EDGE,"E3.6.5.0"),sQuery(id+"F2.wireOp",EDGE,"E3.6.5.1"),sQuery(id+"F2.wireOp",EDGE,"E3.6.5.2"),sQuery(id+"F2.wireOp",EDGE,"E3.6.5.3"),sQuery(id+"F2.wireOp",EDGE,"E3.6.6.0"),sQuery(id+"F2.wireOp",EDGE,"E3.6.6.1"),sQuery(id+"F2.wireOp",EDGE,"E3.6.6.2"),sQuery(id+"F2.wireOp",EDGE,"E3.6.6.3"),sQuery(id+"F2.wireOp",EDGE,"E3.6.7.0"),sQuery(id+"F2.wireOp",EDGE,"E3.6.7.1"),sQuery(id+"F2.wireOp",EDGE,"E3.6.7.2"),sQuery(id+"F2.wireOp",EDGE,"E3.6.7.3"),sQuery(id+"F2.wireOp",EDGE,"E3.6.8.0"),sQuery(id+"F2.wireOp",EDGE,"E3.6.8.1"),sQuery(id+"F2.wireOp",EDGE,"E3.6.8.2"),sQuery(id+"F2.wireOp",EDGE,"E3.6.8.3"),sQuery(id+"F2.wireOp",EDGE,"E3.6.9.0"),sQuery(id+"F2.wireOp",EDGE,"E3.6.9.1"),sQuery(id+"F2.wireOp",EDGE,"E3.6.9.2"),sQuery(id+"F2.wireOp",EDGE,"E3.6.9.3"),sQuery(id+"F2.wireOp",EDGE,"E3.6.10.0"),sQuery(id+"F2.wireOp",EDGE,"E3.6.10.1"),sQuery(id+"F2.wireOp",EDGE,"E3.6.10.2"),sQuery(id+"F2.wireOp",EDGE,"E3.6.10.3"),sQuery(id+"F2.wireOp",EDGE,"E3.6.11.0"),sQuery(id+"F2.wireOp",EDGE,"E3.6.11.1"),sQuery(id+"F2.wireOp",EDGE,"E3.6.11.2"),sQuery(id+"F2.wireOp",EDGE,"E3.6.11.3"),sQuery(id+"F2.wireOp",EDGE,"E3.6.12.0"),sQuery(id+"F2.wireOp",EDGE,"E3.6.12.1"),sQuery(id+"F2.wireOp",EDGE,"E3.6.12.2"),sQuery(id+"F2.wireOp",EDGE,"E3.6.12.3"),sQuery(id+"F2.wireOp",EDGE,"E3.6.13.0"),sQuery(id+"F2.wireOp",EDGE,"E3.6.13.1"),sQuery(id+"F2.wireOp",EDGE,"E3.6.13.2"),sQuery(id+"F2.wireOp",EDGE,"E3.6.13.3"),sQuery(id+"F2.wireOp",EDGE,"E3.6.14.0"),sQuery(id+"F2.wireOp",EDGE,"E3.6.14.1"),sQuery(id+"F2.wireOp",EDGE,"E3.6.14.2"),sQuery(id+"F2.wireOp",EDGE,"E3.6.14.3"),sQuery(id+"F2.wireOp",EDGE,"E3.6.15.0"),sQuery(id+"F2.wireOp",EDGE,"E3.6.15.1"),sQuery(id+"F2.wireOp",EDGE,"E3.6.15.2"),sQuery(id+"F2.wireOp",EDGE,"E3.6.15.3"),sQuery(id+"F2.wireOp",EDGE,"E3.6.16.0"),sQuery(id+"F2.wireOp",EDGE,"E3.6.16.1"),sQuery(id+"F2.wireOp",EDGE,"E3.6.16.2"),sQuery(id+"F2.wireOp",EDGE,"E3.6.16.3"),sQuery(id+"F2.wireOp",EDGE,"E3.6.17.0"),sQuery(id+"F2.wireOp",EDGE,"E3.6.17.1"),sQuery(id+"F2.wireOp",EDGE,"E3.6.17.2"),sQuery(id+"F2.wireOp",EDGE,"E3.6.17.3"),sQuery(id+"F2.wireOp",EDGE,"E3.6.18.0"),sQuery(id+"F2.wireOp",EDGE,"E3.6.18.1"),sQuery(id+"F2.wireOp",EDGE,"E3.6.18.2"),sQuery(id+"F2.wireOp",EDGE,"E3.6.18.3"),sQuery(id+"F2.wireOp",EDGE,"E3.6.19.0"),sQuery(id+"F2.wireOp",EDGE,"E3.6.19.1"),sQuery(id+"F2.wireOp",EDGE,"E3.6.19.2"),sQuery(id+"F2.wireOp",EDGE,"E3.6.19.3"),sQuery(id+"F2.wireOp",EDGE,"E3.6.20.0"),sQuery(id+"F2.wireOp",EDGE,"E3.6.20.1"),sQuery(id+"F2.wireOp",EDGE,"E3.6.20.2"),sQuery(id+"F2.wireOp",EDGE,"E3.6.20.3"),sQuery(id+"F2.wireOp",EDGE,"E3.6.21.0"),sQuery(id+"F2.wireOp",EDGE,"E3.6.21.1"),sQuery(id+"F2.wireOp",EDGE,"E3.6.21.2"),sQuery(id+"F2.wireOp",EDGE,"E3.6.21.3"),sQuery(id+"F2.wireOp",EDGE,"E3.7.0.0"),sQuery(id+"F2.wireOp",EDGE,"E3.7.0.1"),sQuery(id+"F2.wireOp",EDGE,"E3.7.0.2"),sQuery(id+"F2.wireOp",EDGE,"E3.7.0.3"),sQuery(id+"F2.wireOp",EDGE,"E3.7.1.0"),sQuery(id+"F2.wireOp",EDGE,"E3.7.1.1"),sQuery(id+"F2.wireOp",EDGE,"E3.7.1.2"),sQuery(id+"F2.wireOp",EDGE,"E3.7.1.3"),sQuery(id+"F2.wireOp",EDGE,"E3.7.2.0"),sQuery(id+"F2.wireOp",EDGE,"E3.7.2.1"),sQuery(id+"F2.wireOp",EDGE,"E3.7.2.2"),sQuery(id+"F2.wireOp",EDGE,"E3.7.2.3"),sQuery(id+"F2.wireOp",EDGE,"E3.7.3.0"),sQuery(id+"F2.wireOp",EDGE,"E3.7.3.1"),sQuery(id+"F2.wireOp",EDGE,"E3.7.3.2"),sQuery(id+"F2.wireOp",EDGE,"E3.7.3.3"),sQuery(id+"F2.wireOp",EDGE,"E3.7.4.0"),sQuery(id+"F2.wireOp",EDGE,"E3.7.4.1"),sQuery(id+"F2.wireOp",EDGE,"E3.7.4.2"),sQuery(id+"F2.wireOp",EDGE,"E3.7.4.3"),sQuery(id+"F2.wireOp",EDGE,"E3.7.5.0"),sQuery(id+"F2.wireOp",EDGE,"E3.7.5.1"),sQuery(id+"F2.wireOp",EDGE,"E3.7.5.2"),sQuery(id+"F2.wireOp",EDGE,"E3.7.5.3"),sQuery(id+"F2.wireOp",EDGE,"E3.7.6.0"),sQuery(id+"F2.wireOp",EDGE,"E3.7.6.1"),sQuery(id+"F2.wireOp",EDGE,"E3.7.6.2"),sQuery(id+"F2.wireOp",EDGE,"E3.7.6.3"),sQuery(id+"F2.wireOp",EDGE,"E3.7.7.0"),sQuery(id+"F2.wireOp",EDGE,"E3.7.7.1"),sQuery(id+"F2.wireOp",EDGE,"E3.7.7.2"),sQuery(id+"F2.wireOp",EDGE,"E3.7.7.3"),sQuery(id+"F2.wireOp",EDGE,"E3.7.8.0"),sQuery(id+"F2.wireOp",EDGE,"E3.7.8.1"),sQuery(id+"F2.wireOp",EDGE,"E3.7.8.2"),sQuery(id+"F2.wireOp",EDGE,"E3.7.8.3"),sQuery(id+"F2.wireOp",EDGE,"E3.7.9.0"),sQuery(id+"F2.wireOp",EDGE,"E3.7.9.1"),sQuery(id+"F2.wireOp",EDGE,"E3.7.9.2"),sQuery(id+"F2.wireOp",EDGE,"E3.7.9.3"),sQuery(id+"F2.wireOp",EDGE,"E3.7.10.0"),sQuery(id+"F2.wireOp",EDGE,"E3.7.10.1"),sQuery(id+"F2.wireOp",EDGE,"E3.7.10.2"),sQuery(id+"F2.wireOp",EDGE,"E3.7.10.3"),sQuery(id+"F2.wireOp",EDGE,"E3.7.11.0"),sQuery(id+"F2.wireOp",EDGE,"E3.7.11.1"),sQuery(id+"F2.wireOp",EDGE,"E3.7.11.2"),sQuery(id+"F2.wireOp",EDGE,"E3.7.11.3"),sQuery(id+"F2.wireOp",EDGE,"E3.7.12.0"),sQuery(id+"F2.wireOp",EDGE,"E3.7.12.1"),sQuery(id+"F2.wireOp",EDGE,"E3.7.12.2"),sQuery(id+"F2.wireOp",EDGE,"E3.7.12.3"),sQuery(id+"F2.wireOp",EDGE,"E3.7.13.0"),sQuery(id+"F2.wireOp",EDGE,"E3.7.13.1"),sQuery(id+"F2.wireOp",EDGE,"E3.7.13.2"),sQuery(id+"F2.wireOp",EDGE,"E3.7.13.3"),sQuery(id+"F2.wireOp",EDGE,"E3.7.14.0"),sQuery(id+"F2.wireOp",EDGE,"E3.7.14.1"),sQuery(id+"F2.wireOp",EDGE,"E3.7.14.2"),sQuery(id+"F2.wireOp",EDGE,"E3.7.14.3"),sQuery(id+"F2.wireOp",EDGE,"E3.7.15.0"),sQuery(id+"F2.wireOp",EDGE,"E3.7.15.1"),sQuery(id+"F2.wireOp",EDGE,"E3.7.15.2"),sQuery(id+"F2.wireOp",EDGE,"E3.7.15.3"),sQuery(id+"F2.wireOp",EDGE,"E3.7.16.0"),sQuery(id+"F2.wireOp",EDGE,"E3.7.16.1"),sQuery(id+"F2.wireOp",EDGE,"E3.7.16.2"),sQuery(id+"F2.wireOp",EDGE,"E3.7.16.3"),sQuery(id+"F2.wireOp",EDGE,"E3.7.17.0"),sQuery(id+"F2.wireOp",EDGE,"E3.7.17.1"),sQuery(id+"F2.wireOp",EDGE,"E3.7.17.2"),sQuery(id+"F2.wireOp",EDGE,"E3.7.17.3"),sQuery(id+"F2.wireOp",EDGE,"E3.7.18.0"),sQuery(id+"F2.wireOp",EDGE,"E3.7.18.1"),sQuery(id+"F2.wireOp",EDGE,"E3.7.18.2"),sQuery(id+"F2.wireOp",EDGE,"E3.7.18.3"),sQuery(id+"F2.wireOp",EDGE,"E3.7.19.0"),sQuery(id+"F2.wireOp",EDGE,"E3.7.19.1"),sQuery(id+"F2.wireOp",EDGE,"E3.7.19.2"),sQuery(id+"F2.wireOp",EDGE,"E3.7.19.3"),sQuery(id+"F2.wireOp",EDGE,"E3.7.20.0"),sQuery(id+"F2.wireOp",EDGE,"E3.7.20.1"),sQuery(id+"F2.wireOp",EDGE,"E3.7.20.2"),sQuery(id+"F2.wireOp",EDGE,"E3.7.20.3"),sQuery(id+"F2.wireOp",EDGE,"E3.7.21.0"),sQuery(id+"F2.wireOp",EDGE,"E3.7.21.1"),sQuery(id+"F2.wireOp",EDGE,"E3.7.21.2"),sQuery(id+"F2.wireOp",EDGE,"E3.7.21.3"),sQuery(id+"F2.wireOp",EDGE,"E3.8.0.0"),sQuery(id+"F2.wireOp",EDGE,"E3.8.0.1"),sQuery(id+"F2.wireOp",EDGE,"E3.8.0.2"),sQuery(id+"F2.wireOp",EDGE,"E3.8.0.3"),sQuery(id+"F2.wireOp",EDGE,"E3.8.1.0"),sQuery(id+"F2.wireOp",EDGE,"E3.8.1.1"),sQuery(id+"F2.wireOp",EDGE,"E3.8.1.2"),sQuery(id+"F2.wireOp",EDGE,"E3.8.1.3"),sQuery(id+"F2.wireOp",EDGE,"E3.8.2.0"),sQuery(id+"F2.wireOp",EDGE,"E3.8.2.1"),sQuery(id+"F2.wireOp",EDGE,"E3.8.2.2"),sQuery(id+"F2.wireOp",EDGE,"E3.8.2.3"),sQuery(id+"F2.wireOp",EDGE,"E3.8.3.0"),sQuery(id+"F2.wireOp",EDGE,"E3.8.3.1"),sQuery(id+"F2.wireOp",EDGE,"E3.8.3.2"),sQuery(id+"F2.wireOp",EDGE,"E3.8.3.3"),sQuery(id+"F2.wireOp",EDGE,"E3.8.4.0"),sQuery(id+"F2.wireOp",EDGE,"E3.8.4.1"),sQuery(id+"F2.wireOp",EDGE,"E3.8.4.2"),sQuery(id+"F2.wireOp",EDGE,"E3.8.4.3"),sQuery(id+"F2.wireOp",EDGE,"E3.8.5.0"),sQuery(id+"F2.wireOp",EDGE,"E3.8.5.1"),sQuery(id+"F2.wireOp",EDGE,"E3.8.5.2"),sQuery(id+"F2.wireOp",EDGE,"E3.8.5.3"),sQuery(id+"F2.wireOp",EDGE,"E3.8.6.0"),sQuery(id+"F2.wireOp",EDGE,"E3.8.6.1"),sQuery(id+"F2.wireOp",EDGE,"E3.8.6.2"),sQuery(id+"F2.wireOp",EDGE,"E3.8.6.3"),sQuery(id+"F2.wireOp",EDGE,"E3.8.7.0"),sQuery(id+"F2.wireOp",EDGE,"E3.8.7.1"),sQuery(id+"F2.wireOp",EDGE,"E3.8.7.2"),sQuery(id+"F2.wireOp",EDGE,"E3.8.7.3"),sQuery(id+"F2.wireOp",EDGE,"E3.8.8.0"),sQuery(id+"F2.wireOp",EDGE,"E3.8.8.1"),sQuery(id+"F2.wireOp",EDGE,"E3.8.8.2"),sQuery(id+"F2.wireOp",EDGE,"E3.8.8.3"),sQuery(id+"F2.wireOp",EDGE,"E3.8.9.0"),sQuery(id+"F2.wireOp",EDGE,"E3.8.9.1"),sQuery(id+"F2.wireOp",EDGE,"E3.8.9.2"),sQuery(id+"F2.wireOp",EDGE,"E3.8.9.3"),sQuery(id+"F2.wireOp",EDGE,"E3.8.10.0"),sQuery(id+"F2.wireOp",EDGE,"E3.8.10.1"),sQuery(id+"F2.wireOp",EDGE,"E3.8.10.2"),sQuery(id+"F2.wireOp",EDGE,"E3.8.10.3"),sQuery(id+"F2.wireOp",EDGE,"E3.8.11.0"),sQuery(id+"F2.wireOp",EDGE,"E3.8.11.1"),sQuery(id+"F2.wireOp",EDGE,"E3.8.11.2"),sQuery(id+"F2.wireOp",EDGE,"E3.8.11.3"),sQuery(id+"F2.wireOp",EDGE,"E3.8.12.0"),sQuery(id+"F2.wireOp",EDGE,"E3.8.12.1"),sQuery(id+"F2.wireOp",EDGE,"E3.8.12.2"),sQuery(id+"F2.wireOp",EDGE,"E3.8.12.3"),sQuery(id+"F2.wireOp",EDGE,"E3.8.13.0"),sQuery(id+"F2.wireOp",EDGE,"E3.8.13.1"),sQuery(id+"F2.wireOp",EDGE,"E3.8.13.2"),sQuery(id+"F2.wireOp",EDGE,"E3.8.13.3"),sQuery(id+"F2.wireOp",EDGE,"E3.8.14.0"),sQuery(id+"F2.wireOp",EDGE,"E3.8.14.1"),sQuery(id+"F2.wireOp",EDGE,"E3.8.14.2"),sQuery(id+"F2.wireOp",EDGE,"E3.8.14.3"),sQuery(id+"F2.wireOp",EDGE,"E3.8.15.0"),sQuery(id+"F2.wireOp",EDGE,"E3.8.15.1"),sQuery(id+"F2.wireOp",EDGE,"E3.8.15.2"),sQuery(id+"F2.wireOp",EDGE,"E3.8.15.3"),sQuery(id+"F2.wireOp",EDGE,"E3.8.16.0"),sQuery(id+"F2.wireOp",EDGE,"E3.8.16.1"),sQuery(id+"F2.wireOp",EDGE,"E3.8.16.2"),sQuery(id+"F2.wireOp",EDGE,"E3.8.16.3"),sQuery(id+"F2.wireOp",EDGE,"E3.8.17.0"),sQuery(id+"F2.wireOp",EDGE,"E3.8.17.1"),sQuery(id+"F2.wireOp",EDGE,"E3.8.17.2"),sQuery(id+"F2.wireOp",EDGE,"E3.8.17.3"),sQuery(id+"F2.wireOp",EDGE,"E3.8.18.0"),sQuery(id+"F2.wireOp",EDGE,"E3.8.18.1"),sQuery(id+"F2.wireOp",EDGE,"E3.8.18.2"),sQuery(id+"F2.wireOp",EDGE,"E3.8.18.3"),sQuery(id+"F2.wireOp",EDGE,"E3.8.19.0"),sQuery(id+"F2.wireOp",EDGE,"E3.8.19.1"),sQuery(id+"F2.wireOp",EDGE,"E3.8.19.2"),sQuery(id+"F2.wireOp",EDGE,"E3.8.19.3"),sQuery(id+"F2.wireOp",EDGE,"E3.8.20.0"),sQuery(id+"F2.wireOp",EDGE,"E3.8.20.1"),sQuery(id+"F2.wireOp",EDGE,"E3.8.20.2"),sQuery(id+"F2.wireOp",EDGE,"E3.8.20.3"),sQuery(id+"F2.wireOp",EDGE,"E3.8.21.0"),sQuery(id+"F2.wireOp",EDGE,"E3.8.21.1"),sQuery(id+"F2.wireOp",EDGE,"E3.8.21.2"),sQuery(id+"F2.wireOp",EDGE,"E3.8.21.3"),sQuery(id+"F2.wireOp",EDGE,"E3.9.0.0"),sQuery(id+"F2.wireOp",EDGE,"E3.9.0.1"),sQuery(id+"F2.wireOp",EDGE,"E3.9.0.2"),sQuery(id+"F2.wireOp",EDGE,"E3.9.0.3"),sQuery(id+"F2.wireOp",EDGE,"E3.9.1.0"),sQuery(id+"F2.wireOp",EDGE,"E3.9.1.1"),sQuery(id+"F2.wireOp",EDGE,"E3.9.1.2"),sQuery(id+"F2.wireOp",EDGE,"E3.9.1.3"),sQuery(id+"F2.wireOp",EDGE,"E3.9.2.0"),sQuery(id+"F2.wireOp",EDGE,"E3.9.2.1"),sQuery(id+"F2.wireOp",EDGE,"E3.9.2.2"),sQuery(id+"F2.wireOp",EDGE,"E3.9.2.3"),sQuery(id+"F2.wireOp",EDGE,"E3.9.3.0"),sQuery(id+"F2.wireOp",EDGE,"E3.9.3.1"),sQuery(id+"F2.wireOp",EDGE,"E3.9.3.2"),sQuery(id+"F2.wireOp",EDGE,"E3.9.3.3"),sQuery(id+"F2.wireOp",EDGE,"E3.9.4.0"),sQuery(id+"F2.wireOp",EDGE,"E3.9.4.1"),sQuery(id+"F2.wireOp",EDGE,"E3.9.4.2"),sQuery(id+"F2.wireOp",EDGE,"E3.9.4.3"),sQuery(id+"F2.wireOp",EDGE,"E3.9.5.0"),sQuery(id+"F2.wireOp",EDGE,"E3.9.5.1"),sQuery(id+"F2.wireOp",EDGE,"E3.9.5.2"),sQuery(id+"F2.wireOp",EDGE,"E3.9.5.3"),sQuery(id+"F2.wireOp",EDGE,"E3.9.6.0"),sQuery(id+"F2.wireOp",EDGE,"E3.9.6.1"),sQuery(id+"F2.wireOp",EDGE,"E3.9.6.2"),sQuery(id+"F2.wireOp",EDGE,"E3.9.6.3"),sQuery(id+"F2.wireOp",EDGE,"E3.9.7.0"),sQuery(id+"F2.wireOp",EDGE,"E3.9.7.1"),sQuery(id+"F2.wireOp",EDGE,"E3.9.7.2"),sQuery(id+"F2.wireOp",EDGE,"E3.9.7.3"),sQuery(id+"F2.wireOp",EDGE,"E3.9.8.0"),sQuery(id+"F2.wireOp",EDGE,"E3.9.8.1"),sQuery(id+"F2.wireOp",EDGE,"E3.9.8.2"),sQuery(id+"F2.wireOp",EDGE,"E3.9.8.3"),sQuery(id+"F2.wireOp",EDGE,"E3.9.9.0"),sQuery(id+"F2.wireOp",EDGE,"E3.9.9.1"),sQuery(id+"F2.wireOp",EDGE,"E3.9.9.2"),sQuery(id+"F2.wireOp",EDGE,"E3.9.9.3"),sQuery(id+"F2.wireOp",EDGE,"E3.9.10.0"),sQuery(id+"F2.wireOp",EDGE,"E3.9.10.1"),sQuery(id+"F2.wireOp",EDGE,"E3.9.10.2"),sQuery(id+"F2.wireOp",EDGE,"E3.9.10.3"),sQuery(id+"F2.wireOp",EDGE,"E3.9.11.0"),sQuery(id+"F2.wireOp",EDGE,"E3.9.11.1"),sQuery(id+"F2.wireOp",EDGE,"E3.9.11.2"),sQuery(id+"F2.wireOp",EDGE,"E3.9.11.3"),sQuery(id+"F2.wireOp",EDGE,"E3.9.12.0"),sQuery(id+"F2.wireOp",EDGE,"E3.9.12.1"),sQuery(id+"F2.wireOp",EDGE,"E3.9.12.2"),sQuery(id+"F2.wireOp",EDGE,"E3.9.12.3"),sQuery(id+"F2.wireOp",EDGE,"E3.9.13.0"),sQuery(id+"F2.wireOp",EDGE,"E3.9.13.1"),sQuery(id+"F2.wireOp",EDGE,"E3.9.13.2"),sQuery(id+"F2.wireOp",EDGE,"E3.9.13.3"),sQuery(id+"F2.wireOp",EDGE,"E3.9.14.0"),sQuery(id+"F2.wireOp",EDGE,"E3.9.14.1"),sQuery(id+"F2.wireOp",EDGE,"E3.9.14.2"),sQuery(id+"F2.wireOp",EDGE,"E3.9.14.3"),sQuery(id+"F2.wireOp",EDGE,"E3.9.15.0"),sQuery(id+"F2.wireOp",EDGE,"E3.9.15.1"),sQuery(id+"F2.wireOp",EDGE,"E3.9.15.2"),sQuery(id+"F2.wireOp",EDGE,"E3.9.15.3"),sQuery(id+"F2.wireOp",EDGE,"E3.9.16.0"),sQuery(id+"F2.wireOp",EDGE,"E3.9.16.1"),sQuery(id+"F2.wireOp",EDGE,"E3.9.16.2"),sQuery(id+"F2.wireOp",EDGE,"E3.9.16.3"),sQuery(id+"F2.wireOp",EDGE,"E3.9.17.0"),sQuery(id+"F2.wireOp",EDGE,"E3.9.17.1"),sQuery(id+"F2.wireOp",EDGE,"E3.9.17.2"),sQuery(id+"F2.wireOp",EDGE,"E3.9.17.3"),sQuery(id+"F2.wireOp",EDGE,"E3.9.18.0"),sQuery(id+"F2.wireOp",EDGE,"E3.9.18.1"),sQuery(id+"F2.wireOp",EDGE,"E3.9.18.2"),sQuery(id+"F2.wireOp",EDGE,"E3.9.18.3"),sQuery(id+"F2.wireOp",EDGE,"E3.9.19.0"),sQuery(id+"F2.wireOp",EDGE,"E3.9.19.1"),sQuery(id+"F2.wireOp",EDGE,"E3.9.19.2"),sQuery(id+"F2.wireOp",EDGE,"E3.9.19.3"),sQuery(id+"F2.wireOp",EDGE,"E3.9.20.0"),sQuery(id+"F2.wireOp",EDGE,"E3.9.20.1"),sQuery(id+"F2.wireOp",EDGE,"E3.9.20.2"),sQuery(id+"F2.wireOp",EDGE,"E3.9.20.3"),sQuery(id+"F2.wireOp",EDGE,"E3.9.21.0"),sQuery(id+"F2.wireOp",EDGE,"E3.9.21.1"),sQuery(id+"F2.wireOp",EDGE,"E3.9.21.2"),sQuery(id+"F2.wireOp",EDGE,"E3.9.21.3"),sQuery(id+"F2.wireOp",EDGE,"E3.10.0.0"),sQuery(id+"F2.wireOp",EDGE,"E3.10.0.1"),sQuery(id+"F2.wireOp",EDGE,"E3.10.0.2"),sQuery(id+"F2.wireOp",EDGE,"E3.10.0.3"),sQuery(id+"F2.wireOp",EDGE,"E3.10.1.0"),sQuery(id+"F2.wireOp",EDGE,"E3.10.1.1"),sQuery(id+"F2.wireOp",EDGE,"E3.10.1.2"),sQuery(id+"F2.wireOp",EDGE,"E3.10.1.3"),sQuery(id+"F2.wireOp",EDGE,"E3.10.2.0"),sQuery(id+"F2.wireOp",EDGE,"E3.10.2.1"),sQuery(id+"F2.wireOp",EDGE,"E3.10.2.2"),sQuery(id+"F2.wireOp",EDGE,"E3.10.2.3"),sQuery(id+"F2.wireOp",EDGE,"E3.10.3.0"),sQuery(id+"F2.wireOp",EDGE,"E3.10.3.1"),sQuery(id+"F2.wireOp",EDGE,"E3.10.3.2"),sQuery(id+"F2.wireOp",EDGE,"E3.10.3.3"),sQuery(id+"F2.wireOp",EDGE,"E3.10.4.0"),sQuery(id+"F2.wireOp",EDGE,"E3.10.4.1"),sQuery(id+"F2.wireOp",EDGE,"E3.10.4.2"),sQuery(id+"F2.wireOp",EDGE,"E3.10.4.3"),sQuery(id+"F2.wireOp",EDGE,"E3.10.5.0"),sQuery(id+"F2.wireOp",EDGE,"E3.10.5.1"),sQuery(id+"F2.wireOp",EDGE,"E3.10.5.2"),sQuery(id+"F2.wireOp",EDGE,"E3.10.5.3"),sQuery(id+"F2.wireOp",EDGE,"E3.10.6.0"),sQuery(id+"F2.wireOp",EDGE,"E3.10.6.1"),sQuery(id+"F2.wireOp",EDGE,"E3.10.6.2"),sQuery(id+"F2.wireOp",EDGE,"E3.10.6.3"),sQuery(id+"F2.wireOp",EDGE,"E3.10.7.0"),sQuery(id+"F2.wireOp",EDGE,"E3.10.7.1"),sQuery(id+"F2.wireOp",EDGE,"E3.10.7.2"),sQuery(id+"F2.wireOp",EDGE,"E3.10.7.3"),sQuery(id+"F2.wireOp",EDGE,"E3.10.8.0"),sQuery(id+"F2.wireOp",EDGE,"E3.10.8.1"),sQuery(id+"F2.wireOp",EDGE,"E3.10.8.2"),sQuery(id+"F2.wireOp",EDGE,"E3.10.8.3"),sQuery(id+"F2.wireOp",EDGE,"E3.10.9.0"),sQuery(id+"F2.wireOp",EDGE,"E3.10.9.1"),sQuery(id+"F2.wireOp",EDGE,"E3.10.9.2"),sQuery(id+"F2.wireOp",EDGE,"E3.10.9.3"),sQuery(id+"F2.wireOp",EDGE,"E3.10.10.0"),sQuery(id+"F2.wireOp",EDGE,"E3.10.10.1"),sQuery(id+"F2.wireOp",EDGE,"E3.10.10.2"),sQuery(id+"F2.wireOp",EDGE,"E3.10.10.3"),sQuery(id+"F2.wireOp",EDGE,"E3.10.11.0"),sQuery(id+"F2.wireOp",EDGE,"E3.10.11.1"),sQuery(id+"F2.wireOp",EDGE,"E3.10.11.2"),sQuery(id+"F2.wireOp",EDGE,"E3.10.11.3"),sQuery(id+"F2.wireOp",EDGE,"E3.10.12.0"),sQuery(id+"F2.wireOp",EDGE,"E3.10.12.1"),sQuery(id+"F2.wireOp",EDGE,"E3.10.12.2"),sQuery(id+"F2.wireOp",EDGE,"E3.10.12.3"),sQuery(id+"F2.wireOp",EDGE,"E3.10.13.0"),sQuery(id+"F2.wireOp",EDGE,"E3.10.13.1"),sQuery(id+"F2.wireOp",EDGE,"E3.10.13.2"),sQuery(id+"F2.wireOp",EDGE,"E3.10.13.3"),sQuery(id+"F2.wireOp",EDGE,"E3.10.14.0"),sQuery(id+"F2.wireOp",EDGE,"E3.10.14.1"),sQuery(id+"F2.wireOp",EDGE,"E3.10.14.2"),sQuery(id+"F2.wireOp",EDGE,"E3.10.14.3"),sQuery(id+"F2.wireOp",EDGE,"E3.10.15.0"),sQuery(id+"F2.wireOp",EDGE,"E3.10.15.1"),sQuery(id+"F2.wireOp",EDGE,"E3.10.15.2"),sQuery(id+"F2.wireOp",EDGE,"E3.10.15.3"),sQuery(id+"F2.wireOp",EDGE,"E3.10.16.0"),sQuery(id+"F2.wireOp",EDGE,"E3.10.16.1"),sQuery(id+"F2.wireOp",EDGE,"E3.10.16.2"),sQuery(id+"F2.wireOp",EDGE,"E3.10.16.3"),sQuery(id+"F2.wireOp",EDGE,"E3.10.17.0"),sQuery(id+"F2.wireOp",EDGE,"E3.10.17.1"),sQuery(id+"F2.wireOp",EDGE,"E3.10.17.2"),sQuery(id+"F2.wireOp",EDGE,"E3.10.17.3"),sQuery(id+"F2.wireOp",EDGE,"E3.10.18.0"),sQuery(id+"F2.wireOp",EDGE,"E3.10.18.1"),sQuery(id+"F2.wireOp",EDGE,"E3.10.18.2"),sQuery(id+"F2.wireOp",EDGE,"E3.10.18.3"),sQuery(id+"F2.wireOp",EDGE,"E3.10.19.0"),sQuery(id+"F2.wireOp",EDGE,"E3.10.19.1"),sQuery(id+"F2.wireOp",EDGE,"E3.10.19.2"),sQuery(id+"F2.wireOp",EDGE,"E3.10.19.3"),sQuery(id+"F2.wireOp",EDGE,"E3.10.20.0"),sQuery(id+"F2.wireOp",EDGE,"E3.10.20.1"),sQuery(id+"F2.wireOp",EDGE,"E3.10.20.2"),sQuery(id+"F2.wireOp",EDGE,"E3.10.20.3"),sQuery(id+"F2.wireOp",EDGE,"E3.10.21.0"),sQuery(id+"F2.wireOp",EDGE,"E3.10.21.1"),sQuery(id+"F2.wireOp",EDGE,"E3.10.21.2"),sQuery(id+"F2.wireOp",EDGE,"E3.10.21.3"),sQuery(id+"F2.wireOp",EDGE,"E3.11.0.0"),sQuery(id+"F2.wireOp",EDGE,"E3.11.0.1"),sQuery(id+"F2.wireOp",EDGE,"E3.11.0.2"),sQuery(id+"F2.wireOp",EDGE,"E3.11.0.3"),sQuery(id+"F2.wireOp",EDGE,"E3.11.1.0"),sQuery(id+"F2.wireOp",EDGE,"E3.11.1.1"),sQuery(id+"F2.wireOp",EDGE,"E3.11.1.2"),sQuery(id+"F2.wireOp",EDGE,"E3.11.1.3"),sQuery(id+"F2.wireOp",EDGE,"E3.11.2.0"),sQuery(id+"F2.wireOp",EDGE,"E3.11.2.1"),sQuery(id+"F2.wireOp",EDGE,"E3.11.2.2"),sQuery(id+"F2.wireOp",EDGE,"E3.11.2.3"),sQuery(id+"F2.wireOp",EDGE,"E3.11.3.0"),sQuery(id+"F2.wireOp",EDGE,"E3.11.3.1"),sQuery(id+"F2.wireOp",EDGE,"E3.11.3.2"),sQuery(id+"F2.wireOp",EDGE,"E3.11.3.3"),sQuery(id+"F2.wireOp",EDGE,"E3.11.4.0"),sQuery(id+"F2.wireOp",EDGE,"E3.11.4.1"),sQuery(id+"F2.wireOp",EDGE,"E3.11.4.2"),sQuery(id+"F2.wireOp",EDGE,"E3.11.4.3"),sQuery(id+"F2.wireOp",EDGE,"E3.11.5.0"),sQuery(id+"F2.wireOp",EDGE,"E3.11.5.1"),sQuery(id+"F2.wireOp",EDGE,"E3.11.5.2"),sQuery(id+"F2.wireOp",EDGE,"E3.11.5.3"),sQuery(id+"F2.wireOp",EDGE,"E3.11.6.0"),sQuery(id+"F2.wireOp",EDGE,"E3.11.6.1"),sQuery(id+"F2.wireOp",EDGE,"E3.11.6.2"),sQuery(id+"F2.wireOp",EDGE,"E3.11.6.3"),sQuery(id+"F2.wireOp",EDGE,"E3.11.7.0"),sQuery(id+"F2.wireOp",EDGE,"E3.11.7.1"),sQuery(id+"F2.wireOp",EDGE,"E3.11.7.2"),sQuery(id+"F2.wireOp",EDGE,"E3.11.7.3"),sQuery(id+"F2.wireOp",EDGE,"E3.11.8.0"),sQuery(id+"F2.wireOp",EDGE,"E3.11.8.1"),sQuery(id+"F2.wireOp",EDGE,"E3.11.8.2"),sQuery(id+"F2.wireOp",EDGE,"E3.11.8.3"),sQuery(id+"F2.wireOp",EDGE,"E3.11.9.0"),sQuery(id+"F2.wireOp",EDGE,"E3.11.9.1"),sQuery(id+"F2.wireOp",EDGE,"E3.11.9.2"),sQuery(id+"F2.wireOp",EDGE,"E3.11.9.3"),sQuery(id+"F2.wireOp",EDGE,"E3.11.10.0"),sQuery(id+"F2.wireOp",EDGE,"E3.11.10.1"),sQuery(id+"F2.wireOp",EDGE,"E3.11.10.2"),sQuery(id+"F2.wireOp",EDGE,"E3.11.10.3"),sQuery(id+"F2.wireOp",EDGE,"E3.11.11.0"),sQuery(id+"F2.wireOp",EDGE,"E3.11.11.1"),sQuery(id+"F2.wireOp",EDGE,"E3.11.11.2"),sQuery(id+"F2.wireOp",EDGE,"E3.11.11.3"),sQuery(id+"F2.wireOp",EDGE,"E3.11.12.0"),sQuery(id+"F2.wireOp",EDGE,"E3.11.12.1"),sQuery(id+"F2.wireOp",EDGE,"E3.11.12.2"),sQuery(id+"F2.wireOp",EDGE,"E3.11.12.3"),sQuery(id+"F2.wireOp",EDGE,"E3.11.13.0"),sQuery(id+"F2.wireOp",EDGE,"E3.11.13.1"),sQuery(id+"F2.wireOp",EDGE,"E3.11.13.2"),sQuery(id+"F2.wireOp",EDGE,"E3.11.13.3"),sQuery(id+"F2.wireOp",EDGE,"E3.11.14.0"),sQuery(id+"F2.wireOp",EDGE,"E3.11.14.1"),sQuery(id+"F2.wireOp",EDGE,"E3.11.14.2"),sQuery(id+"F2.wireOp",EDGE,"E3.11.14.3"),sQuery(id+"F2.wireOp",EDGE,"E3.11.15.0"),sQuery(id+"F2.wireOp",EDGE,"E3.11.15.1"),sQuery(id+"F2.wireOp",EDGE,"E3.11.15.2"),sQuery(id+"F2.wireOp",EDGE,"E3.11.15.3"),sQuery(id+"F2.wireOp",EDGE,"E3.11.16.0"),sQuery(id+"F2.wireOp",EDGE,"E3.11.16.1"),sQuery(id+"F2.wireOp",EDGE,"E3.11.16.2"),sQuery(id+"F2.wireOp",EDGE,"E3.11.16.3"),sQuery(id+"F2.wireOp",EDGE,"E3.11.17.0"),sQuery(id+"F2.wireOp",EDGE,"E3.11.17.1"),sQuery(id+"F2.wireOp",EDGE,"E3.11.17.2"),sQuery(id+"F2.wireOp",EDGE,"E3.11.17.3"),sQuery(id+"F2.wireOp",EDGE,"E3.11.18.0"),sQuery(id+"F2.wireOp",EDGE,"E3.11.18.1"),sQuery(id+"F2.wireOp",EDGE,"E3.11.18.2"),sQuery(id+"F2.wireOp",EDGE,"E3.11.18.3"),sQuery(id+"F2.wireOp",EDGE,"E3.11.19.0"),sQuery(id+"F2.wireOp",EDGE,"E3.11.19.1"),sQuery(id+"F2.wireOp",EDGE,"E3.11.19.2"),sQuery(id+"F2.wireOp",EDGE,"E3.11.19.3"),sQuery(id+"F2.wireOp",EDGE,"E3.11.20.0"),sQuery(id+"F2.wireOp",EDGE,"E3.11.20.1"),sQuery(id+"F2.wireOp",EDGE,"E3.11.20.2"),sQuery(id+"F2.wireOp",EDGE,"E3.11.20.3"),sQuery(id+"F2.wireOp",EDGE,"E3.11.21.0"),sQuery(id+"F2.wireOp",EDGE,"E3.11.21.1"),sQuery(id+"F2.wireOp",EDGE,"E3.11.21.2"),sQuery(id+"F2.wireOp",EDGE,"E3.11.21.3"),sQuery(id+"F2.wireOp",EDGE,"E3.12.0.0"),sQuery(id+"F2.wireOp",EDGE,"E3.12.0.1"),sQuery(id+"F2.wireOp",EDGE,"E3.12.0.2"),sQuery(id+"F2.wireOp",EDGE,"E3.12.0.3"),sQuery(id+"F2.wireOp",EDGE,"E3.12.1.0"),sQuery(id+"F2.wireOp",EDGE,"E3.12.1.1"),sQuery(id+"F2.wireOp",EDGE,"E3.12.1.2"),sQuery(id+"F2.wireOp",EDGE,"E3.12.1.3"),sQuery(id+"F2.wireOp",EDGE,"E3.12.2.0"),sQuery(id+"F2.wireOp",EDGE,"E3.12.2.1"),sQuery(id+"F2.wireOp",EDGE,"E3.12.2.2"),sQuery(id+"F2.wireOp",EDGE,"E3.12.2.3"),sQuery(id+"F2.wireOp",EDGE,"E3.12.3.0"),sQuery(id+"F2.wireOp",EDGE,"E3.12.3.1"),sQuery(id+"F2.wireOp",EDGE,"E3.12.3.2"),sQuery(id+"F2.wireOp",EDGE,"E3.12.3.3"),sQuery(id+"F2.wireOp",EDGE,"E3.12.4.0"),sQuery(id+"F2.wireOp",EDGE,"E3.12.4.1"),sQuery(id+"F2.wireOp",EDGE,"E3.12.4.2"),sQuery(id+"F2.wireOp",EDGE,"E3.12.4.3"),sQuery(id+"F2.wireOp",EDGE,"E3.12.5.0"),sQuery(id+"F2.wireOp",EDGE,"E3.12.5.1"),sQuery(id+"F2.wireOp",EDGE,"E3.12.5.2"),sQuery(id+"F2.wireOp",EDGE,"E3.12.5.3"),sQuery(id+"F2.wireOp",EDGE,"E3.12.6.0"),sQuery(id+"F2.wireOp",EDGE,"E3.12.6.1"),sQuery(id+"F2.wireOp",EDGE,"E3.12.6.2"),sQuery(id+"F2.wireOp",EDGE,"E3.12.6.3"),sQuery(id+"F2.wireOp",EDGE,"E3.12.7.0"),sQuery(id+"F2.wireOp",EDGE,"E3.12.7.1"),sQuery(id+"F2.wireOp",EDGE,"E3.12.7.2"),sQuery(id+"F2.wireOp",EDGE,"E3.12.7.3"),sQuery(id+"F2.wireOp",EDGE,"E3.12.8.0"),sQuery(id+"F2.wireOp",EDGE,"E3.12.8.1"),sQuery(id+"F2.wireOp",EDGE,"E3.12.8.2"),sQuery(id+"F2.wireOp",EDGE,"E3.12.8.3"),sQuery(id+"F2.wireOp",EDGE,"E3.12.9.0"),sQuery(id+"F2.wireOp",EDGE,"E3.12.9.1"),sQuery(id+"F2.wireOp",EDGE,"E3.12.9.2"),sQuery(id+"F2.wireOp",EDGE,"E3.12.9.3"),sQuery(id+"F2.wireOp",EDGE,"E3.12.10.0"),sQuery(id+"F2.wireOp",EDGE,"E3.12.10.1"),sQuery(id+"F2.wireOp",EDGE,"E3.12.10.2"),sQuery(id+"F2.wireOp",EDGE,"E3.12.10.3"),sQuery(id+"F2.wireOp",EDGE,"E3.12.11.0"),sQuery(id+"F2.wireOp",EDGE,"E3.12.11.1"),sQuery(id+"F2.wireOp",EDGE,"E3.12.11.2"),sQuery(id+"F2.wireOp",EDGE,"E3.12.11.3"),sQuery(id+"F2.wireOp",EDGE,"E3.12.12.0"),sQuery(id+"F2.wireOp",EDGE,"E3.12.12.1"),sQuery(id+"F2.wireOp",EDGE,"E3.12.12.2"),sQuery(id+"F2.wireOp",EDGE,"E3.12.12.3"),sQuery(id+"F2.wireOp",EDGE,"E3.12.13.0"),sQuery(id+"F2.wireOp",EDGE,"E3.12.13.1"),sQuery(id+"F2.wireOp",EDGE,"E3.12.13.2"),sQuery(id+"F2.wireOp",EDGE,"E3.12.13.3"),sQuery(id+"F2.wireOp",EDGE,"E3.12.14.0"),sQuery(id+"F2.wireOp",EDGE,"E3.12.14.1"),sQuery(id+"F2.wireOp",EDGE,"E3.12.14.2"),sQuery(id+"F2.wireOp",EDGE,"E3.12.14.3"),sQuery(id+"F2.wireOp",EDGE,"E3.12.15.0"),sQuery(id+"F2.wireOp",EDGE,"E3.12.15.1"),sQuery(id+"F2.wireOp",EDGE,"E3.12.15.2"),sQuery(id+"F2.wireOp",EDGE,"E3.12.15.3"),sQuery(id+"F2.wireOp",EDGE,"E3.12.16.0"),sQuery(id+"F2.wireOp",EDGE,"E3.12.16.1"),sQuery(id+"F2.wireOp",EDGE,"E3.12.16.2"),sQuery(id+"F2.wireOp",EDGE,"E3.12.16.3"),sQuery(id+"F2.wireOp",EDGE,"E3.12.17.0"),sQuery(id+"F2.wireOp",EDGE,"E3.12.17.1"),sQuery(id+"F2.wireOp",EDGE,"E3.12.17.2"),sQuery(id+"F2.wireOp",EDGE,"E3.12.17.3"),sQuery(id+"F2.wireOp",EDGE,"E3.12.18.0"),sQuery(id+"F2.wireOp",EDGE,"E3.12.18.1"),sQuery(id+"F2.wireOp",EDGE,"E3.12.18.2"),sQuery(id+"F2.wireOp",EDGE,"E3.12.18.3"),sQuery(id+"F2.wireOp",EDGE,"E3.12.19.0"),sQuery(id+"F2.wireOp",EDGE,"E3.12.19.1"),sQuery(id+"F2.wireOp",EDGE,"E3.12.19.2"),sQuery(id+"F2.wireOp",EDGE,"E3.12.19.3"),sQuery(id+"F2.wireOp",EDGE,"E3.12.20.0"),sQuery(id+"F2.wireOp",EDGE,"E3.12.20.1"),sQuery(id+"F2.wireOp",EDGE,"E3.12.20.2"),sQuery(id+"F2.wireOp",EDGE,"E3.12.20.3"),sQuery(id+"F2.wireOp",EDGE,"E3.12.21.0"),sQuery(id+"F2.wireOp",EDGE,"E3.12.21.1"),sQuery(id+"F2.wireOp",EDGE,"E3.12.21.2"),sQuery(id+"F2.wireOp",EDGE,"E3.12.21.3"),sQuery(id+"F2.wireOp",EDGE,"E3.13.0.0"),sQuery(id+"F2.wireOp",EDGE,"E3.13.0.1"),sQuery(id+"F2.wireOp",EDGE,"E3.13.0.2"),sQuery(id+"F2.wireOp",EDGE,"E3.13.0.3"),sQuery(id+"F2.wireOp",EDGE,"E3.13.1.0"),sQuery(id+"F2.wireOp",EDGE,"E3.13.1.1"),sQuery(id+"F2.wireOp",EDGE,"E3.13.1.2"),sQuery(id+"F2.wireOp",EDGE,"E3.13.1.3"),sQuery(id+"F2.wireOp",EDGE,"E3.13.2.0"),sQuery(id+"F2.wireOp",EDGE,"E3.13.2.1"),sQuery(id+"F2.wireOp",EDGE,"E3.13.2.2"),sQuery(id+"F2.wireOp",EDGE,"E3.13.2.3"),sQuery(id+"F2.wireOp",EDGE,"E3.13.3.0"),sQuery(id+"F2.wireOp",EDGE,"E3.13.3.1"),sQuery(id+"F2.wireOp",EDGE,"E3.13.3.2"),sQuery(id+"F2.wireOp",EDGE,"E3.13.3.3"),sQuery(id+"F2.wireOp",EDGE,"E3.13.4.0"),sQuery(id+"F2.wireOp",EDGE,"E3.13.4.1"),sQuery(id+"F2.wireOp",EDGE,"E3.13.4.2"),sQuery(id+"F2.wireOp",EDGE,"E3.13.4.3"),sQuery(id+"F2.wireOp",EDGE,"E3.13.5.0"),sQuery(id+"F2.wireOp",EDGE,"E3.13.5.1"),sQuery(id+"F2.wireOp",EDGE,"E3.13.5.2"),sQuery(id+"F2.wireOp",EDGE,"E3.13.5.3"),sQuery(id+"F2.wireOp",EDGE,"E3.13.6.0"),sQuery(id+"F2.wireOp",EDGE,"E3.13.6.1"),sQuery(id+"F2.wireOp",EDGE,"E3.13.6.2"),sQuery(id+"F2.wireOp",EDGE,"E3.13.6.3"),sQuery(id+"F2.wireOp",EDGE,"E3.13.7.0"),sQuery(id+"F2.wireOp",EDGE,"E3.13.7.1"),sQuery(id+"F2.wireOp",EDGE,"E3.13.7.2"),sQuery(id+"F2.wireOp",EDGE,"E3.13.7.3"),sQuery(id+"F2.wireOp",EDGE,"E3.13.8.0"),sQuery(id+"F2.wireOp",EDGE,"E3.13.8.1"),sQuery(id+"F2.wireOp",EDGE,"E3.13.8.2"),sQuery(id+"F2.wireOp",EDGE,"E3.13.8.3"),sQuery(id+"F2.wireOp",EDGE,"E3.13.9.0"),sQuery(id+"F2.wireOp",EDGE,"E3.13.9.1"),sQuery(id+"F2.wireOp",EDGE,"E3.13.9.2"),sQuery(id+"F2.wireOp",EDGE,"E3.13.9.3"),sQuery(id+"F2.wireOp",EDGE,"E3.13.10.0"),sQuery(id+"F2.wireOp",EDGE,"E3.13.10.1"),sQuery(id+"F2.wireOp",EDGE,"E3.13.10.2"),sQuery(id+"F2.wireOp",EDGE,"E3.13.10.3"),sQuery(id+"F2.wireOp",EDGE,"E3.13.11.0"),sQuery(id+"F2.wireOp",EDGE,"E3.13.11.1"),sQuery(id+"F2.wireOp",EDGE,"E3.13.11.2"),sQuery(id+"F2.wireOp",EDGE,"E3.13.11.3"),sQuery(id+"F2.wireOp",EDGE,"E3.13.12.0"),sQuery(id+"F2.wireOp",EDGE,"E3.13.12.1"),sQuery(id+"F2.wireOp",EDGE,"E3.13.12.2"),sQuery(id+"F2.wireOp",EDGE,"E3.13.12.3"),sQuery(id+"F2.wireOp",EDGE,"E3.13.13.0"),sQuery(id+"F2.wireOp",EDGE,"E3.13.13.1"),sQuery(id+"F2.wireOp",EDGE,"E3.13.13.2"),sQuery(id+"F2.wireOp",EDGE,"E3.13.13.3"),sQuery(id+"F2.wireOp",EDGE,"E3.13.14.0"),sQuery(id+"F2.wireOp",EDGE,"E3.13.14.1"),sQuery(id+"F2.wireOp",EDGE,"E3.13.14.2"),sQuery(id+"F2.wireOp",EDGE,"E3.13.14.3"),sQuery(id+"F2.wireOp",EDGE,"E3.13.15.0"),sQuery(id+"F2.wireOp",EDGE,"E3.13.15.1"),sQuery(id+"F2.wireOp",EDGE,"E3.13.15.2"),sQuery(id+"F2.wireOp",EDGE,"E3.13.15.3"),sQuery(id+"F2.wireOp",EDGE,"E3.13.16.0"),sQuery(id+"F2.wireOp",EDGE,"E3.13.16.1"),sQuery(id+"F2.wireOp",EDGE,"E3.13.16.2"),sQuery(id+"F2.wireOp",EDGE,"E3.13.16.3"),sQuery(id+"F2.wireOp",EDGE,"E3.13.17.0"),sQuery(id+"F2.wireOp",EDGE,"E3.13.17.1"),sQuery(id+"F2.wireOp",EDGE,"E3.13.17.2"),sQuery(id+"F2.wireOp",EDGE,"E3.13.17.3"),sQuery(id+"F2.wireOp",EDGE,"E3.13.18.0"),sQuery(id+"F2.wireOp",EDGE,"E3.13.18.1"),sQuery(id+"F2.wireOp",EDGE,"E3.13.18.2"),sQuery(id+"F2.wireOp",EDGE,"E3.13.18.3"),sQuery(id+"F2.wireOp",EDGE,"E3.13.19.0"),sQuery(id+"F2.wireOp",EDGE,"E3.13.19.1"),sQuery(id+"F2.wireOp",EDGE,"E3.13.19.2"),sQuery(id+"F2.wireOp",EDGE,"E3.13.19.3"),sQuery(id+"F2.wireOp",EDGE,"E3.13.20.0"),sQuery(id+"F2.wireOp",EDGE,"E3.13.20.1"),sQuery(id+"F2.wireOp",EDGE,"E3.13.20.2"),sQuery(id+"F2.wireOp",EDGE,"E3.13.20.3"),sQuery(id+"F2.wireOp",EDGE,"E3.13.21.0"),sQuery(id+"F2.wireOp",EDGE,"E3.13.21.1"),sQuery(id+"F2.wireOp",EDGE,"E3.13.21.2"),sQuery(id+"F2.wireOp",EDGE,"E3.13.21.3"),sQuery(id+"F2.wireOp",EDGE,"E3.14.0.0"),sQuery(id+"F2.wireOp",EDGE,"E3.14.0.1"),sQuery(id+"F2.wireOp",EDGE,"E3.14.0.2"),sQuery(id+"F2.wireOp",EDGE,"E3.14.0.3"),sQuery(id+"F2.wireOp",EDGE,"E3.14.1.0"),sQuery(id+"F2.wireOp",EDGE,"E3.14.1.1"),sQuery(id+"F2.wireOp",EDGE,"E3.14.1.2"),sQuery(id+"F2.wireOp",EDGE,"E3.14.1.3"),sQuery(id+"F2.wireOp",EDGE,"E3.14.2.0"),sQuery(id+"F2.wireOp",EDGE,"E3.14.2.1"),sQuery(id+"F2.wireOp",EDGE,"E3.14.2.2"),sQuery(id+"F2.wireOp",EDGE,"E3.14.2.3"),sQuery(id+"F2.wireOp",EDGE,"E3.14.3.0"),sQuery(id+"F2.wireOp",EDGE,"E3.14.3.1"),sQuery(id+"F2.wireOp",EDGE,"E3.14.3.2"),sQuery(id+"F2.wireOp",EDGE,"E3.14.3.3"),sQuery(id+"F2.wireOp",EDGE,"E3.14.4.0"),sQuery(id+"F2.wireOp",EDGE,"E3.14.4.1"),sQuery(id+"F2.wireOp",EDGE,"E3.14.4.2"),sQuery(id+"F2.wireOp",EDGE,"E3.14.4.3"),sQuery(id+"F2.wireOp",EDGE,"E3.14.5.0"),sQuery(id+"F2.wireOp",EDGE,"E3.14.5.1"),sQuery(id+"F2.wireOp",EDGE,"E3.14.5.2"),sQuery(id+"F2.wireOp",EDGE,"E3.14.5.3"),sQuery(id+"F2.wireOp",EDGE,"E3.14.6.0"),sQuery(id+"F2.wireOp",EDGE,"E3.14.6.1"),sQuery(id+"F2.wireOp",EDGE,"E3.14.6.2"),sQuery(id+"F2.wireOp",EDGE,"E3.14.6.3"),sQuery(id+"F2.wireOp",EDGE,"E3.14.7.0"),sQuery(id+"F2.wireOp",EDGE,"E3.14.7.1"),sQuery(id+"F2.wireOp",EDGE,"E3.14.7.2"),sQuery(id+"F2.wireOp",EDGE,"E3.14.7.3"),sQuery(id+"F2.wireOp",EDGE,"E3.14.8.0"),sQuery(id+"F2.wireOp",EDGE,"E3.14.8.1"),sQuery(id+"F2.wireOp",EDGE,"E3.14.8.2"),sQuery(id+"F2.wireOp",EDGE,"E3.14.8.3"),sQuery(id+"F2.wireOp",EDGE,"E3.14.9.0"),sQuery(id+"F2.wireOp",EDGE,"E3.14.9.1"),sQuery(id+"F2.wireOp",EDGE,"E3.14.9.2"),sQuery(id+"F2.wireOp",EDGE,"E3.14.9.3"),sQuery(id+"F2.wireOp",EDGE,"E3.14.10.0"),sQuery(id+"F2.wireOp",EDGE,"E3.14.10.1"),sQuery(id+"F2.wireOp",EDGE,"E3.14.10.2"),sQuery(id+"F2.wireOp",EDGE,"E3.14.10.3"),sQuery(id+"F2.wireOp",EDGE,"E3.14.11.0"),sQuery(id+"F2.wireOp",EDGE,"E3.14.11.1"),sQuery(id+"F2.wireOp",EDGE,"E3.14.11.2"),sQuery(id+"F2.wireOp",EDGE,"E3.14.11.3"),sQuery(id+"F2.wireOp",EDGE,"E3.14.12.0"),sQuery(id+"F2.wireOp",EDGE,"E3.14.12.1"),sQuery(id+"F2.wireOp",EDGE,"E3.14.12.2"),sQuery(id+"F2.wireOp",EDGE,"E3.14.12.3"),sQuery(id+"F2.wireOp",EDGE,"E3.14.13.0"),sQuery(id+"F2.wireOp",EDGE,"E3.14.13.1"),sQuery(id+"F2.wireOp",EDGE,"E3.14.13.2"),sQuery(id+"F2.wireOp",EDGE,"E3.14.13.3"),sQuery(id+"F2.wireOp",EDGE,"E3.14.14.0"),sQuery(id+"F2.wireOp",EDGE,"E3.14.14.1"),sQuery(id+"F2.wireOp",EDGE,"E3.14.14.2"),sQuery(id+"F2.wireOp",EDGE,"E3.14.14.3"),sQuery(id+"F2.wireOp",EDGE,"E3.14.15.0"),sQuery(id+"F2.wireOp",EDGE,"E3.14.15.1"),sQuery(id+"F2.wireOp",EDGE,"E3.14.15.2"),sQuery(id+"F2.wireOp",EDGE,"E3.14.15.3"),sQuery(id+"F2.wireOp",EDGE,"E3.14.16.0"),sQuery(id+"F2.wireOp",EDGE,"E3.14.16.1"),sQuery(id+"F2.wireOp",EDGE,"E3.14.16.2"),sQuery(id+"F2.wireOp",EDGE,"E3.14.16.3"),sQuery(id+"F2.wireOp",EDGE,"E3.14.17.0"),sQuery(id+"F2.wireOp",EDGE,"E3.14.17.1"),sQuery(id+"F2.wireOp",EDGE,"E3.14.17.2"),sQuery(id+"F2.wireOp",EDGE,"E3.14.17.3"),sQuery(id+"F2.wireOp",EDGE,"E3.14.18.0"),sQuery(id+"F2.wireOp",EDGE,"E3.14.18.1"),sQuery(id+"F2.wireOp",EDGE,"E3.14.18.2"),sQuery(id+"F2.wireOp",EDGE,"E3.14.18.3"),sQuery(id+"F2.wireOp",EDGE,"E3.14.19.0"),sQuery(id+"F2.wireOp",EDGE,"E3.14.19.1"),sQuery(id+"F2.wireOp",EDGE,"E3.14.19.2"),sQuery(id+"F2.wireOp",EDGE,"E3.14.19.3"),sQuery(id+"F2.wireOp",EDGE,"E3.14.20.0"),sQuery(id+"F2.wireOp",EDGE,"E3.14.20.1"),sQuery(id+"F2.wireOp",EDGE,"E3.14.20.2"),sQuery(id+"F2.wireOp",EDGE,"E3.14.20.3"),sQuery(id+"F2.wireOp",EDGE,"E3.14.21.0"),sQuery(id+"F2.wireOp",EDGE,"E3.14.21.1"),sQuery(id+"F2.wireOp",EDGE,"E3.14.21.2"),sQuery(id+"F2.wireOp",EDGE,"E3.14.21.3"),sQuery(id+"F2.wireOp",EDGE,"E3.15.0.0"),sQuery(id+"F2.wireOp",EDGE,"E3.15.0.1"),sQuery(id+"F2.wireOp",EDGE,"E3.15.0.2"),sQuery(id+"F2.wireOp",EDGE,"E3.15.0.3"),sQuery(id+"F2.wireOp",EDGE,"E3.15.1.0"),sQuery(id+"F2.wireOp",EDGE,"E3.15.1.1"),sQuery(id+"F2.wireOp",EDGE,"E3.15.1.2"),sQuery(id+"F2.wireOp",EDGE,"E3.15.1.3"),sQuery(id+"F2.wireOp",EDGE,"E3.15.2.0"),sQuery(id+"F2.wireOp",EDGE,"E3.15.2.1"),sQuery(id+"F2.wireOp",EDGE,"E3.15.2.2"),sQuery(id+"F2.wireOp",EDGE,"E3.15.2.3"),sQuery(id+"F2.wireOp",EDGE,"E3.15.3.0"),sQuery(id+"F2.wireOp",EDGE,"E3.15.3.1"),sQuery(id+"F2.wireOp",EDGE,"E3.15.3.2"),sQuery(id+"F2.wireOp",EDGE,"E3.15.3.3"),sQuery(id+"F2.wireOp",EDGE,"E3.15.4.0"),sQuery(id+"F2.wireOp",EDGE,"E3.15.4.1"),sQuery(id+"F2.wireOp",EDGE,"E3.15.4.2"),sQuery(id+"F2.wireOp",EDGE,"E3.15.4.3"),sQuery(id+"F2.wireOp",EDGE,"E3.15.5.0"),sQuery(id+"F2.wireOp",EDGE,"E3.15.5.1"),sQuery(id+"F2.wireOp",EDGE,"E3.15.5.2"),sQuery(id+"F2.wireOp",EDGE,"E3.15.5.3"),sQuery(id+"F2.wireOp",EDGE,"E3.15.6.0"),sQuery(id+"F2.wireOp",EDGE,"E3.15.6.1"),sQuery(id+"F2.wireOp",EDGE,"E3.15.6.2"),sQuery(id+"F2.wireOp",EDGE,"E3.15.6.3"),sQuery(id+"F2.wireOp",EDGE,"E3.15.7.0"),sQuery(id+"F2.wireOp",EDGE,"E3.15.7.1"),sQuery(id+"F2.wireOp",EDGE,"E3.15.7.2"),sQuery(id+"F2.wireOp",EDGE,"E3.15.7.3"),sQuery(id+"F2.wireOp",EDGE,"E3.15.8.0"),sQuery(id+"F2.wireOp",EDGE,"E3.15.8.1"),sQuery(id+"F2.wireOp",EDGE,"E3.15.8.2"),sQuery(id+"F2.wireOp",EDGE,"E3.15.8.3"),sQuery(id+"F2.wireOp",EDGE,"E3.15.9.0"),sQuery(id+"F2.wireOp",EDGE,"E3.15.9.1"),sQuery(id+"F2.wireOp",EDGE,"E3.15.9.2"),sQuery(id+"F2.wireOp",EDGE,"E3.15.9.3"),sQuery(id+"F2.wireOp",EDGE,"E3.15.10.0"),sQuery(id+"F2.wireOp",EDGE,"E3.15.10.1"),sQuery(id+"F2.wireOp",EDGE,"E3.15.10.2"),sQuery(id+"F2.wireOp",EDGE,"E3.15.10.3"),sQuery(id+"F2.wireOp",EDGE,"E3.15.11.0"),sQuery(id+"F2.wireOp",EDGE,"E3.15.11.1"),sQuery(id+"F2.wireOp",EDGE,"E3.15.11.2"),sQuery(id+"F2.wireOp",EDGE,"E3.15.11.3"),sQuery(id+"F2.wireOp",EDGE,"E3.15.12.0"),sQuery(id+"F2.wireOp",EDGE,"E3.15.12.1"),sQuery(id+"F2.wireOp",EDGE,"E3.15.12.2"),sQuery(id+"F2.wireOp",EDGE,"E3.15.12.3"),sQuery(id+"F2.wireOp",EDGE,"E3.15.13.0"),sQuery(id+"F2.wireOp",EDGE,"E3.15.13.1"),sQuery(id+"F2.wireOp",EDGE,"E3.15.13.2"),sQuery(id+"F2.wireOp",EDGE,"E3.15.13.3"),sQuery(id+"F2.wireOp",EDGE,"E3.15.14.0"),sQuery(id+"F2.wireOp",EDGE,"E3.15.14.1"),sQuery(id+"F2.wireOp",EDGE,"E3.15.14.2"),sQuery(id+"F2.wireOp",EDGE,"E3.15.14.3"),sQuery(id+"F2.wireOp",EDGE,"E3.15.15.0"),sQuery(id+"F2.wireOp",EDGE,"E3.15.15.1"),sQuery(id+"F2.wireOp",EDGE,"E3.15.15.2"),sQuery(id+"F2.wireOp",EDGE,"E3.15.15.3"),sQuery(id+"F2.wireOp",EDGE,"E3.15.16.0"),sQuery(id+"F2.wireOp",EDGE,"E3.15.16.1"),sQuery(id+"F2.wireOp",EDGE,"E3.15.16.2"),sQuery(id+"F2.wireOp",EDGE,"E3.15.16.3"),sQuery(id+"F2.wireOp",EDGE,"E3.15.17.0"),sQuery(id+"F2.wireOp",EDGE,"E3.15.17.1"),sQuery(id+"F2.wireOp",EDGE,"E3.15.17.2"),sQuery(id+"F2.wireOp",EDGE,"E3.15.17.3"),sQuery(id+"F2.wireOp",EDGE,"E3.15.18.0"),sQuery(id+"F2.wireOp",EDGE,"E3.15.18.1"),sQuery(id+"F2.wireOp",EDGE,"E3.15.18.2"),sQuery(id+"F2.wireOp",EDGE,"E3.15.18.3"),sQuery(id+"F2.wireOp",EDGE,"E3.15.19.0"),sQuery(id+"F2.wireOp",EDGE,"E3.15.19.1"),sQuery(id+"F2.wireOp",EDGE,"E3.15.19.2"),sQuery(id+"F2.wireOp",EDGE,"E3.15.19.3"),sQuery(id+"F2.wireOp",EDGE,"E3.15.20.0"),sQuery(id+"F2.wireOp",EDGE,"E3.15.20.1"),sQuery(id+"F2.wireOp",EDGE,"E3.15.20.2"),sQuery(id+"F2.wireOp",EDGE,"E3.15.20.3"),sQuery(id+"F2.wireOp",EDGE,"E3.15.21.0"),sQuery(id+"F2.wireOp",EDGE,"E3.15.21.1"),sQuery(id+"F2.wireOp",EDGE,"E3.15.21.2"),sQuery(id+"F2.wireOp",EDGE,"E3.15.21.3"),sQuery(id+"F2.wireOp",EDGE,"E3.16.0.0"),sQuery(id+"F2.wireOp",EDGE,"E3.16.0.1"),sQuery(id+"F2.wireOp",EDGE,"E3.16.0.2"),sQuery(id+"F2.wireOp",EDGE,"E3.16.0.3"),sQuery(id+"F2.wireOp",EDGE,"E3.16.1.0"),sQuery(id+"F2.wireOp",EDGE,"E3.16.1.1"),sQuery(id+"F2.wireOp",EDGE,"E3.16.1.2"),sQuery(id+"F2.wireOp",EDGE,"E3.16.1.3"),sQuery(id+"F2.wireOp",EDGE,"E3.16.2.0"),sQuery(id+"F2.wireOp",EDGE,"E3.16.2.1"),sQuery(id+"F2.wireOp",EDGE,"E3.16.2.2"),sQuery(id+"F2.wireOp",EDGE,"E3.16.2.3"),sQuery(id+"F2.wireOp",EDGE,"E3.16.3.0"),sQuery(id+"F2.wireOp",EDGE,"E3.16.3.1"),sQuery(id+"F2.wireOp",EDGE,"E3.16.3.2"),sQuery(id+"F2.wireOp",EDGE,"E3.16.3.3"),sQuery(id+"F2.wireOp",EDGE,"E3.16.4.0"),sQuery(id+"F2.wireOp",EDGE,"E3.16.4.1"),sQuery(id+"F2.wireOp",EDGE,"E3.16.4.2"),sQuery(id+"F2.wireOp",EDGE,"E3.16.4.3"),sQuery(id+"F2.wireOp",EDGE,"E3.16.5.0"),sQuery(id+"F2.wireOp",EDGE,"E3.16.5.1"),sQuery(id+"F2.wireOp",EDGE,"E3.16.5.2"),sQuery(id+"F2.wireOp",EDGE,"E3.16.5.3"),sQuery(id+"F2.wireOp",EDGE,"E3.16.6.0"),sQuery(id+"F2.wireOp",EDGE,"E3.16.6.1"),sQuery(id+"F2.wireOp",EDGE,"E3.16.6.2"),sQuery(id+"F2.wireOp",EDGE,"E3.16.6.3"),sQuery(id+"F2.wireOp",EDGE,"E3.16.7.0"),sQuery(id+"F2.wireOp",EDGE,"E3.16.7.1"),sQuery(id+"F2.wireOp",EDGE,"E3.16.7.2"),sQuery(id+"F2.wireOp",EDGE,"E3.16.7.3"),sQuery(id+"F2.wireOp",EDGE,"E3.16.8.0"),sQuery(id+"F2.wireOp",EDGE,"E3.16.8.1"),sQuery(id+"F2.wireOp",EDGE,"E3.16.8.2"),sQuery(id+"F2.wireOp",EDGE,"E3.16.8.3"),sQuery(id+"F2.wireOp",EDGE,"E3.16.9.0"),sQuery(id+"F2.wireOp",EDGE,"E3.16.9.1"),sQuery(id+"F2.wireOp",EDGE,"E3.16.9.2"),sQuery(id+"F2.wireOp",EDGE,"E3.16.9.3"),sQuery(id+"F2.wireOp",EDGE,"E3.16.10.0"),sQuery(id+"F2.wireOp",EDGE,"E3.16.10.1"),sQuery(id+"F2.wireOp",EDGE,"E3.16.10.2"),sQuery(id+"F2.wireOp",EDGE,"E3.16.10.3"),sQuery(id+"F2.wireOp",EDGE,"E3.16.11.0"),sQuery(id+"F2.wireOp",EDGE,"E3.16.11.1"),sQuery(id+"F2.wireOp",EDGE,"E3.16.11.2"),sQuery(id+"F2.wireOp",EDGE,"E3.16.11.3"),sQuery(id+"F2.wireOp",EDGE,"E3.16.12.0"),sQuery(id+"F2.wireOp",EDGE,"E3.16.12.1"),sQuery(id+"F2.wireOp",EDGE,"E3.16.12.2"),sQuery(id+"F2.wireOp",EDGE,"E3.16.12.3"),sQuery(id+"F2.wireOp",EDGE,"E3.16.13.0"),sQuery(id+"F2.wireOp",EDGE,"E3.16.13.1"),sQuery(id+"F2.wireOp",EDGE,"E3.16.13.2"),sQuery(id+"F2.wireOp",EDGE,"E3.16.13.3"),sQuery(id+"F2.wireOp",EDGE,"E3.16.14.0"),sQuery(id+"F2.wireOp",EDGE,"E3.16.14.1"),sQuery(id+"F2.wireOp",EDGE,"E3.16.14.2"),sQuery(id+"F2.wireOp",EDGE,"E3.16.14.3"),sQuery(id+"F2.wireOp",EDGE,"E3.16.15.0"),sQuery(id+"F2.wireOp",EDGE,"E3.16.15.1"),sQuery(id+"F2.wireOp",EDGE,"E3.16.15.2"),sQuery(id+"F2.wireOp",EDGE,"E3.16.15.3"),sQuery(id+"F2.wireOp",EDGE,"E3.16.16.0"),sQuery(id+"F2.wireOp",EDGE,"E3.16.16.1"),sQuery(id+"F2.wireOp",EDGE,"E3.16.16.2"),sQuery(id+"F2.wireOp",EDGE,"E3.16.16.3"),sQuery(id+"F2.wireOp",EDGE,"E3.16.17.0"),sQuery(id+"F2.wireOp",EDGE,"E3.16.17.1"),sQuery(id+"F2.wireOp",EDGE,"E3.16.17.2"),sQuery(id+"F2.wireOp",EDGE,"E3.16.17.3"),sQuery(id+"F2.wireOp",EDGE,"E3.16.18.0"),sQuery(id+"F2.wireOp",EDGE,"E3.16.18.1"),sQuery(id+"F2.wireOp",EDGE,"E3.16.18.2"),sQuery(id+"F2.wireOp",EDGE,"E3.16.18.3"),sQuery(id+"F2.wireOp",EDGE,"E3.16.19.0"),sQuery(id+"F2.wireOp",EDGE,"E3.16.19.1"),sQuery(id+"F2.wireOp",EDGE,"E3.16.19.2"),sQuery(id+"F2.wireOp",EDGE,"E3.16.19.3"),sQuery(id+"F2.wireOp",EDGE,"E3.16.20.0"),sQuery(id+"F2.wireOp",EDGE,"E3.16.20.1"),sQuery(id+"F2.wireOp",EDGE,"E3.16.20.2"),sQuery(id+"F2.wireOp",EDGE,"E3.16.20.3"),sQuery(id+"F2.wireOp",EDGE,"E3.16.21.0"),sQuery(id+"F2.wireOp",EDGE,"E3.16.21.1"),sQuery(id+"F2.wireOp",EDGE,"E3.16.21.2"),sQuery(id+"F2.wireOp",EDGE,"E3.16.21.3"),sQuery(id+"F2.wireOp",EDGE,"E3.17.0.0"),sQuery(id+"F2.wireOp",EDGE,"E3.17.0.1"),sQuery(id+"F2.wireOp",EDGE,"E3.17.0.2"),sQuery(id+"F2.wireOp",EDGE,"E3.17.0.3"),sQuery(id+"F2.wireOp",EDGE,"E3.17.1.0"),sQuery(id+"F2.wireOp",EDGE,"E3.17.1.1"),sQuery(id+"F2.wireOp",EDGE,"E3.17.1.2"),sQuery(id+"F2.wireOp",EDGE,"E3.17.1.3"),sQuery(id+"F2.wireOp",EDGE,"E3.17.2.0"),sQuery(id+"F2.wireOp",EDGE,"E3.17.2.1"),sQuery(id+"F2.wireOp",EDGE,"E3.17.2.2"),sQuery(id+"F2.wireOp",EDGE,"E3.17.2.3"),sQuery(id+"F2.wireOp",EDGE,"E3.17.3.0"),sQuery(id+"F2.wireOp",EDGE,"E3.17.3.1"),sQuery(id+"F2.wireOp",EDGE,"E3.17.3.2"),sQuery(id+"F2.wireOp",EDGE,"E3.17.3.3"),sQuery(id+"F2.wireOp",EDGE,"E3.17.4.0"),sQuery(id+"F2.wireOp",EDGE,"E3.17.4.1"),sQuery(id+"F2.wireOp",EDGE,"E3.17.4.2"),sQuery(id+"F2.wireOp",EDGE,"E3.17.4.3"),sQuery(id+"F2.wireOp",EDGE,"E3.17.5.0"),sQuery(id+"F2.wireOp",EDGE,"E3.17.5.1"),sQuery(id+"F2.wireOp",EDGE,"E3.17.5.2"),sQuery(id+"F2.wireOp",EDGE,"E3.17.5.3"),sQuery(id+"F2.wireOp",EDGE,"E3.17.6.0"),sQuery(id+"F2.wireOp",EDGE,"E3.17.6.1"),sQuery(id+"F2.wireOp",EDGE,"E3.17.6.2"),sQuery(id+"F2.wireOp",EDGE,"E3.17.6.3"),sQuery(id+"F2.wireOp",EDGE,"E3.17.7.0"),sQuery(id+"F2.wireOp",EDGE,"E3.17.7.1"),sQuery(id+"F2.wireOp",EDGE,"E3.17.7.2"),sQuery(id+"F2.wireOp",EDGE,"E3.17.7.3"),sQuery(id+"F2.wireOp",EDGE,"E3.17.8.0"),sQuery(id+"F2.wireOp",EDGE,"E3.17.8.1"),sQuery(id+"F2.wireOp",EDGE,"E3.17.8.2"),sQuery(id+"F2.wireOp",EDGE,"E3.17.8.3"),sQuery(id+"F2.wireOp",EDGE,"E3.17.9.0"),sQuery(id+"F2.wireOp",EDGE,"E3.17.9.1"),sQuery(id+"F2.wireOp",EDGE,"E3.17.9.2"),sQuery(id+"F2.wireOp",EDGE,"E3.17.9.3"),sQuery(id+"F2.wireOp",EDGE,"E3.17.10.0"),sQuery(id+"F2.wireOp",EDGE,"E3.17.10.1"),sQuery(id+"F2.wireOp",EDGE,"E3.17.10.2"),sQuery(id+"F2.wireOp",EDGE,"E3.17.10.3"),sQuery(id+"F2.wireOp",EDGE,"E3.17.11.0"),sQuery(id+"F2.wireOp",EDGE,"E3.17.11.1"),sQuery(id+"F2.wireOp",EDGE,"E3.17.11.2"),sQuery(id+"F2.wireOp",EDGE,"E3.17.11.3"),sQuery(id+"F2.wireOp",EDGE,"E3.17.12.0"),sQuery(id+"F2.wireOp",EDGE,"E3.17.12.1"),sQuery(id+"F2.wireOp",EDGE,"E3.17.12.2"),sQuery(id+"F2.wireOp",EDGE,"E3.17.12.3"),sQuery(id+"F2.wireOp",EDGE,"E3.17.13.0"),sQuery(id+"F2.wireOp",EDGE,"E3.17.13.1"),sQuery(id+"F2.wireOp",EDGE,"E3.17.13.2"),sQuery(id+"F2.wireOp",EDGE,"E3.17.13.3"),sQuery(id+"F2.wireOp",EDGE,"E3.17.14.0"),sQuery(id+"F2.wireOp",EDGE,"E3.17.14.1"),sQuery(id+"F2.wireOp",EDGE,"E3.17.14.2"),sQuery(id+"F2.wireOp",EDGE,"E3.17.14.3"),sQuery(id+"F2.wireOp",EDGE,"E3.17.15.0"),sQuery(id+"F2.wireOp",EDGE,"E3.17.15.1"),sQuery(id+"F2.wireOp",EDGE,"E3.17.15.2"),sQuery(id+"F2.wireOp",EDGE,"E3.17.15.3"),sQuery(id+"F2.wireOp",EDGE,"E3.17.16.0"),sQuery(id+"F2.wireOp",EDGE,"E3.17.16.1"),sQuery(id+"F2.wireOp",EDGE,"E3.17.16.2"),sQuery(id+"F2.wireOp",EDGE,"E3.17.16.3"),sQuery(id+"F2.wireOp",EDGE,"E3.17.17.0"),sQuery(id+"F2.wireOp",EDGE,"E3.17.17.1"),sQuery(id+"F2.wireOp",EDGE,"E3.17.17.2"),sQuery(id+"F2.wireOp",EDGE,"E3.17.17.3"),sQuery(id+"F2.wireOp",EDGE,"E3.17.18.0"),sQuery(id+"F2.wireOp",EDGE,"E3.17.18.1"),sQuery(id+"F2.wireOp",EDGE,"E3.17.18.2"),sQuery(id+"F2.wireOp",EDGE,"E3.17.18.3"),sQuery(id+"F2.wireOp",EDGE,"E3.17.19.0"),sQuery(id+"F2.wireOp",EDGE,"E3.17.19.1"),sQuery(id+"F2.wireOp",EDGE,"E3.17.19.2"),sQuery(id+"F2.wireOp",EDGE,"E3.17.19.3"),sQuery(id+"F2.wireOp",EDGE,"E3.17.20.0"),sQuery(id+"F2.wireOp",EDGE,"E3.17.20.1"),sQuery(id+"F2.wireOp",EDGE,"E3.17.20.2"),sQuery(id+"F2.wireOp",EDGE,"E3.17.20.3"),sQuery(id+"F2.wireOp",EDGE,"E3.17.21.0"),sQuery(id+"F2.wireOp",EDGE,"E3.17.21.1"),sQuery(id+"F2.wireOp",EDGE,"E3.17.21.2"),sQuery(id+"F2.wireOp",EDGE,"E3.17.21.3"),sQuery(id+"F2.wireOp",EDGE,"E3.18.0.0"),sQuery(id+"F2.wireOp",EDGE,"E3.18.0.1"),sQuery(id+"F2.wireOp",EDGE,"E3.18.0.2"),sQuery(id+"F2.wireOp",EDGE,"E3.18.0.3"),sQuery(id+"F2.wireOp",EDGE,"E3.18.1.0"),sQuery(id+"F2.wireOp",EDGE,"E3.18.1.1"),sQuery(id+"F2.wireOp",EDGE,"E3.18.1.2"),sQuery(id+"F2.wireOp",EDGE,"E3.18.1.3"),sQuery(id+"F2.wireOp",EDGE,"E3.18.2.0"),sQuery(id+"F2.wireOp",EDGE,"E3.18.2.1"),sQuery(id+"F2.wireOp",EDGE,"E3.18.2.2"),sQuery(id+"F2.wireOp",EDGE,"E3.18.2.3"),sQuery(id+"F2.wireOp",EDGE,"E3.18.3.0"),sQuery(id+"F2.wireOp",EDGE,"E3.18.3.1"),sQuery(id+"F2.wireOp",EDGE,"E3.18.3.2"),sQuery(id+"F2.wireOp",EDGE,"E3.18.3.3"),sQuery(id+"F2.wireOp",EDGE,"E3.18.4.0"),sQuery(id+"F2.wireOp",EDGE,"E3.18.4.1"),sQuery(id+"F2.wireOp",EDGE,"E3.18.4.2"),sQuery(id+"F2.wireOp",EDGE,"E3.18.4.3"),sQuery(id+"F2.wireOp",EDGE,"E3.18.5.0"),sQuery(id+"F2.wireOp",EDGE,"E3.18.5.1"),sQuery(id+"F2.wireOp",EDGE,"E3.18.5.2"),sQuery(id+"F2.wireOp",EDGE,"E3.18.5.3"),sQuery(id+"F2.wireOp",EDGE,"E3.18.6.0"),sQuery(id+"F2.wireOp",EDGE,"E3.18.6.1"),sQuery(id+"F2.wireOp",EDGE,"E3.18.6.2"),sQuery(id+"F2.wireOp",EDGE,"E3.18.6.3"),sQuery(id+"F2.wireOp",EDGE,"E3.18.7.0"),sQuery(id+"F2.wireOp",EDGE,"E3.18.7.1"),sQuery(id+"F2.wireOp",EDGE,"E3.18.7.2"),sQuery(id+"F2.wireOp",EDGE,"E3.18.7.3"),sQuery(id+"F2.wireOp",EDGE,"E3.18.8.0"),sQuery(id+"F2.wireOp",EDGE,"E3.18.8.1"),sQuery(id+"F2.wireOp",EDGE,"E3.18.8.2"),sQuery(id+"F2.wireOp",EDGE,"E3.18.8.3"),sQuery(id+"F2.wireOp",EDGE,"E3.18.9.0"),sQuery(id+"F2.wireOp",EDGE,"E3.18.9.1"),sQuery(id+"F2.wireOp",EDGE,"E3.18.9.2"),sQuery(id+"F2.wireOp",EDGE,"E3.18.9.3"),sQuery(id+"F2.wireOp",EDGE,"E3.18.10.0"),sQuery(id+"F2.wireOp",EDGE,"E3.18.10.1"),sQuery(id+"F2.wireOp",EDGE,"E3.18.10.2"),sQuery(id+"F2.wireOp",EDGE,"E3.18.10.3"),sQuery(id+"F2.wireOp",EDGE,"E3.18.11.0"),sQuery(id+"F2.wireOp",EDGE,"E3.18.11.1"),sQuery(id+"F2.wireOp",EDGE,"E3.18.11.2"),sQuery(id+"F2.wireOp",EDGE,"E3.18.11.3"),sQuery(id+"F2.wireOp",EDGE,"E3.18.12.0"),sQuery(id+"F2.wireOp",EDGE,"E3.18.12.1"),sQuery(id+"F2.wireOp",EDGE,"E3.18.12.2"),sQuery(id+"F2.wireOp",EDGE,"E3.18.12.3"),sQuery(id+"F2.wireOp",EDGE,"E3.18.13.0"),sQuery(id+"F2.wireOp",EDGE,"E3.18.13.1"),sQuery(id+"F2.wireOp",EDGE,"E3.18.13.2"),sQuery(id+"F2.wireOp",EDGE,"E3.18.13.3"),sQuery(id+"F2.wireOp",EDGE,"E3.18.14.0"),sQuery(id+"F2.wireOp",EDGE,"E3.18.14.1"),sQuery(id+"F2.wireOp",EDGE,"E3.18.14.2"),sQuery(id+"F2.wireOp",EDGE,"E3.18.14.3"),sQuery(id+"F2.wireOp",EDGE,"E3.18.15.0"),sQuery(id+"F2.wireOp",EDGE,"E3.18.15.1"),sQuery(id+"F2.wireOp",EDGE,"E3.18.15.2"),sQuery(id+"F2.wireOp",EDGE,"E3.18.15.3"),sQuery(id+"F2.wireOp",EDGE,"E3.18.16.0"),sQuery(id+"F2.wireOp",EDGE,"E3.18.16.1"),sQuery(id+"F2.wireOp",EDGE,"E3.18.16.2"),sQuery(id+"F2.wireOp",EDGE,"E3.18.16.3"),sQuery(id+"F2.wireOp",EDGE,"E3.18.17.0"),sQuery(id+"F2.wireOp",EDGE,"E3.18.17.1"),sQuery(id+"F2.wireOp",EDGE,"E3.18.17.2"),sQuery(id+"F2.wireOp",EDGE,"E3.18.17.3"),sQuery(id+"F2.wireOp",EDGE,"E3.18.18.0"),sQuery(id+"F2.wireOp",EDGE,"E3.18.18.1"),sQuery(id+"F2.wireOp",EDGE,"E3.18.18.2"),sQuery(id+"F2.wireOp",EDGE,"E3.18.18.3"),sQuery(id+"F2.wireOp",EDGE,"E3.18.19.0"),sQuery(id+"F2.wireOp",EDGE,"E3.18.19.1"),sQuery(id+"F2.wireOp",EDGE,"E3.18.19.2"),sQuery(id+"F2.wireOp",EDGE,"E3.18.19.3"),sQuery(id+"F2.wireOp",EDGE,"E3.18.20.0"),sQuery(id+"F2.wireOp",EDGE,"E3.18.20.1"),sQuery(id+"F2.wireOp",EDGE,"E3.18.20.2"),sQuery(id+"F2.wireOp",EDGE,"E3.18.20.3"),sQuery(id+"F2.wireOp",EDGE,"E3.18.21.0"),sQuery(id+"F2.wireOp",EDGE,"E3.18.21.1"),sQuery(id+"F2.wireOp",EDGE,"E3.18.21.2"),sQuery(id+"F2.wireOp",EDGE,"E3.18.21.3"),sQuery(id+"F2.wireOp",EDGE,"E3.19.0.0"),sQuery(id+"F2.wireOp",EDGE,"E3.19.0.1"),sQuery(id+"F2.wireOp",EDGE,"E3.19.0.2"),sQuery(id+"F2.wireOp",EDGE,"E3.19.0.3"),sQuery(id+"F2.wireOp",EDGE,"E3.19.1.0"),sQuery(id+"F2.wireOp",EDGE,"E3.19.1.1"),sQuery(id+"F2.wireOp",EDGE,"E3.19.1.2"),sQuery(id+"F2.wireOp",EDGE,"E3.19.1.3"),sQuery(id+"F2.wireOp",EDGE,"E3.19.2.0"),sQuery(id+"F2.wireOp",EDGE,"E3.19.2.1"),sQuery(id+"F2.wireOp",EDGE,"E3.19.2.2"),sQuery(id+"F2.wireOp",EDGE,"E3.19.2.3"),sQuery(id+"F2.wireOp",EDGE,"E3.19.3.0"),sQuery(id+"F2.wireOp",EDGE,"E3.19.3.1"),sQuery(id+"F2.wireOp",EDGE,"E3.19.3.2"),sQuery(id+"F2.wireOp",EDGE,"E3.19.3.3"),sQuery(id+"F2.wireOp",EDGE,"E3.19.4.0"),sQuery(id+"F2.wireOp",EDGE,"E3.19.4.1"),sQuery(id+"F2.wireOp",EDGE,"E3.19.4.2"),sQuery(id+"F2.wireOp",EDGE,"E3.19.4.3"),sQuery(id+"F2.wireOp",EDGE,"E3.19.5.0"),sQuery(id+"F2.wireOp",EDGE,"E3.19.5.1"),sQuery(id+"F2.wireOp",EDGE,"E3.19.5.2"),sQuery(id+"F2.wireOp",EDGE,"E3.19.5.3"),sQuery(id+"F2.wireOp",EDGE,"E3.19.6.0"),sQuery(id+"F2.wireOp",EDGE,"E3.19.6.1"),sQuery(id+"F2.wireOp",EDGE,"E3.19.6.2"),sQuery(id+"F2.wireOp",EDGE,"E3.19.6.3"),sQuery(id+"F2.wireOp",EDGE,"E3.19.7.0"),sQuery(id+"F2.wireOp",EDGE,"E3.19.7.1"),sQuery(id+"F2.wireOp",EDGE,"E3.19.7.2"),sQuery(id+"F2.wireOp",EDGE,"E3.19.7.3"),sQuery(id+"F2.wireOp",EDGE,"E3.19.8.0"),sQuery(id+"F2.wireOp",EDGE,"E3.19.8.1"),sQuery(id+"F2.wireOp",EDGE,"E3.19.8.2"),sQuery(id+"F2.wireOp",EDGE,"E3.19.8.3"),sQuery(id+"F2.wireOp",EDGE,"E3.19.9.0"),sQuery(id+"F2.wireOp",EDGE,"E3.19.9.1"),sQuery(id+"F2.wireOp",EDGE,"E3.19.9.2"),sQuery(id+"F2.wireOp",EDGE,"E3.19.9.3"),sQuery(id+"F2.wireOp",EDGE,"E3.19.10.0"),sQuery(id+"F2.wireOp",EDGE,"E3.19.10.1"),sQuery(id+"F2.wireOp",EDGE,"E3.19.10.2"),sQuery(id+"F2.wireOp",EDGE,"E3.19.10.3"),sQuery(id+"F2.wireOp",EDGE,"E3.19.11.0"),sQuery(id+"F2.wireOp",EDGE,"E3.19.11.1"),sQuery(id+"F2.wireOp",EDGE,"E3.19.11.2"),sQuery(id+"F2.wireOp",EDGE,"E3.19.11.3"),sQuery(id+"F2.wireOp",EDGE,"E3.19.12.0"),sQuery(id+"F2.wireOp",EDGE,"E3.19.12.1"),sQuery(id+"F2.wireOp",EDGE,"E3.19.12.2"),sQuery(id+"F2.wireOp",EDGE,"E3.19.12.3"),sQuery(id+"F2.wireOp",EDGE,"E3.19.13.0"),sQuery(id+"F2.wireOp",EDGE,"E3.19.13.1"),sQuery(id+"F2.wireOp",EDGE,"E3.19.13.2"),sQuery(id+"F2.wireOp",EDGE,"E3.19.13.3"),sQuery(id+"F2.wireOp",EDGE,"E3.19.14.0"),sQuery(id+"F2.wireOp",EDGE,"E3.19.14.1"),sQuery(id+"F2.wireOp",EDGE,"E3.19.14.2"),sQuery(id+"F2.wireOp",EDGE,"E3.19.14.3"),sQuery(id+"F2.wireOp",EDGE,"E3.19.15.0"),sQuery(id+"F2.wireOp",EDGE,"E3.19.15.1"),sQuery(id+"F2.wireOp",EDGE,"E3.19.15.2"),sQuery(id+"F2.wireOp",EDGE,"E3.19.15.3"),sQuery(id+"F2.wireOp",EDGE,"E3.19.16.0"),sQuery(id+"F2.wireOp",EDGE,"E3.19.16.1"),sQuery(id+"F2.wireOp",EDGE,"E3.19.16.2"),sQuery(id+"F2.wireOp",EDGE,"E3.19.16.3"),sQuery(id+"F2.wireOp",EDGE,"E3.19.17.0"),sQuery(id+"F2.wireOp",EDGE,"E3.19.17.1"),sQuery(id+"F2.wireOp",EDGE,"E3.19.17.2"),sQuery(id+"F2.wireOp",EDGE,"E3.19.17.3"),sQuery(id+"F2.wireOp",EDGE,"E3.19.18.0"),sQuery(id+"F2.wireOp",EDGE,"E3.19.18.1"),sQuery(id+"F2.wireOp",EDGE,"E3.19.18.2"),sQuery(id+"F2.wireOp",EDGE,"E3.19.18.3"),sQuery(id+"F2.wireOp",EDGE,"E3.19.19.0"),sQuery(id+"F2.wireOp",EDGE,"E3.19.19.1"),sQuery(id+"F2.wireOp",EDGE,"E3.19.19.2"),sQuery(id+"F2.wireOp",EDGE,"E3.19.19.3"),sQuery(id+"F2.wireOp",EDGE,"E3.19.20.0"),sQuery(id+"F2.wireOp",EDGE,"E3.19.20.1"),sQuery(id+"F2.wireOp",EDGE,"E3.19.20.2"),sQuery(id+"F2.wireOp",EDGE,"E3.19.20.3"),sQuery(id+"F2.wireOp",EDGE,"E3.19.21.0"),sQuery(id+"F2.wireOp",EDGE,"E3.19.21.1"),sQuery(id+"F2.wireOp",EDGE,"E3.19.21.2"),sQuery(id+"F2.wireOp",EDGE,"E3.19.21.3"),sQuery(id+"F2.wireOp",EDGE,"E3.20.0.0"),sQuery(id+"F2.wireOp",EDGE,"E3.20.0.1"),sQuery(id+"F2.wireOp",EDGE,"E3.20.0.2"),sQuery(id+"F2.wireOp",EDGE,"E3.20.0.3"),sQuery(id+"F2.wireOp",EDGE,"E3.20.1.0"),sQuery(id+"F2.wireOp",EDGE,"E3.20.1.1"),sQuery(id+"F2.wireOp",EDGE,"E3.20.1.2"),sQuery(id+"F2.wireOp",EDGE,"E3.20.1.3"),sQuery(id+"F2.wireOp",EDGE,"E3.20.2.0"),sQuery(id+"F2.wireOp",EDGE,"E3.20.2.1"),sQuery(id+"F2.wireOp",EDGE,"E3.20.2.2"),sQuery(id+"F2.wireOp",EDGE,"E3.20.2.3"),sQuery(id+"F2.wireOp",EDGE,"E3.20.3.0"),sQuery(id+"F2.wireOp",EDGE,"E3.20.3.1"),sQuery(id+"F2.wireOp",EDGE,"E3.20.3.2"),sQuery(id+"F2.wireOp",EDGE,"E3.20.3.3"),sQuery(id+"F2.wireOp",EDGE,"E3.20.4.0"),sQuery(id+"F2.wireOp",EDGE,"E3.20.4.1"),sQuery(id+"F2.wireOp",EDGE,"E3.20.4.2"),sQuery(id+"F2.wireOp",EDGE,"E3.20.4.3"),sQuery(id+"F2.wireOp",EDGE,"E3.20.5.0"),sQuery(id+"F2.wireOp",EDGE,"E3.20.5.1"),sQuery(id+"F2.wireOp",EDGE,"E3.20.5.2"),sQuery(id+"F2.wireOp",EDGE,"E3.20.5.3"),sQuery(id+"F2.wireOp",EDGE,"E3.20.6.0"),sQuery(id+"F2.wireOp",EDGE,"E3.20.6.1"),sQuery(id+"F2.wireOp",EDGE,"E3.20.6.2"),sQuery(id+"F2.wireOp",EDGE,"E3.20.6.3"),sQuery(id+"F2.wireOp",EDGE,"E3.20.7.0"),sQuery(id+"F2.wireOp",EDGE,"E3.20.7.1"),sQuery(id+"F2.wireOp",EDGE,"E3.20.7.2"),sQuery(id+"F2.wireOp",EDGE,"E3.20.7.3"),sQuery(id+"F2.wireOp",EDGE,"E3.20.8.0"),sQuery(id+"F2.wireOp",EDGE,"E3.20.8.1"),sQuery(id+"F2.wireOp",EDGE,"E3.20.8.2"),sQuery(id+"F2.wireOp",EDGE,"E3.20.8.3"),sQuery(id+"F2.wireOp",EDGE,"E3.20.9.0"),sQuery(id+"F2.wireOp",EDGE,"E3.20.9.1"),sQuery(id+"F2.wireOp",EDGE,"E3.20.9.2"),sQuery(id+"F2.wireOp",EDGE,"E3.20.9.3"),sQuery(id+"F2.wireOp",EDGE,"E3.20.10.0"),sQuery(id+"F2.wireOp",EDGE,"E3.20.10.1"),sQuery(id+"F2.wireOp",EDGE,"E3.20.10.2"),sQuery(id+"F2.wireOp",EDGE,"E3.20.10.3"),sQuery(id+"F2.wireOp",EDGE,"E3.20.11.0"),sQuery(id+"F2.wireOp",EDGE,"E3.20.11.1"),sQuery(id+"F2.wireOp",EDGE,"E3.20.11.2"),sQuery(id+"F2.wireOp",EDGE,"E3.20.11.3"),sQuery(id+"F2.wireOp",EDGE,"E3.20.12.0"),sQuery(id+"F2.wireOp",EDGE,"E3.20.12.1"),sQuery(id+"F2.wireOp",EDGE,"E3.20.12.2"),sQuery(id+"F2.wireOp",EDGE,"E3.20.12.3"),sQuery(id+"F2.wireOp",EDGE,"E3.20.13.0"),sQuery(id+"F2.wireOp",EDGE,"E3.20.13.1"),sQuery(id+"F2.wireOp",EDGE,"E3.20.13.2"),sQuery(id+"F2.wireOp",EDGE,"E3.20.13.3"),sQuery(id+"F2.wireOp",EDGE,"E3.20.14.0"),sQuery(id+"F2.wireOp",EDGE,"E3.20.14.1"),sQuery(id+"F2.wireOp",EDGE,"E3.20.14.2"),sQuery(id+"F2.wireOp",EDGE,"E3.20.14.3"),sQuery(id+"F2.wireOp",EDGE,"E3.20.15.0"),sQuery(id+"F2.wireOp",EDGE,"E3.20.15.1"),sQuery(id+"F2.wireOp",EDGE,"E3.20.15.2"),sQuery(id+"F2.wireOp",EDGE,"E3.20.15.3"),sQuery(id+"F2.wireOp",EDGE,"E3.20.16.0"),sQuery(id+"F2.wireOp",EDGE,"E3.20.16.1"),sQuery(id+"F2.wireOp",EDGE,"E3.20.16.2"),sQuery(id+"F2.wireOp",EDGE,"E3.20.16.3"),sQuery(id+"F2.wireOp",EDGE,"E3.20.17.0"),sQuery(id+"F2.wireOp",EDGE,"E3.20.17.1"),sQuery(id+"F2.wireOp",EDGE,"E3.20.17.2"),sQuery(id+"F2.wireOp",EDGE,"E3.20.17.3"),sQuery(id+"F2.wireOp",EDGE,"E3.20.18.0"),sQuery(id+"F2.wireOp",EDGE,"E3.20.18.1"),sQuery(id+"F2.wireOp",EDGE,"E3.20.18.2"),sQuery(id+"F2.wireOp",EDGE,"E3.20.18.3"),sQuery(id+"F2.wireOp",EDGE,"E3.20.19.0"),sQuery(id+"F2.wireOp",EDGE,"E3.20.19.1"),sQuery(id+"F2.wireOp",EDGE,"E3.20.19.2"),sQuery(id+"F2.wireOp",EDGE,"E3.20.19.3"),sQuery(id+"F2.wireOp",EDGE,"E3.20.20.0"),sQuery(id+"F2.wireOp",EDGE,"E3.20.20.1"),sQuery(id+"F2.wireOp",EDGE,"E3.20.20.2"),sQuery(id+"F2.wireOp",EDGE,"E3.20.20.3"),sQuery(id+"F2.wireOp",EDGE,"E3.20.21.0"),sQuery(id+"F2.wireOp",EDGE,"E3.20.21.1"),sQuery(id+"F2.wireOp",EDGE,"E3.20.21.2"),sQuery(id+"F2.wireOp",EDGE,"E3.20.21.3"),sQuery(id+"F2.wireOp",EDGE,"E3.21.0.0"),sQuery(id+"F2.wireOp",EDGE,"E3.21.0.1"),sQuery(id+"F2.wireOp",EDGE,"E3.21.0.2"),sQuery(id+"F2.wireOp",EDGE,"E3.21.0.3"),sQuery(id+"F2.wireOp",EDGE,"E3.21.1.0"),sQuery(id+"F2.wireOp",EDGE,"E3.21.1.1"),sQuery(id+"F2.wireOp",EDGE,"E3.21.1.2"),sQuery(id+"F2.wireOp",EDGE,"E3.21.1.3"),sQuery(id+"F2.wireOp",EDGE,"E3.21.2.0"),sQuery(id+"F2.wireOp",EDGE,"E3.21.2.1"),sQuery(id+"F2.wireOp",EDGE,"E3.21.2.2"),sQuery(id+"F2.wireOp",EDGE,"E3.21.2.3"),sQuery(id+"F2.wireOp",EDGE,"E3.21.3.0"),sQuery(id+"F2.wireOp",EDGE,"E3.21.3.1"),sQuery(id+"F2.wireOp",EDGE,"E3.21.3.2"),sQuery(id+"F2.wireOp",EDGE,"E3.21.3.3"),sQuery(id+"F2.wireOp",EDGE,"E3.21.4.0"),sQuery(id+"F2.wireOp",EDGE,"E3.21.4.1"),sQuery(id+"F2.wireOp",EDGE,"E3.21.4.2"),sQuery(id+"F2.wireOp",EDGE,"E3.21.4.3"),sQuery(id+"F2.wireOp",EDGE,"E3.21.5.0"),sQuery(id+"F2.wireOp",EDGE,"E3.21.5.1"),sQuery(id+"F2.wireOp",EDGE,"E3.21.5.2"),sQuery(id+"F2.wireOp",EDGE,"E3.21.5.3"),sQuery(id+"F2.wireOp",EDGE,"E3.21.6.0"),sQuery(id+"F2.wireOp",EDGE,"E3.21.6.1"),sQuery(id+"F2.wireOp",EDGE,"E3.21.6.2"),sQuery(id+"F2.wireOp",EDGE,"E3.21.6.3"),sQuery(id+"F2.wireOp",EDGE,"E3.21.7.0"),sQuery(id+"F2.wireOp",EDGE,"E3.21.7.1"),sQuery(id+"F2.wireOp",EDGE,"E3.21.7.2"),sQuery(id+"F2.wireOp",EDGE,"E3.21.7.3"),sQuery(id+"F2.wireOp",EDGE,"E3.21.8.0"),sQuery(id+"F2.wireOp",EDGE,"E3.21.8.1"),sQuery(id+"F2.wireOp",EDGE,"E3.21.8.2"),sQuery(id+"F2.wireOp",EDGE,"E3.21.8.3"),sQuery(id+"F2.wireOp",EDGE,"E3.21.9.0"),sQuery(id+"F2.wireOp",EDGE,"E3.21.9.1"),sQuery(id+"F2.wireOp",EDGE,"E3.21.9.2"),sQuery(id+"F2.wireOp",EDGE,"E3.21.9.3"),sQuery(id+"F2.wireOp",EDGE,"E3.21.10.0"),sQuery(id+"F2.wireOp",EDGE,"E3.21.10.1"),sQuery(id+"F2.wireOp",EDGE,"E3.21.10.2"),sQuery(id+"F2.wireOp",EDGE,"E3.21.10.3"),sQuery(id+"F2.wireOp",EDGE,"E3.21.11.0"),sQuery(id+"F2.wireOp",EDGE,"E3.21.11.1"),sQuery(id+"F2.wireOp",EDGE,"E3.21.11.2"),sQuery(id+"F2.wireOp",EDGE,"E3.21.11.3"),sQuery(id+"F2.wireOp",EDGE,"E3.21.12.0"),sQuery(id+"F2.wireOp",EDGE,"E3.21.12.1"),sQuery(id+"F2.wireOp",EDGE,"E3.21.12.2"),sQuery(id+"F2.wireOp",EDGE,"E3.21.12.3"),sQuery(id+"F2.wireOp",EDGE,"E3.21.13.0"),sQuery(id+"F2.wireOp",EDGE,"E3.21.13.1"),sQuery(id+"F2.wireOp",EDGE,"E3.21.13.2"),sQuery(id+"F2.wireOp",EDGE,"E3.21.13.3"),sQuery(id+"F2.wireOp",EDGE,"E3.21.14.0"),sQuery(id+"F2.wireOp",EDGE,"E3.21.14.1"),sQuery(id+"F2.wireOp",EDGE,"E3.21.14.2"),sQuery(id+"F2.wireOp",EDGE,"E3.21.14.3"),sQuery(id+"F2.wireOp",EDGE,"E3.21.15.0"),sQuery(id+"F2.wireOp",EDGE,"E3.21.15.1"),sQuery(id+"F2.wireOp",EDGE,"E3.21.15.2"),sQuery(id+"F2.wireOp",EDGE,"E3.21.15.3"),sQuery(id+"F2.wireOp",EDGE,"E3.21.16.0"),sQuery(id+"F2.wireOp",EDGE,"E3.21.16.1"),sQuery(id+"F2.wireOp",EDGE,"E3.21.16.2"),sQuery(id+"F2.wireOp",EDGE,"E3.21.16.3"),sQuery(id+"F2.wireOp",EDGE,"E3.21.17.0"),sQuery(id+"F2.wireOp",EDGE,"E3.21.17.1"),sQuery(id+"F2.wireOp",EDGE,"E3.21.17.2"),sQuery(id+"F2.wireOp",EDGE,"E3.21.17.3"),sQuery(id+"F2.wireOp",EDGE,"E3.21.18.0"),sQuery(id+"F2.wireOp",EDGE,"E3.21.18.1"),sQuery(id+"F2.wireOp",EDGE,"E3.21.18.2"),sQuery(id+"F2.wireOp",EDGE,"E3.21.18.3"),sQuery(id+"F2.wireOp",EDGE,"E3.21.19.0"),sQuery(id+"F2.wireOp",EDGE,"E3.21.19.1"),sQuery(id+"F2.wireOp",EDGE,"E3.21.19.2"),sQuery(id+"F2.wireOp",EDGE,"E3.21.19.3"),sQuery(id+"F2.wireOp",EDGE,"E3.21.20.0"),sQuery(id+"F2.wireOp",EDGE,"E3.21.20.1"),sQuery(id+"F2.wireOp",EDGE,"E3.21.20.2"),sQuery(id+"F2.wireOp",EDGE,"E3.21.20.3"),sQuery(id+"F2.wireOp",EDGE,"E3.21.21.0"),sQuery(id+"F2.wireOp",EDGE,"E3.21.21.1"),sQuery(id+"F2.wireOp",EDGE,"E3.21.21.2"),sQuery(id+"F2.wireOp",EDGE,"E3.21.21.3"),sQuery(id+"F2.wireOp",EDGE,"E3.22.0.0"),sQuery(id+"F2.wireOp",EDGE,"E3.22.0.1"),sQuery(id+"F2.wireOp",EDGE,"E3.22.0.2"),sQuery(id+"F2.wireOp",EDGE,"E3.22.0.3"),sQuery(id+"F2.wireOp",EDGE,"E3.22.1.0"),sQuery(id+"F2.wireOp",EDGE,"E3.22.1.1"),sQuery(id+"F2.wireOp",EDGE,"E3.22.1.2"),sQuery(id+"F2.wireOp",EDGE,"E3.22.1.3"),sQuery(id+"F2.wireOp",EDGE,"E3.22.2.0"),sQuery(id+"F2.wireOp",EDGE,"E3.22.2.1"),sQuery(id+"F2.wireOp",EDGE,"E3.22.2.2"),sQuery(id+"F2.wireOp",EDGE,"E3.22.2.3"),sQuery(id+"F2.wireOp",EDGE,"E3.22.3.0"),sQuery(id+"F2.wireOp",EDGE,"E3.22.3.1"),sQuery(id+"F2.wireOp",EDGE,"E3.22.3.2"),sQuery(id+"F2.wireOp",EDGE,"E3.22.3.3"),sQuery(id+"F2.wireOp",EDGE,"E3.22.4.0"),sQuery(id+"F2.wireOp",EDGE,"E3.22.4.1"),sQuery(id+"F2.wireOp",EDGE,"E3.22.4.2"),sQuery(id+"F2.wireOp",EDGE,"E3.22.4.3"),sQuery(id+"F2.wireOp",EDGE,"E3.22.5.0"),sQuery(id+"F2.wireOp",EDGE,"E3.22.5.1"),sQuery(id+"F2.wireOp",EDGE,"E3.22.5.2"),sQuery(id+"F2.wireOp",EDGE,"E3.22.5.3"),sQuery(id+"F2.wireOp",EDGE,"E3.22.6.0"),sQuery(id+"F2.wireOp",EDGE,"E3.22.6.1"),sQuery(id+"F2.wireOp",EDGE,"E3.22.6.2"),sQuery(id+"F2.wireOp",EDGE,"E3.22.6.3"),sQuery(id+"F2.wireOp",EDGE,"E3.22.7.0"),sQuery(id+"F2.wireOp",EDGE,"E3.22.7.1"),sQuery(id+"F2.wireOp",EDGE,"E3.22.7.2"),sQuery(id+"F2.wireOp",EDGE,"E3.22.7.3"),sQuery(id+"F2.wireOp",EDGE,"E3.22.8.0"),sQuery(id+"F2.wireOp",EDGE,"E3.22.8.1"),sQuery(id+"F2.wireOp",EDGE,"E3.22.8.2"),sQuery(id+"F2.wireOp",EDGE,"E3.22.8.3"),sQuery(id+"F2.wireOp",EDGE,"E3.22.9.0"),sQuery(id+"F2.wireOp",EDGE,"E3.22.9.1"),sQuery(id+"F2.wireOp",EDGE,"E3.22.9.2"),sQuery(id+"F2.wireOp",EDGE,"E3.22.9.3"),sQuery(id+"F2.wireOp",EDGE,"E3.22.10.0"),sQuery(id+"F2.wireOp",EDGE,"E3.22.10.1"),sQuery(id+"F2.wireOp",EDGE,"E3.22.10.2"),sQuery(id+"F2.wireOp",EDGE,"E3.22.10.3"),sQuery(id+"F2.wireOp",EDGE,"E3.22.11.0"),sQuery(id+"F2.wireOp",EDGE,"E3.22.11.1"),sQuery(id+"F2.wireOp",EDGE,"E3.22.11.2"),sQuery(id+"F2.wireOp",EDGE,"E3.22.11.3"),sQuery(id+"F2.wireOp",EDGE,"E3.22.12.0"),sQuery(id+"F2.wireOp",EDGE,"E3.22.12.1"),sQuery(id+"F2.wireOp",EDGE,"E3.22.12.2"),sQuery(id+"F2.wireOp",EDGE,"E3.22.12.3"),sQuery(id+"F2.wireOp",EDGE,"E3.22.13.0"),sQuery(id+"F2.wireOp",EDGE,"E3.22.13.1"),sQuery(id+"F2.wireOp",EDGE,"E3.22.13.2"),sQuery(id+"F2.wireOp",EDGE,"E3.22.13.3"),sQuery(id+"F2.wireOp",EDGE,"E3.22.14.0"),sQuery(id+"F2.wireOp",EDGE,"E3.22.14.1"),sQuery(id+"F2.wireOp",EDGE,"E3.22.14.2"),sQuery(id+"F2.wireOp",EDGE,"E3.22.14.3"),sQuery(id+"F2.wireOp",EDGE,"E3.22.15.0"),sQuery(id+"F2.wireOp",EDGE,"E3.22.15.1"),sQuery(id+"F2.wireOp",EDGE,"E3.22.15.2"),sQuery(id+"F2.wireOp",EDGE,"E3.22.15.3"),sQuery(id+"F2.wireOp",EDGE,"E3.22.16.0"),sQuery(id+"F2.wireOp",EDGE,"E3.22.16.1"),sQuery(id+"F2.wireOp",EDGE,"E3.22.16.2"),sQuery(id+"F2.wireOp",EDGE,"E3.22.16.3"),sQuery(id+"F2.wireOp",EDGE,"E3.22.17.0"),sQuery(id+"F2.wireOp",EDGE,"E3.22.17.1"),sQuery(id+"F2.wireOp",EDGE,"E3.22.17.2"),sQuery(id+"F2.wireOp",EDGE,"E3.22.17.3"),sQuery(id+"F2.wireOp",EDGE,"E3.22.18.0"),sQuery(id+"F2.wireOp",EDGE,"E3.22.18.1"),sQuery(id+"F2.wireOp",EDGE,"E3.22.18.2"),sQuery(id+"F2.wireOp",EDGE,"E3.22.18.3"),sQuery(id+"F2.wireOp",EDGE,"E3.22.19.0"),sQuery(id+"F2.wireOp",EDGE,"E3.22.19.1"),sQuery(id+"F2.wireOp",EDGE,"E3.22.19.2"),sQuery(id+"F2.wireOp",EDGE,"E3.22.19.3"),sQuery(id+"F2.wireOp",EDGE,"E3.22.20.0"),sQuery(id+"F2.wireOp",EDGE,"E3.22.20.1"),sQuery(id+"F2.wireOp",EDGE,"E3.22.20.2"),sQuery(id+"F2.wireOp",EDGE,"E3.22.20.3"),sQuery(id+"F2.wireOp",EDGE,"E3.22.21.0"),sQuery(id+"F2.wireOp",EDGE,"E3.22.21.1"),sQuery(id+"F2.wireOp",EDGE,"E3.22.21.2"),sQuery(id+"F2.wireOp",EDGE,"E3.22.21.3"),sQuery(id+"F2.wireOp",EDGE,"E3.23.0.0"),sQuery(id+"F2.wireOp",EDGE,"E3.23.0.1"),sQuery(id+"F2.wireOp",EDGE,"E3.23.0.2"),sQuery(id+"F2.wireOp",EDGE,"E3.23.0.3"),sQuery(id+"F2.wireOp",EDGE,"E3.23.1.0"),sQuery(id+"F2.wireOp",EDGE,"E3.23.1.1"),sQuery(id+"F2.wireOp",EDGE,"E3.23.1.2"),sQuery(id+"F2.wireOp",EDGE,"E3.23.1.3"),sQuery(id+"F2.wireOp",EDGE,"E3.23.2.0"),sQuery(id+"F2.wireOp",EDGE,"E3.23.2.1"),sQuery(id+"F2.wireOp",EDGE,"E3.23.2.2"),sQuery(id+"F2.wireOp",EDGE,"E3.23.2.3"),sQuery(id+"F2.wireOp",EDGE,"E3.23.3.0"),sQuery(id+"F2.wireOp",EDGE,"E3.23.3.1"),sQuery(id+"F2.wireOp",EDGE,"E3.23.3.2"),sQuery(id+"F2.wireOp",EDGE,"E3.23.3.3"),sQuery(id+"F2.wireOp",EDGE,"E3.23.4.0"),sQuery(id+"F2.wireOp",EDGE,"E3.23.4.1"),sQuery(id+"F2.wireOp",EDGE,"E3.23.4.2"),sQuery(id+"F2.wireOp",EDGE,"E3.23.4.3"),sQuery(id+"F2.wireOp",EDGE,"E3.23.5.0"),sQuery(id+"F2.wireOp",EDGE,"E3.23.5.1"),sQuery(id+"F2.wireOp",EDGE,"E3.23.5.2"),sQuery(id+"F2.wireOp",EDGE,"E3.23.5.3"),sQuery(id+"F2.wireOp",EDGE,"E3.23.6.0"),sQuery(id+"F2.wireOp",EDGE,"E3.23.6.1"),sQuery(id+"F2.wireOp",EDGE,"E3.23.6.2"),sQuery(id+"F2.wireOp",EDGE,"E3.23.6.3"),sQuery(id+"F2.wireOp",EDGE,"E3.23.7.0"),sQuery(id+"F2.wireOp",EDGE,"E3.23.7.1"),sQuery(id+"F2.wireOp",EDGE,"E3.23.7.2"),sQuery(id+"F2.wireOp",EDGE,"E3.23.7.3"),sQuery(id+"F2.wireOp",EDGE,"E3.23.8.0"),sQuery(id+"F2.wireOp",EDGE,"E3.23.8.1"),sQuery(id+"F2.wireOp",EDGE,"E3.23.8.2"),sQuery(id+"F2.wireOp",EDGE,"E3.23.8.3"),sQuery(id+"F2.wireOp",EDGE,"E3.23.9.0"),sQuery(id+"F2.wireOp",EDGE,"E3.23.9.1"),sQuery(id+"F2.wireOp",EDGE,"E3.23.9.2"),sQuery(id+"F2.wireOp",EDGE,"E3.23.9.3"),sQuery(id+"F2.wireOp",EDGE,"E3.23.10.0"),sQuery(id+"F2.wireOp",EDGE,"E3.23.10.1"),sQuery(id+"F2.wireOp",EDGE,"E3.23.10.2"),sQuery(id+"F2.wireOp",EDGE,"E3.23.10.3"),sQuery(id+"F2.wireOp",EDGE,"E3.23.11.0"),sQuery(id+"F2.wireOp",EDGE,"E3.23.11.1"),sQuery(id+"F2.wireOp",EDGE,"E3.23.11.2"),sQuery(id+"F2.wireOp",EDGE,"E3.23.11.3"),sQuery(id+"F2.wireOp",EDGE,"E3.23.12.0"),sQuery(id+"F2.wireOp",EDGE,"E3.23.12.1"),sQuery(id+"F2.wireOp",EDGE,"E3.23.12.2"),sQuery(id+"F2.wireOp",EDGE,"E3.23.12.3"),sQuery(id+"F2.wireOp",EDGE,"E3.23.13.0"),sQuery(id+"F2.wireOp",EDGE,"E3.23.13.1"),sQuery(id+"F2.wireOp",EDGE,"E3.23.13.2"),sQuery(id+"F2.wireOp",EDGE,"E3.23.13.3"),sQuery(id+"F2.wireOp",EDGE,"E3.23.14.0"),sQuery(id+"F2.wireOp",EDGE,"E3.23.14.1"),sQuery(id+"F2.wireOp",EDGE,"E3.23.14.2"),sQuery(id+"F2.wireOp",EDGE,"E3.23.14.3"),sQuery(id+"F2.wireOp",EDGE,"E3.23.15.0"),sQuery(id+"F2.wireOp",EDGE,"E3.23.15.1"),sQuery(id+"F2.wireOp",EDGE,"E3.23.15.2"),sQuery(id+"F2.wireOp",EDGE,"E3.23.15.3"),sQuery(id+"F2.wireOp",EDGE,"E3.23.16.0"),sQuery(id+"F2.wireOp",EDGE,"E3.23.16.1"),sQuery(id+"F2.wireOp",EDGE,"E3.23.16.2"),sQuery(id+"F2.wireOp",EDGE,"E3.23.16.3"),sQuery(id+"F2.wireOp",EDGE,"E3.23.17.0"),sQuery(id+"F2.wireOp",EDGE,"E3.23.17.1"),sQuery(id+"F2.wireOp",EDGE,"E3.23.17.2"),sQuery(id+"F2.wireOp",EDGE,"E3.23.17.3"),sQuery(id+"F2.wireOp",EDGE,"E3.23.18.0"),sQuery(id+"F2.wireOp",EDGE,"E3.23.18.1"),sQuery(id+"F2.wireOp",EDGE,"E3.23.18.2"),sQuery(id+"F2.wireOp",EDGE,"E3.23.18.3"),sQuery(id+"F2.wireOp",EDGE,"E3.23.19.0"),sQuery(id+"F2.wireOp",EDGE,"E3.23.19.1"),sQuery(id+"F2.wireOp",EDGE,"E3.23.19.2"),sQuery(id+"F2.wireOp",EDGE,"E3.23.19.3"),sQuery(id+"F2.wireOp",EDGE,"E3.23.20.0"),sQuery(id+"F2.wireOp",EDGE,"E3.23.20.1"),sQuery(id+"F2.wireOp",EDGE,"E3.23.20.2"),sQuery(id+"F2.wireOp",EDGE,"E3.23.20.3"),sQuery(id+"F2.wireOp",EDGE,"E3.23.21.0"),sQuery(id+"F2.wireOp",EDGE,"E3.23.21.1"),sQuery(id+"F2.wireOp",EDGE,"E3.23.21.2"),sQuery(id+"F2.wireOp",EDGE,"E3.23.21.3"),sQuery(id+"F2.wireOp",EDGE,"E3.24.0.0"),sQuery(id+"F2.wireOp",EDGE,"E3.24.0.1"),sQuery(id+"F2.wireOp",EDGE,"E3.24.0.2"),sQuery(id+"F2.wireOp",EDGE,"E3.24.0.3"),sQuery(id+"F2.wireOp",EDGE,"E3.24.1.0"),sQuery(id+"F2.wireOp",EDGE,"E3.24.1.1"),sQuery(id+"F2.wireOp",EDGE,"E3.24.1.2"),sQuery(id+"F2.wireOp",EDGE,"E3.24.1.3"),sQuery(id+"F2.wireOp",EDGE,"E3.24.2.0"),sQuery(id+"F2.wireOp",EDGE,"E3.24.2.1"),sQuery(id+"F2.wireOp",EDGE,"E3.24.2.2"),sQuery(id+"F2.wireOp",EDGE,"E3.24.2.3"),sQuery(id+"F2.wireOp",EDGE,"E3.24.3.0"),sQuery(id+"F2.wireOp",EDGE,"E3.24.3.1"),sQuery(id+"F2.wireOp",EDGE,"E3.24.3.2"),sQuery(id+"F2.wireOp",EDGE,"E3.24.3.3"),sQuery(id+"F2.wireOp",EDGE,"E3.24.4.0"),sQuery(id+"F2.wireOp",EDGE,"E3.24.4.1"),sQuery(id+"F2.wireOp",EDGE,"E3.24.4.2"),sQuery(id+"F2.wireOp",EDGE,"E3.24.4.3"),sQuery(id+"F2.wireOp",EDGE,"E3.24.5.0"),sQuery(id+"F2.wireOp",EDGE,"E3.24.5.1"),sQuery(id+"F2.wireOp",EDGE,"E3.24.5.2"),sQuery(id+"F2.wireOp",EDGE,"E3.24.5.3"),sQuery(id+"F2.wireOp",EDGE,"E3.24.6.0"),sQuery(id+"F2.wireOp",EDGE,"E3.24.6.1"),sQuery(id+"F2.wireOp",EDGE,"E3.24.6.2"),sQuery(id+"F2.wireOp",EDGE,"E3.24.6.3"),sQuery(id+"F2.wireOp",EDGE,"E3.24.7.0"),sQuery(id+"F2.wireOp",EDGE,"E3.24.7.1"),sQuery(id+"F2.wireOp",EDGE,"E3.24.7.2"),sQuery(id+"F2.wireOp",EDGE,"E3.24.7.3"),sQuery(id+"F2.wireOp",EDGE,"E3.24.8.0"),sQuery(id+"F2.wireOp",EDGE,"E3.24.8.1"),sQuery(id+"F2.wireOp",EDGE,"E3.24.8.2"),sQuery(id+"F2.wireOp",EDGE,"E3.24.8.3"),sQuery(id+"F2.wireOp",EDGE,"E3.24.9.0"),sQuery(id+"F2.wireOp",EDGE,"E3.24.9.1"),sQuery(id+"F2.wireOp",EDGE,"E3.24.9.2"),sQuery(id+"F2.wireOp",EDGE,"E3.24.9.3"),sQuery(id+"F2.wireOp",EDGE,"E3.24.10.0"),sQuery(id+"F2.wireOp",EDGE,"E3.24.10.1"),sQuery(id+"F2.wireOp",EDGE,"E3.24.10.2"),sQuery(id+"F2.wireOp",EDGE,"E3.24.10.3"),sQuery(id+"F2.wireOp",EDGE,"E3.24.11.0"),sQuery(id+"F2.wireOp",EDGE,"E3.24.11.1"),sQuery(id+"F2.wireOp",EDGE,"E3.24.11.2"),sQuery(id+"F2.wireOp",EDGE,"E3.24.11.3"),sQuery(id+"F2.wireOp",EDGE,"E3.24.12.0"),sQuery(id+"F2.wireOp",EDGE,"E3.24.12.1"),sQuery(id+"F2.wireOp",EDGE,"E3.24.12.2"),sQuery(id+"F2.wireOp",EDGE,"E3.24.12.3"),sQuery(id+"F2.wireOp",EDGE,"E3.24.13.0"),sQuery(id+"F2.wireOp",EDGE,"E3.24.13.1"),sQuery(id+"F2.wireOp",EDGE,"E3.24.13.2"),sQuery(id+"F2.wireOp",EDGE,"E3.24.13.3"),sQuery(id+"F2.wireOp",EDGE,"E3.24.14.0"),sQuery(id+"F2.wireOp",EDGE,"E3.24.14.1"),sQuery(id+"F2.wireOp",EDGE,"E3.24.14.2"),sQuery(id+"F2.wireOp",EDGE,"E3.24.14.3"),sQuery(id+"F2.wireOp",EDGE,"E3.24.15.0"),sQuery(id+"F2.wireOp",EDGE,"E3.24.15.1"),sQuery(id+"F2.wireOp",EDGE,"E3.24.15.2"),sQuery(id+"F2.wireOp",EDGE,"E3.24.15.3"),sQuery(id+"F2.wireOp",EDGE,"E3.24.16.0"),sQuery(id+"F2.wireOp",EDGE,"E3.24.16.1"),sQuery(id+"F2.wireOp",EDGE,"E3.24.16.2"),sQuery(id+"F2.wireOp",EDGE,"E3.24.16.3"),sQuery(id+"F2.wireOp",EDGE,"E3.24.17.0"),sQuery(id+"F2.wireOp",EDGE,"E3.24.17.1"),sQuery(id+"F2.wireOp",EDGE,"E3.24.17.2"),sQuery(id+"F2.wireOp",EDGE,"E3.24.17.3"),sQuery(id+"F2.wireOp",EDGE,"E3.24.18.0"),sQuery(id+"F2.wireOp",EDGE,"E3.24.18.1"),sQuery(id+"F2.wireOp",EDGE,"E3.24.18.2"),sQuery(id+"F2.wireOp",EDGE,"E3.24.18.3"),sQuery(id+"F2.wireOp",EDGE,"E3.24.19.0"),sQuery(id+"F2.wireOp",EDGE,"E3.24.19.1"),sQuery(id+"F2.wireOp",EDGE,"E3.24.19.2"),sQuery(id+"F2.wireOp",EDGE,"E3.24.19.3"),sQuery(id+"F2.wireOp",EDGE,"E3.24.20.0"),sQuery(id+"F2.wireOp",EDGE,"E3.24.20.1"),sQuery(id+"F2.wireOp",EDGE,"E3.24.20.2"),sQuery(id+"F2.wireOp",EDGE,"E3.24.20.3"),sQuery(id+"F2.wireOp",EDGE,"E3.24.21.0"),sQuery(id+"F2.wireOp",EDGE,"E3.24.21.1"),sQuery(id+"F2.wireOp",EDGE,"E3.24.21.2"),sQuery(id+"F2.wireOp",EDGE,"E3.24.21.3"),sQuery(id+"F2.wireOp",EDGE,"E3.25.0.0"),sQuery(id+"F2.wireOp",EDGE,"E3.25.0.1"),sQuery(id+"F2.wireOp",EDGE,"E3.25.0.2"),sQuery(id+"F2.wireOp",EDGE,"E3.25.0.3"),sQuery(id+"F2.wireOp",EDGE,"E3.25.1.0"),sQuery(id+"F2.wireOp",EDGE,"E3.25.1.1"),sQuery(id+"F2.wireOp",EDGE,"E3.25.1.2"),sQuery(id+"F2.wireOp",EDGE,"E3.25.1.3"),sQuery(id+"F2.wireOp",EDGE,"E3.25.2.0"),sQuery(id+"F2.wireOp",EDGE,"E3.25.2.1"),sQuery(id+"F2.wireOp",EDGE,"E3.25.2.2"),sQuery(id+"F2.wireOp",EDGE,"E3.25.2.3"),sQuery(id+"F2.wireOp",EDGE,"E3.25.3.0"),sQuery(id+"F2.wireOp",EDGE,"E3.25.3.1"),sQuery(id+"F2.wireOp",EDGE,"E3.25.3.2"),sQuery(id+"F2.wireOp",EDGE,"E3.25.3.3"),sQuery(id+"F2.wireOp",EDGE,"E3.25.4.0"),sQuery(id+"F2.wireOp",EDGE,"E3.25.4.1"),sQuery(id+"F2.wireOp",EDGE,"E3.25.4.2"),sQuery(id+"F2.wireOp",EDGE,"E3.25.4.3"),sQuery(id+"F2.wireOp",EDGE,"E3.25.5.0"),sQuery(id+"F2.wireOp",EDGE,"E3.25.5.1"),sQuery(id+"F2.wireOp",EDGE,"E3.25.5.2"),sQuery(id+"F2.wireOp",EDGE,"E3.25.5.3"),sQuery(id+"F2.wireOp",EDGE,"E3.25.6.0"),sQuery(id+"F2.wireOp",EDGE,"E3.25.6.1"),sQuery(id+"F2.wireOp",EDGE,"E3.25.6.2"),sQuery(id+"F2.wireOp",EDGE,"E3.25.6.3"),sQuery(id+"F2.wireOp",EDGE,"E3.25.7.0"),sQuery(id+"F2.wireOp",EDGE,"E3.25.7.1"),sQuery(id+"F2.wireOp",EDGE,"E3.25.7.2"),sQuery(id+"F2.wireOp",EDGE,"E3.25.7.3"),sQuery(id+"F2.wireOp",EDGE,"E3.25.8.0"),sQuery(id+"F2.wireOp",EDGE,"E3.25.8.1"),sQuery(id+"F2.wireOp",EDGE,"E3.25.8.2"),sQuery(id+"F2.wireOp",EDGE,"E3.25.8.3"),sQuery(id+"F2.wireOp",EDGE,"E3.25.9.0"),sQuery(id+"F2.wireOp",EDGE,"E3.25.9.1"),sQuery(id+"F2.wireOp",EDGE,"E3.25.9.2"),sQuery(id+"F2.wireOp",EDGE,"E3.25.9.3"),sQuery(id+"F2.wireOp",EDGE,"E3.25.10.0"),sQuery(id+"F2.wireOp",EDGE,"E3.25.10.1"),sQuery(id+"F2.wireOp",EDGE,"E3.25.10.2"),sQuery(id+"F2.wireOp",EDGE,"E3.25.10.3"),sQuery(id+"F2.wireOp",EDGE,"E3.25.11.0"),sQuery(id+"F2.wireOp",EDGE,"E3.25.11.1"),sQuery(id+"F2.wireOp",EDGE,"E3.25.11.2"),sQuery(id+"F2.wireOp",EDGE,"E3.25.11.3"),sQuery(id+"F2.wireOp",EDGE,"E3.25.12.0"),sQuery(id+"F2.wireOp",EDGE,"E3.25.12.1"),sQuery(id+"F2.wireOp",EDGE,"E3.25.12.2"),sQuery(id+"F2.wireOp",EDGE,"E3.25.12.3"),sQuery(id+"F2.wireOp",EDGE,"E3.25.13.0"),sQuery(id+"F2.wireOp",EDGE,"E3.25.13.1"),sQuery(id+"F2.wireOp",EDGE,"E3.25.13.2"),sQuery(id+"F2.wireOp",EDGE,"E3.25.13.3"),sQuery(id+"F2.wireOp",EDGE,"E3.25.14.0"),sQuery(id+"F2.wireOp",EDGE,"E3.25.14.1"),sQuery(id+"F2.wireOp",EDGE,"E3.25.14.2"),sQuery(id+"F2.wireOp",EDGE,"E3.25.14.3"),sQuery(id+"F2.wireOp",EDGE,"E3.25.15.0"),sQuery(id+"F2.wireOp",EDGE,"E3.25.15.1"),sQuery(id+"F2.wireOp",EDGE,"E3.25.15.2"),sQuery(id+"F2.wireOp",EDGE,"E3.25.15.3"),sQuery(id+"F2.wireOp",EDGE,"E3.25.16.0"),sQuery(id+"F2.wireOp",EDGE,"E3.25.16.1"),sQuery(id+"F2.wireOp",EDGE,"E3.25.16.2"),sQuery(id+"F2.wireOp",EDGE,"E3.25.16.3"),sQuery(id+"F2.wireOp",EDGE,"E3.25.17.0"),sQuery(id+"F2.wireOp",EDGE,"E3.25.17.1"),sQuery(id+"F2.wireOp",EDGE,"E3.25.17.2"),sQuery(id+"F2.wireOp",EDGE,"E3.25.17.3"),sQuery(id+"F2.wireOp",EDGE,"E3.25.18.0"),sQuery(id+"F2.wireOp",EDGE,"E3.25.18.1"),sQuery(id+"F2.wireOp",EDGE,"E3.25.18.2"),sQuery(id+"F2.wireOp",EDGE,"E3.25.18.3"),sQuery(id+"F2.wireOp",EDGE,"E3.25.19.0"),sQuery(id+"F2.wireOp",EDGE,"E3.25.19.1"),sQuery(id+"F2.wireOp",EDGE,"E3.25.19.2"),sQuery(id+"F2.wireOp",EDGE,"E3.25.19.3"),sQuery(id+"F2.wireOp",EDGE,"E3.25.20.0"),sQuery(id+"F2.wireOp",EDGE,"E3.25.20.1"),sQuery(id+"F2.wireOp",EDGE,"E3.25.20.2"),sQuery(id+"F2.wireOp",EDGE,"E3.25.20.3"),sQuery(id+"F2.wireOp",EDGE,"E3.25.21.0"),sQuery(id+"F2.wireOp",EDGE,"E3.25.21.1"),sQuery(id+"F2.wireOp",EDGE,"E3.25.21.2"),sQuery(id+"F2.wireOp",EDGE,"E3.25.21.3"),sQuery(id+"F2.wireOp",EDGE,"E3.26.0.0"),sQuery(id+"F2.wireOp",EDGE,"E3.26.0.1"),sQuery(id+"F2.wireOp",EDGE,"E3.26.0.2"),sQuery(id+"F2.wireOp",EDGE,"E3.26.0.3"),sQuery(id+"F2.wireOp",EDGE,"E3.26.1.0"),sQuery(id+"F2.wireOp",EDGE,"E3.26.1.1"),sQuery(id+"F2.wireOp",EDGE,"E3.26.1.2"),sQuery(id+"F2.wireOp",EDGE,"E3.26.1.3"),sQuery(id+"F2.wireOp",EDGE,"E3.26.2.0"),sQuery(id+"F2.wireOp",EDGE,"E3.26.2.1"),sQuery(id+"F2.wireOp",EDGE,"E3.26.2.2"),sQuery(id+"F2.wireOp",EDGE,"E3.26.2.3"),sQuery(id+"F2.wireOp",EDGE,"E3.26.3.0"),sQuery(id+"F2.wireOp",EDGE,"E3.26.3.1"),sQuery(id+"F2.wireOp",EDGE,"E3.26.3.2"),sQuery(id+"F2.wireOp",EDGE,"E3.26.3.3"),sQuery(id+"F2.wireOp",EDGE,"E3.26.4.0"),sQuery(id+"F2.wireOp",EDGE,"E3.26.4.1"),sQuery(id+"F2.wireOp",EDGE,"E3.26.4.2"),sQuery(id+"F2.wireOp",EDGE,"E3.26.4.3"),sQuery(id+"F2.wireOp",EDGE,"E3.26.5.0"),sQuery(id+"F2.wireOp",EDGE,"E3.26.5.1"),sQuery(id+"F2.wireOp",EDGE,"E3.26.5.2"),sQuery(id+"F2.wireOp",EDGE,"E3.26.5.3"),sQuery(id+"F2.wireOp",EDGE,"E3.26.6.0"),sQuery(id+"F2.wireOp",EDGE,"E3.26.6.1"),sQuery(id+"F2.wireOp",EDGE,"E3.26.6.2"),sQuery(id+"F2.wireOp",EDGE,"E3.26.6.3"),sQuery(id+"F2.wireOp",EDGE,"E3.26.7.0"),sQuery(id+"F2.wireOp",EDGE,"E3.26.7.1"),sQuery(id+"F2.wireOp",EDGE,"E3.26.7.2"),sQuery(id+"F2.wireOp",EDGE,"E3.26.7.3"),sQuery(id+"F2.wireOp",EDGE,"E3.26.8.0"),sQuery(id+"F2.wireOp",EDGE,"E3.26.8.1"),sQuery(id+"F2.wireOp",EDGE,"E3.26.8.2"),sQuery(id+"F2.wireOp",EDGE,"E3.26.8.3"),sQuery(id+"F2.wireOp",EDGE,"E3.26.9.0"),sQuery(id+"F2.wireOp",EDGE,"E3.26.9.1"),sQuery(id+"F2.wireOp",EDGE,"E3.26.9.2"),sQuery(id+"F2.wireOp",EDGE,"E3.26.9.3"),sQuery(id+"F2.wireOp",EDGE,"E3.26.10.0"),sQuery(id+"F2.wireOp",EDGE,"E3.26.10.1"),sQuery(id+"F2.wireOp",EDGE,"E3.26.10.2"),sQuery(id+"F2.wireOp",EDGE,"E3.26.10.3"),sQuery(id+"F2.wireOp",EDGE,"E3.26.11.0"),sQuery(id+"F2.wireOp",EDGE,"E3.26.11.1"),sQuery(id+"F2.wireOp",EDGE,"E3.26.11.2"),sQuery(id+"F2.wireOp",EDGE,"E3.26.11.3"),sQuery(id+"F2.wireOp",EDGE,"E3.26.12.0"),sQuery(id+"F2.wireOp",EDGE,"E3.26.12.1"),sQuery(id+"F2.wireOp",EDGE,"E3.26.12.2"),sQuery(id+"F2.wireOp",EDGE,"E3.26.12.3"),sQuery(id+"F2.wireOp",EDGE,"E3.26.13.0"),sQuery(id+"F2.wireOp",EDGE,"E3.26.13.1"),sQuery(id+"F2.wireOp",EDGE,"E3.26.13.2"),sQuery(id+"F2.wireOp",EDGE,"E3.26.13.3"),sQuery(id+"F2.wireOp",EDGE,"E3.26.14.0"),sQuery(id+"F2.wireOp",EDGE,"E3.26.14.1"),sQuery(id+"F2.wireOp",EDGE,"E3.26.14.2"),sQuery(id+"F2.wireOp",EDGE,"E3.26.14.3"),sQuery(id+"F2.wireOp",EDGE,"E3.26.15.0"),sQuery(id+"F2.wireOp",EDGE,"E3.26.15.1"),sQuery(id+"F2.wireOp",EDGE,"E3.26.15.2"),sQuery(id+"F2.wireOp",EDGE,"E3.26.15.3"),sQuery(id+"F2.wireOp",EDGE,"E3.26.16.0"),sQuery(id+"F2.wireOp",EDGE,"E3.26.16.1"),sQuery(id+"F2.wireOp",EDGE,"E3.26.16.2"),sQuery(id+"F2.wireOp",EDGE,"E3.26.16.3"),sQuery(id+"F2.wireOp",EDGE,"E3.26.17.0"),sQuery(id+"F2.wireOp",EDGE,"E3.26.17.1"),sQuery(id+"F2.wireOp",EDGE,"E3.26.17.2"),sQuery(id+"F2.wireOp",EDGE,"E3.26.17.3"),sQuery(id+"F2.wireOp",EDGE,"E3.26.18.0"),sQuery(id+"F2.wireOp",EDGE,"E3.26.18.1"),sQuery(id+"F2.wireOp",EDGE,"E3.26.18.2"),sQuery(id+"F2.wireOp",EDGE,"E3.26.18.3"),sQuery(id+"F2.wireOp",EDGE,"E3.26.19.0"),sQuery(id+"F2.wireOp",EDGE,"E3.26.19.1"),sQuery(id+"F2.wireOp",EDGE,"E3.26.19.2"),sQuery(id+"F2.wireOp",EDGE,"E3.26.19.3"),sQuery(id+"F2.wireOp",EDGE,"E3.26.20.0"),sQuery(id+"F2.wireOp",EDGE,"E3.26.20.1"),sQuery(id+"F2.wireOp",EDGE,"E3.26.20.2"),sQuery(id+"F2.wireOp",EDGE,"E3.26.20.3"),sQuery(id+"F2.wireOp",EDGE,"E3.26.21.0"),sQuery(id+"F2.wireOp",EDGE,"E3.26.21.1"),sQuery(id+"F2.wireOp",EDGE,"E3.26.21.2"),sQuery(id+"F2.wireOp",EDGE,"E3.26.21.3"),sQuery(id+"F2.wireOp",EDGE,"E3.27.0.0"),sQuery(id+"F2.wireOp",EDGE,"E3.27.0.1"),sQuery(id+"F2.wireOp",EDGE,"E3.27.0.2"),sQuery(id+"F2.wireOp",EDGE,"E3.27.0.3"),sQuery(id+"F2.wireOp",EDGE,"E3.27.1.0"),sQuery(id+"F2.wireOp",EDGE,"E3.27.1.1"),sQuery(id+"F2.wireOp",EDGE,"E3.27.1.2"),sQuery(id+"F2.wireOp",EDGE,"E3.27.1.3"),sQuery(id+"F2.wireOp",EDGE,"E3.27.2.0"),sQuery(id+"F2.wireOp",EDGE,"E3.27.2.1"),sQuery(id+"F2.wireOp",EDGE,"E3.27.2.2"),sQuery(id+"F2.wireOp",EDGE,"E3.27.2.3"),sQuery(id+"F2.wireOp",EDGE,"E3.27.3.0"),sQuery(id+"F2.wireOp",EDGE,"E3.27.3.1"),sQuery(id+"F2.wireOp",EDGE,"E3.27.3.2"),sQuery(id+"F2.wireOp",EDGE,"E3.27.3.3"),sQuery(id+"F2.wireOp",EDGE,"E3.27.4.0"),sQuery(id+"F2.wireOp",EDGE,"E3.27.4.1"),sQuery(id+"F2.wireOp",EDGE,"E3.27.4.2"),sQuery(id+"F2.wireOp",EDGE,"E3.27.4.3"),sQuery(id+"F2.wireOp",EDGE,"E3.27.5.0"),sQuery(id+"F2.wireOp",EDGE,"E3.27.5.1"),sQuery(id+"F2.wireOp",EDGE,"E3.27.5.2"),sQuery(id+"F2.wireOp",EDGE,"E3.27.5.3"),sQuery(id+"F2.wireOp",EDGE,"E3.27.6.0"),sQuery(id+"F2.wireOp",EDGE,"E3.27.6.1"),sQuery(id+"F2.wireOp",EDGE,"E3.27.6.2"),sQuery(id+"F2.wireOp",EDGE,"E3.27.6.3"),sQuery(id+"F2.wireOp",EDGE,"E3.27.7.0"),sQuery(id+"F2.wireOp",EDGE,"E3.27.7.1"),sQuery(id+"F2.wireOp",EDGE,"E3.27.7.2"),sQuery(id+"F2.wireOp",EDGE,"E3.27.7.3"),sQuery(id+"F2.wireOp",EDGE,"E3.27.8.0"),sQuery(id+"F2.wireOp",EDGE,"E3.27.8.1"),sQuery(id+"F2.wireOp",EDGE,"E3.27.8.2"),sQuery(id+"F2.wireOp",EDGE,"E3.27.8.3"),sQuery(id+"F2.wireOp",EDGE,"E3.27.9.0"),sQuery(id+"F2.wireOp",EDGE,"E3.27.9.1"),sQuery(id+"F2.wireOp",EDGE,"E3.27.9.2"),sQuery(id+"F2.wireOp",EDGE,"E3.27.9.3"),sQuery(id+"F2.wireOp",EDGE,"E3.27.10.0"),sQuery(id+"F2.wireOp",EDGE,"E3.27.10.1"),sQuery(id+"F2.wireOp",EDGE,"E3.27.10.2"),sQuery(id+"F2.wireOp",EDGE,"E3.27.10.3"),sQuery(id+"F2.wireOp",EDGE,"E3.27.11.0"),sQuery(id+"F2.wireOp",EDGE,"E3.27.11.1"),sQuery(id+"F2.wireOp",EDGE,"E3.27.11.2"),sQuery(id+"F2.wireOp",EDGE,"E3.27.11.3"),sQuery(id+"F2.wireOp",EDGE,"E3.27.12.0"),sQuery(id+"F2.wireOp",EDGE,"E3.27.12.1"),sQuery(id+"F2.wireOp",EDGE,"E3.27.12.2"),sQuery(id+"F2.wireOp",EDGE,"E3.27.12.3"),sQuery(id+"F2.wireOp",EDGE,"E3.27.13.0"),sQuery(id+"F2.wireOp",EDGE,"E3.27.13.1"),sQuery(id+"F2.wireOp",EDGE,"E3.27.13.2"),sQuery(id+"F2.wireOp",EDGE,"E3.27.13.3"),sQuery(id+"F2.wireOp",EDGE,"E3.27.14.0"),sQuery(id+"F2.wireOp",EDGE,"E3.27.14.1"),sQuery(id+"F2.wireOp",EDGE,"E3.27.14.2"),sQuery(id+"F2.wireOp",EDGE,"E3.27.14.3"),sQuery(id+"F2.wireOp",EDGE,"E3.27.15.0"),sQuery(id+"F2.wireOp",EDGE,"E3.27.15.1"),sQuery(id+"F2.wireOp",EDGE,"E3.27.15.2"),sQuery(id+"F2.wireOp",EDGE,"E3.27.15.3"),sQuery(id+"F2.wireOp",EDGE,"E3.27.16.0"),sQuery(id+"F2.wireOp",EDGE,"E3.27.16.1"),sQuery(id+"F2.wireOp",EDGE,"E3.27.16.2"),sQuery(id+"F2.wireOp",EDGE,"E3.27.16.3"),sQuery(id+"F2.wireOp",EDGE,"E3.27.17.0"),sQuery(id+"F2.wireOp",EDGE,"E3.27.17.1"),sQuery(id+"F2.wireOp",EDGE,"E3.27.17.2"),sQuery(id+"F2.wireOp",EDGE,"E3.27.17.3"),sQuery(id+"F2.wireOp",EDGE,"E3.27.18.0"),sQuery(id+"F2.wireOp",EDGE,"E3.27.18.1"),sQuery(id+"F2.wireOp",EDGE,"E3.27.18.2"),sQuery(id+"F2.wireOp",EDGE,"E3.27.18.3"),sQuery(id+"F2.wireOp",EDGE,"E3.27.19.0"),sQuery(id+"F2.wireOp",EDGE,"E3.27.19.1"),sQuery(id+"F2.wireOp",EDGE,"E3.27.19.2"),sQuery(id+"F2.wireOp",EDGE,"E3.27.19.3"),sQuery(id+"F2.wireOp",EDGE,"E3.27.20.0"),sQuery(id+"F2.wireOp",EDGE,"E3.27.20.1"),sQuery(id+"F2.wireOp",EDGE,"E3.27.20.2"),sQuery(id+"F2.wireOp",EDGE,"E3.27.20.3"),sQuery(id+"F2.wireOp",EDGE,"E3.27.21.0"),sQuery(id+"F2.wireOp",EDGE,"E3.27.21.1"),sQuery(id+"F2.wireOp",EDGE,"E3.27.21.2"),sQuery(id+"F2.wireOp",EDGE,"E3.27.21.3"),sQuery(id+"F2.wireOp",EDGE,"E3.28.0.0"),sQuery(id+"F2.wireOp",EDGE,"E3.28.0.1"),sQuery(id+"F2.wireOp",EDGE,"E3.28.0.2"),sQuery(id+"F2.wireOp",EDGE,"E3.28.0.3"),sQuery(id+"F2.wireOp",EDGE,"E3.28.1.0"),sQuery(id+"F2.wireOp",EDGE,"E3.28.1.1"),sQuery(id+"F2.wireOp",EDGE,"E3.28.1.2"),sQuery(id+"F2.wireOp",EDGE,"E3.28.1.3"),sQuery(id+"F2.wireOp",EDGE,"E3.28.2.0"),sQuery(id+"F2.wireOp",EDGE,"E3.28.2.1"),sQuery(id+"F2.wireOp",EDGE,"E3.28.2.2"),sQuery(id+"F2.wireOp",EDGE,"E3.28.2.3"),sQuery(id+"F2.wireOp",EDGE,"E3.28.3.0"),sQuery(id+"F2.wireOp",EDGE,"E3.28.3.1"),sQuery(id+"F2.wireOp",EDGE,"E3.28.3.2"),sQuery(id+"F2.wireOp",EDGE,"E3.28.3.3"),sQuery(id+"F2.wireOp",EDGE,"E3.28.4.0"),sQuery(id+"F2.wireOp",EDGE,"E3.28.4.1"),sQuery(id+"F2.wireOp",EDGE,"E3.28.4.2"),sQuery(id+"F2.wireOp",EDGE,"E3.28.4.3"),sQuery(id+"F2.wireOp",EDGE,"E3.28.5.0"),sQuery(id+"F2.wireOp",EDGE,"E3.28.5.1"),sQuery(id+"F2.wireOp",EDGE,"E3.28.5.2"),sQuery(id+"F2.wireOp",EDGE,"E3.28.5.3"),sQuery(id+"F2.wireOp",EDGE,"E3.28.6.0"),sQuery(id+"F2.wireOp",EDGE,"E3.28.6.1"),sQuery(id+"F2.wireOp",EDGE,"E3.28.6.2"),sQuery(id+"F2.wireOp",EDGE,"E3.28.6.3"),sQuery(id+"F2.wireOp",EDGE,"E3.28.7.0"),sQuery(id+"F2.wireOp",EDGE,"E3.28.7.1"),sQuery(id+"F2.wireOp",EDGE,"E3.28.7.2"),sQuery(id+"F2.wireOp",EDGE,"E3.28.7.3"),sQuery(id+"F2.wireOp",EDGE,"E3.28.8.0"),sQuery(id+"F2.wireOp",EDGE,"E3.28.8.1"),sQuery(id+"F2.wireOp",EDGE,"E3.28.8.2"),sQuery(id+"F2.wireOp",EDGE,"E3.28.8.3"),sQuery(id+"F2.wireOp",EDGE,"E3.28.9.0"),sQuery(id+"F2.wireOp",EDGE,"E3.28.9.1"),sQuery(id+"F2.wireOp",EDGE,"E3.28.9.2"),sQuery(id+"F2.wireOp",EDGE,"E3.28.9.3"),sQuery(id+"F2.wireOp",EDGE,"E3.28.10.0"),sQuery(id+"F2.wireOp",EDGE,"E3.28.10.1"),sQuery(id+"F2.wireOp",EDGE,"E3.28.10.2"),sQuery(id+"F2.wireOp",EDGE,"E3.28.10.3"),sQuery(id+"F2.wireOp",EDGE,"E3.28.11.0"),sQuery(id+"F2.wireOp",EDGE,"E3.28.11.1"),sQuery(id+"F2.wireOp",EDGE,"E3.28.11.2"),sQuery(id+"F2.wireOp",EDGE,"E3.28.11.3"),sQuery(id+"F2.wireOp",EDGE,"E3.28.12.0"),sQuery(id+"F2.wireOp",EDGE,"E3.28.12.1"),sQuery(id+"F2.wireOp",EDGE,"E3.28.12.2"),sQuery(id+"F2.wireOp",EDGE,"E3.28.12.3"),sQuery(id+"F2.wireOp",EDGE,"E3.28.13.0"),sQuery(id+"F2.wireOp",EDGE,"E3.28.13.1"),sQuery(id+"F2.wireOp",EDGE,"E3.28.13.2"),sQuery(id+"F2.wireOp",EDGE,"E3.28.13.3"),sQuery(id+"F2.wireOp",EDGE,"E3.28.14.0"),sQuery(id+"F2.wireOp",EDGE,"E3.28.14.1"),sQuery(id+"F2.wireOp",EDGE,"E3.28.14.2"),sQuery(id+"F2.wireOp",EDGE,"E3.28.14.3"),sQuery(id+"F2.wireOp",EDGE,"E3.28.15.0"),sQuery(id+"F2.wireOp",EDGE,"E3.28.15.1"),sQuery(id+"F2.wireOp",EDGE,"E3.28.15.2"),sQuery(id+"F2.wireOp",EDGE,"E3.28.15.3"),sQuery(id+"F2.wireOp",EDGE,"E3.28.16.0"),sQuery(id+"F2.wireOp",EDGE,"E3.28.16.1"),sQuery(id+"F2.wireOp",EDGE,"E3.28.16.2"),sQuery(id+"F2.wireOp",EDGE,"E3.28.16.3"),sQuery(id+"F2.wireOp",EDGE,"E3.28.17.0"),sQuery(id+"F2.wireOp",EDGE,"E3.28.17.1"),sQuery(id+"F2.wireOp",EDGE,"E3.28.17.2"),sQuery(id+"F2.wireOp",EDGE,"E3.28.17.3"),sQuery(id+"F2.wireOp",EDGE,"E3.28.18.0"),sQuery(id+"F2.wireOp",EDGE,"E3.28.18.1"),sQuery(id+"F2.wireOp",EDGE,"E3.28.18.2"),sQuery(id+"F2.wireOp",EDGE,"E3.28.18.3"),sQuery(id+"F2.wireOp",EDGE,"E3.28.19.0"),sQuery(id+"F2.wireOp",EDGE,"E3.28.19.1"),sQuery(id+"F2.wireOp",EDGE,"E3.28.19.2"),sQuery(id+"F2.wireOp",EDGE,"E3.28.19.3"),sQuery(id+"F2.wireOp",EDGE,"E3.28.20.0"),sQuery(id+"F2.wireOp",EDGE,"E3.28.20.1"),sQuery(id+"F2.wireOp",EDGE,"E3.28.20.2"),sQuery(id+"F2.wireOp",EDGE,"E3.28.20.3"),sQuery(id+"F2.wireOp",EDGE,"E3.28.21.0"),sQuery(id+"F2.wireOp",EDGE,"E3.28.21.1"),sQuery(id+"F2.wireOp",EDGE,"E3.28.21.2"),sQuery(id+"F2.wireOp",EDGE,"E3.28.21.3"),sQuery(id+"F2.wireOp",EDGE,"E3.29.0.0"),sQuery(id+"F2.wireOp",EDGE,"E3.29.0.1"),sQuery(id+"F2.wireOp",EDGE,"E3.29.0.2"),sQuery(id+"F2.wireOp",EDGE,"E3.29.0.3"),sQuery(id+"F2.wireOp",EDGE,"E3.29.1.0"),sQuery(id+"F2.wireOp",EDGE,"E3.29.1.1"),sQuery(id+"F2.wireOp",EDGE,"E3.29.1.2"),sQuery(id+"F2.wireOp",EDGE,"E3.29.1.3"),sQuery(id+"F2.wireOp",EDGE,"E3.29.2.0"),sQuery(id+"F2.wireOp",EDGE,"E3.29.2.1"),sQuery(id+"F2.wireOp",EDGE,"E3.29.2.2"),sQuery(id+"F2.wireOp",EDGE,"E3.29.2.3"),sQuery(id+"F2.wireOp",EDGE,"E3.29.3.0"),sQuery(id+"F2.wireOp",EDGE,"E3.29.3.1"),sQuery(id+"F2.wireOp",EDGE,"E3.29.3.2"),sQuery(id+"F2.wireOp",EDGE,"E3.29.3.3"),sQuery(id+"F2.wireOp",EDGE,"E3.29.4.0"),sQuery(id+"F2.wireOp",EDGE,"E3.29.4.1"),sQuery(id+"F2.wireOp",EDGE,"E3.29.4.2"),sQuery(id+"F2.wireOp",EDGE,"E3.29.4.3"),sQuery(id+"F2.wireOp",EDGE,"E3.29.5.0"),sQuery(id+"F2.wireOp",EDGE,"E3.29.5.1"),sQuery(id+"F2.wireOp",EDGE,"E3.29.5.2"),sQuery(id+"F2.wireOp",EDGE,"E3.29.5.3"),sQuery(id+"F2.wireOp",EDGE,"E3.29.6.0"),sQuery(id+"F2.wireOp",EDGE,"E3.29.6.1"),sQuery(id+"F2.wireOp",EDGE,"E3.29.6.2"),sQuery(id+"F2.wireOp",EDGE,"E3.29.6.3"),sQuery(id+"F2.wireOp",EDGE,"E3.29.7.0"),sQuery(id+"F2.wireOp",EDGE,"E3.29.7.1"),sQuery(id+"F2.wireOp",EDGE,"E3.29.7.2"),sQuery(id+"F2.wireOp",EDGE,"E3.29.7.3"),sQuery(id+"F2.wireOp",EDGE,"E3.29.8.0"),sQuery(id+"F2.wireOp",EDGE,"E3.29.8.1"),sQuery(id+"F2.wireOp",EDGE,"E3.29.8.2"),sQuery(id+"F2.wireOp",EDGE,"E3.29.8.3"),sQuery(id+"F2.wireOp",EDGE,"E3.29.9.0"),sQuery(id+"F2.wireOp",EDGE,"E3.29.9.1"),sQuery(id+"F2.wireOp",EDGE,"E3.29.9.2"),sQuery(id+"F2.wireOp",EDGE,"E3.29.9.3"),sQuery(id+"F2.wireOp",EDGE,"E3.29.10.0"),sQuery(id+"F2.wireOp",EDGE,"E3.29.10.1"),sQuery(id+"F2.wireOp",EDGE,"E3.29.10.2"),sQuery(id+"F2.wireOp",EDGE,"E3.29.10.3"),sQuery(id+"F2.wireOp",EDGE,"E3.29.11.0"),sQuery(id+"F2.wireOp",EDGE,"E3.29.11.1"),sQuery(id+"F2.wireOp",EDGE,"E3.29.11.2"),sQuery(id+"F2.wireOp",EDGE,"E3.29.11.3"),sQuery(id+"F2.wireOp",EDGE,"E3.29.12.0"),sQuery(id+"F2.wireOp",EDGE,"E3.29.12.1"),sQuery(id+"F2.wireOp",EDGE,"E3.29.12.2"),sQuery(id+"F2.wireOp",EDGE,"E3.29.12.3"),sQuery(id+"F2.wireOp",EDGE,"E3.29.13.0"),sQuery(id+"F2.wireOp",EDGE,"E3.29.13.1"),sQuery(id+"F2.wireOp",EDGE,"E3.29.13.2"),sQuery(id+"F2.wireOp",EDGE,"E3.29.13.3"),sQuery(id+"F2.wireOp",EDGE,"E3.29.14.0"),sQuery(id+"F2.wireOp",EDGE,"E3.29.14.1"),sQuery(id+"F2.wireOp",EDGE,"E3.29.14.2"),sQuery(id+"F2.wireOp",EDGE,"E3.29.14.3"),sQuery(id+"F2.wireOp",EDGE,"E3.29.15.0"),sQuery(id+"F2.wireOp",EDGE,"E3.29.15.1"),sQuery(id+"F2.wireOp",EDGE,"E3.29.15.2"),sQuery(id+"F2.wireOp",EDGE,"E3.29.15.3"),sQuery(id+"F2.wireOp",EDGE,"E3.29.16.0"),sQuery(id+"F2.wireOp",EDGE,"E3.29.16.1"),sQuery(id+"F2.wireOp",EDGE,"E3.29.16.2"),sQuery(id+"F2.wireOp",EDGE,"E3.29.16.3"),sQuery(id+"F2.wireOp",EDGE,"E3.29.17.0"),sQuery(id+"F2.wireOp",EDGE,"E3.29.17.1"),sQuery(id+"F2.wireOp",EDGE,"E3.29.17.2"),sQuery(id+"F2.wireOp",EDGE,"E3.29.17.3"),sQuery(id+"F2.wireOp",EDGE,"E3.29.18.0"),sQuery(id+"F2.wireOp",EDGE,"E3.29.18.1"),sQuery(id+"F2.wireOp",EDGE,"E3.29.18.2"),sQuery(id+"F2.wireOp",EDGE,"E3.29.18.3"),sQuery(id+"F2.wireOp",EDGE,"E3.29.19.0"),sQuery(id+"F2.wireOp",EDGE,"E3.29.19.1"),sQuery(id+"F2.wireOp",EDGE,"E3.29.19.2"),sQuery(id+"F2.wireOp",EDGE,"E3.29.19.3"),sQuery(id+"F2.wireOp",EDGE,"E3.29.20.0"),sQuery(id+"F2.wireOp",EDGE,"E3.29.20.1"),sQuery(id+"F2.wireOp",EDGE,"E3.29.20.2"),sQuery(id+"F2.wireOp",EDGE,"E3.29.20.3"),sQuery(id+"F2.wireOp",EDGE,"E3.29.21.0"),sQuery(id+"F2.wireOp",EDGE,"E3.29.21.1"),sQuery(id+"F2.wireOp",EDGE,"E3.29.21.2"),sQuery(id+"F2.wireOp",EDGE,"E3.29.21.3"),sQuery(id+"F2.wireOp",EDGE,"E4.filletArc"),sQuery(id+"F2.wireOp",EDGE,"E5.filletArc"),sQuery(id+"F2.wireOp",EDGE,"E6.filletArc"),sQuery(id+"F2.wireOp",EDGE,"E7.filletArc")])],"isStart":false})});
            var sketch = newSketch(context, id + "F4", { "sketchPlane" : qUnion([Q0])});
            skCircle(sketch, "E8", {"center": v(204.4, 278.2) * mm, "radius": 1.2 * mm});
            skSolve(sketch);
        }
        {
            var Q0;
            Q0 = qSketchRegion(id + "F4", true);
            extrude(context, id + "F5", {"entities" : qUnion([Q0]), "operationType" : NewBodyOperationType.REMOVE, "oppositeDirection" : true, "depth" : 6.35 * mm});
        }
        {
            var Q0;
            {var subQ0=sQuery(id+"F0.wireOp",EDGE,"E0.left");var subQ1=sQuery(id+"F0.wireOp",EDGE,"E0.bottom");var subQ2=sQuery(id+"F0.wireOp",EDGE,"E0.top");var subQ3=sQuery(id+"F0.wireOp",EDGE,"E0.right");Q0=makeQuery(id+"F3.boolean.opBoolean","SPLIT",FACE,{"disambiguationData":[TD([makeQuery(id+"F1.opExtrude","SWEPT_FACE",FACE,{"disambiguationData":[OSD([subQ1])]})])],"derivedFrom":makeQuery(id+"F1.opExtrude","CAP_FACE",FACE,{"disambiguationData":[OSD([subQ1,subQ2,subQ0,subQ3])],"isStart":false})});}
            var sketch = newSketch(context, id + "F6", { "sketchPlane" : qUnion([Q0])});
            skLineSegment(sketch, "E9.bottom", {"start": v(0, 304.8) * mm, "end": v(406.4, 304.8) * mm});
            skLineSegment(sketch, "E9.top", {"start": v(0, 300.84) * mm, "end": v(406.4, 300.84) * mm});
            skLineSegment(sketch, "E9.left", {"start": v(0, 304.8) * mm, "end": v(0, 300.84) * mm});
            skLineSegment(sketch, "E9.right", {"start": v(406.4, 304.8) * mm, "end": v(406.4, 300.84) * mm});
            skLineSegment(sketch, "E10.bottom", {"start": v(0, 0) * mm, "end": v(406.4, 0) * mm});
            skLineSegment(sketch, "E10.top", {"start": v(0, 3.96) * mm, "end": v(406.4, 3.96) * mm});
            skLineSegment(sketch, "E10.left", {"start": v(0, 0) * mm, "end": v(0, 3.96) * mm});
            skLineSegment(sketch, "E10.right", {"start": v(406.4, 0) * mm, "end": v(406.4, 3.96) * mm});
            skLineSegment(sketch, "E11.bottom", {"start": v(0, 3.96) * mm, "end": v(3.96, 3.96) * mm});
            skLineSegment(sketch, "E11.top", {"start": v(0, 304.8) * mm, "end": v(3.96, 304.8) * mm});
            skLineSegment(sketch, "E11.left", {"start": v(0, 3.96) * mm, "end": v(0, 304.8) * mm});
            skLineSegment(sketch, "E11.right", {"start": v(3.96, 3.96) * mm, "end": v(3.96, 304.8) * mm});
            skLineSegment(sketch, "E12.bottom", {"start": v(406.4, 3.96) * mm, "end": v(402.44, 3.96) * mm});
            skLineSegment(sketch, "E12.top", {"start": v(406.4, 300.84) * mm, "end": v(402.44, 300.84) * mm});
            skLineSegment(sketch, "E12.left", {"start": v(406.4, 3.96) * mm, "end": v(406.4, 300.84) * mm});
            skLineSegment(sketch, "E12.right", {"start": v(402.44, 3.96) * mm, "end": v(402.44, 300.84) * mm});
            skSolve(sketch);
        }
        {
            var Q0;
            Q0 = qSketchRegion(id + "F6", true);
            extrude(context, id + "F7", {"entities" : qUnion([Q0]), "operationType" : NewBodyOperationType.REMOVE, "oppositeDirection" : true, "depth" : 15.88 * mm});
        }
        {
            var Q0;
            Q0=makeQuery(id+"F7.boolean.opBoolean","COPY",FACE,{"derivedFrom":makeQuery(id+"F7.opExtrude","SWEPT_FACE",FACE,{"disambiguationData":[OSD([sQuery(id+"F6.wireOp",EDGE,"E9.top")])]})});
            var sketch = newSketch(context, id + "F8", { "sketchPlane" : qUnion([Q0])});
            skCircle(sketch, "E13", {"center": v(-204.4, 11.13) * mm, "radius": 5.08 * mm});
            skSolve(sketch);
        }
        {
            var Q0;
            Q0 = qSketchRegion(id + "F8", true);
            extrude(context, id + "F9", {"entities" : qUnion([Q0]), "operationType" : NewBodyOperationType.REMOVE, "oppositeDirection" : true, "depth" : 6.35 * mm});
        }
        {
            var Q0;
            Q0=makeQuery(id+"F9.boolean.opBoolean","COPY",FACE,{"derivedFrom":makeQuery(id+"F9.opExtrude","CAP_FACE",FACE,{"disambiguationData":[OSD([sQuery(id+"F8.wireOp",EDGE,"E13")])],"isStart":false})});
            var sketch = newSketch(context, id + "F10", { "sketchPlane" : qUnion([Q0])});
            skCircle(sketch, "E14", {"center": v(-204.4, 11.13) * mm, "radius": 3.18 * mm});
            skSolve(sketch);
        }
        {
            var Q0;
            Q0 = qSketchRegion(id + "F10", true);
            extrude(context, id + "F11", {"entities" : qUnion([Q0]), "operationType" : NewBodyOperationType.REMOVE, "oppositeDirection" : true, "depth" : 19.05 * mm});
        }
    });
